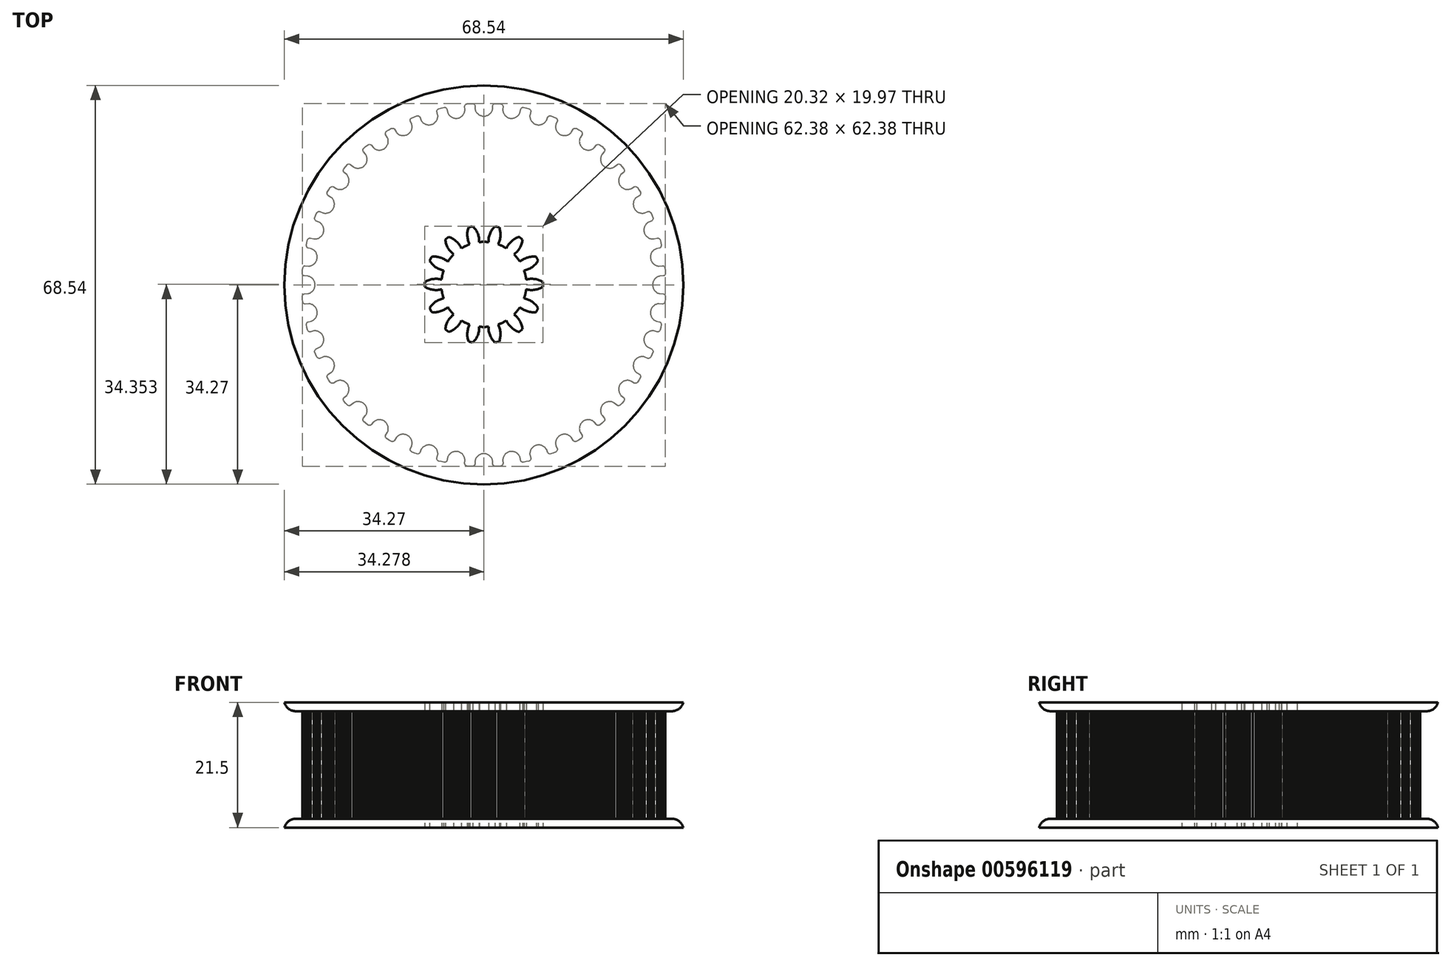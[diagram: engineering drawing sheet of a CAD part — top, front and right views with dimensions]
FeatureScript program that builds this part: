
annotation { "Feature Type Name" : "Feature", "Feature Type Description" : "" }
export const myFeature = defineFeature(function(context is Context, id is Id, definition is map)
    precondition{}
    {
        {
            assignVariable(context, id + "F0", {"name" : "totalThick", "anyValue" : 21.5});
        }
        {
            assignVariable(context, id + "F1", {"name" : "idlerThick", "anyValue" : 1.5});
        }
        {
            assignVariable(context, id + "F2", {"name" : "filletSize", "anyValue" : 2});
        }
        {
            var Q0;
            Q0=qCreatedBy(makeId("Top.planeOp"),FACE);
            var sketch = newSketch(context, id + "F3", { "sketchPlane" : qUnion([Q0])});
            skLineSegment(sketch, "E0", {"start": v(2.45, -31.16) * mm, "end": v(2.94, -31.12) * mm});
            skLineSegment(sketch, "E1", {"start": v(2.94, -31.12) * mm, "end": v(3.07, -31.07) * mm});
            skLineSegment(sketch, "E2", {"start": v(3.07, -31.07) * mm, "end": v(3.19, -30.98) * mm});
            skLineSegment(sketch, "E3", {"start": v(3.19, -30.98) * mm, "end": v(3.27, -30.85) * mm});
            skLineSegment(sketch, "E4", {"start": v(3.27, -30.85) * mm, "end": v(3.3, -30.7) * mm});
            skLineSegment(sketch, "E5", {"start": v(3.3, -30.7) * mm, "end": v(3.25, -30.1) * mm});
            skLineSegment(sketch, "E6", {"start": v(3.25, -30.1) * mm, "end": v(3.26, -29.97) * mm});
            skLineSegment(sketch, "E7", {"start": v(3.26, -29.97) * mm, "end": v(3.28, -29.84) * mm});
            skLineSegment(sketch, "E8", {"start": v(3.28, -29.84) * mm, "end": v(3.3, -29.71) * mm});
            skLineSegment(sketch, "E9", {"start": v(3.3, -29.71) * mm, "end": v(3.35, -29.6) * mm});
            skLineSegment(sketch, "E10", {"start": v(3.35, -29.6) * mm, "end": v(3.4, -29.47) * mm});
            skLineSegment(sketch, "E11", {"start": v(3.4, -29.47) * mm, "end": v(3.47, -29.36) * mm});
            skLineSegment(sketch, "E12", {"start": v(3.47, -29.36) * mm, "end": v(3.54, -29.26) * mm});
            skLineSegment(sketch, "E13", {"start": v(3.54, -29.26) * mm, "end": v(3.62, -29.16) * mm});
            skLineSegment(sketch, "E14", {"start": v(3.62, -29.16) * mm, "end": v(3.71, -29.06) * mm});
            skLineSegment(sketch, "E15", {"start": v(3.71, -29.06) * mm, "end": v(3.81, -28.98) * mm});
            skLineSegment(sketch, "E16", {"start": v(3.81, -28.98) * mm, "end": v(3.92, -28.9) * mm});
            skLineSegment(sketch, "E17", {"start": v(3.92, -28.9) * mm, "end": v(4.03, -28.83) * mm});
            skLineSegment(sketch, "E18", {"start": v(4.03, -28.83) * mm, "end": v(4.15, -28.77) * mm});
            skLineSegment(sketch, "E19", {"start": v(4.15, -28.77) * mm, "end": v(4.27, -28.71) * mm});
            skLineSegment(sketch, "E20", {"start": v(4.27, -28.71) * mm, "end": v(4.4, -28.67) * mm});
            skLineSegment(sketch, "E21", {"start": v(4.4, -28.67) * mm, "end": v(4.54, -28.64) * mm});
            skLineSegment(sketch, "E22", {"start": v(4.54, -28.64) * mm, "end": v(4.67, -28.63) * mm});
            skLineSegment(sketch, "E23", {"start": v(4.67, -28.63) * mm, "end": v(4.81, -28.63) * mm});
            skLineSegment(sketch, "E24", {"start": v(4.81, -28.63) * mm, "end": v(4.95, -28.64) * mm});
            skLineSegment(sketch, "E25", {"start": v(4.95, -28.64) * mm, "end": v(5.08, -28.66) * mm});
            skLineSegment(sketch, "E26", {"start": v(5.08, -28.66) * mm, "end": v(5.2, -28.7) * mm});
            skLineSegment(sketch, "E27", {"start": v(5.2, -28.7) * mm, "end": v(5.33, -28.74) * mm});
            skLineSegment(sketch, "E28", {"start": v(5.33, -28.74) * mm, "end": v(5.45, -28.79) * mm});
            skLineSegment(sketch, "E29", {"start": v(5.45, -28.79) * mm, "end": v(5.56, -28.85) * mm});
            skLineSegment(sketch, "E30", {"start": v(5.56, -28.85) * mm, "end": v(5.67, -28.92) * mm});
            skLineSegment(sketch, "E31", {"start": v(5.67, -28.92) * mm, "end": v(5.77, -29) * mm});
            skLineSegment(sketch, "E32", {"start": v(5.77, -29) * mm, "end": v(5.87, -29.08) * mm});
            skLineSegment(sketch, "E33", {"start": v(5.87, -29.08) * mm, "end": v(5.96, -29.18) * mm});
            skLineSegment(sketch, "E34", {"start": v(5.96, -29.18) * mm, "end": v(6.03, -29.28) * mm});
            skLineSegment(sketch, "E35", {"start": v(6.03, -29.28) * mm, "end": v(6.1, -29.39) * mm});
            skLineSegment(sketch, "E36", {"start": v(6.1, -29.39) * mm, "end": v(6.16, -29.5) * mm});
            skLineSegment(sketch, "E37", {"start": v(6.16, -29.5) * mm, "end": v(6.21, -29.63) * mm});
            skLineSegment(sketch, "E38", {"start": v(6.21, -29.63) * mm, "end": v(6.35, -30.22) * mm});
            skLineSegment(sketch, "E39", {"start": v(6.35, -30.22) * mm, "end": v(6.43, -30.35) * mm});
            skLineSegment(sketch, "E40", {"start": v(6.43, -30.35) * mm, "end": v(6.54, -30.45) * mm});
            skLineSegment(sketch, "E41", {"start": v(6.54, -30.45) * mm, "end": v(6.69, -30.5) * mm});
            skLineSegment(sketch, "E42", {"start": v(6.69, -30.5) * mm, "end": v(6.82, -30.5) * mm});
            skLineSegment(sketch, "E43", {"start": v(6.82, -30.5) * mm, "end": v(7.3, -30.4) * mm});
            skLineSegment(sketch, "E44", {"start": v(7.3, -30.4) * mm, "end": v(7.77, -30.27) * mm});
            skLineSegment(sketch, "E45", {"start": v(7.77, -30.27) * mm, "end": v(7.89, -30.21) * mm});
            skLineSegment(sketch, "E46", {"start": v(7.89, -30.21) * mm, "end": v(8, -30.1) * mm});
            skLineSegment(sketch, "E47", {"start": v(8, -30.1) * mm, "end": v(8.05, -29.96) * mm});
            skLineSegment(sketch, "E48", {"start": v(8.05, -29.96) * mm, "end": v(8.06, -29.8) * mm});
            skLineSegment(sketch, "E49", {"start": v(8.06, -29.8) * mm, "end": v(7.91, -29.22) * mm});
            skLineSegment(sketch, "E50", {"start": v(7.91, -29.22) * mm, "end": v(7.9, -29.09) * mm});
            skLineSegment(sketch, "E51", {"start": v(7.9, -29.09) * mm, "end": v(7.9, -28.96) * mm});
            skLineSegment(sketch, "E52", {"start": v(7.9, -28.96) * mm, "end": v(7.92, -28.83) * mm});
            skLineSegment(sketch, "E53", {"start": v(7.92, -28.83) * mm, "end": v(7.94, -28.7) * mm});
            skLineSegment(sketch, "E54", {"start": v(7.94, -28.7) * mm, "end": v(7.97, -28.58) * mm});
            skLineSegment(sketch, "E55", {"start": v(7.97, -28.58) * mm, "end": v(8.02, -28.46) * mm});
            skLineSegment(sketch, "E56", {"start": v(8.02, -28.46) * mm, "end": v(8.07, -28.34) * mm});
            skLineSegment(sketch, "E57", {"start": v(8.07, -28.34) * mm, "end": v(8.14, -28.23) * mm});
            skLineSegment(sketch, "E58", {"start": v(8.14, -28.23) * mm, "end": v(8.21, -28.12) * mm});
            skLineSegment(sketch, "E59", {"start": v(8.21, -28.12) * mm, "end": v(8.3, -28.02) * mm});
            skLineSegment(sketch, "E60", {"start": v(8.3, -28.02) * mm, "end": v(8.39, -27.93) * mm});
            skLineSegment(sketch, "E61", {"start": v(8.39, -27.93) * mm, "end": v(8.49, -27.84) * mm});
            skLineSegment(sketch, "E62", {"start": v(8.49, -27.84) * mm, "end": v(8.6, -27.76) * mm});
            skLineSegment(sketch, "E63", {"start": v(8.6, -27.76) * mm, "end": v(8.71, -27.7) * mm});
            skLineSegment(sketch, "E64", {"start": v(8.71, -27.7) * mm, "end": v(8.83, -27.63) * mm});
            skLineSegment(sketch, "E65", {"start": v(8.83, -27.63) * mm, "end": v(8.96, -27.58) * mm});
            skLineSegment(sketch, "E66", {"start": v(8.96, -27.58) * mm, "end": v(9.1, -27.55) * mm});
            skLineSegment(sketch, "E67", {"start": v(9.1, -27.55) * mm, "end": v(9.23, -27.52) * mm});
            skLineSegment(sketch, "E68", {"start": v(9.23, -27.52) * mm, "end": v(9.36, -27.51) * mm});
            skLineSegment(sketch, "E69", {"start": v(9.36, -27.51) * mm, "end": v(9.5, -27.51) * mm});
            skLineSegment(sketch, "E70", {"start": v(9.5, -27.51) * mm, "end": v(9.63, -27.53) * mm});
            skLineSegment(sketch, "E71", {"start": v(9.63, -27.53) * mm, "end": v(9.76, -27.55) * mm});
            skLineSegment(sketch, "E72", {"start": v(9.76, -27.55) * mm, "end": v(9.89, -27.58) * mm});
            skLineSegment(sketch, "E73", {"start": v(9.89, -27.58) * mm, "end": v(10, -27.62) * mm});
            skLineSegment(sketch, "E74", {"start": v(10, -27.62) * mm, "end": v(10.13, -27.67) * mm});
            skLineSegment(sketch, "E75", {"start": v(10.13, -27.67) * mm, "end": v(10.24, -27.74) * mm});
            skLineSegment(sketch, "E76", {"start": v(10.24, -27.74) * mm, "end": v(10.35, -27.8) * mm});
            skLineSegment(sketch, "E77", {"start": v(10.35, -27.8) * mm, "end": v(10.45, -27.89) * mm});
            skLineSegment(sketch, "E78", {"start": v(10.45, -27.89) * mm, "end": v(10.54, -27.98) * mm});
            skLineSegment(sketch, "E79", {"start": v(10.54, -27.98) * mm, "end": v(10.63, -28.07) * mm});
            skLineSegment(sketch, "E80", {"start": v(10.63, -28.07) * mm, "end": v(10.7, -28.18) * mm});
            skLineSegment(sketch, "E81", {"start": v(10.7, -28.18) * mm, "end": v(10.77, -28.3) * mm});
            skLineSegment(sketch, "E82", {"start": v(10.77, -28.3) * mm, "end": v(11, -28.85) * mm});
            skLineSegment(sketch, "E83", {"start": v(11, -28.85) * mm, "end": v(11.1, -28.97) * mm});
            skLineSegment(sketch, "E84", {"start": v(11.1, -28.97) * mm, "end": v(11.23, -29.05) * mm});
            skLineSegment(sketch, "E85", {"start": v(11.23, -29.05) * mm, "end": v(11.38, -29.08) * mm});
            skLineSegment(sketch, "E86", {"start": v(11.38, -29.08) * mm, "end": v(11.5, -29.06) * mm});
            skLineSegment(sketch, "E87", {"start": v(11.5, -29.06) * mm, "end": v(11.96, -28.88) * mm});
            skLineSegment(sketch, "E88", {"start": v(11.96, -28.88) * mm, "end": v(12.4, -28.68) * mm});
            skLineSegment(sketch, "E89", {"start": v(12.4, -28.68) * mm, "end": v(12.52, -28.6) * mm});
            skLineSegment(sketch, "E90", {"start": v(12.52, -28.6) * mm, "end": v(12.6, -28.48) * mm});
            skLineSegment(sketch, "E91", {"start": v(12.6, -28.48) * mm, "end": v(12.64, -28.33) * mm});
            skLineSegment(sketch, "E92", {"start": v(12.64, -28.33) * mm, "end": v(12.62, -28.18) * mm});
            skLineSegment(sketch, "E93", {"start": v(12.62, -28.18) * mm, "end": v(12.39, -27.62) * mm});
            skLineSegment(sketch, "E94", {"start": v(12.39, -27.62) * mm, "end": v(12.36, -27.5) * mm});
            skLineSegment(sketch, "E95", {"start": v(12.36, -27.5) * mm, "end": v(12.34, -27.36) * mm});
            skLineSegment(sketch, "E96", {"start": v(12.34, -27.36) * mm, "end": v(12.33, -27.24) * mm});
            skLineSegment(sketch, "E97", {"start": v(12.33, -27.24) * mm, "end": v(12.33, -27.1) * mm});
            skLineSegment(sketch, "E98", {"start": v(12.33, -27.1) * mm, "end": v(12.35, -26.98) * mm});
            skLineSegment(sketch, "E99", {"start": v(12.35, -26.98) * mm, "end": v(12.37, -26.85) * mm});
            skLineSegment(sketch, "E100", {"start": v(12.37, -26.85) * mm, "end": v(12.4, -26.73) * mm});
            skLineSegment(sketch, "E101", {"start": v(12.4, -26.73) * mm, "end": v(12.46, -26.6) * mm});
            skLineSegment(sketch, "E102", {"start": v(12.46, -26.6) * mm, "end": v(12.51, -26.5) * mm});
            skLineSegment(sketch, "E103", {"start": v(12.51, -26.5) * mm, "end": v(12.58, -26.38) * mm});
            skLineSegment(sketch, "E104", {"start": v(12.58, -26.38) * mm, "end": v(12.65, -26.27) * mm});
            skLineSegment(sketch, "E105", {"start": v(12.65, -26.27) * mm, "end": v(12.74, -26.17) * mm});
            skLineSegment(sketch, "E106", {"start": v(12.74, -26.17) * mm, "end": v(12.83, -26.08) * mm});
            skLineSegment(sketch, "E107", {"start": v(12.83, -26.08) * mm, "end": v(12.94, -25.99) * mm});
            skLineSegment(sketch, "E108", {"start": v(12.94, -25.99) * mm, "end": v(13.05, -25.9) * mm});
            skLineSegment(sketch, "E109", {"start": v(13.05, -25.9) * mm, "end": v(13.16, -25.84) * mm});
            skLineSegment(sketch, "E110", {"start": v(13.16, -25.84) * mm, "end": v(13.3, -25.78) * mm});
            skLineSegment(sketch, "E111", {"start": v(13.3, -25.78) * mm, "end": v(13.42, -25.74) * mm});
            skLineSegment(sketch, "E112", {"start": v(13.42, -25.74) * mm, "end": v(13.55, -25.7) * mm});
            skLineSegment(sketch, "E113", {"start": v(13.55, -25.7) * mm, "end": v(13.69, -25.69) * mm});
            skLineSegment(sketch, "E114", {"start": v(13.69, -25.69) * mm, "end": v(13.82, -25.68) * mm});
            skLineSegment(sketch, "E115", {"start": v(13.82, -25.68) * mm, "end": v(13.95, -25.68) * mm});
            skLineSegment(sketch, "E116", {"start": v(13.95, -25.68) * mm, "end": v(14.08, -25.7) * mm});
            skLineSegment(sketch, "E117", {"start": v(14.08, -25.7) * mm, "end": v(14.2, -25.72) * mm});
            skLineSegment(sketch, "E118", {"start": v(14.2, -25.72) * mm, "end": v(14.33, -25.75) * mm});
            skLineSegment(sketch, "E119", {"start": v(14.33, -25.75) * mm, "end": v(14.45, -25.8) * mm});
            skLineSegment(sketch, "E120", {"start": v(14.45, -25.8) * mm, "end": v(14.57, -25.85) * mm});
            skLineSegment(sketch, "E121", {"start": v(14.57, -25.85) * mm, "end": v(14.68, -25.9) * mm});
            skLineSegment(sketch, "E122", {"start": v(14.68, -25.9) * mm, "end": v(14.79, -25.98) * mm});
            skLineSegment(sketch, "E123", {"start": v(14.79, -25.98) * mm, "end": v(14.89, -26.06) * mm});
            skLineSegment(sketch, "E124", {"start": v(14.89, -26.06) * mm, "end": v(14.98, -26.16) * mm});
            skLineSegment(sketch, "E125", {"start": v(14.98, -26.16) * mm, "end": v(15.07, -26.26) * mm});
            skLineSegment(sketch, "E126", {"start": v(15.07, -26.26) * mm, "end": v(15.38, -26.78) * mm});
            skLineSegment(sketch, "E127", {"start": v(15.38, -26.78) * mm, "end": v(15.5, -26.88) * mm});
            skLineSegment(sketch, "E128", {"start": v(15.5, -26.88) * mm, "end": v(15.63, -26.93) * mm});
            skLineSegment(sketch, "E129", {"start": v(15.63, -26.93) * mm, "end": v(15.78, -26.94) * mm});
            skLineSegment(sketch, "E130", {"start": v(15.78, -26.94) * mm, "end": v(15.91, -26.9) * mm});
            skLineSegment(sketch, "E131", {"start": v(15.91, -26.9) * mm, "end": v(16.33, -26.65) * mm});
            skLineSegment(sketch, "E132", {"start": v(16.33, -26.65) * mm, "end": v(16.74, -26.4) * mm});
            skLineSegment(sketch, "E133", {"start": v(16.74, -26.4) * mm, "end": v(16.84, -26.3) * mm});
            skLineSegment(sketch, "E134", {"start": v(16.84, -26.3) * mm, "end": v(16.9, -26.16) * mm});
            skLineSegment(sketch, "E135", {"start": v(16.9, -26.16) * mm, "end": v(16.92, -26) * mm});
            skLineSegment(sketch, "E136", {"start": v(16.92, -26) * mm, "end": v(16.88, -25.86) * mm});
            skLineSegment(sketch, "E137", {"start": v(16.88, -25.86) * mm, "end": v(16.56, -25.34) * mm});
            skLineSegment(sketch, "E138", {"start": v(16.56, -25.34) * mm, "end": v(16.5, -25.22) * mm});
            skLineSegment(sketch, "E139", {"start": v(16.5, -25.22) * mm, "end": v(16.47, -25.1) * mm});
            skLineSegment(sketch, "E140", {"start": v(16.47, -25.1) * mm, "end": v(16.44, -24.97) * mm});
            skLineSegment(sketch, "E141", {"start": v(16.44, -24.97) * mm, "end": v(16.42, -24.84) * mm});
            skLineSegment(sketch, "E142", {"start": v(16.42, -24.84) * mm, "end": v(16.42, -24.71) * mm});
            skLineSegment(sketch, "E143", {"start": v(16.42, -24.71) * mm, "end": v(16.42, -24.59) * mm});
            skLineSegment(sketch, "E144", {"start": v(16.42, -24.59) * mm, "end": v(16.44, -24.46) * mm});
            skLineSegment(sketch, "E145", {"start": v(16.44, -24.46) * mm, "end": v(16.46, -24.33) * mm});
            skLineSegment(sketch, "E146", {"start": v(16.46, -24.33) * mm, "end": v(16.5, -24.2) * mm});
            skLineSegment(sketch, "E147", {"start": v(16.5, -24.2) * mm, "end": v(16.55, -24.09) * mm});
            skLineSegment(sketch, "E148", {"start": v(16.55, -24.09) * mm, "end": v(16.6, -23.97) * mm});
            skLineSegment(sketch, "E149", {"start": v(16.6, -23.97) * mm, "end": v(16.68, -23.86) * mm});
            skLineSegment(sketch, "E150", {"start": v(16.68, -23.86) * mm, "end": v(16.75, -23.75) * mm});
            skLineSegment(sketch, "E151", {"start": v(16.75, -23.75) * mm, "end": v(16.84, -23.65) * mm});
            skLineSegment(sketch, "E152", {"start": v(16.84, -23.65) * mm, "end": v(16.94, -23.55) * mm});
            skLineSegment(sketch, "E153", {"start": v(16.94, -23.55) * mm, "end": v(17.04, -23.46) * mm});
            skLineSegment(sketch, "E154", {"start": v(17.04, -23.46) * mm, "end": v(17.16, -23.39) * mm});
            skLineSegment(sketch, "E155", {"start": v(17.16, -23.39) * mm, "end": v(17.28, -23.32) * mm});
            skLineSegment(sketch, "E156", {"start": v(17.28, -23.32) * mm, "end": v(17.4, -23.27) * mm});
            skLineSegment(sketch, "E157", {"start": v(17.4, -23.27) * mm, "end": v(17.54, -23.23) * mm});
            skLineSegment(sketch, "E158", {"start": v(17.54, -23.23) * mm, "end": v(17.66, -23.2) * mm});
            skLineSegment(sketch, "E159", {"start": v(17.66, -23.2) * mm, "end": v(17.8, -23.18) * mm});
            skLineSegment(sketch, "E160", {"start": v(17.8, -23.18) * mm, "end": v(17.92, -23.18) * mm});
            skLineSegment(sketch, "E161", {"start": v(17.92, -23.18) * mm, "end": v(18.05, -23.18) * mm});
            skLineSegment(sketch, "E162", {"start": v(18.05, -23.18) * mm, "end": v(18.18, -23.2) * mm});
            skLineSegment(sketch, "E163", {"start": v(18.18, -23.2) * mm, "end": v(18.3, -23.21) * mm});
            skLineSegment(sketch, "E164", {"start": v(18.3, -23.21) * mm, "end": v(18.43, -23.25) * mm});
            skLineSegment(sketch, "E165", {"start": v(18.43, -23.25) * mm, "end": v(18.55, -23.3) * mm});
            skLineSegment(sketch, "E166", {"start": v(18.55, -23.3) * mm, "end": v(18.67, -23.35) * mm});
            skLineSegment(sketch, "E167", {"start": v(18.67, -23.35) * mm, "end": v(18.78, -23.41) * mm});
            skLineSegment(sketch, "E168", {"start": v(18.78, -23.41) * mm, "end": v(18.89, -23.5) * mm});
            skLineSegment(sketch, "E169", {"start": v(18.89, -23.5) * mm, "end": v(18.99, -23.58) * mm});
            skLineSegment(sketch, "E170", {"start": v(18.99, -23.58) * mm, "end": v(19.38, -24.04) * mm});
            skLineSegment(sketch, "E171", {"start": v(19.38, -24.04) * mm, "end": v(19.5, -24.13) * mm});
            skLineSegment(sketch, "E172", {"start": v(19.5, -24.13) * mm, "end": v(19.65, -24.16) * mm});
            skLineSegment(sketch, "E173", {"start": v(19.65, -24.16) * mm, "end": v(19.8, -24.14) * mm});
            skLineSegment(sketch, "E174", {"start": v(19.8, -24.14) * mm, "end": v(19.92, -24.08) * mm});
            skLineSegment(sketch, "E175", {"start": v(19.92, -24.08) * mm, "end": v(20.3, -23.77) * mm});
            skLineSegment(sketch, "E176", {"start": v(20.3, -23.77) * mm, "end": v(20.67, -23.45) * mm});
            skLineSegment(sketch, "E177", {"start": v(20.67, -23.45) * mm, "end": v(20.74, -23.34) * mm});
            skLineSegment(sketch, "E178", {"start": v(20.74, -23.34) * mm, "end": v(20.79, -23.19) * mm});
            skLineSegment(sketch, "E179", {"start": v(20.79, -23.19) * mm, "end": v(20.78, -23.04) * mm});
            skLineSegment(sketch, "E180", {"start": v(20.78, -23.04) * mm, "end": v(20.72, -22.9) * mm});
            skLineSegment(sketch, "E181", {"start": v(20.72, -22.9) * mm, "end": v(20.32, -22.44) * mm});
            skLineSegment(sketch, "E182", {"start": v(20.32, -22.44) * mm, "end": v(20.25, -22.33) * mm});
            skLineSegment(sketch, "E183", {"start": v(20.25, -22.33) * mm, "end": v(20.19, -22.21) * mm});
            skLineSegment(sketch, "E184", {"start": v(20.19, -22.21) * mm, "end": v(20.14, -22.1) * mm});
            skLineSegment(sketch, "E185", {"start": v(20.14, -22.1) * mm, "end": v(20.1, -21.97) * mm});
            skLineSegment(sketch, "E186", {"start": v(20.1, -21.97) * mm, "end": v(20.08, -21.84) * mm});
            skLineSegment(sketch, "E187", {"start": v(20.08, -21.84) * mm, "end": v(20.07, -21.72) * mm});
            skLineSegment(sketch, "E188", {"start": v(20.07, -21.72) * mm, "end": v(20.06, -21.59) * mm});
            skLineSegment(sketch, "E189", {"start": v(20.06, -21.59) * mm, "end": v(20.07, -21.46) * mm});
            skLineSegment(sketch, "E190", {"start": v(20.07, -21.46) * mm, "end": v(20.09, -21.33) * mm});
            skLineSegment(sketch, "E191", {"start": v(20.09, -21.33) * mm, "end": v(20.11, -21.2) * mm});
            skLineSegment(sketch, "E192", {"start": v(20.11, -21.2) * mm, "end": v(20.15, -21.08) * mm});
            skLineSegment(sketch, "E193", {"start": v(20.15, -21.08) * mm, "end": v(20.2, -20.95) * mm});
            skLineSegment(sketch, "E194", {"start": v(20.2, -20.95) * mm, "end": v(20.26, -20.84) * mm});
            skLineSegment(sketch, "E195", {"start": v(20.26, -20.84) * mm, "end": v(20.33, -20.72) * mm});
            skLineSegment(sketch, "E196", {"start": v(20.33, -20.72) * mm, "end": v(20.41, -20.6) * mm});
            skLineSegment(sketch, "E197", {"start": v(20.41, -20.6) * mm, "end": v(20.5, -20.5) * mm});
            skLineSegment(sketch, "E198", {"start": v(20.5, -20.5) * mm, "end": v(20.6, -20.41) * mm});
            skLineSegment(sketch, "E199", {"start": v(20.6, -20.41) * mm, "end": v(20.72, -20.33) * mm});
            skLineSegment(sketch, "E200", {"start": v(20.72, -20.33) * mm, "end": v(20.83, -20.26) * mm});
            skLineSegment(sketch, "E201", {"start": v(20.83, -20.26) * mm, "end": v(20.95, -20.2) * mm});
            skLineSegment(sketch, "E202", {"start": v(20.95, -20.2) * mm, "end": v(21.08, -20.15) * mm});
            skLineSegment(sketch, "E203", {"start": v(21.08, -20.15) * mm, "end": v(21.2, -20.11) * mm});
            skLineSegment(sketch, "E204", {"start": v(21.2, -20.11) * mm, "end": v(21.33, -20.09) * mm});
            skLineSegment(sketch, "E205", {"start": v(21.33, -20.09) * mm, "end": v(21.46, -20.07) * mm});
            skLineSegment(sketch, "E206", {"start": v(21.46, -20.07) * mm, "end": v(21.59, -20.06) * mm});
            skLineSegment(sketch, "E207", {"start": v(21.59, -20.06) * mm, "end": v(21.72, -20.06) * mm});
            skLineSegment(sketch, "E208", {"start": v(21.72, -20.06) * mm, "end": v(21.84, -20.08) * mm});
            skLineSegment(sketch, "E209", {"start": v(21.84, -20.08) * mm, "end": v(21.97, -20.1) * mm});
            skLineSegment(sketch, "E210", {"start": v(21.97, -20.1) * mm, "end": v(22.1, -20.14) * mm});
            skLineSegment(sketch, "E211", {"start": v(22.1, -20.14) * mm, "end": v(22.21, -20.19) * mm});
            skLineSegment(sketch, "E212", {"start": v(22.21, -20.19) * mm, "end": v(22.33, -20.25) * mm});
            skLineSegment(sketch, "E213", {"start": v(22.33, -20.25) * mm, "end": v(22.44, -20.32) * mm});
            skLineSegment(sketch, "E214", {"start": v(22.44, -20.32) * mm, "end": v(22.9, -20.72) * mm});
            skLineSegment(sketch, "E215", {"start": v(22.9, -20.72) * mm, "end": v(23.04, -20.78) * mm});
            skLineSegment(sketch, "E216", {"start": v(23.04, -20.78) * mm, "end": v(23.19, -20.79) * mm});
            skLineSegment(sketch, "E217", {"start": v(23.19, -20.79) * mm, "end": v(23.34, -20.74) * mm});
            skLineSegment(sketch, "E218", {"start": v(23.34, -20.74) * mm, "end": v(23.45, -20.67) * mm});
            skLineSegment(sketch, "E219", {"start": v(23.45, -20.67) * mm, "end": v(23.77, -20.3) * mm});
            skLineSegment(sketch, "E220", {"start": v(23.77, -20.3) * mm, "end": v(24.08, -19.92) * mm});
            skLineSegment(sketch, "E221", {"start": v(24.08, -19.92) * mm, "end": v(24.14, -19.8) * mm});
            skLineSegment(sketch, "E222", {"start": v(24.14, -19.8) * mm, "end": v(24.16, -19.65) * mm});
            skLineSegment(sketch, "E223", {"start": v(24.16, -19.65) * mm, "end": v(24.13, -19.5) * mm});
            skLineSegment(sketch, "E224", {"start": v(24.13, -19.5) * mm, "end": v(24.04, -19.38) * mm});
            skLineSegment(sketch, "E225", {"start": v(24.04, -19.38) * mm, "end": v(23.58, -18.99) * mm});
            skLineSegment(sketch, "E226", {"start": v(23.58, -18.99) * mm, "end": v(23.5, -18.89) * mm});
            skLineSegment(sketch, "E227", {"start": v(23.5, -18.89) * mm, "end": v(23.42, -18.78) * mm});
            skLineSegment(sketch, "E228", {"start": v(23.42, -18.78) * mm, "end": v(23.35, -18.67) * mm});
            skLineSegment(sketch, "E229", {"start": v(23.35, -18.67) * mm, "end": v(23.3, -18.55) * mm});
            skLineSegment(sketch, "E230", {"start": v(23.3, -18.55) * mm, "end": v(23.25, -18.43) * mm});
            skLineSegment(sketch, "E231", {"start": v(23.25, -18.43) * mm, "end": v(23.21, -18.3) * mm});
            skLineSegment(sketch, "E232", {"start": v(23.21, -18.3) * mm, "end": v(23.2, -18.18) * mm});
            skLineSegment(sketch, "E233", {"start": v(23.2, -18.18) * mm, "end": v(23.18, -18.05) * mm});
            skLineSegment(sketch, "E234", {"start": v(23.18, -18.05) * mm, "end": v(23.18, -17.92) * mm});
            skLineSegment(sketch, "E235", {"start": v(23.18, -17.92) * mm, "end": v(23.18, -17.8) * mm});
            skLineSegment(sketch, "E236", {"start": v(23.18, -17.8) * mm, "end": v(23.2, -17.66) * mm});
            skLineSegment(sketch, "E237", {"start": v(23.2, -17.66) * mm, "end": v(23.23, -17.54) * mm});
            skLineSegment(sketch, "E238", {"start": v(23.23, -17.54) * mm, "end": v(23.27, -17.4) * mm});
            skLineSegment(sketch, "E239", {"start": v(23.27, -17.4) * mm, "end": v(23.32, -17.28) * mm});
            skLineSegment(sketch, "E240", {"start": v(23.32, -17.28) * mm, "end": v(23.39, -17.16) * mm});
            skLineSegment(sketch, "E241", {"start": v(23.39, -17.16) * mm, "end": v(23.46, -17.04) * mm});
            skLineSegment(sketch, "E242", {"start": v(23.46, -17.04) * mm, "end": v(23.55, -16.94) * mm});
            skLineSegment(sketch, "E243", {"start": v(23.55, -16.94) * mm, "end": v(23.65, -16.84) * mm});
            skLineSegment(sketch, "E244", {"start": v(23.65, -16.84) * mm, "end": v(23.75, -16.75) * mm});
            skLineSegment(sketch, "E245", {"start": v(23.75, -16.75) * mm, "end": v(23.86, -16.68) * mm});
            skLineSegment(sketch, "E246", {"start": v(23.86, -16.68) * mm, "end": v(23.97, -16.6) * mm});
            skLineSegment(sketch, "E247", {"start": v(23.97, -16.6) * mm, "end": v(24.09, -16.55) * mm});
            skLineSegment(sketch, "E248", {"start": v(24.09, -16.55) * mm, "end": v(24.2, -16.5) * mm});
            skLineSegment(sketch, "E249", {"start": v(24.2, -16.5) * mm, "end": v(24.33, -16.46) * mm});
            skLineSegment(sketch, "E250", {"start": v(24.33, -16.46) * mm, "end": v(24.46, -16.44) * mm});
            skLineSegment(sketch, "E251", {"start": v(24.46, -16.44) * mm, "end": v(24.59, -16.42) * mm});
            skLineSegment(sketch, "E252", {"start": v(24.59, -16.42) * mm, "end": v(24.71, -16.42) * mm});
            skLineSegment(sketch, "E253", {"start": v(24.71, -16.42) * mm, "end": v(24.84, -16.42) * mm});
            skLineSegment(sketch, "E254", {"start": v(24.84, -16.42) * mm, "end": v(24.97, -16.44) * mm});
            skLineSegment(sketch, "E255", {"start": v(24.97, -16.44) * mm, "end": v(25.1, -16.47) * mm});
            skLineSegment(sketch, "E256", {"start": v(25.1, -16.47) * mm, "end": v(25.22, -16.5) * mm});
            skLineSegment(sketch, "E257", {"start": v(25.22, -16.5) * mm, "end": v(25.34, -16.56) * mm});
            skLineSegment(sketch, "E258", {"start": v(25.34, -16.56) * mm, "end": v(25.86, -16.88) * mm});
            skLineSegment(sketch, "E259", {"start": v(25.86, -16.88) * mm, "end": v(26, -16.92) * mm});
            skLineSegment(sketch, "E260", {"start": v(26, -16.92) * mm, "end": v(26.16, -16.9) * mm});
            skLineSegment(sketch, "E261", {"start": v(26.16, -16.9) * mm, "end": v(26.3, -16.84) * mm});
            skLineSegment(sketch, "E262", {"start": v(26.3, -16.84) * mm, "end": v(26.4, -16.74) * mm});
            skLineSegment(sketch, "E263", {"start": v(26.4, -16.74) * mm, "end": v(26.65, -16.33) * mm});
            skLineSegment(sketch, "E264", {"start": v(26.65, -16.33) * mm, "end": v(26.9, -15.91) * mm});
            skLineSegment(sketch, "E265", {"start": v(26.9, -15.91) * mm, "end": v(26.94, -15.78) * mm});
            skLineSegment(sketch, "E266", {"start": v(26.94, -15.78) * mm, "end": v(26.93, -15.63) * mm});
            skLineSegment(sketch, "E267", {"start": v(26.93, -15.63) * mm, "end": v(26.88, -15.5) * mm});
            skLineSegment(sketch, "E268", {"start": v(26.88, -15.5) * mm, "end": v(26.78, -15.38) * mm});
            skLineSegment(sketch, "E269", {"start": v(26.78, -15.38) * mm, "end": v(26.26, -15.07) * mm});
            skLineSegment(sketch, "E270", {"start": v(26.26, -15.07) * mm, "end": v(26.16, -14.98) * mm});
            skLineSegment(sketch, "E271", {"start": v(26.16, -14.98) * mm, "end": v(26.06, -14.89) * mm});
            skLineSegment(sketch, "E272", {"start": v(26.06, -14.89) * mm, "end": v(25.98, -14.79) * mm});
            skLineSegment(sketch, "E273", {"start": v(25.98, -14.79) * mm, "end": v(25.9, -14.68) * mm});
            skLineSegment(sketch, "E274", {"start": v(25.9, -14.68) * mm, "end": v(25.85, -14.57) * mm});
            skLineSegment(sketch, "E275", {"start": v(25.85, -14.57) * mm, "end": v(25.8, -14.45) * mm});
            skLineSegment(sketch, "E276", {"start": v(25.8, -14.45) * mm, "end": v(25.75, -14.33) * mm});
            skLineSegment(sketch, "E277", {"start": v(25.75, -14.33) * mm, "end": v(25.72, -14.2) * mm});
            skLineSegment(sketch, "E278", {"start": v(25.72, -14.2) * mm, "end": v(25.7, -14.08) * mm});
            skLineSegment(sketch, "E279", {"start": v(25.7, -14.08) * mm, "end": v(25.68, -13.95) * mm});
            skLineSegment(sketch, "E280", {"start": v(25.68, -13.95) * mm, "end": v(25.68, -13.82) * mm});
            skLineSegment(sketch, "E281", {"start": v(25.68, -13.82) * mm, "end": v(25.69, -13.69) * mm});
            skLineSegment(sketch, "E282", {"start": v(25.69, -13.69) * mm, "end": v(25.7, -13.55) * mm});
            skLineSegment(sketch, "E283", {"start": v(25.7, -13.55) * mm, "end": v(25.74, -13.42) * mm});
            skLineSegment(sketch, "E284", {"start": v(25.74, -13.42) * mm, "end": v(25.78, -13.3) * mm});
            skLineSegment(sketch, "E285", {"start": v(25.78, -13.3) * mm, "end": v(25.84, -13.16) * mm});
            skLineSegment(sketch, "E286", {"start": v(25.84, -13.16) * mm, "end": v(25.9, -13.05) * mm});
            skLineSegment(sketch, "E287", {"start": v(25.9, -13.05) * mm, "end": v(25.99, -12.94) * mm});
            skLineSegment(sketch, "E288", {"start": v(25.99, -12.94) * mm, "end": v(26.08, -12.83) * mm});
            skLineSegment(sketch, "E289", {"start": v(26.08, -12.83) * mm, "end": v(26.17, -12.74) * mm});
            skLineSegment(sketch, "E290", {"start": v(26.17, -12.74) * mm, "end": v(26.27, -12.65) * mm});
            skLineSegment(sketch, "E291", {"start": v(26.27, -12.65) * mm, "end": v(26.38, -12.58) * mm});
            skLineSegment(sketch, "E292", {"start": v(26.38, -12.58) * mm, "end": v(26.5, -12.51) * mm});
            skLineSegment(sketch, "E293", {"start": v(26.5, -12.51) * mm, "end": v(26.6, -12.46) * mm});
            skLineSegment(sketch, "E294", {"start": v(26.6, -12.46) * mm, "end": v(26.73, -12.4) * mm});
            skLineSegment(sketch, "E295", {"start": v(26.73, -12.4) * mm, "end": v(26.85, -12.37) * mm});
            skLineSegment(sketch, "E296", {"start": v(26.85, -12.37) * mm, "end": v(26.98, -12.35) * mm});
            skLineSegment(sketch, "E297", {"start": v(26.98, -12.35) * mm, "end": v(27.1, -12.33) * mm});
            skLineSegment(sketch, "E298", {"start": v(27.1, -12.33) * mm, "end": v(27.24, -12.33) * mm});
            skLineSegment(sketch, "E299", {"start": v(27.24, -12.33) * mm, "end": v(27.36, -12.34) * mm});
            skLineSegment(sketch, "E300", {"start": v(27.36, -12.34) * mm, "end": v(27.5, -12.36) * mm});
            skLineSegment(sketch, "E301", {"start": v(27.5, -12.36) * mm, "end": v(27.62, -12.39) * mm});
            skLineSegment(sketch, "E302", {"start": v(27.62, -12.39) * mm, "end": v(28.18, -12.62) * mm});
            skLineSegment(sketch, "E303", {"start": v(28.18, -12.62) * mm, "end": v(28.33, -12.64) * mm});
            skLineSegment(sketch, "E304", {"start": v(28.33, -12.64) * mm, "end": v(28.48, -12.6) * mm});
            skLineSegment(sketch, "E305", {"start": v(28.48, -12.6) * mm, "end": v(28.6, -12.52) * mm});
            skLineSegment(sketch, "E306", {"start": v(28.6, -12.52) * mm, "end": v(28.68, -12.4) * mm});
            skLineSegment(sketch, "E307", {"start": v(28.68, -12.4) * mm, "end": v(28.88, -11.96) * mm});
            skLineSegment(sketch, "E308", {"start": v(28.88, -11.96) * mm, "end": v(29.06, -11.5) * mm});
            skLineSegment(sketch, "E309", {"start": v(29.06, -11.5) * mm, "end": v(29.08, -11.38) * mm});
            skLineSegment(sketch, "E310", {"start": v(29.08, -11.38) * mm, "end": v(29.05, -11.23) * mm});
            skLineSegment(sketch, "E311", {"start": v(29.05, -11.23) * mm, "end": v(28.97, -11.1) * mm});
            skLineSegment(sketch, "E312", {"start": v(28.97, -11.1) * mm, "end": v(28.85, -11) * mm});
            skLineSegment(sketch, "E313", {"start": v(28.85, -11) * mm, "end": v(28.3, -10.77) * mm});
            skLineSegment(sketch, "E314", {"start": v(28.3, -10.77) * mm, "end": v(28.18, -10.7) * mm});
            skLineSegment(sketch, "E315", {"start": v(28.18, -10.7) * mm, "end": v(28.07, -10.63) * mm});
            skLineSegment(sketch, "E316", {"start": v(28.07, -10.63) * mm, "end": v(27.98, -10.54) * mm});
            skLineSegment(sketch, "E317", {"start": v(27.98, -10.54) * mm, "end": v(27.89, -10.45) * mm});
            skLineSegment(sketch, "E318", {"start": v(27.89, -10.45) * mm, "end": v(27.8, -10.35) * mm});
            skLineSegment(sketch, "E319", {"start": v(27.8, -10.35) * mm, "end": v(27.74, -10.24) * mm});
            skLineSegment(sketch, "E320", {"start": v(27.74, -10.24) * mm, "end": v(27.67, -10.13) * mm});
            skLineSegment(sketch, "E321", {"start": v(27.67, -10.13) * mm, "end": v(27.62, -10) * mm});
            skLineSegment(sketch, "E322", {"start": v(27.62, -10) * mm, "end": v(27.58, -9.89) * mm});
            skLineSegment(sketch, "E323", {"start": v(27.58, -9.89) * mm, "end": v(27.55, -9.76) * mm});
            skLineSegment(sketch, "E324", {"start": v(27.55, -9.76) * mm, "end": v(27.53, -9.63) * mm});
            skLineSegment(sketch, "E325", {"start": v(27.53, -9.63) * mm, "end": v(27.51, -9.5) * mm});
            skLineSegment(sketch, "E326", {"start": v(27.51, -9.5) * mm, "end": v(27.51, -9.36) * mm});
            skLineSegment(sketch, "E327", {"start": v(27.51, -9.36) * mm, "end": v(27.52, -9.23) * mm});
            skLineSegment(sketch, "E328", {"start": v(27.52, -9.23) * mm, "end": v(27.55, -9.1) * mm});
            skLineSegment(sketch, "E329", {"start": v(27.55, -9.1) * mm, "end": v(27.58, -8.96) * mm});
            skLineSegment(sketch, "E330", {"start": v(27.58, -8.96) * mm, "end": v(27.63, -8.83) * mm});
            skLineSegment(sketch, "E331", {"start": v(27.63, -8.83) * mm, "end": v(27.7, -8.71) * mm});
            skLineSegment(sketch, "E332", {"start": v(27.7, -8.71) * mm, "end": v(27.76, -8.6) * mm});
            skLineSegment(sketch, "E333", {"start": v(27.76, -8.6) * mm, "end": v(27.84, -8.49) * mm});
            skLineSegment(sketch, "E334", {"start": v(27.84, -8.49) * mm, "end": v(27.93, -8.39) * mm});
            skLineSegment(sketch, "E335", {"start": v(27.93, -8.39) * mm, "end": v(28.02, -8.3) * mm});
            skLineSegment(sketch, "E336", {"start": v(28.02, -8.3) * mm, "end": v(28.12, -8.21) * mm});
            skLineSegment(sketch, "E337", {"start": v(28.12, -8.21) * mm, "end": v(28.23, -8.14) * mm});
            skLineSegment(sketch, "E338", {"start": v(28.23, -8.14) * mm, "end": v(28.34, -8.07) * mm});
            skLineSegment(sketch, "E339", {"start": v(28.34, -8.07) * mm, "end": v(28.46, -8.02) * mm});
            skLineSegment(sketch, "E340", {"start": v(28.46, -8.02) * mm, "end": v(28.58, -7.97) * mm});
            skLineSegment(sketch, "E341", {"start": v(28.58, -7.97) * mm, "end": v(28.7, -7.94) * mm});
            skLineSegment(sketch, "E342", {"start": v(28.7, -7.94) * mm, "end": v(28.83, -7.92) * mm});
            skLineSegment(sketch, "E343", {"start": v(28.83, -7.92) * mm, "end": v(28.96, -7.9) * mm});
            skLineSegment(sketch, "E344", {"start": v(28.96, -7.9) * mm, "end": v(29.09, -7.9) * mm});
            skLineSegment(sketch, "E345", {"start": v(29.09, -7.9) * mm, "end": v(29.22, -7.91) * mm});
            skLineSegment(sketch, "E346", {"start": v(29.22, -7.91) * mm, "end": v(29.8, -8.06) * mm});
            skLineSegment(sketch, "E347", {"start": v(29.8, -8.06) * mm, "end": v(29.96, -8.05) * mm});
            skLineSegment(sketch, "E348", {"start": v(29.96, -8.05) * mm, "end": v(30.1, -8) * mm});
            skLineSegment(sketch, "E349", {"start": v(30.1, -8) * mm, "end": v(30.21, -7.89) * mm});
            skLineSegment(sketch, "E350", {"start": v(30.21, -7.89) * mm, "end": v(30.27, -7.77) * mm});
            skLineSegment(sketch, "E351", {"start": v(30.27, -7.77) * mm, "end": v(30.4, -7.3) * mm});
            skLineSegment(sketch, "E352", {"start": v(30.4, -7.3) * mm, "end": v(30.5, -6.82) * mm});
            skLineSegment(sketch, "E353", {"start": v(30.5, -6.82) * mm, "end": v(30.5, -6.69) * mm});
            skLineSegment(sketch, "E354", {"start": v(30.5, -6.69) * mm, "end": v(30.45, -6.54) * mm});
            skLineSegment(sketch, "E355", {"start": v(30.45, -6.54) * mm, "end": v(30.35, -6.43) * mm});
            skLineSegment(sketch, "E356", {"start": v(30.35, -6.43) * mm, "end": v(30.22, -6.35) * mm});
            skLineSegment(sketch, "E357", {"start": v(30.22, -6.35) * mm, "end": v(29.63, -6.21) * mm});
            skLineSegment(sketch, "E358", {"start": v(29.63, -6.21) * mm, "end": v(29.5, -6.16) * mm});
            skLineSegment(sketch, "E359", {"start": v(29.5, -6.16) * mm, "end": v(29.39, -6.1) * mm});
            skLineSegment(sketch, "E360", {"start": v(29.39, -6.1) * mm, "end": v(29.28, -6.03) * mm});
            skLineSegment(sketch, "E361", {"start": v(29.28, -6.03) * mm, "end": v(29.18, -5.96) * mm});
            skLineSegment(sketch, "E362", {"start": v(29.18, -5.96) * mm, "end": v(29.08, -5.87) * mm});
            skLineSegment(sketch, "E363", {"start": v(29.08, -5.87) * mm, "end": v(29, -5.77) * mm});
            skLineSegment(sketch, "E364", {"start": v(29, -5.77) * mm, "end": v(28.92, -5.67) * mm});
            skLineSegment(sketch, "E365", {"start": v(28.92, -5.67) * mm, "end": v(28.85, -5.56) * mm});
            skLineSegment(sketch, "E366", {"start": v(28.85, -5.56) * mm, "end": v(28.79, -5.45) * mm});
            skLineSegment(sketch, "E367", {"start": v(28.79, -5.45) * mm, "end": v(28.74, -5.33) * mm});
            skLineSegment(sketch, "E368", {"start": v(28.74, -5.33) * mm, "end": v(28.7, -5.2) * mm});
            skLineSegment(sketch, "E369", {"start": v(28.7, -5.2) * mm, "end": v(28.66, -5.08) * mm});
            skLineSegment(sketch, "E370", {"start": v(28.66, -5.08) * mm, "end": v(28.64, -4.95) * mm});
            skLineSegment(sketch, "E371", {"start": v(28.64, -4.95) * mm, "end": v(28.63, -4.81) * mm});
            skLineSegment(sketch, "E372", {"start": v(28.63, -4.81) * mm, "end": v(28.63, -4.67) * mm});
            skLineSegment(sketch, "E373", {"start": v(28.63, -4.67) * mm, "end": v(28.64, -4.54) * mm});
            skLineSegment(sketch, "E374", {"start": v(28.64, -4.54) * mm, "end": v(28.67, -4.4) * mm});
            skLineSegment(sketch, "E375", {"start": v(28.67, -4.4) * mm, "end": v(28.71, -4.27) * mm});
            skLineSegment(sketch, "E376", {"start": v(28.71, -4.27) * mm, "end": v(28.77, -4.15) * mm});
            skLineSegment(sketch, "E377", {"start": v(28.77, -4.15) * mm, "end": v(28.83, -4.03) * mm});
            skLineSegment(sketch, "E378", {"start": v(28.83, -4.03) * mm, "end": v(28.9, -3.92) * mm});
            skLineSegment(sketch, "E379", {"start": v(28.9, -3.92) * mm, "end": v(28.98, -3.81) * mm});
            skLineSegment(sketch, "E380", {"start": v(28.98, -3.81) * mm, "end": v(29.06, -3.71) * mm});
            skLineSegment(sketch, "E381", {"start": v(29.06, -3.71) * mm, "end": v(29.16, -3.62) * mm});
            skLineSegment(sketch, "E382", {"start": v(29.16, -3.62) * mm, "end": v(29.26, -3.54) * mm});
            skLineSegment(sketch, "E383", {"start": v(29.26, -3.54) * mm, "end": v(29.36, -3.47) * mm});
            skLineSegment(sketch, "E384", {"start": v(29.36, -3.47) * mm, "end": v(29.47, -3.4) * mm});
            skLineSegment(sketch, "E385", {"start": v(29.47, -3.4) * mm, "end": v(29.6, -3.35) * mm});
            skLineSegment(sketch, "E386", {"start": v(29.6, -3.35) * mm, "end": v(29.71, -3.3) * mm});
            skLineSegment(sketch, "E387", {"start": v(29.71, -3.3) * mm, "end": v(29.84, -3.28) * mm});
            skLineSegment(sketch, "E388", {"start": v(29.84, -3.28) * mm, "end": v(29.97, -3.26) * mm});
            skLineSegment(sketch, "E389", {"start": v(29.97, -3.26) * mm, "end": v(30.1, -3.25) * mm});
            skLineSegment(sketch, "E390", {"start": v(30.1, -3.25) * mm, "end": v(30.7, -3.3) * mm});
            skLineSegment(sketch, "E391", {"start": v(30.7, -3.3) * mm, "end": v(30.85, -3.27) * mm});
            skLineSegment(sketch, "E392", {"start": v(30.85, -3.27) * mm, "end": v(30.98, -3.19) * mm});
            skLineSegment(sketch, "E393", {"start": v(30.98, -3.19) * mm, "end": v(31.07, -3.07) * mm});
            skLineSegment(sketch, "E394", {"start": v(31.07, -3.07) * mm, "end": v(31.12, -2.94) * mm});
            skLineSegment(sketch, "E395", {"start": v(31.12, -2.94) * mm, "end": v(31.16, -2.45) * mm});
            skLineSegment(sketch, "E396", {"start": v(31.16, -2.45) * mm, "end": v(31.2, -1.97) * mm});
            skLineSegment(sketch, "E397", {"start": v(31.2, -1.97) * mm, "end": v(31.17, -1.83) * mm});
            skLineSegment(sketch, "E398", {"start": v(31.17, -1.83) * mm, "end": v(31.1, -1.7) * mm});
            skLineSegment(sketch, "E399", {"start": v(31.1, -1.7) * mm, "end": v(30.98, -1.6) * mm});
            skLineSegment(sketch, "E400", {"start": v(30.98, -1.6) * mm, "end": v(30.84, -1.54) * mm});
            skLineSegment(sketch, "E401", {"start": v(30.84, -1.54) * mm, "end": v(30.24, -1.5) * mm});
            skLineSegment(sketch, "E402", {"start": v(30.24, -1.5) * mm, "end": v(30.1, -1.47) * mm});
            skLineSegment(sketch, "E403", {"start": v(30.1, -1.47) * mm, "end": v(29.98, -1.43) * mm});
            skLineSegment(sketch, "E404", {"start": v(29.98, -1.43) * mm, "end": v(29.86, -1.38) * mm});
            skLineSegment(sketch, "E405", {"start": v(29.86, -1.38) * mm, "end": v(29.75, -1.32) * mm});
            skLineSegment(sketch, "E406", {"start": v(29.75, -1.32) * mm, "end": v(29.64, -1.25) * mm});
            skLineSegment(sketch, "E407", {"start": v(29.64, -1.25) * mm, "end": v(29.54, -1.17) * mm});
            skLineSegment(sketch, "E408", {"start": v(29.54, -1.17) * mm, "end": v(29.45, -1.08) * mm});
            skLineSegment(sketch, "E409", {"start": v(29.45, -1.08) * mm, "end": v(29.36, -0.98) * mm});
            skLineSegment(sketch, "E410", {"start": v(29.36, -0.98) * mm, "end": v(29.29, -0.88) * mm});
            skLineSegment(sketch, "E411", {"start": v(29.29, -0.88) * mm, "end": v(29.22, -0.77) * mm});
            skLineSegment(sketch, "E412", {"start": v(29.22, -0.77) * mm, "end": v(29.15, -0.65) * mm});
            skLineSegment(sketch, "E413", {"start": v(29.15, -0.65) * mm, "end": v(29.1, -0.53) * mm});
            skLineSegment(sketch, "E414", {"start": v(29.1, -0.53) * mm, "end": v(29.06, -0.4) * mm});
            skLineSegment(sketch, "E415", {"start": v(29.06, -0.4) * mm, "end": v(29.03, -0.27) * mm});
            skLineSegment(sketch, "E416", {"start": v(29.03, -0.27) * mm, "end": v(29, -0.14) * mm});
            skLineSegment(sketch, "E417", {"start": v(29, -0.14) * mm, "end": v(29, 0) * mm});
            skLineSegment(sketch, "E418", {"start": v(29, 0) * mm, "end": v(29, 0.14) * mm});
            skLineSegment(sketch, "E419", {"start": v(29, 0.14) * mm, "end": v(29.03, 0.27) * mm});
            skLineSegment(sketch, "E420", {"start": v(29.03, 0.27) * mm, "end": v(29.06, 0.4) * mm});
            skLineSegment(sketch, "E421", {"start": v(29.06, 0.4) * mm, "end": v(29.1, 0.53) * mm});
            skLineSegment(sketch, "E422", {"start": v(29.1, 0.53) * mm, "end": v(29.15, 0.65) * mm});
            skLineSegment(sketch, "E423", {"start": v(29.15, 0.65) * mm, "end": v(29.22, 0.77) * mm});
            skLineSegment(sketch, "E424", {"start": v(29.22, 0.77) * mm, "end": v(29.28, 0.88) * mm});
            skLineSegment(sketch, "E425", {"start": v(29.28, 0.88) * mm, "end": v(29.36, 0.98) * mm});
            skLineSegment(sketch, "E426", {"start": v(29.36, 0.98) * mm, "end": v(29.45, 1.08) * mm});
            skLineSegment(sketch, "E427", {"start": v(29.45, 1.08) * mm, "end": v(29.54, 1.17) * mm});
            skLineSegment(sketch, "E428", {"start": v(29.54, 1.17) * mm, "end": v(29.64, 1.25) * mm});
            skLineSegment(sketch, "E429", {"start": v(29.64, 1.25) * mm, "end": v(29.75, 1.32) * mm});
            skLineSegment(sketch, "E430", {"start": v(29.75, 1.32) * mm, "end": v(29.86, 1.38) * mm});
            skLineSegment(sketch, "E431", {"start": v(29.86, 1.38) * mm, "end": v(29.98, 1.43) * mm});
            skLineSegment(sketch, "E432", {"start": v(29.98, 1.43) * mm, "end": v(30.1, 1.47) * mm});
            skLineSegment(sketch, "E433", {"start": v(30.1, 1.47) * mm, "end": v(30.24, 1.5) * mm});
            skLineSegment(sketch, "E434", {"start": v(30.24, 1.5) * mm, "end": v(30.84, 1.54) * mm});
            skLineSegment(sketch, "E435", {"start": v(30.84, 1.54) * mm, "end": v(30.98, 1.6) * mm});
            skLineSegment(sketch, "E436", {"start": v(30.98, 1.6) * mm, "end": v(31.1, 1.7) * mm});
            skLineSegment(sketch, "E437", {"start": v(31.1, 1.7) * mm, "end": v(31.17, 1.83) * mm});
            skLineSegment(sketch, "E438", {"start": v(31.17, 1.83) * mm, "end": v(31.2, 1.97) * mm});
            skLineSegment(sketch, "E439", {"start": v(31.2, 1.97) * mm, "end": v(31.16, 2.45) * mm});
            skLineSegment(sketch, "E440", {"start": v(31.16, 2.45) * mm, "end": v(31.12, 2.94) * mm});
            skLineSegment(sketch, "E441", {"start": v(31.12, 2.94) * mm, "end": v(31.07, 3.07) * mm});
            skLineSegment(sketch, "E442", {"start": v(31.07, 3.07) * mm, "end": v(30.98, 3.19) * mm});
            skLineSegment(sketch, "E443", {"start": v(30.98, 3.19) * mm, "end": v(30.85, 3.27) * mm});
            skLineSegment(sketch, "E444", {"start": v(30.85, 3.27) * mm, "end": v(30.7, 3.3) * mm});
            skLineSegment(sketch, "E445", {"start": v(30.7, 3.3) * mm, "end": v(30.1, 3.25) * mm});
            skLineSegment(sketch, "E446", {"start": v(30.1, 3.25) * mm, "end": v(29.97, 3.26) * mm});
            skLineSegment(sketch, "E447", {"start": v(29.97, 3.26) * mm, "end": v(29.84, 3.28) * mm});
            skLineSegment(sketch, "E448", {"start": v(29.84, 3.28) * mm, "end": v(29.71, 3.3) * mm});
            skLineSegment(sketch, "E449", {"start": v(29.71, 3.3) * mm, "end": v(29.6, 3.35) * mm});
            skLineSegment(sketch, "E450", {"start": v(29.6, 3.35) * mm, "end": v(29.47, 3.4) * mm});
            skLineSegment(sketch, "E451", {"start": v(29.47, 3.4) * mm, "end": v(29.36, 3.47) * mm});
            skLineSegment(sketch, "E452", {"start": v(29.36, 3.47) * mm, "end": v(29.26, 3.54) * mm});
            skLineSegment(sketch, "E453", {"start": v(29.26, 3.54) * mm, "end": v(29.16, 3.62) * mm});
            skLineSegment(sketch, "E454", {"start": v(29.16, 3.62) * mm, "end": v(29.06, 3.71) * mm});
            skLineSegment(sketch, "E455", {"start": v(29.06, 3.71) * mm, "end": v(28.98, 3.81) * mm});
            skLineSegment(sketch, "E456", {"start": v(28.98, 3.81) * mm, "end": v(28.9, 3.92) * mm});
            skLineSegment(sketch, "E457", {"start": v(28.9, 3.92) * mm, "end": v(28.83, 4.03) * mm});
            skLineSegment(sketch, "E458", {"start": v(28.83, 4.03) * mm, "end": v(28.77, 4.15) * mm});
            skLineSegment(sketch, "E459", {"start": v(28.77, 4.15) * mm, "end": v(28.71, 4.27) * mm});
            skLineSegment(sketch, "E460", {"start": v(28.71, 4.27) * mm, "end": v(28.67, 4.4) * mm});
            skLineSegment(sketch, "E461", {"start": v(28.67, 4.4) * mm, "end": v(28.64, 4.54) * mm});
            skLineSegment(sketch, "E462", {"start": v(28.64, 4.54) * mm, "end": v(28.63, 4.67) * mm});
            skLineSegment(sketch, "E463", {"start": v(28.63, 4.67) * mm, "end": v(28.63, 4.81) * mm});
            skLineSegment(sketch, "E464", {"start": v(28.63, 4.81) * mm, "end": v(28.64, 4.95) * mm});
            skLineSegment(sketch, "E465", {"start": v(28.64, 4.95) * mm, "end": v(28.66, 5.08) * mm});
            skLineSegment(sketch, "E466", {"start": v(28.66, 5.08) * mm, "end": v(28.7, 5.2) * mm});
            skLineSegment(sketch, "E467", {"start": v(28.7, 5.2) * mm, "end": v(28.74, 5.33) * mm});
            skLineSegment(sketch, "E468", {"start": v(28.74, 5.33) * mm, "end": v(28.79, 5.45) * mm});
            skLineSegment(sketch, "E469", {"start": v(28.79, 5.45) * mm, "end": v(28.85, 5.56) * mm});
            skLineSegment(sketch, "E470", {"start": v(28.85, 5.56) * mm, "end": v(28.92, 5.67) * mm});
            skLineSegment(sketch, "E471", {"start": v(28.92, 5.67) * mm, "end": v(29, 5.77) * mm});
            skLineSegment(sketch, "E472", {"start": v(29, 5.77) * mm, "end": v(29.08, 5.87) * mm});
            skLineSegment(sketch, "E473", {"start": v(29.08, 5.87) * mm, "end": v(29.18, 5.96) * mm});
            skLineSegment(sketch, "E474", {"start": v(29.18, 5.96) * mm, "end": v(29.28, 6.03) * mm});
            skLineSegment(sketch, "E475", {"start": v(29.28, 6.03) * mm, "end": v(29.39, 6.1) * mm});
            skLineSegment(sketch, "E476", {"start": v(29.39, 6.1) * mm, "end": v(29.5, 6.16) * mm});
            skLineSegment(sketch, "E477", {"start": v(29.5, 6.16) * mm, "end": v(29.63, 6.21) * mm});
            skLineSegment(sketch, "E478", {"start": v(29.63, 6.21) * mm, "end": v(30.22, 6.35) * mm});
            skLineSegment(sketch, "E479", {"start": v(30.22, 6.35) * mm, "end": v(30.35, 6.43) * mm});
            skLineSegment(sketch, "E480", {"start": v(30.35, 6.43) * mm, "end": v(30.45, 6.54) * mm});
            skLineSegment(sketch, "E481", {"start": v(30.45, 6.54) * mm, "end": v(30.5, 6.69) * mm});
            skLineSegment(sketch, "E482", {"start": v(30.5, 6.69) * mm, "end": v(30.5, 6.82) * mm});
            skLineSegment(sketch, "E483", {"start": v(30.5, 6.82) * mm, "end": v(30.4, 7.3) * mm});
            skLineSegment(sketch, "E484", {"start": v(30.4, 7.3) * mm, "end": v(30.27, 7.77) * mm});
            skLineSegment(sketch, "E485", {"start": v(30.27, 7.77) * mm, "end": v(30.21, 7.89) * mm});
            skLineSegment(sketch, "E486", {"start": v(30.21, 7.89) * mm, "end": v(30.1, 8) * mm});
            skLineSegment(sketch, "E487", {"start": v(30.1, 8) * mm, "end": v(29.96, 8.05) * mm});
            skLineSegment(sketch, "E488", {"start": v(29.96, 8.05) * mm, "end": v(29.8, 8.06) * mm});
            skLineSegment(sketch, "E489", {"start": v(29.8, 8.06) * mm, "end": v(29.22, 7.91) * mm});
            skLineSegment(sketch, "E490", {"start": v(29.22, 7.91) * mm, "end": v(29.09, 7.9) * mm});
            skLineSegment(sketch, "E491", {"start": v(29.09, 7.9) * mm, "end": v(28.96, 7.9) * mm});
            skLineSegment(sketch, "E492", {"start": v(28.96, 7.9) * mm, "end": v(28.83, 7.92) * mm});
            skLineSegment(sketch, "E493", {"start": v(28.83, 7.92) * mm, "end": v(28.7, 7.94) * mm});
            skLineSegment(sketch, "E494", {"start": v(28.7, 7.94) * mm, "end": v(28.58, 7.97) * mm});
            skLineSegment(sketch, "E495", {"start": v(28.58, 7.97) * mm, "end": v(28.46, 8.02) * mm});
            skLineSegment(sketch, "E496", {"start": v(28.46, 8.02) * mm, "end": v(28.34, 8.07) * mm});
            skLineSegment(sketch, "E497", {"start": v(28.34, 8.07) * mm, "end": v(28.23, 8.14) * mm});
            skLineSegment(sketch, "E498", {"start": v(28.23, 8.14) * mm, "end": v(28.12, 8.21) * mm});
            skLineSegment(sketch, "E499", {"start": v(28.12, 8.21) * mm, "end": v(28.02, 8.3) * mm});
            skLineSegment(sketch, "E500", {"start": v(28.02, 8.3) * mm, "end": v(27.93, 8.39) * mm});
            skLineSegment(sketch, "E501", {"start": v(27.93, 8.39) * mm, "end": v(27.84, 8.49) * mm});
            skLineSegment(sketch, "E502", {"start": v(27.84, 8.49) * mm, "end": v(27.76, 8.6) * mm});
            skLineSegment(sketch, "E503", {"start": v(27.76, 8.6) * mm, "end": v(27.7, 8.71) * mm});
            skLineSegment(sketch, "E504", {"start": v(27.7, 8.71) * mm, "end": v(27.63, 8.83) * mm});
            skLineSegment(sketch, "E505", {"start": v(27.63, 8.83) * mm, "end": v(27.58, 8.96) * mm});
            skLineSegment(sketch, "E506", {"start": v(27.58, 8.96) * mm, "end": v(27.55, 9.1) * mm});
            skLineSegment(sketch, "E507", {"start": v(27.55, 9.1) * mm, "end": v(27.52, 9.23) * mm});
            skLineSegment(sketch, "E508", {"start": v(27.52, 9.23) * mm, "end": v(27.51, 9.36) * mm});
            skLineSegment(sketch, "E509", {"start": v(27.51, 9.36) * mm, "end": v(27.51, 9.5) * mm});
            skLineSegment(sketch, "E510", {"start": v(27.51, 9.5) * mm, "end": v(27.53, 9.63) * mm});
            skLineSegment(sketch, "E511", {"start": v(27.53, 9.63) * mm, "end": v(27.55, 9.76) * mm});
            skLineSegment(sketch, "E512", {"start": v(27.55, 9.76) * mm, "end": v(27.58, 9.89) * mm});
            skLineSegment(sketch, "E513", {"start": v(27.58, 9.89) * mm, "end": v(27.62, 10) * mm});
            skLineSegment(sketch, "E514", {"start": v(27.62, 10) * mm, "end": v(27.67, 10.13) * mm});
            skLineSegment(sketch, "E515", {"start": v(27.67, 10.13) * mm, "end": v(27.74, 10.24) * mm});
            skLineSegment(sketch, "E516", {"start": v(27.74, 10.24) * mm, "end": v(27.8, 10.35) * mm});
            skLineSegment(sketch, "E517", {"start": v(27.8, 10.35) * mm, "end": v(27.89, 10.45) * mm});
            skLineSegment(sketch, "E518", {"start": v(27.89, 10.45) * mm, "end": v(27.98, 10.54) * mm});
            skLineSegment(sketch, "E519", {"start": v(27.98, 10.54) * mm, "end": v(28.07, 10.63) * mm});
            skLineSegment(sketch, "E520", {"start": v(28.07, 10.63) * mm, "end": v(28.18, 10.7) * mm});
            skLineSegment(sketch, "E521", {"start": v(28.18, 10.7) * mm, "end": v(28.3, 10.77) * mm});
            skLineSegment(sketch, "E522", {"start": v(28.3, 10.77) * mm, "end": v(28.85, 11) * mm});
            skLineSegment(sketch, "E523", {"start": v(28.85, 11) * mm, "end": v(28.97, 11.1) * mm});
            skLineSegment(sketch, "E524", {"start": v(28.97, 11.1) * mm, "end": v(29.05, 11.23) * mm});
            skLineSegment(sketch, "E525", {"start": v(29.05, 11.23) * mm, "end": v(29.08, 11.38) * mm});
            skLineSegment(sketch, "E526", {"start": v(29.08, 11.38) * mm, "end": v(29.06, 11.5) * mm});
            skLineSegment(sketch, "E527", {"start": v(29.06, 11.5) * mm, "end": v(28.88, 11.96) * mm});
            skLineSegment(sketch, "E528", {"start": v(28.88, 11.96) * mm, "end": v(28.68, 12.4) * mm});
            skLineSegment(sketch, "E529", {"start": v(28.68, 12.4) * mm, "end": v(28.6, 12.52) * mm});
            skLineSegment(sketch, "E530", {"start": v(28.6, 12.52) * mm, "end": v(28.48, 12.6) * mm});
            skLineSegment(sketch, "E531", {"start": v(28.48, 12.6) * mm, "end": v(28.33, 12.64) * mm});
            skLineSegment(sketch, "E532", {"start": v(28.33, 12.64) * mm, "end": v(28.18, 12.62) * mm});
            skLineSegment(sketch, "E533", {"start": v(28.18, 12.62) * mm, "end": v(27.62, 12.39) * mm});
            skLineSegment(sketch, "E534", {"start": v(27.62, 12.39) * mm, "end": v(27.5, 12.36) * mm});
            skLineSegment(sketch, "E535", {"start": v(27.5, 12.36) * mm, "end": v(27.36, 12.34) * mm});
            skLineSegment(sketch, "E536", {"start": v(27.36, 12.34) * mm, "end": v(27.24, 12.33) * mm});
            skLineSegment(sketch, "E537", {"start": v(27.24, 12.33) * mm, "end": v(27.1, 12.33) * mm});
            skLineSegment(sketch, "E538", {"start": v(27.1, 12.33) * mm, "end": v(26.98, 12.35) * mm});
            skLineSegment(sketch, "E539", {"start": v(26.98, 12.35) * mm, "end": v(26.85, 12.37) * mm});
            skLineSegment(sketch, "E540", {"start": v(26.85, 12.37) * mm, "end": v(26.73, 12.4) * mm});
            skLineSegment(sketch, "E541", {"start": v(26.73, 12.4) * mm, "end": v(26.6, 12.46) * mm});
            skLineSegment(sketch, "E542", {"start": v(26.6, 12.46) * mm, "end": v(26.5, 12.51) * mm});
            skLineSegment(sketch, "E543", {"start": v(26.5, 12.51) * mm, "end": v(26.38, 12.58) * mm});
            skLineSegment(sketch, "E544", {"start": v(26.38, 12.58) * mm, "end": v(26.27, 12.65) * mm});
            skLineSegment(sketch, "E545", {"start": v(26.27, 12.65) * mm, "end": v(26.17, 12.74) * mm});
            skLineSegment(sketch, "E546", {"start": v(26.17, 12.74) * mm, "end": v(26.08, 12.83) * mm});
            skLineSegment(sketch, "E547", {"start": v(26.08, 12.83) * mm, "end": v(25.99, 12.94) * mm});
            skLineSegment(sketch, "E548", {"start": v(25.99, 12.94) * mm, "end": v(25.9, 13.05) * mm});
            skLineSegment(sketch, "E549", {"start": v(25.9, 13.05) * mm, "end": v(25.84, 13.16) * mm});
            skLineSegment(sketch, "E550", {"start": v(25.84, 13.16) * mm, "end": v(25.78, 13.3) * mm});
            skLineSegment(sketch, "E551", {"start": v(25.78, 13.3) * mm, "end": v(25.74, 13.42) * mm});
            skLineSegment(sketch, "E552", {"start": v(25.74, 13.42) * mm, "end": v(25.7, 13.55) * mm});
            skLineSegment(sketch, "E553", {"start": v(25.7, 13.55) * mm, "end": v(25.69, 13.69) * mm});
            skLineSegment(sketch, "E554", {"start": v(25.69, 13.69) * mm, "end": v(25.68, 13.82) * mm});
            skLineSegment(sketch, "E555", {"start": v(25.68, 13.82) * mm, "end": v(25.68, 13.95) * mm});
            skLineSegment(sketch, "E556", {"start": v(25.68, 13.95) * mm, "end": v(25.7, 14.08) * mm});
            skLineSegment(sketch, "E557", {"start": v(25.7, 14.08) * mm, "end": v(25.72, 14.2) * mm});
            skLineSegment(sketch, "E558", {"start": v(25.72, 14.2) * mm, "end": v(25.75, 14.33) * mm});
            skLineSegment(sketch, "E559", {"start": v(25.75, 14.33) * mm, "end": v(25.8, 14.45) * mm});
            skLineSegment(sketch, "E560", {"start": v(25.8, 14.45) * mm, "end": v(25.85, 14.57) * mm});
            skLineSegment(sketch, "E561", {"start": v(25.85, 14.57) * mm, "end": v(25.9, 14.68) * mm});
            skLineSegment(sketch, "E562", {"start": v(25.9, 14.68) * mm, "end": v(25.98, 14.79) * mm});
            skLineSegment(sketch, "E563", {"start": v(25.98, 14.79) * mm, "end": v(26.06, 14.89) * mm});
            skLineSegment(sketch, "E564", {"start": v(26.06, 14.89) * mm, "end": v(26.16, 14.98) * mm});
            skLineSegment(sketch, "E565", {"start": v(26.16, 14.98) * mm, "end": v(26.26, 15.07) * mm});
            skLineSegment(sketch, "E566", {"start": v(26.26, 15.07) * mm, "end": v(26.78, 15.38) * mm});
            skLineSegment(sketch, "E567", {"start": v(26.78, 15.38) * mm, "end": v(26.88, 15.5) * mm});
            skLineSegment(sketch, "E568", {"start": v(26.88, 15.5) * mm, "end": v(26.93, 15.63) * mm});
            skLineSegment(sketch, "E569", {"start": v(26.93, 15.63) * mm, "end": v(26.94, 15.78) * mm});
            skLineSegment(sketch, "E570", {"start": v(26.94, 15.78) * mm, "end": v(26.9, 15.91) * mm});
            skLineSegment(sketch, "E571", {"start": v(26.9, 15.91) * mm, "end": v(26.65, 16.33) * mm});
            skLineSegment(sketch, "E572", {"start": v(26.65, 16.33) * mm, "end": v(26.4, 16.74) * mm});
            skLineSegment(sketch, "E573", {"start": v(26.4, 16.74) * mm, "end": v(26.3, 16.84) * mm});
            skLineSegment(sketch, "E574", {"start": v(26.3, 16.84) * mm, "end": v(26.16, 16.9) * mm});
            skLineSegment(sketch, "E575", {"start": v(26.16, 16.9) * mm, "end": v(26, 16.92) * mm});
            skLineSegment(sketch, "E576", {"start": v(26, 16.92) * mm, "end": v(25.86, 16.88) * mm});
            skLineSegment(sketch, "E577", {"start": v(25.86, 16.88) * mm, "end": v(25.34, 16.56) * mm});
            skLineSegment(sketch, "E578", {"start": v(25.34, 16.56) * mm, "end": v(25.22, 16.5) * mm});
            skLineSegment(sketch, "E579", {"start": v(25.22, 16.5) * mm, "end": v(25.1, 16.47) * mm});
            skLineSegment(sketch, "E580", {"start": v(25.1, 16.47) * mm, "end": v(24.97, 16.44) * mm});
            skLineSegment(sketch, "E581", {"start": v(24.97, 16.44) * mm, "end": v(24.84, 16.42) * mm});
            skLineSegment(sketch, "E582", {"start": v(24.84, 16.42) * mm, "end": v(24.71, 16.42) * mm});
            skLineSegment(sketch, "E583", {"start": v(24.71, 16.42) * mm, "end": v(24.59, 16.42) * mm});
            skLineSegment(sketch, "E584", {"start": v(24.59, 16.42) * mm, "end": v(24.46, 16.44) * mm});
            skLineSegment(sketch, "E585", {"start": v(24.46, 16.44) * mm, "end": v(24.33, 16.46) * mm});
            skLineSegment(sketch, "E586", {"start": v(24.33, 16.46) * mm, "end": v(24.2, 16.5) * mm});
            skLineSegment(sketch, "E587", {"start": v(24.2, 16.5) * mm, "end": v(24.09, 16.55) * mm});
            skLineSegment(sketch, "E588", {"start": v(24.09, 16.55) * mm, "end": v(23.97, 16.6) * mm});
            skLineSegment(sketch, "E589", {"start": v(23.97, 16.6) * mm, "end": v(23.86, 16.68) * mm});
            skLineSegment(sketch, "E590", {"start": v(23.86, 16.68) * mm, "end": v(23.75, 16.75) * mm});
            skLineSegment(sketch, "E591", {"start": v(23.75, 16.75) * mm, "end": v(23.65, 16.84) * mm});
            skLineSegment(sketch, "E592", {"start": v(23.65, 16.84) * mm, "end": v(23.55, 16.94) * mm});
            skLineSegment(sketch, "E593", {"start": v(23.55, 16.94) * mm, "end": v(23.46, 17.04) * mm});
            skLineSegment(sketch, "E594", {"start": v(23.46, 17.04) * mm, "end": v(23.39, 17.16) * mm});
            skLineSegment(sketch, "E595", {"start": v(23.39, 17.16) * mm, "end": v(23.32, 17.28) * mm});
            skLineSegment(sketch, "E596", {"start": v(23.32, 17.28) * mm, "end": v(23.27, 17.4) * mm});
            skLineSegment(sketch, "E597", {"start": v(23.27, 17.4) * mm, "end": v(23.23, 17.54) * mm});
            skLineSegment(sketch, "E598", {"start": v(23.23, 17.54) * mm, "end": v(23.2, 17.66) * mm});
            skLineSegment(sketch, "E599", {"start": v(23.2, 17.66) * mm, "end": v(23.18, 17.8) * mm});
            skLineSegment(sketch, "E600", {"start": v(23.18, 17.8) * mm, "end": v(23.18, 17.92) * mm});
            skLineSegment(sketch, "E601", {"start": v(23.18, 17.92) * mm, "end": v(23.18, 18.05) * mm});
            skLineSegment(sketch, "E602", {"start": v(23.18, 18.05) * mm, "end": v(23.2, 18.18) * mm});
            skLineSegment(sketch, "E603", {"start": v(23.2, 18.18) * mm, "end": v(23.21, 18.3) * mm});
            skLineSegment(sketch, "E604", {"start": v(23.21, 18.3) * mm, "end": v(23.25, 18.43) * mm});
            skLineSegment(sketch, "E605", {"start": v(23.25, 18.43) * mm, "end": v(23.3, 18.55) * mm});
            skLineSegment(sketch, "E606", {"start": v(23.3, 18.55) * mm, "end": v(23.35, 18.67) * mm});
            skLineSegment(sketch, "E607", {"start": v(23.35, 18.67) * mm, "end": v(23.41, 18.78) * mm});
            skLineSegment(sketch, "E608", {"start": v(23.41, 18.78) * mm, "end": v(23.5, 18.89) * mm});
            skLineSegment(sketch, "E609", {"start": v(23.5, 18.89) * mm, "end": v(23.58, 18.99) * mm});
            skLineSegment(sketch, "E610", {"start": v(23.58, 18.99) * mm, "end": v(24.04, 19.38) * mm});
            skLineSegment(sketch, "E611", {"start": v(24.04, 19.38) * mm, "end": v(24.13, 19.5) * mm});
            skLineSegment(sketch, "E612", {"start": v(24.13, 19.5) * mm, "end": v(24.16, 19.65) * mm});
            skLineSegment(sketch, "E613", {"start": v(24.16, 19.65) * mm, "end": v(24.14, 19.8) * mm});
            skLineSegment(sketch, "E614", {"start": v(24.14, 19.8) * mm, "end": v(24.08, 19.92) * mm});
            skLineSegment(sketch, "E615", {"start": v(24.08, 19.92) * mm, "end": v(23.77, 20.3) * mm});
            skLineSegment(sketch, "E616", {"start": v(23.77, 20.3) * mm, "end": v(23.45, 20.67) * mm});
            skLineSegment(sketch, "E617", {"start": v(23.45, 20.67) * mm, "end": v(23.34, 20.74) * mm});
            skLineSegment(sketch, "E618", {"start": v(23.34, 20.74) * mm, "end": v(23.19, 20.79) * mm});
            skLineSegment(sketch, "E619", {"start": v(23.19, 20.79) * mm, "end": v(23.04, 20.78) * mm});
            skLineSegment(sketch, "E620", {"start": v(23.04, 20.78) * mm, "end": v(22.9, 20.72) * mm});
            skLineSegment(sketch, "E621", {"start": v(22.9, 20.72) * mm, "end": v(22.44, 20.32) * mm});
            skLineSegment(sketch, "E622", {"start": v(22.44, 20.32) * mm, "end": v(22.33, 20.25) * mm});
            skLineSegment(sketch, "E623", {"start": v(22.33, 20.25) * mm, "end": v(22.21, 20.19) * mm});
            skLineSegment(sketch, "E624", {"start": v(22.21, 20.19) * mm, "end": v(22.1, 20.14) * mm});
            skLineSegment(sketch, "E625", {"start": v(22.1, 20.14) * mm, "end": v(21.97, 20.1) * mm});
            skLineSegment(sketch, "E626", {"start": v(21.97, 20.1) * mm, "end": v(21.84, 20.08) * mm});
            skLineSegment(sketch, "E627", {"start": v(21.84, 20.08) * mm, "end": v(21.72, 20.07) * mm});
            skLineSegment(sketch, "E628", {"start": v(21.72, 20.07) * mm, "end": v(21.59, 20.06) * mm});
            skLineSegment(sketch, "E629", {"start": v(21.59, 20.06) * mm, "end": v(21.46, 20.07) * mm});
            skLineSegment(sketch, "E630", {"start": v(21.46, 20.07) * mm, "end": v(21.33, 20.09) * mm});
            skLineSegment(sketch, "E631", {"start": v(21.33, 20.09) * mm, "end": v(21.2, 20.11) * mm});
            skLineSegment(sketch, "E632", {"start": v(21.2, 20.11) * mm, "end": v(21.08, 20.15) * mm});
            skLineSegment(sketch, "E633", {"start": v(21.08, 20.15) * mm, "end": v(20.95, 20.2) * mm});
            skLineSegment(sketch, "E634", {"start": v(20.95, 20.2) * mm, "end": v(20.84, 20.26) * mm});
            skLineSegment(sketch, "E635", {"start": v(20.84, 20.26) * mm, "end": v(20.72, 20.33) * mm});
            skLineSegment(sketch, "E636", {"start": v(20.72, 20.33) * mm, "end": v(20.6, 20.41) * mm});
            skLineSegment(sketch, "E637", {"start": v(20.6, 20.41) * mm, "end": v(20.5, 20.5) * mm});
            skLineSegment(sketch, "E638", {"start": v(20.5, 20.5) * mm, "end": v(20.41, 20.6) * mm});
            skLineSegment(sketch, "E639", {"start": v(20.41, 20.6) * mm, "end": v(20.33, 20.72) * mm});
            skLineSegment(sketch, "E640", {"start": v(20.33, 20.72) * mm, "end": v(20.26, 20.83) * mm});
            skLineSegment(sketch, "E641", {"start": v(20.26, 20.83) * mm, "end": v(20.2, 20.95) * mm});
            skLineSegment(sketch, "E642", {"start": v(20.2, 20.95) * mm, "end": v(20.15, 21.08) * mm});
            skLineSegment(sketch, "E643", {"start": v(20.15, 21.08) * mm, "end": v(20.11, 21.2) * mm});
            skLineSegment(sketch, "E644", {"start": v(20.11, 21.2) * mm, "end": v(20.09, 21.33) * mm});
            skLineSegment(sketch, "E645", {"start": v(20.09, 21.33) * mm, "end": v(20.07, 21.46) * mm});
            skLineSegment(sketch, "E646", {"start": v(20.07, 21.46) * mm, "end": v(20.06, 21.59) * mm});
            skLineSegment(sketch, "E647", {"start": v(20.06, 21.59) * mm, "end": v(20.06, 21.72) * mm});
            skLineSegment(sketch, "E648", {"start": v(20.06, 21.72) * mm, "end": v(20.08, 21.84) * mm});
            skLineSegment(sketch, "E649", {"start": v(20.08, 21.84) * mm, "end": v(20.1, 21.97) * mm});
            skLineSegment(sketch, "E650", {"start": v(20.1, 21.97) * mm, "end": v(20.14, 22.1) * mm});
            skLineSegment(sketch, "E651", {"start": v(20.14, 22.1) * mm, "end": v(20.19, 22.21) * mm});
            skLineSegment(sketch, "E652", {"start": v(20.19, 22.21) * mm, "end": v(20.25, 22.33) * mm});
            skLineSegment(sketch, "E653", {"start": v(20.25, 22.33) * mm, "end": v(20.32, 22.44) * mm});
            skLineSegment(sketch, "E654", {"start": v(20.32, 22.44) * mm, "end": v(20.72, 22.9) * mm});
            skLineSegment(sketch, "E655", {"start": v(20.72, 22.9) * mm, "end": v(20.78, 23.04) * mm});
            skLineSegment(sketch, "E656", {"start": v(20.78, 23.04) * mm, "end": v(20.79, 23.19) * mm});
            skLineSegment(sketch, "E657", {"start": v(20.79, 23.19) * mm, "end": v(20.74, 23.34) * mm});
            skLineSegment(sketch, "E658", {"start": v(20.74, 23.34) * mm, "end": v(20.67, 23.45) * mm});
            skLineSegment(sketch, "E659", {"start": v(20.67, 23.45) * mm, "end": v(20.3, 23.77) * mm});
            skLineSegment(sketch, "E660", {"start": v(20.3, 23.77) * mm, "end": v(19.92, 24.08) * mm});
            skLineSegment(sketch, "E661", {"start": v(19.92, 24.08) * mm, "end": v(19.8, 24.14) * mm});
            skLineSegment(sketch, "E662", {"start": v(19.8, 24.14) * mm, "end": v(19.65, 24.16) * mm});
            skLineSegment(sketch, "E663", {"start": v(19.65, 24.16) * mm, "end": v(19.5, 24.13) * mm});
            skLineSegment(sketch, "E664", {"start": v(19.5, 24.13) * mm, "end": v(19.38, 24.04) * mm});
            skLineSegment(sketch, "E665", {"start": v(19.38, 24.04) * mm, "end": v(18.99, 23.58) * mm});
            skLineSegment(sketch, "E666", {"start": v(18.99, 23.58) * mm, "end": v(18.89, 23.5) * mm});
            skLineSegment(sketch, "E667", {"start": v(18.89, 23.5) * mm, "end": v(18.78, 23.42) * mm});
            skLineSegment(sketch, "E668", {"start": v(18.78, 23.42) * mm, "end": v(18.67, 23.35) * mm});
            skLineSegment(sketch, "E669", {"start": v(18.67, 23.35) * mm, "end": v(18.55, 23.3) * mm});
            skLineSegment(sketch, "E670", {"start": v(18.55, 23.3) * mm, "end": v(18.43, 23.25) * mm});
            skLineSegment(sketch, "E671", {"start": v(18.43, 23.25) * mm, "end": v(18.3, 23.21) * mm});
            skLineSegment(sketch, "E672", {"start": v(18.3, 23.21) * mm, "end": v(18.18, 23.2) * mm});
            skLineSegment(sketch, "E673", {"start": v(18.18, 23.2) * mm, "end": v(18.05, 23.18) * mm});
            skLineSegment(sketch, "E674", {"start": v(18.05, 23.18) * mm, "end": v(17.92, 23.18) * mm});
            skLineSegment(sketch, "E675", {"start": v(17.92, 23.18) * mm, "end": v(17.8, 23.18) * mm});
            skLineSegment(sketch, "E676", {"start": v(17.8, 23.18) * mm, "end": v(17.66, 23.2) * mm});
            skLineSegment(sketch, "E677", {"start": v(17.66, 23.2) * mm, "end": v(17.54, 23.23) * mm});
            skLineSegment(sketch, "E678", {"start": v(17.54, 23.23) * mm, "end": v(17.4, 23.27) * mm});
            skLineSegment(sketch, "E679", {"start": v(17.4, 23.27) * mm, "end": v(17.28, 23.32) * mm});
            skLineSegment(sketch, "E680", {"start": v(17.28, 23.32) * mm, "end": v(17.16, 23.39) * mm});
            skLineSegment(sketch, "E681", {"start": v(17.16, 23.39) * mm, "end": v(17.04, 23.46) * mm});
            skLineSegment(sketch, "E682", {"start": v(17.04, 23.46) * mm, "end": v(16.94, 23.55) * mm});
            skLineSegment(sketch, "E683", {"start": v(16.94, 23.55) * mm, "end": v(16.84, 23.65) * mm});
            skLineSegment(sketch, "E684", {"start": v(16.84, 23.65) * mm, "end": v(16.75, 23.75) * mm});
            skLineSegment(sketch, "E685", {"start": v(16.75, 23.75) * mm, "end": v(16.68, 23.86) * mm});
            skLineSegment(sketch, "E686", {"start": v(16.68, 23.86) * mm, "end": v(16.6, 23.97) * mm});
            skLineSegment(sketch, "E687", {"start": v(16.6, 23.97) * mm, "end": v(16.55, 24.09) * mm});
            skLineSegment(sketch, "E688", {"start": v(16.55, 24.09) * mm, "end": v(16.5, 24.2) * mm});
            skLineSegment(sketch, "E689", {"start": v(16.5, 24.2) * mm, "end": v(16.46, 24.33) * mm});
            skLineSegment(sketch, "E690", {"start": v(16.46, 24.33) * mm, "end": v(16.44, 24.46) * mm});
            skLineSegment(sketch, "E691", {"start": v(16.44, 24.46) * mm, "end": v(16.42, 24.59) * mm});
            skLineSegment(sketch, "E692", {"start": v(16.42, 24.59) * mm, "end": v(16.42, 24.71) * mm});
            skLineSegment(sketch, "E693", {"start": v(16.42, 24.71) * mm, "end": v(16.42, 24.84) * mm});
            skLineSegment(sketch, "E694", {"start": v(16.42, 24.84) * mm, "end": v(16.44, 24.97) * mm});
            skLineSegment(sketch, "E695", {"start": v(16.44, 24.97) * mm, "end": v(16.47, 25.1) * mm});
            skLineSegment(sketch, "E696", {"start": v(16.47, 25.1) * mm, "end": v(16.5, 25.22) * mm});
            skLineSegment(sketch, "E697", {"start": v(16.5, 25.22) * mm, "end": v(16.56, 25.34) * mm});
            skLineSegment(sketch, "E698", {"start": v(16.56, 25.34) * mm, "end": v(16.88, 25.86) * mm});
            skLineSegment(sketch, "E699", {"start": v(16.88, 25.86) * mm, "end": v(16.92, 26) * mm});
            skLineSegment(sketch, "E700", {"start": v(16.92, 26) * mm, "end": v(16.9, 26.16) * mm});
            skLineSegment(sketch, "E701", {"start": v(16.9, 26.16) * mm, "end": v(16.84, 26.3) * mm});
            skLineSegment(sketch, "E702", {"start": v(16.84, 26.3) * mm, "end": v(16.74, 26.4) * mm});
            skLineSegment(sketch, "E703", {"start": v(16.74, 26.4) * mm, "end": v(16.33, 26.65) * mm});
            skLineSegment(sketch, "E704", {"start": v(16.33, 26.65) * mm, "end": v(15.91, 26.9) * mm});
            skLineSegment(sketch, "E705", {"start": v(15.91, 26.9) * mm, "end": v(15.78, 26.94) * mm});
            skLineSegment(sketch, "E706", {"start": v(15.78, 26.94) * mm, "end": v(15.63, 26.93) * mm});
            skLineSegment(sketch, "E707", {"start": v(15.63, 26.93) * mm, "end": v(15.5, 26.88) * mm});
            skLineSegment(sketch, "E708", {"start": v(15.5, 26.88) * mm, "end": v(15.38, 26.78) * mm});
            skLineSegment(sketch, "E709", {"start": v(15.38, 26.78) * mm, "end": v(15.07, 26.26) * mm});
            skLineSegment(sketch, "E710", {"start": v(15.07, 26.26) * mm, "end": v(14.98, 26.16) * mm});
            skLineSegment(sketch, "E711", {"start": v(14.98, 26.16) * mm, "end": v(14.89, 26.06) * mm});
            skLineSegment(sketch, "E712", {"start": v(14.89, 26.06) * mm, "end": v(14.79, 25.98) * mm});
            skLineSegment(sketch, "E713", {"start": v(14.79, 25.98) * mm, "end": v(14.68, 25.9) * mm});
            skLineSegment(sketch, "E714", {"start": v(14.68, 25.9) * mm, "end": v(14.57, 25.85) * mm});
            skLineSegment(sketch, "E715", {"start": v(14.57, 25.85) * mm, "end": v(14.45, 25.8) * mm});
            skLineSegment(sketch, "E716", {"start": v(14.45, 25.8) * mm, "end": v(14.33, 25.75) * mm});
            skLineSegment(sketch, "E717", {"start": v(14.33, 25.75) * mm, "end": v(14.2, 25.72) * mm});
            skLineSegment(sketch, "E718", {"start": v(14.2, 25.72) * mm, "end": v(14.08, 25.7) * mm});
            skLineSegment(sketch, "E719", {"start": v(14.08, 25.7) * mm, "end": v(13.95, 25.68) * mm});
            skLineSegment(sketch, "E720", {"start": v(13.95, 25.68) * mm, "end": v(13.82, 25.68) * mm});
            skLineSegment(sketch, "E721", {"start": v(13.82, 25.68) * mm, "end": v(13.69, 25.69) * mm});
            skLineSegment(sketch, "E722", {"start": v(13.69, 25.69) * mm, "end": v(13.55, 25.7) * mm});
            skLineSegment(sketch, "E723", {"start": v(13.55, 25.7) * mm, "end": v(13.42, 25.74) * mm});
            skLineSegment(sketch, "E724", {"start": v(13.42, 25.74) * mm, "end": v(13.3, 25.78) * mm});
            skLineSegment(sketch, "E725", {"start": v(13.3, 25.78) * mm, "end": v(13.16, 25.84) * mm});
            skLineSegment(sketch, "E726", {"start": v(13.16, 25.84) * mm, "end": v(13.05, 25.9) * mm});
            skLineSegment(sketch, "E727", {"start": v(13.05, 25.9) * mm, "end": v(12.94, 25.99) * mm});
            skLineSegment(sketch, "E728", {"start": v(12.94, 25.99) * mm, "end": v(12.83, 26.08) * mm});
            skLineSegment(sketch, "E729", {"start": v(12.83, 26.08) * mm, "end": v(12.74, 26.17) * mm});
            skLineSegment(sketch, "E730", {"start": v(12.74, 26.17) * mm, "end": v(12.65, 26.27) * mm});
            skLineSegment(sketch, "E731", {"start": v(12.65, 26.27) * mm, "end": v(12.58, 26.38) * mm});
            skLineSegment(sketch, "E732", {"start": v(12.58, 26.38) * mm, "end": v(12.51, 26.5) * mm});
            skLineSegment(sketch, "E733", {"start": v(12.51, 26.5) * mm, "end": v(12.46, 26.6) * mm});
            skLineSegment(sketch, "E734", {"start": v(12.46, 26.6) * mm, "end": v(12.4, 26.73) * mm});
            skLineSegment(sketch, "E735", {"start": v(12.4, 26.73) * mm, "end": v(12.37, 26.85) * mm});
            skLineSegment(sketch, "E736", {"start": v(12.37, 26.85) * mm, "end": v(12.35, 26.98) * mm});
            skLineSegment(sketch, "E737", {"start": v(12.35, 26.98) * mm, "end": v(12.33, 27.1) * mm});
            skLineSegment(sketch, "E738", {"start": v(12.33, 27.1) * mm, "end": v(12.33, 27.24) * mm});
            skLineSegment(sketch, "E739", {"start": v(12.33, 27.24) * mm, "end": v(12.34, 27.36) * mm});
            skLineSegment(sketch, "E740", {"start": v(12.34, 27.36) * mm, "end": v(12.36, 27.5) * mm});
            skLineSegment(sketch, "E741", {"start": v(12.36, 27.5) * mm, "end": v(12.39, 27.62) * mm});
            skLineSegment(sketch, "E742", {"start": v(12.39, 27.62) * mm, "end": v(12.62, 28.18) * mm});
            skLineSegment(sketch, "E743", {"start": v(12.62, 28.18) * mm, "end": v(12.64, 28.33) * mm});
            skLineSegment(sketch, "E744", {"start": v(12.64, 28.33) * mm, "end": v(12.6, 28.48) * mm});
            skLineSegment(sketch, "E745", {"start": v(12.6, 28.48) * mm, "end": v(12.52, 28.6) * mm});
            skLineSegment(sketch, "E746", {"start": v(12.52, 28.6) * mm, "end": v(12.4, 28.68) * mm});
            skLineSegment(sketch, "E747", {"start": v(12.4, 28.68) * mm, "end": v(11.96, 28.88) * mm});
            skLineSegment(sketch, "E748", {"start": v(11.96, 28.88) * mm, "end": v(11.5, 29.06) * mm});
            skLineSegment(sketch, "E749", {"start": v(11.5, 29.06) * mm, "end": v(11.38, 29.08) * mm});
            skLineSegment(sketch, "E750", {"start": v(11.38, 29.08) * mm, "end": v(11.23, 29.05) * mm});
            skLineSegment(sketch, "E751", {"start": v(11.23, 29.05) * mm, "end": v(11.1, 28.97) * mm});
            skLineSegment(sketch, "E752", {"start": v(11.1, 28.97) * mm, "end": v(11, 28.85) * mm});
            skLineSegment(sketch, "E753", {"start": v(11, 28.85) * mm, "end": v(10.77, 28.3) * mm});
            skLineSegment(sketch, "E754", {"start": v(10.77, 28.3) * mm, "end": v(10.7, 28.18) * mm});
            skLineSegment(sketch, "E755", {"start": v(10.7, 28.18) * mm, "end": v(10.63, 28.07) * mm});
            skLineSegment(sketch, "E756", {"start": v(10.63, 28.07) * mm, "end": v(10.54, 27.98) * mm});
            skLineSegment(sketch, "E757", {"start": v(10.54, 27.98) * mm, "end": v(10.45, 27.89) * mm});
            skLineSegment(sketch, "E758", {"start": v(10.45, 27.89) * mm, "end": v(10.35, 27.8) * mm});
            skLineSegment(sketch, "E759", {"start": v(10.35, 27.8) * mm, "end": v(10.24, 27.74) * mm});
            skLineSegment(sketch, "E760", {"start": v(10.24, 27.74) * mm, "end": v(10.13, 27.67) * mm});
            skLineSegment(sketch, "E761", {"start": v(10.13, 27.67) * mm, "end": v(10, 27.62) * mm});
            skLineSegment(sketch, "E762", {"start": v(10, 27.62) * mm, "end": v(9.89, 27.58) * mm});
            skLineSegment(sketch, "E763", {"start": v(9.89, 27.58) * mm, "end": v(9.76, 27.55) * mm});
            skLineSegment(sketch, "E764", {"start": v(9.76, 27.55) * mm, "end": v(9.63, 27.53) * mm});
            skLineSegment(sketch, "E765", {"start": v(9.63, 27.53) * mm, "end": v(9.5, 27.51) * mm});
            skLineSegment(sketch, "E766", {"start": v(9.5, 27.51) * mm, "end": v(9.36, 27.51) * mm});
            skLineSegment(sketch, "E767", {"start": v(9.36, 27.51) * mm, "end": v(9.23, 27.52) * mm});
            skLineSegment(sketch, "E768", {"start": v(9.23, 27.52) * mm, "end": v(9.1, 27.55) * mm});
            skLineSegment(sketch, "E769", {"start": v(9.1, 27.55) * mm, "end": v(8.96, 27.58) * mm});
            skLineSegment(sketch, "E770", {"start": v(8.96, 27.58) * mm, "end": v(8.83, 27.63) * mm});
            skLineSegment(sketch, "E771", {"start": v(8.83, 27.63) * mm, "end": v(8.71, 27.7) * mm});
            skLineSegment(sketch, "E772", {"start": v(8.71, 27.7) * mm, "end": v(8.6, 27.76) * mm});
            skLineSegment(sketch, "E773", {"start": v(8.6, 27.76) * mm, "end": v(8.49, 27.84) * mm});
            skLineSegment(sketch, "E774", {"start": v(8.49, 27.84) * mm, "end": v(8.39, 27.93) * mm});
            skLineSegment(sketch, "E775", {"start": v(8.39, 27.93) * mm, "end": v(8.3, 28.02) * mm});
            skLineSegment(sketch, "E776", {"start": v(8.3, 28.02) * mm, "end": v(8.21, 28.12) * mm});
            skLineSegment(sketch, "E777", {"start": v(8.21, 28.12) * mm, "end": v(8.14, 28.23) * mm});
            skLineSegment(sketch, "E778", {"start": v(8.14, 28.23) * mm, "end": v(8.07, 28.34) * mm});
            skLineSegment(sketch, "E779", {"start": v(8.07, 28.34) * mm, "end": v(8.02, 28.46) * mm});
            skLineSegment(sketch, "E780", {"start": v(8.02, 28.46) * mm, "end": v(7.97, 28.58) * mm});
            skLineSegment(sketch, "E781", {"start": v(7.97, 28.58) * mm, "end": v(7.94, 28.7) * mm});
            skLineSegment(sketch, "E782", {"start": v(7.94, 28.7) * mm, "end": v(7.92, 28.83) * mm});
            skLineSegment(sketch, "E783", {"start": v(7.92, 28.83) * mm, "end": v(7.9, 28.96) * mm});
            skLineSegment(sketch, "E784", {"start": v(7.9, 28.96) * mm, "end": v(7.9, 29.09) * mm});
            skLineSegment(sketch, "E785", {"start": v(7.9, 29.09) * mm, "end": v(7.91, 29.22) * mm});
            skLineSegment(sketch, "E786", {"start": v(7.91, 29.22) * mm, "end": v(8.06, 29.8) * mm});
            skLineSegment(sketch, "E787", {"start": v(8.06, 29.8) * mm, "end": v(8.05, 29.96) * mm});
            skLineSegment(sketch, "E788", {"start": v(8.05, 29.96) * mm, "end": v(8, 30.1) * mm});
            skLineSegment(sketch, "E789", {"start": v(8, 30.1) * mm, "end": v(7.89, 30.21) * mm});
            skLineSegment(sketch, "E790", {"start": v(7.89, 30.21) * mm, "end": v(7.77, 30.27) * mm});
            skLineSegment(sketch, "E791", {"start": v(7.77, 30.27) * mm, "end": v(7.3, 30.4) * mm});
            skLineSegment(sketch, "E792", {"start": v(7.3, 30.4) * mm, "end": v(6.82, 30.5) * mm});
            skLineSegment(sketch, "E793", {"start": v(6.82, 30.5) * mm, "end": v(6.69, 30.5) * mm});
            skLineSegment(sketch, "E794", {"start": v(6.69, 30.5) * mm, "end": v(6.54, 30.45) * mm});
            skLineSegment(sketch, "E795", {"start": v(6.54, 30.45) * mm, "end": v(6.43, 30.35) * mm});
            skLineSegment(sketch, "E796", {"start": v(6.43, 30.35) * mm, "end": v(6.35, 30.22) * mm});
            skLineSegment(sketch, "E797", {"start": v(6.35, 30.22) * mm, "end": v(6.21, 29.63) * mm});
            skLineSegment(sketch, "E798", {"start": v(6.21, 29.63) * mm, "end": v(6.16, 29.5) * mm});
            skLineSegment(sketch, "E799", {"start": v(6.16, 29.5) * mm, "end": v(6.1, 29.39) * mm});
            skLineSegment(sketch, "E800", {"start": v(6.1, 29.39) * mm, "end": v(6.03, 29.28) * mm});
            skLineSegment(sketch, "E801", {"start": v(6.03, 29.28) * mm, "end": v(5.96, 29.18) * mm});
            skLineSegment(sketch, "E802", {"start": v(5.96, 29.18) * mm, "end": v(5.87, 29.08) * mm});
            skLineSegment(sketch, "E803", {"start": v(5.87, 29.08) * mm, "end": v(5.77, 29) * mm});
            skLineSegment(sketch, "E804", {"start": v(5.77, 29) * mm, "end": v(5.67, 28.92) * mm});
            skLineSegment(sketch, "E805", {"start": v(5.67, 28.92) * mm, "end": v(5.56, 28.85) * mm});
            skLineSegment(sketch, "E806", {"start": v(5.56, 28.85) * mm, "end": v(5.45, 28.79) * mm});
            skLineSegment(sketch, "E807", {"start": v(5.45, 28.79) * mm, "end": v(5.33, 28.74) * mm});
            skLineSegment(sketch, "E808", {"start": v(5.33, 28.74) * mm, "end": v(5.2, 28.7) * mm});
            skLineSegment(sketch, "E809", {"start": v(5.2, 28.7) * mm, "end": v(5.08, 28.66) * mm});
            skLineSegment(sketch, "E810", {"start": v(5.08, 28.66) * mm, "end": v(4.95, 28.64) * mm});
            skLineSegment(sketch, "E811", {"start": v(4.95, 28.64) * mm, "end": v(4.81, 28.63) * mm});
            skLineSegment(sketch, "E812", {"start": v(4.81, 28.63) * mm, "end": v(4.67, 28.63) * mm});
            skLineSegment(sketch, "E813", {"start": v(4.67, 28.63) * mm, "end": v(4.54, 28.64) * mm});
            skLineSegment(sketch, "E814", {"start": v(4.54, 28.64) * mm, "end": v(4.4, 28.67) * mm});
            skLineSegment(sketch, "E815", {"start": v(4.4, 28.67) * mm, "end": v(4.27, 28.71) * mm});
            skLineSegment(sketch, "E816", {"start": v(4.27, 28.71) * mm, "end": v(4.15, 28.77) * mm});
            skLineSegment(sketch, "E817", {"start": v(4.15, 28.77) * mm, "end": v(4.03, 28.83) * mm});
            skLineSegment(sketch, "E818", {"start": v(4.03, 28.83) * mm, "end": v(3.92, 28.9) * mm});
            skLineSegment(sketch, "E819", {"start": v(3.92, 28.9) * mm, "end": v(3.81, 28.98) * mm});
            skLineSegment(sketch, "E820", {"start": v(3.81, 28.98) * mm, "end": v(3.71, 29.06) * mm});
            skLineSegment(sketch, "E821", {"start": v(3.71, 29.06) * mm, "end": v(3.62, 29.16) * mm});
            skLineSegment(sketch, "E822", {"start": v(3.62, 29.16) * mm, "end": v(3.54, 29.26) * mm});
            skLineSegment(sketch, "E823", {"start": v(3.54, 29.26) * mm, "end": v(3.47, 29.36) * mm});
            skLineSegment(sketch, "E824", {"start": v(3.47, 29.36) * mm, "end": v(3.4, 29.47) * mm});
            skLineSegment(sketch, "E825", {"start": v(3.4, 29.47) * mm, "end": v(3.35, 29.6) * mm});
            skLineSegment(sketch, "E826", {"start": v(3.35, 29.6) * mm, "end": v(3.3, 29.71) * mm});
            skLineSegment(sketch, "E827", {"start": v(3.3, 29.71) * mm, "end": v(3.28, 29.84) * mm});
            skLineSegment(sketch, "E828", {"start": v(3.28, 29.84) * mm, "end": v(3.26, 29.97) * mm});
            skLineSegment(sketch, "E829", {"start": v(3.26, 29.97) * mm, "end": v(3.25, 30.1) * mm});
            skLineSegment(sketch, "E830", {"start": v(3.25, 30.1) * mm, "end": v(3.3, 30.7) * mm});
            skLineSegment(sketch, "E831", {"start": v(3.3, 30.7) * mm, "end": v(3.27, 30.85) * mm});
            skLineSegment(sketch, "E832", {"start": v(3.27, 30.85) * mm, "end": v(3.19, 30.98) * mm});
            skLineSegment(sketch, "E833", {"start": v(3.19, 30.98) * mm, "end": v(3.07, 31.07) * mm});
            skLineSegment(sketch, "E834", {"start": v(3.07, 31.07) * mm, "end": v(2.94, 31.12) * mm});
            skLineSegment(sketch, "E835", {"start": v(2.94, 31.12) * mm, "end": v(2.45, 31.16) * mm});
            skLineSegment(sketch, "E836", {"start": v(2.45, 31.16) * mm, "end": v(1.97, 31.2) * mm});
            skLineSegment(sketch, "E837", {"start": v(1.97, 31.2) * mm, "end": v(1.83, 31.17) * mm});
            skLineSegment(sketch, "E838", {"start": v(1.83, 31.17) * mm, "end": v(1.7, 31.1) * mm});
            skLineSegment(sketch, "E839", {"start": v(1.7, 31.1) * mm, "end": v(1.6, 30.98) * mm});
            skLineSegment(sketch, "E840", {"start": v(1.6, 30.98) * mm, "end": v(1.54, 30.84) * mm});
            skLineSegment(sketch, "E841", {"start": v(1.54, 30.84) * mm, "end": v(1.5, 30.24) * mm});
            skLineSegment(sketch, "E842", {"start": v(1.5, 30.24) * mm, "end": v(1.47, 30.1) * mm});
            skLineSegment(sketch, "E843", {"start": v(1.47, 30.1) * mm, "end": v(1.43, 29.98) * mm});
            skLineSegment(sketch, "E844", {"start": v(1.43, 29.98) * mm, "end": v(1.38, 29.86) * mm});
            skLineSegment(sketch, "E845", {"start": v(1.38, 29.86) * mm, "end": v(1.32, 29.75) * mm});
            skLineSegment(sketch, "E846", {"start": v(1.32, 29.75) * mm, "end": v(1.25, 29.64) * mm});
            skLineSegment(sketch, "E847", {"start": v(1.25, 29.64) * mm, "end": v(1.17, 29.54) * mm});
            skLineSegment(sketch, "E848", {"start": v(1.17, 29.54) * mm, "end": v(1.08, 29.45) * mm});
            skLineSegment(sketch, "E849", {"start": v(1.08, 29.45) * mm, "end": v(0.98, 29.36) * mm});
            skLineSegment(sketch, "E850", {"start": v(0.98, 29.36) * mm, "end": v(0.88, 29.29) * mm});
            skLineSegment(sketch, "E851", {"start": v(0.88, 29.29) * mm, "end": v(0.77, 29.22) * mm});
            skLineSegment(sketch, "E852", {"start": v(0.77, 29.22) * mm, "end": v(0.65, 29.15) * mm});
            skLineSegment(sketch, "E853", {"start": v(0.65, 29.15) * mm, "end": v(0.53, 29.1) * mm});
            skLineSegment(sketch, "E854", {"start": v(0.53, 29.1) * mm, "end": v(0.4, 29.06) * mm});
            skLineSegment(sketch, "E855", {"start": v(0.4, 29.06) * mm, "end": v(0.27, 29.03) * mm});
            skLineSegment(sketch, "E856", {"start": v(0.27, 29.03) * mm, "end": v(0.14, 29) * mm});
            skLineSegment(sketch, "E857", {"start": v(0.14, 29) * mm, "end": v(0, 29) * mm});
            skLineSegment(sketch, "E858", {"start": v(0, 29) * mm, "end": v(-0.14, 29) * mm});
            skLineSegment(sketch, "E859", {"start": v(-0.14, 29) * mm, "end": v(-0.27, 29.03) * mm});
            skLineSegment(sketch, "E860", {"start": v(-0.27, 29.03) * mm, "end": v(-0.4, 29.06) * mm});
            skLineSegment(sketch, "E861", {"start": v(-0.4, 29.06) * mm, "end": v(-0.53, 29.1) * mm});
            skLineSegment(sketch, "E862", {"start": v(-0.53, 29.1) * mm, "end": v(-0.65, 29.15) * mm});
            skLineSegment(sketch, "E863", {"start": v(-0.65, 29.15) * mm, "end": v(-0.77, 29.22) * mm});
            skLineSegment(sketch, "E864", {"start": v(-0.77, 29.22) * mm, "end": v(-0.88, 29.28) * mm});
            skLineSegment(sketch, "E865", {"start": v(-0.88, 29.28) * mm, "end": v(-0.98, 29.36) * mm});
            skLineSegment(sketch, "E866", {"start": v(-0.98, 29.36) * mm, "end": v(-1.08, 29.45) * mm});
            skLineSegment(sketch, "E867", {"start": v(-1.08, 29.45) * mm, "end": v(-1.17, 29.54) * mm});
            skLineSegment(sketch, "E868", {"start": v(-1.17, 29.54) * mm, "end": v(-1.25, 29.64) * mm});
            skLineSegment(sketch, "E869", {"start": v(-1.25, 29.64) * mm, "end": v(-1.32, 29.75) * mm});
            skLineSegment(sketch, "E870", {"start": v(-1.32, 29.75) * mm, "end": v(-1.38, 29.86) * mm});
            skLineSegment(sketch, "E871", {"start": v(-1.38, 29.86) * mm, "end": v(-1.43, 29.98) * mm});
            skLineSegment(sketch, "E872", {"start": v(-1.43, 29.98) * mm, "end": v(-1.47, 30.1) * mm});
            skLineSegment(sketch, "E873", {"start": v(-1.47, 30.1) * mm, "end": v(-1.5, 30.24) * mm});
            skLineSegment(sketch, "E874", {"start": v(-1.5, 30.24) * mm, "end": v(-1.54, 30.84) * mm});
            skLineSegment(sketch, "E875", {"start": v(-1.54, 30.84) * mm, "end": v(-1.6, 30.98) * mm});
            skLineSegment(sketch, "E876", {"start": v(-1.6, 30.98) * mm, "end": v(-1.7, 31.1) * mm});
            skLineSegment(sketch, "E877", {"start": v(-1.7, 31.1) * mm, "end": v(-1.83, 31.17) * mm});
            skLineSegment(sketch, "E878", {"start": v(-1.83, 31.17) * mm, "end": v(-1.97, 31.2) * mm});
            skLineSegment(sketch, "E879", {"start": v(-1.97, 31.2) * mm, "end": v(-2.45, 31.16) * mm});
            skLineSegment(sketch, "E880", {"start": v(-2.45, 31.16) * mm, "end": v(-2.94, 31.12) * mm});
            skLineSegment(sketch, "E881", {"start": v(-2.94, 31.12) * mm, "end": v(-3.07, 31.07) * mm});
            skLineSegment(sketch, "E882", {"start": v(-3.07, 31.07) * mm, "end": v(-3.19, 30.98) * mm});
            skLineSegment(sketch, "E883", {"start": v(-3.19, 30.98) * mm, "end": v(-3.27, 30.85) * mm});
            skLineSegment(sketch, "E884", {"start": v(-3.27, 30.85) * mm, "end": v(-3.3, 30.7) * mm});
            skLineSegment(sketch, "E885", {"start": v(-3.3, 30.7) * mm, "end": v(-3.25, 30.1) * mm});
            skLineSegment(sketch, "E886", {"start": v(-3.25, 30.1) * mm, "end": v(-3.26, 29.97) * mm});
            skLineSegment(sketch, "E887", {"start": v(-3.26, 29.97) * mm, "end": v(-3.28, 29.84) * mm});
            skLineSegment(sketch, "E888", {"start": v(-3.28, 29.84) * mm, "end": v(-3.3, 29.71) * mm});
            skLineSegment(sketch, "E889", {"start": v(-3.3, 29.71) * mm, "end": v(-3.35, 29.6) * mm});
            skLineSegment(sketch, "E890", {"start": v(-3.35, 29.6) * mm, "end": v(-3.4, 29.47) * mm});
            skLineSegment(sketch, "E891", {"start": v(-3.4, 29.47) * mm, "end": v(-3.47, 29.36) * mm});
            skLineSegment(sketch, "E892", {"start": v(-3.47, 29.36) * mm, "end": v(-3.54, 29.26) * mm});
            skLineSegment(sketch, "E893", {"start": v(-3.54, 29.26) * mm, "end": v(-3.62, 29.16) * mm});
            skLineSegment(sketch, "E894", {"start": v(-3.62, 29.16) * mm, "end": v(-3.71, 29.06) * mm});
            skLineSegment(sketch, "E895", {"start": v(-3.71, 29.06) * mm, "end": v(-3.81, 28.98) * mm});
            skLineSegment(sketch, "E896", {"start": v(-3.81, 28.98) * mm, "end": v(-3.92, 28.9) * mm});
            skLineSegment(sketch, "E897", {"start": v(-3.92, 28.9) * mm, "end": v(-4.03, 28.83) * mm});
            skLineSegment(sketch, "E898", {"start": v(-4.03, 28.83) * mm, "end": v(-4.15, 28.77) * mm});
            skLineSegment(sketch, "E899", {"start": v(-4.15, 28.77) * mm, "end": v(-4.27, 28.71) * mm});
            skLineSegment(sketch, "E900", {"start": v(-4.27, 28.71) * mm, "end": v(-4.4, 28.67) * mm});
            skLineSegment(sketch, "E901", {"start": v(-4.4, 28.67) * mm, "end": v(-4.54, 28.64) * mm});
            skLineSegment(sketch, "E902", {"start": v(-4.54, 28.64) * mm, "end": v(-4.67, 28.63) * mm});
            skLineSegment(sketch, "E903", {"start": v(-4.67, 28.63) * mm, "end": v(-4.81, 28.63) * mm});
            skLineSegment(sketch, "E904", {"start": v(-4.81, 28.63) * mm, "end": v(-4.95, 28.64) * mm});
            skLineSegment(sketch, "E905", {"start": v(-4.95, 28.64) * mm, "end": v(-5.08, 28.66) * mm});
            skLineSegment(sketch, "E906", {"start": v(-5.08, 28.66) * mm, "end": v(-5.2, 28.7) * mm});
            skLineSegment(sketch, "E907", {"start": v(-5.2, 28.7) * mm, "end": v(-5.33, 28.74) * mm});
            skLineSegment(sketch, "E908", {"start": v(-5.33, 28.74) * mm, "end": v(-5.45, 28.79) * mm});
            skLineSegment(sketch, "E909", {"start": v(-5.45, 28.79) * mm, "end": v(-5.56, 28.85) * mm});
            skLineSegment(sketch, "E910", {"start": v(-5.56, 28.85) * mm, "end": v(-5.67, 28.92) * mm});
            skLineSegment(sketch, "E911", {"start": v(-5.67, 28.92) * mm, "end": v(-5.77, 29) * mm});
            skLineSegment(sketch, "E912", {"start": v(-5.77, 29) * mm, "end": v(-5.87, 29.08) * mm});
            skLineSegment(sketch, "E913", {"start": v(-5.87, 29.08) * mm, "end": v(-5.96, 29.18) * mm});
            skLineSegment(sketch, "E914", {"start": v(-5.96, 29.18) * mm, "end": v(-6.03, 29.28) * mm});
            skLineSegment(sketch, "E915", {"start": v(-6.03, 29.28) * mm, "end": v(-6.1, 29.39) * mm});
            skLineSegment(sketch, "E916", {"start": v(-6.1, 29.39) * mm, "end": v(-6.16, 29.5) * mm});
            skLineSegment(sketch, "E917", {"start": v(-6.16, 29.5) * mm, "end": v(-6.21, 29.63) * mm});
            skLineSegment(sketch, "E918", {"start": v(-6.21, 29.63) * mm, "end": v(-6.35, 30.22) * mm});
            skLineSegment(sketch, "E919", {"start": v(-6.35, 30.22) * mm, "end": v(-6.43, 30.35) * mm});
            skLineSegment(sketch, "E920", {"start": v(-6.43, 30.35) * mm, "end": v(-6.54, 30.45) * mm});
            skLineSegment(sketch, "E921", {"start": v(-6.54, 30.45) * mm, "end": v(-6.69, 30.5) * mm});
            skLineSegment(sketch, "E922", {"start": v(-6.69, 30.5) * mm, "end": v(-6.82, 30.5) * mm});
            skLineSegment(sketch, "E923", {"start": v(-6.82, 30.5) * mm, "end": v(-7.3, 30.4) * mm});
            skLineSegment(sketch, "E924", {"start": v(-7.3, 30.4) * mm, "end": v(-7.77, 30.27) * mm});
            skLineSegment(sketch, "E925", {"start": v(-7.77, 30.27) * mm, "end": v(-7.89, 30.21) * mm});
            skLineSegment(sketch, "E926", {"start": v(-7.89, 30.21) * mm, "end": v(-8, 30.1) * mm});
            skLineSegment(sketch, "E927", {"start": v(-8, 30.1) * mm, "end": v(-8.05, 29.96) * mm});
            skLineSegment(sketch, "E928", {"start": v(-8.05, 29.96) * mm, "end": v(-8.06, 29.8) * mm});
            skLineSegment(sketch, "E929", {"start": v(-8.06, 29.8) * mm, "end": v(-7.91, 29.22) * mm});
            skLineSegment(sketch, "E930", {"start": v(-7.91, 29.22) * mm, "end": v(-7.9, 29.09) * mm});
            skLineSegment(sketch, "E931", {"start": v(-7.9, 29.09) * mm, "end": v(-7.9, 28.96) * mm});
            skLineSegment(sketch, "E932", {"start": v(-7.9, 28.96) * mm, "end": v(-7.92, 28.83) * mm});
            skLineSegment(sketch, "E933", {"start": v(-7.92, 28.83) * mm, "end": v(-7.94, 28.7) * mm});
            skLineSegment(sketch, "E934", {"start": v(-7.94, 28.7) * mm, "end": v(-7.97, 28.58) * mm});
            skLineSegment(sketch, "E935", {"start": v(-7.97, 28.58) * mm, "end": v(-8.02, 28.46) * mm});
            skLineSegment(sketch, "E936", {"start": v(-8.02, 28.46) * mm, "end": v(-8.07, 28.34) * mm});
            skLineSegment(sketch, "E937", {"start": v(-8.07, 28.34) * mm, "end": v(-8.14, 28.23) * mm});
            skLineSegment(sketch, "E938", {"start": v(-8.14, 28.23) * mm, "end": v(-8.21, 28.12) * mm});
            skLineSegment(sketch, "E939", {"start": v(-8.21, 28.12) * mm, "end": v(-8.3, 28.02) * mm});
            skLineSegment(sketch, "E940", {"start": v(-8.3, 28.02) * mm, "end": v(-8.39, 27.93) * mm});
            skLineSegment(sketch, "E941", {"start": v(-8.39, 27.93) * mm, "end": v(-8.49, 27.84) * mm});
            skLineSegment(sketch, "E942", {"start": v(-8.49, 27.84) * mm, "end": v(-8.6, 27.76) * mm});
            skLineSegment(sketch, "E943", {"start": v(-8.6, 27.76) * mm, "end": v(-8.71, 27.7) * mm});
            skLineSegment(sketch, "E944", {"start": v(-8.71, 27.7) * mm, "end": v(-8.83, 27.63) * mm});
            skLineSegment(sketch, "E945", {"start": v(-8.83, 27.63) * mm, "end": v(-8.96, 27.58) * mm});
            skLineSegment(sketch, "E946", {"start": v(-8.96, 27.58) * mm, "end": v(-9.1, 27.55) * mm});
            skLineSegment(sketch, "E947", {"start": v(-9.1, 27.55) * mm, "end": v(-9.23, 27.52) * mm});
            skLineSegment(sketch, "E948", {"start": v(-9.23, 27.52) * mm, "end": v(-9.36, 27.51) * mm});
            skLineSegment(sketch, "E949", {"start": v(-9.36, 27.51) * mm, "end": v(-9.5, 27.51) * mm});
            skLineSegment(sketch, "E950", {"start": v(-9.5, 27.51) * mm, "end": v(-9.63, 27.53) * mm});
            skLineSegment(sketch, "E951", {"start": v(-9.63, 27.53) * mm, "end": v(-9.76, 27.55) * mm});
            skLineSegment(sketch, "E952", {"start": v(-9.76, 27.55) * mm, "end": v(-9.89, 27.58) * mm});
            skLineSegment(sketch, "E953", {"start": v(-9.89, 27.58) * mm, "end": v(-10, 27.62) * mm});
            skLineSegment(sketch, "E954", {"start": v(-10, 27.62) * mm, "end": v(-10.13, 27.67) * mm});
            skLineSegment(sketch, "E955", {"start": v(-10.13, 27.67) * mm, "end": v(-10.24, 27.74) * mm});
            skLineSegment(sketch, "E956", {"start": v(-10.24, 27.74) * mm, "end": v(-10.35, 27.8) * mm});
            skLineSegment(sketch, "E957", {"start": v(-10.35, 27.8) * mm, "end": v(-10.45, 27.89) * mm});
            skLineSegment(sketch, "E958", {"start": v(-10.45, 27.89) * mm, "end": v(-10.54, 27.98) * mm});
            skLineSegment(sketch, "E959", {"start": v(-10.54, 27.98) * mm, "end": v(-10.63, 28.07) * mm});
            skLineSegment(sketch, "E960", {"start": v(-10.63, 28.07) * mm, "end": v(-10.7, 28.18) * mm});
            skLineSegment(sketch, "E961", {"start": v(-10.7, 28.18) * mm, "end": v(-10.77, 28.3) * mm});
            skLineSegment(sketch, "E962", {"start": v(-10.77, 28.3) * mm, "end": v(-11, 28.85) * mm});
            skLineSegment(sketch, "E963", {"start": v(-11, 28.85) * mm, "end": v(-11.1, 28.97) * mm});
            skLineSegment(sketch, "E964", {"start": v(-11.1, 28.97) * mm, "end": v(-11.23, 29.05) * mm});
            skLineSegment(sketch, "E965", {"start": v(-11.23, 29.05) * mm, "end": v(-11.38, 29.08) * mm});
            skLineSegment(sketch, "E966", {"start": v(-11.38, 29.08) * mm, "end": v(-11.5, 29.06) * mm});
            skLineSegment(sketch, "E967", {"start": v(-11.5, 29.06) * mm, "end": v(-11.96, 28.88) * mm});
            skLineSegment(sketch, "E968", {"start": v(-11.96, 28.88) * mm, "end": v(-12.4, 28.68) * mm});
            skLineSegment(sketch, "E969", {"start": v(-12.4, 28.68) * mm, "end": v(-12.52, 28.6) * mm});
            skLineSegment(sketch, "E970", {"start": v(-12.52, 28.6) * mm, "end": v(-12.6, 28.48) * mm});
            skLineSegment(sketch, "E971", {"start": v(-12.6, 28.48) * mm, "end": v(-12.64, 28.33) * mm});
            skLineSegment(sketch, "E972", {"start": v(-12.64, 28.33) * mm, "end": v(-12.62, 28.18) * mm});
            skLineSegment(sketch, "E973", {"start": v(-12.62, 28.18) * mm, "end": v(-12.39, 27.62) * mm});
            skLineSegment(sketch, "E974", {"start": v(-12.39, 27.62) * mm, "end": v(-12.36, 27.5) * mm});
            skLineSegment(sketch, "E975", {"start": v(-12.36, 27.5) * mm, "end": v(-12.34, 27.36) * mm});
            skLineSegment(sketch, "E976", {"start": v(-12.34, 27.36) * mm, "end": v(-12.33, 27.24) * mm});
            skLineSegment(sketch, "E977", {"start": v(-12.33, 27.24) * mm, "end": v(-12.33, 27.1) * mm});
            skLineSegment(sketch, "E978", {"start": v(-12.33, 27.1) * mm, "end": v(-12.35, 26.98) * mm});
            skLineSegment(sketch, "E979", {"start": v(-12.35, 26.98) * mm, "end": v(-12.37, 26.85) * mm});
            skLineSegment(sketch, "E980", {"start": v(-12.37, 26.85) * mm, "end": v(-12.4, 26.73) * mm});
            skLineSegment(sketch, "E981", {"start": v(-12.4, 26.73) * mm, "end": v(-12.46, 26.6) * mm});
            skLineSegment(sketch, "E982", {"start": v(-12.46, 26.6) * mm, "end": v(-12.51, 26.5) * mm});
            skLineSegment(sketch, "E983", {"start": v(-12.51, 26.5) * mm, "end": v(-12.58, 26.38) * mm});
            skLineSegment(sketch, "E984", {"start": v(-12.58, 26.38) * mm, "end": v(-12.65, 26.27) * mm});
            skLineSegment(sketch, "E985", {"start": v(-12.65, 26.27) * mm, "end": v(-12.74, 26.17) * mm});
            skLineSegment(sketch, "E986", {"start": v(-12.74, 26.17) * mm, "end": v(-12.83, 26.08) * mm});
            skLineSegment(sketch, "E987", {"start": v(-12.83, 26.08) * mm, "end": v(-12.94, 25.99) * mm});
            skLineSegment(sketch, "E988", {"start": v(-12.94, 25.99) * mm, "end": v(-13.05, 25.9) * mm});
            skLineSegment(sketch, "E989", {"start": v(-13.05, 25.9) * mm, "end": v(-13.16, 25.84) * mm});
            skLineSegment(sketch, "E990", {"start": v(-13.16, 25.84) * mm, "end": v(-13.3, 25.78) * mm});
            skLineSegment(sketch, "E991", {"start": v(-13.3, 25.78) * mm, "end": v(-13.42, 25.74) * mm});
            skLineSegment(sketch, "E992", {"start": v(-13.42, 25.74) * mm, "end": v(-13.55, 25.7) * mm});
            skLineSegment(sketch, "E993", {"start": v(-13.55, 25.7) * mm, "end": v(-13.69, 25.69) * mm});
            skLineSegment(sketch, "E994", {"start": v(-13.69, 25.69) * mm, "end": v(-13.82, 25.68) * mm});
            skLineSegment(sketch, "E995", {"start": v(-13.82, 25.68) * mm, "end": v(-13.95, 25.68) * mm});
            skLineSegment(sketch, "E996", {"start": v(-13.95, 25.68) * mm, "end": v(-14.08, 25.7) * mm});
            skLineSegment(sketch, "E997", {"start": v(-14.08, 25.7) * mm, "end": v(-14.2, 25.72) * mm});
            skLineSegment(sketch, "E998", {"start": v(-14.2, 25.72) * mm, "end": v(-14.33, 25.75) * mm});
            skLineSegment(sketch, "E999", {"start": v(-14.33, 25.75) * mm, "end": v(-14.45, 25.8) * mm});
            skLineSegment(sketch, "E1000", {"start": v(-14.45, 25.8) * mm, "end": v(-14.57, 25.85) * mm});
            skLineSegment(sketch, "E1001", {"start": v(-14.57, 25.85) * mm, "end": v(-14.68, 25.9) * mm});
            skLineSegment(sketch, "E1002", {"start": v(-14.68, 25.9) * mm, "end": v(-14.79, 25.98) * mm});
            skLineSegment(sketch, "E1003", {"start": v(-14.79, 25.98) * mm, "end": v(-14.89, 26.06) * mm});
            skLineSegment(sketch, "E1004", {"start": v(-14.89, 26.06) * mm, "end": v(-14.98, 26.16) * mm});
            skLineSegment(sketch, "E1005", {"start": v(-14.98, 26.16) * mm, "end": v(-15.07, 26.26) * mm});
            skLineSegment(sketch, "E1006", {"start": v(-15.07, 26.26) * mm, "end": v(-15.38, 26.78) * mm});
            skLineSegment(sketch, "E1007", {"start": v(-15.38, 26.78) * mm, "end": v(-15.5, 26.88) * mm});
            skLineSegment(sketch, "E1008", {"start": v(-15.5, 26.88) * mm, "end": v(-15.63, 26.93) * mm});
            skLineSegment(sketch, "E1009", {"start": v(-15.63, 26.93) * mm, "end": v(-15.78, 26.94) * mm});
            skLineSegment(sketch, "E1010", {"start": v(-15.78, 26.94) * mm, "end": v(-15.91, 26.9) * mm});
            skLineSegment(sketch, "E1011", {"start": v(-15.91, 26.9) * mm, "end": v(-16.33, 26.65) * mm});
            skLineSegment(sketch, "E1012", {"start": v(-16.33, 26.65) * mm, "end": v(-16.74, 26.4) * mm});
            skLineSegment(sketch, "E1013", {"start": v(-16.74, 26.4) * mm, "end": v(-16.84, 26.3) * mm});
            skLineSegment(sketch, "E1014", {"start": v(-16.84, 26.3) * mm, "end": v(-16.9, 26.16) * mm});
            skLineSegment(sketch, "E1015", {"start": v(-16.9, 26.16) * mm, "end": v(-16.92, 26) * mm});
            skLineSegment(sketch, "E1016", {"start": v(-16.92, 26) * mm, "end": v(-16.88, 25.86) * mm});
            skLineSegment(sketch, "E1017", {"start": v(-16.88, 25.86) * mm, "end": v(-16.56, 25.34) * mm});
            skLineSegment(sketch, "E1018", {"start": v(-16.56, 25.34) * mm, "end": v(-16.5, 25.22) * mm});
            skLineSegment(sketch, "E1019", {"start": v(-16.5, 25.22) * mm, "end": v(-16.47, 25.1) * mm});
            skLineSegment(sketch, "E1020", {"start": v(-16.47, 25.1) * mm, "end": v(-16.44, 24.97) * mm});
            skLineSegment(sketch, "E1021", {"start": v(-16.44, 24.97) * mm, "end": v(-16.42, 24.84) * mm});
            skLineSegment(sketch, "E1022", {"start": v(-16.42, 24.84) * mm, "end": v(-16.42, 24.71) * mm});
            skLineSegment(sketch, "E1023", {"start": v(-16.42, 24.71) * mm, "end": v(-16.42, 24.59) * mm});
            skLineSegment(sketch, "E1024", {"start": v(-16.42, 24.59) * mm, "end": v(-16.44, 24.46) * mm});
            skLineSegment(sketch, "E1025", {"start": v(-16.44, 24.46) * mm, "end": v(-16.46, 24.33) * mm});
            skLineSegment(sketch, "E1026", {"start": v(-16.46, 24.33) * mm, "end": v(-16.5, 24.2) * mm});
            skLineSegment(sketch, "E1027", {"start": v(-16.5, 24.2) * mm, "end": v(-16.55, 24.09) * mm});
            skLineSegment(sketch, "E1028", {"start": v(-16.55, 24.09) * mm, "end": v(-16.6, 23.97) * mm});
            skLineSegment(sketch, "E1029", {"start": v(-16.6, 23.97) * mm, "end": v(-16.68, 23.86) * mm});
            skLineSegment(sketch, "E1030", {"start": v(-16.68, 23.86) * mm, "end": v(-16.75, 23.75) * mm});
            skLineSegment(sketch, "E1031", {"start": v(-16.75, 23.75) * mm, "end": v(-16.84, 23.65) * mm});
            skLineSegment(sketch, "E1032", {"start": v(-16.84, 23.65) * mm, "end": v(-16.94, 23.55) * mm});
            skLineSegment(sketch, "E1033", {"start": v(-16.94, 23.55) * mm, "end": v(-17.04, 23.46) * mm});
            skLineSegment(sketch, "E1034", {"start": v(-17.04, 23.46) * mm, "end": v(-17.16, 23.39) * mm});
            skLineSegment(sketch, "E1035", {"start": v(-17.16, 23.39) * mm, "end": v(-17.28, 23.32) * mm});
            skLineSegment(sketch, "E1036", {"start": v(-17.28, 23.32) * mm, "end": v(-17.4, 23.27) * mm});
            skLineSegment(sketch, "E1037", {"start": v(-17.4, 23.27) * mm, "end": v(-17.54, 23.23) * mm});
            skLineSegment(sketch, "E1038", {"start": v(-17.54, 23.23) * mm, "end": v(-17.66, 23.2) * mm});
            skLineSegment(sketch, "E1039", {"start": v(-17.66, 23.2) * mm, "end": v(-17.8, 23.18) * mm});
            skLineSegment(sketch, "E1040", {"start": v(-17.8, 23.18) * mm, "end": v(-17.92, 23.18) * mm});
            skLineSegment(sketch, "E1041", {"start": v(-17.92, 23.18) * mm, "end": v(-18.05, 23.18) * mm});
            skLineSegment(sketch, "E1042", {"start": v(-18.05, 23.18) * mm, "end": v(-18.18, 23.2) * mm});
            skLineSegment(sketch, "E1043", {"start": v(-18.18, 23.2) * mm, "end": v(-18.3, 23.21) * mm});
            skLineSegment(sketch, "E1044", {"start": v(-18.3, 23.21) * mm, "end": v(-18.43, 23.25) * mm});
            skLineSegment(sketch, "E1045", {"start": v(-18.43, 23.25) * mm, "end": v(-18.55, 23.3) * mm});
            skLineSegment(sketch, "E1046", {"start": v(-18.55, 23.3) * mm, "end": v(-18.67, 23.35) * mm});
            skLineSegment(sketch, "E1047", {"start": v(-18.67, 23.35) * mm, "end": v(-18.78, 23.41) * mm});
            skLineSegment(sketch, "E1048", {"start": v(-18.78, 23.41) * mm, "end": v(-18.89, 23.5) * mm});
            skLineSegment(sketch, "E1049", {"start": v(-18.89, 23.5) * mm, "end": v(-18.99, 23.58) * mm});
            skLineSegment(sketch, "E1050", {"start": v(-18.99, 23.58) * mm, "end": v(-19.38, 24.04) * mm});
            skLineSegment(sketch, "E1051", {"start": v(-19.38, 24.04) * mm, "end": v(-19.5, 24.13) * mm});
            skLineSegment(sketch, "E1052", {"start": v(-19.5, 24.13) * mm, "end": v(-19.65, 24.16) * mm});
            skLineSegment(sketch, "E1053", {"start": v(-19.65, 24.16) * mm, "end": v(-19.8, 24.14) * mm});
            skLineSegment(sketch, "E1054", {"start": v(-19.8, 24.14) * mm, "end": v(-19.92, 24.08) * mm});
            skLineSegment(sketch, "E1055", {"start": v(-19.92, 24.08) * mm, "end": v(-20.3, 23.77) * mm});
            skLineSegment(sketch, "E1056", {"start": v(-20.3, 23.77) * mm, "end": v(-20.67, 23.45) * mm});
            skLineSegment(sketch, "E1057", {"start": v(-20.67, 23.45) * mm, "end": v(-20.74, 23.34) * mm});
            skLineSegment(sketch, "E1058", {"start": v(-20.74, 23.34) * mm, "end": v(-20.79, 23.19) * mm});
            skLineSegment(sketch, "E1059", {"start": v(-20.79, 23.19) * mm, "end": v(-20.78, 23.04) * mm});
            skLineSegment(sketch, "E1060", {"start": v(-20.78, 23.04) * mm, "end": v(-20.72, 22.9) * mm});
            skLineSegment(sketch, "E1061", {"start": v(-20.72, 22.9) * mm, "end": v(-20.32, 22.44) * mm});
            skLineSegment(sketch, "E1062", {"start": v(-20.32, 22.44) * mm, "end": v(-20.25, 22.33) * mm});
            skLineSegment(sketch, "E1063", {"start": v(-20.25, 22.33) * mm, "end": v(-20.19, 22.21) * mm});
            skLineSegment(sketch, "E1064", {"start": v(-20.19, 22.21) * mm, "end": v(-20.14, 22.1) * mm});
            skLineSegment(sketch, "E1065", {"start": v(-20.14, 22.1) * mm, "end": v(-20.1, 21.97) * mm});
            skLineSegment(sketch, "E1066", {"start": v(-20.1, 21.97) * mm, "end": v(-20.08, 21.84) * mm});
            skLineSegment(sketch, "E1067", {"start": v(-20.08, 21.84) * mm, "end": v(-20.07, 21.72) * mm});
            skLineSegment(sketch, "E1068", {"start": v(-20.07, 21.72) * mm, "end": v(-20.06, 21.59) * mm});
            skLineSegment(sketch, "E1069", {"start": v(-20.06, 21.59) * mm, "end": v(-20.07, 21.46) * mm});
            skLineSegment(sketch, "E1070", {"start": v(-20.07, 21.46) * mm, "end": v(-20.09, 21.33) * mm});
            skLineSegment(sketch, "E1071", {"start": v(-20.09, 21.33) * mm, "end": v(-20.11, 21.2) * mm});
            skLineSegment(sketch, "E1072", {"start": v(-20.11, 21.2) * mm, "end": v(-20.15, 21.08) * mm});
            skLineSegment(sketch, "E1073", {"start": v(-20.15, 21.08) * mm, "end": v(-20.2, 20.95) * mm});
            skLineSegment(sketch, "E1074", {"start": v(-20.2, 20.95) * mm, "end": v(-20.26, 20.84) * mm});
            skLineSegment(sketch, "E1075", {"start": v(-20.26, 20.84) * mm, "end": v(-20.33, 20.72) * mm});
            skLineSegment(sketch, "E1076", {"start": v(-20.33, 20.72) * mm, "end": v(-20.41, 20.6) * mm});
            skLineSegment(sketch, "E1077", {"start": v(-20.41, 20.6) * mm, "end": v(-20.5, 20.5) * mm});
            skLineSegment(sketch, "E1078", {"start": v(-20.5, 20.5) * mm, "end": v(-20.6, 20.41) * mm});
            skLineSegment(sketch, "E1079", {"start": v(-20.6, 20.41) * mm, "end": v(-20.72, 20.33) * mm});
            skLineSegment(sketch, "E1080", {"start": v(-20.72, 20.33) * mm, "end": v(-20.83, 20.26) * mm});
            skLineSegment(sketch, "E1081", {"start": v(-20.83, 20.26) * mm, "end": v(-20.95, 20.2) * mm});
            skLineSegment(sketch, "E1082", {"start": v(-20.95, 20.2) * mm, "end": v(-21.08, 20.15) * mm});
            skLineSegment(sketch, "E1083", {"start": v(-21.08, 20.15) * mm, "end": v(-21.2, 20.11) * mm});
            skLineSegment(sketch, "E1084", {"start": v(-21.2, 20.11) * mm, "end": v(-21.33, 20.09) * mm});
            skLineSegment(sketch, "E1085", {"start": v(-21.33, 20.09) * mm, "end": v(-21.46, 20.07) * mm});
            skLineSegment(sketch, "E1086", {"start": v(-21.46, 20.07) * mm, "end": v(-21.59, 20.06) * mm});
            skLineSegment(sketch, "E1087", {"start": v(-21.59, 20.06) * mm, "end": v(-21.72, 20.06) * mm});
            skLineSegment(sketch, "E1088", {"start": v(-21.72, 20.06) * mm, "end": v(-21.84, 20.08) * mm});
            skLineSegment(sketch, "E1089", {"start": v(-21.84, 20.08) * mm, "end": v(-21.97, 20.1) * mm});
            skLineSegment(sketch, "E1090", {"start": v(-21.97, 20.1) * mm, "end": v(-22.1, 20.14) * mm});
            skLineSegment(sketch, "E1091", {"start": v(-22.1, 20.14) * mm, "end": v(-22.21, 20.19) * mm});
            skLineSegment(sketch, "E1092", {"start": v(-22.21, 20.19) * mm, "end": v(-22.33, 20.25) * mm});
            skLineSegment(sketch, "E1093", {"start": v(-22.33, 20.25) * mm, "end": v(-22.44, 20.32) * mm});
            skLineSegment(sketch, "E1094", {"start": v(-22.44, 20.32) * mm, "end": v(-22.9, 20.72) * mm});
            skLineSegment(sketch, "E1095", {"start": v(-22.9, 20.72) * mm, "end": v(-23.04, 20.78) * mm});
            skLineSegment(sketch, "E1096", {"start": v(-23.04, 20.78) * mm, "end": v(-23.19, 20.79) * mm});
            skLineSegment(sketch, "E1097", {"start": v(-23.19, 20.79) * mm, "end": v(-23.34, 20.74) * mm});
            skLineSegment(sketch, "E1098", {"start": v(-23.34, 20.74) * mm, "end": v(-23.45, 20.67) * mm});
            skLineSegment(sketch, "E1099", {"start": v(-23.45, 20.67) * mm, "end": v(-23.77, 20.3) * mm});
            skLineSegment(sketch, "E1100", {"start": v(-23.77, 20.3) * mm, "end": v(-24.08, 19.92) * mm});
            skLineSegment(sketch, "E1101", {"start": v(-24.08, 19.92) * mm, "end": v(-24.14, 19.8) * mm});
            skLineSegment(sketch, "E1102", {"start": v(-24.14, 19.8) * mm, "end": v(-24.16, 19.65) * mm});
            skLineSegment(sketch, "E1103", {"start": v(-24.16, 19.65) * mm, "end": v(-24.13, 19.5) * mm});
            skLineSegment(sketch, "E1104", {"start": v(-24.13, 19.5) * mm, "end": v(-24.04, 19.38) * mm});
            skLineSegment(sketch, "E1105", {"start": v(-24.04, 19.38) * mm, "end": v(-23.58, 18.99) * mm});
            skLineSegment(sketch, "E1106", {"start": v(-23.58, 18.99) * mm, "end": v(-23.5, 18.89) * mm});
            skLineSegment(sketch, "E1107", {"start": v(-23.5, 18.89) * mm, "end": v(-23.42, 18.78) * mm});
            skLineSegment(sketch, "E1108", {"start": v(-23.42, 18.78) * mm, "end": v(-23.35, 18.67) * mm});
            skLineSegment(sketch, "E1109", {"start": v(-23.35, 18.67) * mm, "end": v(-23.3, 18.55) * mm});
            skLineSegment(sketch, "E1110", {"start": v(-23.3, 18.55) * mm, "end": v(-23.25, 18.43) * mm});
            skLineSegment(sketch, "E1111", {"start": v(-23.25, 18.43) * mm, "end": v(-23.21, 18.3) * mm});
            skLineSegment(sketch, "E1112", {"start": v(-23.21, 18.3) * mm, "end": v(-23.2, 18.18) * mm});
            skLineSegment(sketch, "E1113", {"start": v(-23.2, 18.18) * mm, "end": v(-23.18, 18.05) * mm});
            skLineSegment(sketch, "E1114", {"start": v(-23.18, 18.05) * mm, "end": v(-23.18, 17.92) * mm});
            skLineSegment(sketch, "E1115", {"start": v(-23.18, 17.92) * mm, "end": v(-23.18, 17.8) * mm});
            skLineSegment(sketch, "E1116", {"start": v(-23.18, 17.8) * mm, "end": v(-23.2, 17.66) * mm});
            skLineSegment(sketch, "E1117", {"start": v(-23.2, 17.66) * mm, "end": v(-23.23, 17.54) * mm});
            skLineSegment(sketch, "E1118", {"start": v(-23.23, 17.54) * mm, "end": v(-23.27, 17.4) * mm});
            skLineSegment(sketch, "E1119", {"start": v(-23.27, 17.4) * mm, "end": v(-23.32, 17.28) * mm});
            skLineSegment(sketch, "E1120", {"start": v(-23.32, 17.28) * mm, "end": v(-23.39, 17.16) * mm});
            skLineSegment(sketch, "E1121", {"start": v(-23.39, 17.16) * mm, "end": v(-23.46, 17.04) * mm});
            skLineSegment(sketch, "E1122", {"start": v(-23.46, 17.04) * mm, "end": v(-23.55, 16.94) * mm});
            skLineSegment(sketch, "E1123", {"start": v(-23.55, 16.94) * mm, "end": v(-23.65, 16.84) * mm});
            skLineSegment(sketch, "E1124", {"start": v(-23.65, 16.84) * mm, "end": v(-23.75, 16.75) * mm});
            skLineSegment(sketch, "E1125", {"start": v(-23.75, 16.75) * mm, "end": v(-23.86, 16.68) * mm});
            skLineSegment(sketch, "E1126", {"start": v(-23.86, 16.68) * mm, "end": v(-23.97, 16.6) * mm});
            skLineSegment(sketch, "E1127", {"start": v(-23.97, 16.6) * mm, "end": v(-24.09, 16.55) * mm});
            skLineSegment(sketch, "E1128", {"start": v(-24.09, 16.55) * mm, "end": v(-24.2, 16.5) * mm});
            skLineSegment(sketch, "E1129", {"start": v(-24.2, 16.5) * mm, "end": v(-24.33, 16.46) * mm});
            skLineSegment(sketch, "E1130", {"start": v(-24.33, 16.46) * mm, "end": v(-24.46, 16.44) * mm});
            skLineSegment(sketch, "E1131", {"start": v(-24.46, 16.44) * mm, "end": v(-24.59, 16.42) * mm});
            skLineSegment(sketch, "E1132", {"start": v(-24.59, 16.42) * mm, "end": v(-24.71, 16.42) * mm});
            skLineSegment(sketch, "E1133", {"start": v(-24.71, 16.42) * mm, "end": v(-24.84, 16.42) * mm});
            skLineSegment(sketch, "E1134", {"start": v(-24.84, 16.42) * mm, "end": v(-24.97, 16.44) * mm});
            skLineSegment(sketch, "E1135", {"start": v(-24.97, 16.44) * mm, "end": v(-25.1, 16.47) * mm});
            skLineSegment(sketch, "E1136", {"start": v(-25.1, 16.47) * mm, "end": v(-25.22, 16.5) * mm});
            skLineSegment(sketch, "E1137", {"start": v(-25.22, 16.5) * mm, "end": v(-25.34, 16.56) * mm});
            skLineSegment(sketch, "E1138", {"start": v(-25.34, 16.56) * mm, "end": v(-25.86, 16.88) * mm});
            skLineSegment(sketch, "E1139", {"start": v(-25.86, 16.88) * mm, "end": v(-26, 16.92) * mm});
            skLineSegment(sketch, "E1140", {"start": v(-26, 16.92) * mm, "end": v(-26.16, 16.9) * mm});
            skLineSegment(sketch, "E1141", {"start": v(-26.16, 16.9) * mm, "end": v(-26.3, 16.84) * mm});
            skLineSegment(sketch, "E1142", {"start": v(-26.3, 16.84) * mm, "end": v(-26.4, 16.74) * mm});
            skLineSegment(sketch, "E1143", {"start": v(-26.4, 16.74) * mm, "end": v(-26.65, 16.33) * mm});
            skLineSegment(sketch, "E1144", {"start": v(-26.65, 16.33) * mm, "end": v(-26.9, 15.91) * mm});
            skLineSegment(sketch, "E1145", {"start": v(-26.9, 15.91) * mm, "end": v(-26.94, 15.78) * mm});
            skLineSegment(sketch, "E1146", {"start": v(-26.94, 15.78) * mm, "end": v(-26.93, 15.63) * mm});
            skLineSegment(sketch, "E1147", {"start": v(-26.93, 15.63) * mm, "end": v(-26.88, 15.5) * mm});
            skLineSegment(sketch, "E1148", {"start": v(-26.88, 15.5) * mm, "end": v(-26.78, 15.38) * mm});
            skLineSegment(sketch, "E1149", {"start": v(-26.78, 15.38) * mm, "end": v(-26.26, 15.07) * mm});
            skLineSegment(sketch, "E1150", {"start": v(-26.26, 15.07) * mm, "end": v(-26.16, 14.98) * mm});
            skLineSegment(sketch, "E1151", {"start": v(-26.16, 14.98) * mm, "end": v(-26.06, 14.89) * mm});
            skLineSegment(sketch, "E1152", {"start": v(-26.06, 14.89) * mm, "end": v(-25.98, 14.79) * mm});
            skLineSegment(sketch, "E1153", {"start": v(-25.98, 14.79) * mm, "end": v(-25.9, 14.68) * mm});
            skLineSegment(sketch, "E1154", {"start": v(-25.9, 14.68) * mm, "end": v(-25.85, 14.57) * mm});
            skLineSegment(sketch, "E1155", {"start": v(-25.85, 14.57) * mm, "end": v(-25.8, 14.45) * mm});
            skLineSegment(sketch, "E1156", {"start": v(-25.8, 14.45) * mm, "end": v(-25.75, 14.33) * mm});
            skLineSegment(sketch, "E1157", {"start": v(-25.75, 14.33) * mm, "end": v(-25.72, 14.2) * mm});
            skLineSegment(sketch, "E1158", {"start": v(-25.72, 14.2) * mm, "end": v(-25.7, 14.08) * mm});
            skLineSegment(sketch, "E1159", {"start": v(-25.7, 14.08) * mm, "end": v(-25.68, 13.95) * mm});
            skLineSegment(sketch, "E1160", {"start": v(-25.68, 13.95) * mm, "end": v(-25.68, 13.82) * mm});
            skLineSegment(sketch, "E1161", {"start": v(-25.68, 13.82) * mm, "end": v(-25.69, 13.69) * mm});
            skLineSegment(sketch, "E1162", {"start": v(-25.69, 13.69) * mm, "end": v(-25.7, 13.55) * mm});
            skLineSegment(sketch, "E1163", {"start": v(-25.7, 13.55) * mm, "end": v(-25.74, 13.42) * mm});
            skLineSegment(sketch, "E1164", {"start": v(-25.74, 13.42) * mm, "end": v(-25.78, 13.3) * mm});
            skLineSegment(sketch, "E1165", {"start": v(-25.78, 13.3) * mm, "end": v(-25.84, 13.16) * mm});
            skLineSegment(sketch, "E1166", {"start": v(-25.84, 13.16) * mm, "end": v(-25.9, 13.05) * mm});
            skLineSegment(sketch, "E1167", {"start": v(-25.9, 13.05) * mm, "end": v(-25.99, 12.94) * mm});
            skLineSegment(sketch, "E1168", {"start": v(-25.99, 12.94) * mm, "end": v(-26.08, 12.83) * mm});
            skLineSegment(sketch, "E1169", {"start": v(-26.08, 12.83) * mm, "end": v(-26.17, 12.74) * mm});
            skLineSegment(sketch, "E1170", {"start": v(-26.17, 12.74) * mm, "end": v(-26.27, 12.65) * mm});
            skLineSegment(sketch, "E1171", {"start": v(-26.27, 12.65) * mm, "end": v(-26.38, 12.58) * mm});
            skLineSegment(sketch, "E1172", {"start": v(-26.38, 12.58) * mm, "end": v(-26.5, 12.51) * mm});
            skLineSegment(sketch, "E1173", {"start": v(-26.5, 12.51) * mm, "end": v(-26.6, 12.46) * mm});
            skLineSegment(sketch, "E1174", {"start": v(-26.6, 12.46) * mm, "end": v(-26.73, 12.4) * mm});
            skLineSegment(sketch, "E1175", {"start": v(-26.73, 12.4) * mm, "end": v(-26.85, 12.37) * mm});
            skLineSegment(sketch, "E1176", {"start": v(-26.85, 12.37) * mm, "end": v(-26.98, 12.35) * mm});
            skLineSegment(sketch, "E1177", {"start": v(-26.98, 12.35) * mm, "end": v(-27.1, 12.33) * mm});
            skLineSegment(sketch, "E1178", {"start": v(-27.1, 12.33) * mm, "end": v(-27.24, 12.33) * mm});
            skLineSegment(sketch, "E1179", {"start": v(-27.24, 12.33) * mm, "end": v(-27.36, 12.34) * mm});
            skLineSegment(sketch, "E1180", {"start": v(-27.36, 12.34) * mm, "end": v(-27.5, 12.36) * mm});
            skLineSegment(sketch, "E1181", {"start": v(-27.5, 12.36) * mm, "end": v(-27.62, 12.39) * mm});
            skLineSegment(sketch, "E1182", {"start": v(-27.62, 12.39) * mm, "end": v(-28.18, 12.62) * mm});
            skLineSegment(sketch, "E1183", {"start": v(-28.18, 12.62) * mm, "end": v(-28.33, 12.64) * mm});
            skLineSegment(sketch, "E1184", {"start": v(-28.33, 12.64) * mm, "end": v(-28.48, 12.6) * mm});
            skLineSegment(sketch, "E1185", {"start": v(-28.48, 12.6) * mm, "end": v(-28.6, 12.52) * mm});
            skLineSegment(sketch, "E1186", {"start": v(-28.6, 12.52) * mm, "end": v(-28.68, 12.4) * mm});
            skLineSegment(sketch, "E1187", {"start": v(-28.68, 12.4) * mm, "end": v(-28.88, 11.96) * mm});
            skLineSegment(sketch, "E1188", {"start": v(-28.88, 11.96) * mm, "end": v(-29.06, 11.5) * mm});
            skLineSegment(sketch, "E1189", {"start": v(-29.06, 11.5) * mm, "end": v(-29.08, 11.38) * mm});
            skLineSegment(sketch, "E1190", {"start": v(-29.08, 11.38) * mm, "end": v(-29.05, 11.23) * mm});
            skLineSegment(sketch, "E1191", {"start": v(-29.05, 11.23) * mm, "end": v(-28.97, 11.1) * mm});
            skLineSegment(sketch, "E1192", {"start": v(-28.97, 11.1) * mm, "end": v(-28.85, 11) * mm});
            skLineSegment(sketch, "E1193", {"start": v(-28.85, 11) * mm, "end": v(-28.3, 10.77) * mm});
            skLineSegment(sketch, "E1194", {"start": v(-28.3, 10.77) * mm, "end": v(-28.18, 10.7) * mm});
            skLineSegment(sketch, "E1195", {"start": v(-28.18, 10.7) * mm, "end": v(-28.07, 10.63) * mm});
            skLineSegment(sketch, "E1196", {"start": v(-28.07, 10.63) * mm, "end": v(-27.98, 10.54) * mm});
            skLineSegment(sketch, "E1197", {"start": v(-27.98, 10.54) * mm, "end": v(-27.89, 10.45) * mm});
            skLineSegment(sketch, "E1198", {"start": v(-27.89, 10.45) * mm, "end": v(-27.8, 10.35) * mm});
            skLineSegment(sketch, "E1199", {"start": v(-27.8, 10.35) * mm, "end": v(-27.74, 10.24) * mm});
            skLineSegment(sketch, "E1200", {"start": v(-27.74, 10.24) * mm, "end": v(-27.67, 10.13) * mm});
            skLineSegment(sketch, "E1201", {"start": v(-27.67, 10.13) * mm, "end": v(-27.62, 10) * mm});
            skLineSegment(sketch, "E1202", {"start": v(-27.62, 10) * mm, "end": v(-27.58, 9.89) * mm});
            skLineSegment(sketch, "E1203", {"start": v(-27.58, 9.89) * mm, "end": v(-27.55, 9.76) * mm});
            skLineSegment(sketch, "E1204", {"start": v(-27.55, 9.76) * mm, "end": v(-27.53, 9.63) * mm});
            skLineSegment(sketch, "E1205", {"start": v(-27.53, 9.63) * mm, "end": v(-27.51, 9.5) * mm});
            skLineSegment(sketch, "E1206", {"start": v(-27.51, 9.5) * mm, "end": v(-27.51, 9.36) * mm});
            skLineSegment(sketch, "E1207", {"start": v(-27.51, 9.36) * mm, "end": v(-27.52, 9.23) * mm});
            skLineSegment(sketch, "E1208", {"start": v(-27.52, 9.23) * mm, "end": v(-27.55, 9.1) * mm});
            skLineSegment(sketch, "E1209", {"start": v(-27.55, 9.1) * mm, "end": v(-27.58, 8.96) * mm});
            skLineSegment(sketch, "E1210", {"start": v(-27.58, 8.96) * mm, "end": v(-27.63, 8.83) * mm});
            skLineSegment(sketch, "E1211", {"start": v(-27.63, 8.83) * mm, "end": v(-27.7, 8.71) * mm});
            skLineSegment(sketch, "E1212", {"start": v(-27.7, 8.71) * mm, "end": v(-27.76, 8.6) * mm});
            skLineSegment(sketch, "E1213", {"start": v(-27.76, 8.6) * mm, "end": v(-27.84, 8.49) * mm});
            skLineSegment(sketch, "E1214", {"start": v(-27.84, 8.49) * mm, "end": v(-27.93, 8.39) * mm});
            skLineSegment(sketch, "E1215", {"start": v(-27.93, 8.39) * mm, "end": v(-28.02, 8.3) * mm});
            skLineSegment(sketch, "E1216", {"start": v(-28.02, 8.3) * mm, "end": v(-28.12, 8.21) * mm});
            skLineSegment(sketch, "E1217", {"start": v(-28.12, 8.21) * mm, "end": v(-28.23, 8.14) * mm});
            skLineSegment(sketch, "E1218", {"start": v(-28.23, 8.14) * mm, "end": v(-28.34, 8.07) * mm});
            skLineSegment(sketch, "E1219", {"start": v(-28.34, 8.07) * mm, "end": v(-28.46, 8.02) * mm});
            skLineSegment(sketch, "E1220", {"start": v(-28.46, 8.02) * mm, "end": v(-28.58, 7.97) * mm});
            skLineSegment(sketch, "E1221", {"start": v(-28.58, 7.97) * mm, "end": v(-28.7, 7.94) * mm});
            skLineSegment(sketch, "E1222", {"start": v(-28.7, 7.94) * mm, "end": v(-28.83, 7.92) * mm});
            skLineSegment(sketch, "E1223", {"start": v(-28.83, 7.92) * mm, "end": v(-28.96, 7.9) * mm});
            skLineSegment(sketch, "E1224", {"start": v(-28.96, 7.9) * mm, "end": v(-29.09, 7.9) * mm});
            skLineSegment(sketch, "E1225", {"start": v(-29.09, 7.9) * mm, "end": v(-29.22, 7.91) * mm});
            skLineSegment(sketch, "E1226", {"start": v(-29.22, 7.91) * mm, "end": v(-29.8, 8.06) * mm});
            skLineSegment(sketch, "E1227", {"start": v(-29.8, 8.06) * mm, "end": v(-29.96, 8.05) * mm});
            skLineSegment(sketch, "E1228", {"start": v(-29.96, 8.05) * mm, "end": v(-30.1, 8) * mm});
            skLineSegment(sketch, "E1229", {"start": v(-30.1, 8) * mm, "end": v(-30.21, 7.89) * mm});
            skLineSegment(sketch, "E1230", {"start": v(-30.21, 7.89) * mm, "end": v(-30.27, 7.77) * mm});
            skLineSegment(sketch, "E1231", {"start": v(-30.27, 7.77) * mm, "end": v(-30.4, 7.3) * mm});
            skLineSegment(sketch, "E1232", {"start": v(-30.4, 7.3) * mm, "end": v(-30.5, 6.82) * mm});
            skLineSegment(sketch, "E1233", {"start": v(-30.5, 6.82) * mm, "end": v(-30.5, 6.69) * mm});
            skLineSegment(sketch, "E1234", {"start": v(-30.5, 6.69) * mm, "end": v(-30.45, 6.54) * mm});
            skLineSegment(sketch, "E1235", {"start": v(-30.45, 6.54) * mm, "end": v(-30.35, 6.43) * mm});
            skLineSegment(sketch, "E1236", {"start": v(-30.35, 6.43) * mm, "end": v(-30.22, 6.35) * mm});
            skLineSegment(sketch, "E1237", {"start": v(-30.22, 6.35) * mm, "end": v(-29.63, 6.21) * mm});
            skLineSegment(sketch, "E1238", {"start": v(-29.63, 6.21) * mm, "end": v(-29.5, 6.16) * mm});
            skLineSegment(sketch, "E1239", {"start": v(-29.5, 6.16) * mm, "end": v(-29.39, 6.1) * mm});
            skLineSegment(sketch, "E1240", {"start": v(-29.39, 6.1) * mm, "end": v(-29.28, 6.03) * mm});
            skLineSegment(sketch, "E1241", {"start": v(-29.28, 6.03) * mm, "end": v(-29.18, 5.96) * mm});
            skLineSegment(sketch, "E1242", {"start": v(-29.18, 5.96) * mm, "end": v(-29.08, 5.87) * mm});
            skLineSegment(sketch, "E1243", {"start": v(-29.08, 5.87) * mm, "end": v(-29, 5.77) * mm});
            skLineSegment(sketch, "E1244", {"start": v(-29, 5.77) * mm, "end": v(-28.92, 5.67) * mm});
            skLineSegment(sketch, "E1245", {"start": v(-28.92, 5.67) * mm, "end": v(-28.85, 5.56) * mm});
            skLineSegment(sketch, "E1246", {"start": v(-28.85, 5.56) * mm, "end": v(-28.79, 5.45) * mm});
            skLineSegment(sketch, "E1247", {"start": v(-28.79, 5.45) * mm, "end": v(-28.74, 5.33) * mm});
            skLineSegment(sketch, "E1248", {"start": v(-28.74, 5.33) * mm, "end": v(-28.7, 5.2) * mm});
            skLineSegment(sketch, "E1249", {"start": v(-28.7, 5.2) * mm, "end": v(-28.66, 5.08) * mm});
            skLineSegment(sketch, "E1250", {"start": v(-28.66, 5.08) * mm, "end": v(-28.64, 4.95) * mm});
            skLineSegment(sketch, "E1251", {"start": v(-28.64, 4.95) * mm, "end": v(-28.63, 4.81) * mm});
            skLineSegment(sketch, "E1252", {"start": v(-28.63, 4.81) * mm, "end": v(-28.63, 4.67) * mm});
            skLineSegment(sketch, "E1253", {"start": v(-28.63, 4.67) * mm, "end": v(-28.64, 4.54) * mm});
            skLineSegment(sketch, "E1254", {"start": v(-28.64, 4.54) * mm, "end": v(-28.67, 4.4) * mm});
            skLineSegment(sketch, "E1255", {"start": v(-28.67, 4.4) * mm, "end": v(-28.71, 4.27) * mm});
            skLineSegment(sketch, "E1256", {"start": v(-28.71, 4.27) * mm, "end": v(-28.77, 4.15) * mm});
            skLineSegment(sketch, "E1257", {"start": v(-28.77, 4.15) * mm, "end": v(-28.83, 4.03) * mm});
            skLineSegment(sketch, "E1258", {"start": v(-28.83, 4.03) * mm, "end": v(-28.9, 3.92) * mm});
            skLineSegment(sketch, "E1259", {"start": v(-28.9, 3.92) * mm, "end": v(-28.98, 3.81) * mm});
            skLineSegment(sketch, "E1260", {"start": v(-28.98, 3.81) * mm, "end": v(-29.06, 3.71) * mm});
            skLineSegment(sketch, "E1261", {"start": v(-29.06, 3.71) * mm, "end": v(-29.16, 3.62) * mm});
            skLineSegment(sketch, "E1262", {"start": v(-29.16, 3.62) * mm, "end": v(-29.26, 3.54) * mm});
            skLineSegment(sketch, "E1263", {"start": v(-29.26, 3.54) * mm, "end": v(-29.36, 3.47) * mm});
            skLineSegment(sketch, "E1264", {"start": v(-29.36, 3.47) * mm, "end": v(-29.47, 3.4) * mm});
            skLineSegment(sketch, "E1265", {"start": v(-29.47, 3.4) * mm, "end": v(-29.6, 3.35) * mm});
            skLineSegment(sketch, "E1266", {"start": v(-29.6, 3.35) * mm, "end": v(-29.71, 3.3) * mm});
            skLineSegment(sketch, "E1267", {"start": v(-29.71, 3.3) * mm, "end": v(-29.84, 3.28) * mm});
            skLineSegment(sketch, "E1268", {"start": v(-29.84, 3.28) * mm, "end": v(-29.97, 3.26) * mm});
            skLineSegment(sketch, "E1269", {"start": v(-29.97, 3.26) * mm, "end": v(-30.1, 3.25) * mm});
            skLineSegment(sketch, "E1270", {"start": v(-30.1, 3.25) * mm, "end": v(-30.7, 3.3) * mm});
            skLineSegment(sketch, "E1271", {"start": v(-30.7, 3.3) * mm, "end": v(-30.85, 3.27) * mm});
            skLineSegment(sketch, "E1272", {"start": v(-30.85, 3.27) * mm, "end": v(-30.98, 3.19) * mm});
            skLineSegment(sketch, "E1273", {"start": v(-30.98, 3.19) * mm, "end": v(-31.07, 3.07) * mm});
            skLineSegment(sketch, "E1274", {"start": v(-31.07, 3.07) * mm, "end": v(-31.12, 2.94) * mm});
            skLineSegment(sketch, "E1275", {"start": v(-31.12, 2.94) * mm, "end": v(-31.16, 2.45) * mm});
            skLineSegment(sketch, "E1276", {"start": v(-31.16, 2.45) * mm, "end": v(-31.2, 1.97) * mm});
            skLineSegment(sketch, "E1277", {"start": v(-31.2, 1.97) * mm, "end": v(-31.17, 1.83) * mm});
            skLineSegment(sketch, "E1278", {"start": v(-31.17, 1.83) * mm, "end": v(-31.1, 1.7) * mm});
            skLineSegment(sketch, "E1279", {"start": v(-31.1, 1.7) * mm, "end": v(-30.98, 1.6) * mm});
            skLineSegment(sketch, "E1280", {"start": v(-30.98, 1.6) * mm, "end": v(-30.84, 1.54) * mm});
            skLineSegment(sketch, "E1281", {"start": v(-30.84, 1.54) * mm, "end": v(-30.24, 1.5) * mm});
            skLineSegment(sketch, "E1282", {"start": v(-30.24, 1.5) * mm, "end": v(-30.1, 1.47) * mm});
            skLineSegment(sketch, "E1283", {"start": v(-30.1, 1.47) * mm, "end": v(-29.98, 1.43) * mm});
            skLineSegment(sketch, "E1284", {"start": v(-29.98, 1.43) * mm, "end": v(-29.86, 1.38) * mm});
            skLineSegment(sketch, "E1285", {"start": v(-29.86, 1.38) * mm, "end": v(-29.75, 1.32) * mm});
            skLineSegment(sketch, "E1286", {"start": v(-29.75, 1.32) * mm, "end": v(-29.64, 1.25) * mm});
            skLineSegment(sketch, "E1287", {"start": v(-29.64, 1.25) * mm, "end": v(-29.54, 1.17) * mm});
            skLineSegment(sketch, "E1288", {"start": v(-29.54, 1.17) * mm, "end": v(-29.45, 1.08) * mm});
            skLineSegment(sketch, "E1289", {"start": v(-29.45, 1.08) * mm, "end": v(-29.36, 0.98) * mm});
            skLineSegment(sketch, "E1290", {"start": v(-29.36, 0.98) * mm, "end": v(-29.29, 0.88) * mm});
            skLineSegment(sketch, "E1291", {"start": v(-29.29, 0.88) * mm, "end": v(-29.22, 0.77) * mm});
            skLineSegment(sketch, "E1292", {"start": v(-29.22, 0.77) * mm, "end": v(-29.15, 0.65) * mm});
            skLineSegment(sketch, "E1293", {"start": v(-29.15, 0.65) * mm, "end": v(-29.1, 0.53) * mm});
            skLineSegment(sketch, "E1294", {"start": v(-29.1, 0.53) * mm, "end": v(-29.06, 0.4) * mm});
            skLineSegment(sketch, "E1295", {"start": v(-29.06, 0.4) * mm, "end": v(-29.03, 0.27) * mm});
            skLineSegment(sketch, "E1296", {"start": v(-29.03, 0.27) * mm, "end": v(-29, 0.14) * mm});
            skLineSegment(sketch, "E1297", {"start": v(-29, 0.14) * mm, "end": v(-29, 0) * mm});
            skLineSegment(sketch, "E1298", {"start": v(-29, 0) * mm, "end": v(-29, -0.14) * mm});
            skLineSegment(sketch, "E1299", {"start": v(-29, -0.14) * mm, "end": v(-29.03, -0.27) * mm});
            skLineSegment(sketch, "E1300", {"start": v(-29.03, -0.27) * mm, "end": v(-29.06, -0.4) * mm});
            skLineSegment(sketch, "E1301", {"start": v(-29.06, -0.4) * mm, "end": v(-29.1, -0.53) * mm});
            skLineSegment(sketch, "E1302", {"start": v(-29.1, -0.53) * mm, "end": v(-29.15, -0.65) * mm});
            skLineSegment(sketch, "E1303", {"start": v(-29.15, -0.65) * mm, "end": v(-29.22, -0.77) * mm});
            skLineSegment(sketch, "E1304", {"start": v(-29.22, -0.77) * mm, "end": v(-29.28, -0.88) * mm});
            skLineSegment(sketch, "E1305", {"start": v(-29.28, -0.88) * mm, "end": v(-29.36, -0.98) * mm});
            skLineSegment(sketch, "E1306", {"start": v(-29.36, -0.98) * mm, "end": v(-29.45, -1.08) * mm});
            skLineSegment(sketch, "E1307", {"start": v(-29.45, -1.08) * mm, "end": v(-29.54, -1.17) * mm});
            skLineSegment(sketch, "E1308", {"start": v(-29.54, -1.17) * mm, "end": v(-29.64, -1.25) * mm});
            skLineSegment(sketch, "E1309", {"start": v(-29.64, -1.25) * mm, "end": v(-29.75, -1.32) * mm});
            skLineSegment(sketch, "E1310", {"start": v(-29.75, -1.32) * mm, "end": v(-29.86, -1.38) * mm});
            skLineSegment(sketch, "E1311", {"start": v(-29.86, -1.38) * mm, "end": v(-29.98, -1.43) * mm});
            skLineSegment(sketch, "E1312", {"start": v(-29.98, -1.43) * mm, "end": v(-30.1, -1.47) * mm});
            skLineSegment(sketch, "E1313", {"start": v(-30.1, -1.47) * mm, "end": v(-30.24, -1.5) * mm});
            skLineSegment(sketch, "E1314", {"start": v(-30.24, -1.5) * mm, "end": v(-30.84, -1.54) * mm});
            skLineSegment(sketch, "E1315", {"start": v(-30.84, -1.54) * mm, "end": v(-30.98, -1.6) * mm});
            skLineSegment(sketch, "E1316", {"start": v(-30.98, -1.6) * mm, "end": v(-31.1, -1.7) * mm});
            skLineSegment(sketch, "E1317", {"start": v(-31.1, -1.7) * mm, "end": v(-31.17, -1.83) * mm});
            skLineSegment(sketch, "E1318", {"start": v(-31.17, -1.83) * mm, "end": v(-31.2, -1.97) * mm});
            skLineSegment(sketch, "E1319", {"start": v(-31.2, -1.97) * mm, "end": v(-31.16, -2.45) * mm});
            skLineSegment(sketch, "E1320", {"start": v(-31.16, -2.45) * mm, "end": v(-31.12, -2.94) * mm});
            skLineSegment(sketch, "E1321", {"start": v(-31.12, -2.94) * mm, "end": v(-31.07, -3.07) * mm});
            skLineSegment(sketch, "E1322", {"start": v(-31.07, -3.07) * mm, "end": v(-30.98, -3.19) * mm});
            skLineSegment(sketch, "E1323", {"start": v(-30.98, -3.19) * mm, "end": v(-30.85, -3.27) * mm});
            skLineSegment(sketch, "E1324", {"start": v(-30.85, -3.27) * mm, "end": v(-30.7, -3.3) * mm});
            skLineSegment(sketch, "E1325", {"start": v(-30.7, -3.3) * mm, "end": v(-30.1, -3.25) * mm});
            skLineSegment(sketch, "E1326", {"start": v(-30.1, -3.25) * mm, "end": v(-29.97, -3.26) * mm});
            skLineSegment(sketch, "E1327", {"start": v(-29.97, -3.26) * mm, "end": v(-29.84, -3.28) * mm});
            skLineSegment(sketch, "E1328", {"start": v(-29.84, -3.28) * mm, "end": v(-29.71, -3.3) * mm});
            skLineSegment(sketch, "E1329", {"start": v(-29.71, -3.3) * mm, "end": v(-29.6, -3.35) * mm});
            skLineSegment(sketch, "E1330", {"start": v(-29.6, -3.35) * mm, "end": v(-29.47, -3.4) * mm});
            skLineSegment(sketch, "E1331", {"start": v(-29.47, -3.4) * mm, "end": v(-29.36, -3.47) * mm});
            skLineSegment(sketch, "E1332", {"start": v(-29.36, -3.47) * mm, "end": v(-29.26, -3.54) * mm});
            skLineSegment(sketch, "E1333", {"start": v(-29.26, -3.54) * mm, "end": v(-29.16, -3.62) * mm});
            skLineSegment(sketch, "E1334", {"start": v(-29.16, -3.62) * mm, "end": v(-29.06, -3.71) * mm});
            skLineSegment(sketch, "E1335", {"start": v(-29.06, -3.71) * mm, "end": v(-28.98, -3.81) * mm});
            skLineSegment(sketch, "E1336", {"start": v(-28.98, -3.81) * mm, "end": v(-28.9, -3.92) * mm});
            skLineSegment(sketch, "E1337", {"start": v(-28.9, -3.92) * mm, "end": v(-28.83, -4.03) * mm});
            skLineSegment(sketch, "E1338", {"start": v(-28.83, -4.03) * mm, "end": v(-28.77, -4.15) * mm});
            skLineSegment(sketch, "E1339", {"start": v(-28.77, -4.15) * mm, "end": v(-28.71, -4.27) * mm});
            skLineSegment(sketch, "E1340", {"start": v(-28.71, -4.27) * mm, "end": v(-28.67, -4.4) * mm});
            skLineSegment(sketch, "E1341", {"start": v(-28.67, -4.4) * mm, "end": v(-28.64, -4.54) * mm});
            skLineSegment(sketch, "E1342", {"start": v(-28.64, -4.54) * mm, "end": v(-28.63, -4.67) * mm});
            skLineSegment(sketch, "E1343", {"start": v(-28.63, -4.67) * mm, "end": v(-28.63, -4.81) * mm});
            skLineSegment(sketch, "E1344", {"start": v(-28.63, -4.81) * mm, "end": v(-28.64, -4.95) * mm});
            skLineSegment(sketch, "E1345", {"start": v(-28.64, -4.95) * mm, "end": v(-28.66, -5.08) * mm});
            skLineSegment(sketch, "E1346", {"start": v(-28.66, -5.08) * mm, "end": v(-28.7, -5.2) * mm});
            skLineSegment(sketch, "E1347", {"start": v(-28.7, -5.2) * mm, "end": v(-28.74, -5.33) * mm});
            skLineSegment(sketch, "E1348", {"start": v(-28.74, -5.33) * mm, "end": v(-28.79, -5.45) * mm});
            skLineSegment(sketch, "E1349", {"start": v(-28.79, -5.45) * mm, "end": v(-28.85, -5.56) * mm});
            skLineSegment(sketch, "E1350", {"start": v(-28.85, -5.56) * mm, "end": v(-28.92, -5.67) * mm});
            skLineSegment(sketch, "E1351", {"start": v(-28.92, -5.67) * mm, "end": v(-29, -5.77) * mm});
            skLineSegment(sketch, "E1352", {"start": v(-29, -5.77) * mm, "end": v(-29.08, -5.87) * mm});
            skLineSegment(sketch, "E1353", {"start": v(-29.08, -5.87) * mm, "end": v(-29.18, -5.96) * mm});
            skLineSegment(sketch, "E1354", {"start": v(-29.18, -5.96) * mm, "end": v(-29.28, -6.03) * mm});
            skLineSegment(sketch, "E1355", {"start": v(-29.28, -6.03) * mm, "end": v(-29.39, -6.1) * mm});
            skLineSegment(sketch, "E1356", {"start": v(-29.39, -6.1) * mm, "end": v(-29.5, -6.16) * mm});
            skLineSegment(sketch, "E1357", {"start": v(-29.5, -6.16) * mm, "end": v(-29.63, -6.21) * mm});
            skLineSegment(sketch, "E1358", {"start": v(-29.63, -6.21) * mm, "end": v(-30.22, -6.35) * mm});
            skLineSegment(sketch, "E1359", {"start": v(-30.22, -6.35) * mm, "end": v(-30.35, -6.43) * mm});
            skLineSegment(sketch, "E1360", {"start": v(-30.35, -6.43) * mm, "end": v(-30.45, -6.54) * mm});
            skLineSegment(sketch, "E1361", {"start": v(-30.45, -6.54) * mm, "end": v(-30.5, -6.69) * mm});
            skLineSegment(sketch, "E1362", {"start": v(-30.5, -6.69) * mm, "end": v(-30.5, -6.82) * mm});
            skLineSegment(sketch, "E1363", {"start": v(-30.5, -6.82) * mm, "end": v(-30.4, -7.3) * mm});
            skLineSegment(sketch, "E1364", {"start": v(-30.4, -7.3) * mm, "end": v(-30.27, -7.77) * mm});
            skLineSegment(sketch, "E1365", {"start": v(-30.27, -7.77) * mm, "end": v(-30.21, -7.89) * mm});
            skLineSegment(sketch, "E1366", {"start": v(-30.21, -7.89) * mm, "end": v(-30.1, -8) * mm});
            skLineSegment(sketch, "E1367", {"start": v(-30.1, -8) * mm, "end": v(-29.96, -8.05) * mm});
            skLineSegment(sketch, "E1368", {"start": v(-29.96, -8.05) * mm, "end": v(-29.8, -8.06) * mm});
            skLineSegment(sketch, "E1369", {"start": v(-29.8, -8.06) * mm, "end": v(-29.22, -7.91) * mm});
            skLineSegment(sketch, "E1370", {"start": v(-29.22, -7.91) * mm, "end": v(-29.09, -7.9) * mm});
            skLineSegment(sketch, "E1371", {"start": v(-29.09, -7.9) * mm, "end": v(-28.96, -7.9) * mm});
            skLineSegment(sketch, "E1372", {"start": v(-28.96, -7.9) * mm, "end": v(-28.83, -7.92) * mm});
            skLineSegment(sketch, "E1373", {"start": v(-28.83, -7.92) * mm, "end": v(-28.7, -7.94) * mm});
            skLineSegment(sketch, "E1374", {"start": v(-28.7, -7.94) * mm, "end": v(-28.58, -7.97) * mm});
            skLineSegment(sketch, "E1375", {"start": v(-28.58, -7.97) * mm, "end": v(-28.46, -8.02) * mm});
            skLineSegment(sketch, "E1376", {"start": v(-28.46, -8.02) * mm, "end": v(-28.34, -8.07) * mm});
            skLineSegment(sketch, "E1377", {"start": v(-28.34, -8.07) * mm, "end": v(-28.23, -8.14) * mm});
            skLineSegment(sketch, "E1378", {"start": v(-28.23, -8.14) * mm, "end": v(-28.12, -8.21) * mm});
            skLineSegment(sketch, "E1379", {"start": v(-28.12, -8.21) * mm, "end": v(-28.02, -8.3) * mm});
            skLineSegment(sketch, "E1380", {"start": v(-28.02, -8.3) * mm, "end": v(-27.93, -8.39) * mm});
            skLineSegment(sketch, "E1381", {"start": v(-27.93, -8.39) * mm, "end": v(-27.84, -8.49) * mm});
            skLineSegment(sketch, "E1382", {"start": v(-27.84, -8.49) * mm, "end": v(-27.76, -8.6) * mm});
            skLineSegment(sketch, "E1383", {"start": v(-27.76, -8.6) * mm, "end": v(-27.7, -8.71) * mm});
            skLineSegment(sketch, "E1384", {"start": v(-27.7, -8.71) * mm, "end": v(-27.63, -8.83) * mm});
            skLineSegment(sketch, "E1385", {"start": v(-27.63, -8.83) * mm, "end": v(-27.58, -8.96) * mm});
            skLineSegment(sketch, "E1386", {"start": v(-27.58, -8.96) * mm, "end": v(-27.55, -9.1) * mm});
            skLineSegment(sketch, "E1387", {"start": v(-27.55, -9.1) * mm, "end": v(-27.52, -9.23) * mm});
            skLineSegment(sketch, "E1388", {"start": v(-27.52, -9.23) * mm, "end": v(-27.51, -9.36) * mm});
            skLineSegment(sketch, "E1389", {"start": v(-27.51, -9.36) * mm, "end": v(-27.51, -9.5) * mm});
            skLineSegment(sketch, "E1390", {"start": v(-27.51, -9.5) * mm, "end": v(-27.53, -9.63) * mm});
            skLineSegment(sketch, "E1391", {"start": v(-27.53, -9.63) * mm, "end": v(-27.55, -9.76) * mm});
            skLineSegment(sketch, "E1392", {"start": v(-27.55, -9.76) * mm, "end": v(-27.58, -9.89) * mm});
            skLineSegment(sketch, "E1393", {"start": v(-27.58, -9.89) * mm, "end": v(-27.62, -10) * mm});
            skLineSegment(sketch, "E1394", {"start": v(-27.62, -10) * mm, "end": v(-27.67, -10.13) * mm});
            skLineSegment(sketch, "E1395", {"start": v(-27.67, -10.13) * mm, "end": v(-27.74, -10.24) * mm});
            skLineSegment(sketch, "E1396", {"start": v(-27.74, -10.24) * mm, "end": v(-27.8, -10.35) * mm});
            skLineSegment(sketch, "E1397", {"start": v(-27.8, -10.35) * mm, "end": v(-27.89, -10.45) * mm});
            skLineSegment(sketch, "E1398", {"start": v(-27.89, -10.45) * mm, "end": v(-27.98, -10.54) * mm});
            skLineSegment(sketch, "E1399", {"start": v(-27.98, -10.54) * mm, "end": v(-28.07, -10.63) * mm});
            skLineSegment(sketch, "E1400", {"start": v(-28.07, -10.63) * mm, "end": v(-28.18, -10.7) * mm});
            skLineSegment(sketch, "E1401", {"start": v(-28.18, -10.7) * mm, "end": v(-28.3, -10.77) * mm});
            skLineSegment(sketch, "E1402", {"start": v(-28.3, -10.77) * mm, "end": v(-28.85, -11) * mm});
            skLineSegment(sketch, "E1403", {"start": v(-28.85, -11) * mm, "end": v(-28.97, -11.1) * mm});
            skLineSegment(sketch, "E1404", {"start": v(-28.97, -11.1) * mm, "end": v(-29.05, -11.23) * mm});
            skLineSegment(sketch, "E1405", {"start": v(-29.05, -11.23) * mm, "end": v(-29.08, -11.38) * mm});
            skLineSegment(sketch, "E1406", {"start": v(-29.08, -11.38) * mm, "end": v(-29.06, -11.5) * mm});
            skLineSegment(sketch, "E1407", {"start": v(-29.06, -11.5) * mm, "end": v(-28.88, -11.96) * mm});
            skLineSegment(sketch, "E1408", {"start": v(-28.88, -11.96) * mm, "end": v(-28.68, -12.4) * mm});
            skLineSegment(sketch, "E1409", {"start": v(-28.68, -12.4) * mm, "end": v(-28.6, -12.52) * mm});
            skLineSegment(sketch, "E1410", {"start": v(-28.6, -12.52) * mm, "end": v(-28.48, -12.6) * mm});
            skLineSegment(sketch, "E1411", {"start": v(-28.48, -12.6) * mm, "end": v(-28.33, -12.64) * mm});
            skLineSegment(sketch, "E1412", {"start": v(-28.33, -12.64) * mm, "end": v(-28.18, -12.62) * mm});
            skLineSegment(sketch, "E1413", {"start": v(-28.18, -12.62) * mm, "end": v(-27.62, -12.39) * mm});
            skLineSegment(sketch, "E1414", {"start": v(-27.62, -12.39) * mm, "end": v(-27.5, -12.36) * mm});
            skLineSegment(sketch, "E1415", {"start": v(-27.5, -12.36) * mm, "end": v(-27.36, -12.34) * mm});
            skLineSegment(sketch, "E1416", {"start": v(-27.36, -12.34) * mm, "end": v(-27.24, -12.33) * mm});
            skLineSegment(sketch, "E1417", {"start": v(-27.24, -12.33) * mm, "end": v(-27.1, -12.33) * mm});
            skLineSegment(sketch, "E1418", {"start": v(-27.1, -12.33) * mm, "end": v(-26.98, -12.35) * mm});
            skLineSegment(sketch, "E1419", {"start": v(-26.98, -12.35) * mm, "end": v(-26.85, -12.37) * mm});
            skLineSegment(sketch, "E1420", {"start": v(-26.85, -12.37) * mm, "end": v(-26.73, -12.4) * mm});
            skLineSegment(sketch, "E1421", {"start": v(-26.73, -12.4) * mm, "end": v(-26.6, -12.46) * mm});
            skLineSegment(sketch, "E1422", {"start": v(-26.6, -12.46) * mm, "end": v(-26.5, -12.51) * mm});
            skLineSegment(sketch, "E1423", {"start": v(-26.5, -12.51) * mm, "end": v(-26.38, -12.58) * mm});
            skLineSegment(sketch, "E1424", {"start": v(-26.38, -12.58) * mm, "end": v(-26.27, -12.65) * mm});
            skLineSegment(sketch, "E1425", {"start": v(-26.27, -12.65) * mm, "end": v(-26.17, -12.74) * mm});
            skLineSegment(sketch, "E1426", {"start": v(-26.17, -12.74) * mm, "end": v(-26.08, -12.83) * mm});
            skLineSegment(sketch, "E1427", {"start": v(-26.08, -12.83) * mm, "end": v(-25.99, -12.94) * mm});
            skLineSegment(sketch, "E1428", {"start": v(-25.99, -12.94) * mm, "end": v(-25.9, -13.05) * mm});
            skLineSegment(sketch, "E1429", {"start": v(-25.9, -13.05) * mm, "end": v(-25.84, -13.16) * mm});
            skLineSegment(sketch, "E1430", {"start": v(-25.84, -13.16) * mm, "end": v(-25.78, -13.3) * mm});
            skLineSegment(sketch, "E1431", {"start": v(-25.78, -13.3) * mm, "end": v(-25.74, -13.42) * mm});
            skLineSegment(sketch, "E1432", {"start": v(-25.74, -13.42) * mm, "end": v(-25.7, -13.55) * mm});
            skLineSegment(sketch, "E1433", {"start": v(-25.7, -13.55) * mm, "end": v(-25.69, -13.69) * mm});
            skLineSegment(sketch, "E1434", {"start": v(-25.69, -13.69) * mm, "end": v(-25.68, -13.82) * mm});
            skLineSegment(sketch, "E1435", {"start": v(-25.68, -13.82) * mm, "end": v(-25.68, -13.95) * mm});
            skLineSegment(sketch, "E1436", {"start": v(-25.68, -13.95) * mm, "end": v(-25.7, -14.08) * mm});
            skLineSegment(sketch, "E1437", {"start": v(-25.7, -14.08) * mm, "end": v(-25.72, -14.2) * mm});
            skLineSegment(sketch, "E1438", {"start": v(-25.72, -14.2) * mm, "end": v(-25.75, -14.33) * mm});
            skLineSegment(sketch, "E1439", {"start": v(-25.75, -14.33) * mm, "end": v(-25.8, -14.45) * mm});
            skLineSegment(sketch, "E1440", {"start": v(-25.8, -14.45) * mm, "end": v(-25.85, -14.57) * mm});
            skLineSegment(sketch, "E1441", {"start": v(-25.85, -14.57) * mm, "end": v(-25.9, -14.68) * mm});
            skLineSegment(sketch, "E1442", {"start": v(-25.9, -14.68) * mm, "end": v(-25.98, -14.79) * mm});
            skLineSegment(sketch, "E1443", {"start": v(-25.98, -14.79) * mm, "end": v(-26.06, -14.89) * mm});
            skLineSegment(sketch, "E1444", {"start": v(-26.06, -14.89) * mm, "end": v(-26.16, -14.98) * mm});
            skLineSegment(sketch, "E1445", {"start": v(-26.16, -14.98) * mm, "end": v(-26.26, -15.07) * mm});
            skLineSegment(sketch, "E1446", {"start": v(-26.26, -15.07) * mm, "end": v(-26.78, -15.38) * mm});
            skLineSegment(sketch, "E1447", {"start": v(-26.78, -15.38) * mm, "end": v(-26.88, -15.5) * mm});
            skLineSegment(sketch, "E1448", {"start": v(-26.88, -15.5) * mm, "end": v(-26.93, -15.63) * mm});
            skLineSegment(sketch, "E1449", {"start": v(-26.93, -15.63) * mm, "end": v(-26.94, -15.78) * mm});
            skLineSegment(sketch, "E1450", {"start": v(-26.94, -15.78) * mm, "end": v(-26.9, -15.91) * mm});
            skLineSegment(sketch, "E1451", {"start": v(-26.9, -15.91) * mm, "end": v(-26.65, -16.33) * mm});
            skLineSegment(sketch, "E1452", {"start": v(-26.65, -16.33) * mm, "end": v(-26.4, -16.74) * mm});
            skLineSegment(sketch, "E1453", {"start": v(-26.4, -16.74) * mm, "end": v(-26.3, -16.84) * mm});
            skLineSegment(sketch, "E1454", {"start": v(-26.3, -16.84) * mm, "end": v(-26.16, -16.9) * mm});
            skLineSegment(sketch, "E1455", {"start": v(-26.16, -16.9) * mm, "end": v(-26, -16.92) * mm});
            skLineSegment(sketch, "E1456", {"start": v(-26, -16.92) * mm, "end": v(-25.86, -16.88) * mm});
            skLineSegment(sketch, "E1457", {"start": v(-25.86, -16.88) * mm, "end": v(-25.34, -16.56) * mm});
            skLineSegment(sketch, "E1458", {"start": v(-25.34, -16.56) * mm, "end": v(-25.22, -16.5) * mm});
            skLineSegment(sketch, "E1459", {"start": v(-25.22, -16.5) * mm, "end": v(-25.1, -16.47) * mm});
            skLineSegment(sketch, "E1460", {"start": v(-25.1, -16.47) * mm, "end": v(-24.97, -16.44) * mm});
            skLineSegment(sketch, "E1461", {"start": v(-24.97, -16.44) * mm, "end": v(-24.84, -16.42) * mm});
            skLineSegment(sketch, "E1462", {"start": v(-24.84, -16.42) * mm, "end": v(-24.71, -16.42) * mm});
            skLineSegment(sketch, "E1463", {"start": v(-24.71, -16.42) * mm, "end": v(-24.59, -16.42) * mm});
            skLineSegment(sketch, "E1464", {"start": v(-24.59, -16.42) * mm, "end": v(-24.46, -16.44) * mm});
            skLineSegment(sketch, "E1465", {"start": v(-24.46, -16.44) * mm, "end": v(-24.33, -16.46) * mm});
            skLineSegment(sketch, "E1466", {"start": v(-24.33, -16.46) * mm, "end": v(-24.2, -16.5) * mm});
            skLineSegment(sketch, "E1467", {"start": v(-24.2, -16.5) * mm, "end": v(-24.09, -16.55) * mm});
            skLineSegment(sketch, "E1468", {"start": v(-24.09, -16.55) * mm, "end": v(-23.97, -16.6) * mm});
            skLineSegment(sketch, "E1469", {"start": v(-23.97, -16.6) * mm, "end": v(-23.86, -16.68) * mm});
            skLineSegment(sketch, "E1470", {"start": v(-23.86, -16.68) * mm, "end": v(-23.75, -16.75) * mm});
            skLineSegment(sketch, "E1471", {"start": v(-23.75, -16.75) * mm, "end": v(-23.65, -16.84) * mm});
            skLineSegment(sketch, "E1472", {"start": v(-23.65, -16.84) * mm, "end": v(-23.55, -16.94) * mm});
            skLineSegment(sketch, "E1473", {"start": v(-23.55, -16.94) * mm, "end": v(-23.46, -17.04) * mm});
            skLineSegment(sketch, "E1474", {"start": v(-23.46, -17.04) * mm, "end": v(-23.39, -17.16) * mm});
            skLineSegment(sketch, "E1475", {"start": v(-23.39, -17.16) * mm, "end": v(-23.32, -17.28) * mm});
            skLineSegment(sketch, "E1476", {"start": v(-23.32, -17.28) * mm, "end": v(-23.27, -17.4) * mm});
            skLineSegment(sketch, "E1477", {"start": v(-23.27, -17.4) * mm, "end": v(-23.23, -17.54) * mm});
            skLineSegment(sketch, "E1478", {"start": v(-23.23, -17.54) * mm, "end": v(-23.2, -17.66) * mm});
            skLineSegment(sketch, "E1479", {"start": v(-23.2, -17.66) * mm, "end": v(-23.18, -17.8) * mm});
            skLineSegment(sketch, "E1480", {"start": v(-23.18, -17.8) * mm, "end": v(-23.18, -17.92) * mm});
            skLineSegment(sketch, "E1481", {"start": v(-23.18, -17.92) * mm, "end": v(-23.18, -18.05) * mm});
            skLineSegment(sketch, "E1482", {"start": v(-23.18, -18.05) * mm, "end": v(-23.2, -18.18) * mm});
            skLineSegment(sketch, "E1483", {"start": v(-23.2, -18.18) * mm, "end": v(-23.21, -18.3) * mm});
            skLineSegment(sketch, "E1484", {"start": v(-23.21, -18.3) * mm, "end": v(-23.25, -18.43) * mm});
            skLineSegment(sketch, "E1485", {"start": v(-23.25, -18.43) * mm, "end": v(-23.3, -18.55) * mm});
            skLineSegment(sketch, "E1486", {"start": v(-23.3, -18.55) * mm, "end": v(-23.35, -18.67) * mm});
            skLineSegment(sketch, "E1487", {"start": v(-23.35, -18.67) * mm, "end": v(-23.41, -18.78) * mm});
            skLineSegment(sketch, "E1488", {"start": v(-23.41, -18.78) * mm, "end": v(-23.5, -18.89) * mm});
            skLineSegment(sketch, "E1489", {"start": v(-23.5, -18.89) * mm, "end": v(-23.58, -18.99) * mm});
            skLineSegment(sketch, "E1490", {"start": v(-23.58, -18.99) * mm, "end": v(-24.04, -19.38) * mm});
            skLineSegment(sketch, "E1491", {"start": v(-24.04, -19.38) * mm, "end": v(-24.13, -19.5) * mm});
            skLineSegment(sketch, "E1492", {"start": v(-24.13, -19.5) * mm, "end": v(-24.16, -19.65) * mm});
            skLineSegment(sketch, "E1493", {"start": v(-24.16, -19.65) * mm, "end": v(-24.14, -19.8) * mm});
            skLineSegment(sketch, "E1494", {"start": v(-24.14, -19.8) * mm, "end": v(-24.08, -19.92) * mm});
            skLineSegment(sketch, "E1495", {"start": v(-24.08, -19.92) * mm, "end": v(-23.77, -20.3) * mm});
            skLineSegment(sketch, "E1496", {"start": v(-23.77, -20.3) * mm, "end": v(-23.45, -20.67) * mm});
            skLineSegment(sketch, "E1497", {"start": v(-23.45, -20.67) * mm, "end": v(-23.34, -20.74) * mm});
            skLineSegment(sketch, "E1498", {"start": v(-23.34, -20.74) * mm, "end": v(-23.19, -20.79) * mm});
            skLineSegment(sketch, "E1499", {"start": v(-23.19, -20.79) * mm, "end": v(-23.04, -20.78) * mm});
            skLineSegment(sketch, "E1500", {"start": v(-23.04, -20.78) * mm, "end": v(-22.9, -20.72) * mm});
            skLineSegment(sketch, "E1501", {"start": v(-22.9, -20.72) * mm, "end": v(-22.44, -20.32) * mm});
            skLineSegment(sketch, "E1502", {"start": v(-22.44, -20.32) * mm, "end": v(-22.33, -20.25) * mm});
            skLineSegment(sketch, "E1503", {"start": v(-22.33, -20.25) * mm, "end": v(-22.21, -20.19) * mm});
            skLineSegment(sketch, "E1504", {"start": v(-22.21, -20.19) * mm, "end": v(-22.1, -20.14) * mm});
            skLineSegment(sketch, "E1505", {"start": v(-22.1, -20.14) * mm, "end": v(-21.97, -20.1) * mm});
            skLineSegment(sketch, "E1506", {"start": v(-21.97, -20.1) * mm, "end": v(-21.84, -20.08) * mm});
            skLineSegment(sketch, "E1507", {"start": v(-21.84, -20.08) * mm, "end": v(-21.72, -20.07) * mm});
            skLineSegment(sketch, "E1508", {"start": v(-21.72, -20.07) * mm, "end": v(-21.59, -20.06) * mm});
            skLineSegment(sketch, "E1509", {"start": v(-21.59, -20.06) * mm, "end": v(-21.46, -20.07) * mm});
            skLineSegment(sketch, "E1510", {"start": v(-21.46, -20.07) * mm, "end": v(-21.33, -20.09) * mm});
            skLineSegment(sketch, "E1511", {"start": v(-21.33, -20.09) * mm, "end": v(-21.2, -20.11) * mm});
            skLineSegment(sketch, "E1512", {"start": v(-21.2, -20.11) * mm, "end": v(-21.08, -20.15) * mm});
            skLineSegment(sketch, "E1513", {"start": v(-21.08, -20.15) * mm, "end": v(-20.95, -20.2) * mm});
            skLineSegment(sketch, "E1514", {"start": v(-20.95, -20.2) * mm, "end": v(-20.84, -20.26) * mm});
            skLineSegment(sketch, "E1515", {"start": v(-20.84, -20.26) * mm, "end": v(-20.72, -20.33) * mm});
            skLineSegment(sketch, "E1516", {"start": v(-20.72, -20.33) * mm, "end": v(-20.6, -20.41) * mm});
            skLineSegment(sketch, "E1517", {"start": v(-20.6, -20.41) * mm, "end": v(-20.5, -20.5) * mm});
            skLineSegment(sketch, "E1518", {"start": v(-20.5, -20.5) * mm, "end": v(-20.41, -20.6) * mm});
            skLineSegment(sketch, "E1519", {"start": v(-20.41, -20.6) * mm, "end": v(-20.33, -20.72) * mm});
            skLineSegment(sketch, "E1520", {"start": v(-20.33, -20.72) * mm, "end": v(-20.26, -20.83) * mm});
            skLineSegment(sketch, "E1521", {"start": v(-20.26, -20.83) * mm, "end": v(-20.2, -20.95) * mm});
            skLineSegment(sketch, "E1522", {"start": v(-20.2, -20.95) * mm, "end": v(-20.15, -21.08) * mm});
            skLineSegment(sketch, "E1523", {"start": v(-20.15, -21.08) * mm, "end": v(-20.11, -21.2) * mm});
            skLineSegment(sketch, "E1524", {"start": v(-20.11, -21.2) * mm, "end": v(-20.09, -21.33) * mm});
            skLineSegment(sketch, "E1525", {"start": v(-20.09, -21.33) * mm, "end": v(-20.07, -21.46) * mm});
            skLineSegment(sketch, "E1526", {"start": v(-20.07, -21.46) * mm, "end": v(-20.06, -21.59) * mm});
            skLineSegment(sketch, "E1527", {"start": v(-20.06, -21.59) * mm, "end": v(-20.06, -21.72) * mm});
            skLineSegment(sketch, "E1528", {"start": v(-20.06, -21.72) * mm, "end": v(-20.08, -21.84) * mm});
            skLineSegment(sketch, "E1529", {"start": v(-20.08, -21.84) * mm, "end": v(-20.1, -21.97) * mm});
            skLineSegment(sketch, "E1530", {"start": v(-20.1, -21.97) * mm, "end": v(-20.14, -22.1) * mm});
            skLineSegment(sketch, "E1531", {"start": v(-20.14, -22.1) * mm, "end": v(-20.19, -22.21) * mm});
            skLineSegment(sketch, "E1532", {"start": v(-20.19, -22.21) * mm, "end": v(-20.25, -22.33) * mm});
            skLineSegment(sketch, "E1533", {"start": v(-20.25, -22.33) * mm, "end": v(-20.32, -22.44) * mm});
            skLineSegment(sketch, "E1534", {"start": v(-20.32, -22.44) * mm, "end": v(-20.72, -22.9) * mm});
            skLineSegment(sketch, "E1535", {"start": v(-20.72, -22.9) * mm, "end": v(-20.78, -23.04) * mm});
            skLineSegment(sketch, "E1536", {"start": v(-20.78, -23.04) * mm, "end": v(-20.79, -23.19) * mm});
            skLineSegment(sketch, "E1537", {"start": v(-20.79, -23.19) * mm, "end": v(-20.74, -23.34) * mm});
            skLineSegment(sketch, "E1538", {"start": v(-20.74, -23.34) * mm, "end": v(-20.67, -23.45) * mm});
            skLineSegment(sketch, "E1539", {"start": v(-20.67, -23.45) * mm, "end": v(-20.3, -23.77) * mm});
            skLineSegment(sketch, "E1540", {"start": v(-20.3, -23.77) * mm, "end": v(-19.92, -24.08) * mm});
            skLineSegment(sketch, "E1541", {"start": v(-19.92, -24.08) * mm, "end": v(-19.8, -24.14) * mm});
            skLineSegment(sketch, "E1542", {"start": v(-19.8, -24.14) * mm, "end": v(-19.65, -24.16) * mm});
            skLineSegment(sketch, "E1543", {"start": v(-19.65, -24.16) * mm, "end": v(-19.5, -24.13) * mm});
            skLineSegment(sketch, "E1544", {"start": v(-19.5, -24.13) * mm, "end": v(-19.38, -24.04) * mm});
            skLineSegment(sketch, "E1545", {"start": v(-19.38, -24.04) * mm, "end": v(-18.99, -23.58) * mm});
            skLineSegment(sketch, "E1546", {"start": v(-18.99, -23.58) * mm, "end": v(-18.89, -23.5) * mm});
            skLineSegment(sketch, "E1547", {"start": v(-18.89, -23.5) * mm, "end": v(-18.78, -23.42) * mm});
            skLineSegment(sketch, "E1548", {"start": v(-18.78, -23.42) * mm, "end": v(-18.67, -23.35) * mm});
            skLineSegment(sketch, "E1549", {"start": v(-18.67, -23.35) * mm, "end": v(-18.55, -23.3) * mm});
            skLineSegment(sketch, "E1550", {"start": v(-18.55, -23.3) * mm, "end": v(-18.43, -23.25) * mm});
            skLineSegment(sketch, "E1551", {"start": v(-18.43, -23.25) * mm, "end": v(-18.3, -23.21) * mm});
            skLineSegment(sketch, "E1552", {"start": v(-18.3, -23.21) * mm, "end": v(-18.18, -23.2) * mm});
            skLineSegment(sketch, "E1553", {"start": v(-18.18, -23.2) * mm, "end": v(-18.05, -23.18) * mm});
            skLineSegment(sketch, "E1554", {"start": v(-18.05, -23.18) * mm, "end": v(-17.92, -23.18) * mm});
            skLineSegment(sketch, "E1555", {"start": v(-17.92, -23.18) * mm, "end": v(-17.8, -23.18) * mm});
            skLineSegment(sketch, "E1556", {"start": v(-17.8, -23.18) * mm, "end": v(-17.66, -23.2) * mm});
            skLineSegment(sketch, "E1557", {"start": v(-17.66, -23.2) * mm, "end": v(-17.54, -23.23) * mm});
            skLineSegment(sketch, "E1558", {"start": v(-17.54, -23.23) * mm, "end": v(-17.4, -23.27) * mm});
            skLineSegment(sketch, "E1559", {"start": v(-17.4, -23.27) * mm, "end": v(-17.28, -23.32) * mm});
            skLineSegment(sketch, "E1560", {"start": v(-17.28, -23.32) * mm, "end": v(-17.16, -23.39) * mm});
            skLineSegment(sketch, "E1561", {"start": v(-17.16, -23.39) * mm, "end": v(-17.04, -23.46) * mm});
            skLineSegment(sketch, "E1562", {"start": v(-17.04, -23.46) * mm, "end": v(-16.94, -23.55) * mm});
            skLineSegment(sketch, "E1563", {"start": v(-16.94, -23.55) * mm, "end": v(-16.84, -23.65) * mm});
            skLineSegment(sketch, "E1564", {"start": v(-16.84, -23.65) * mm, "end": v(-16.75, -23.75) * mm});
            skLineSegment(sketch, "E1565", {"start": v(-16.75, -23.75) * mm, "end": v(-16.68, -23.86) * mm});
            skLineSegment(sketch, "E1566", {"start": v(-16.68, -23.86) * mm, "end": v(-16.6, -23.97) * mm});
            skLineSegment(sketch, "E1567", {"start": v(-16.6, -23.97) * mm, "end": v(-16.55, -24.09) * mm});
            skLineSegment(sketch, "E1568", {"start": v(-16.55, -24.09) * mm, "end": v(-16.5, -24.2) * mm});
            skLineSegment(sketch, "E1569", {"start": v(-16.5, -24.2) * mm, "end": v(-16.46, -24.33) * mm});
            skLineSegment(sketch, "E1570", {"start": v(-16.46, -24.33) * mm, "end": v(-16.44, -24.46) * mm});
            skLineSegment(sketch, "E1571", {"start": v(-16.44, -24.46) * mm, "end": v(-16.42, -24.59) * mm});
            skLineSegment(sketch, "E1572", {"start": v(-16.42, -24.59) * mm, "end": v(-16.42, -24.71) * mm});
            skLineSegment(sketch, "E1573", {"start": v(-16.42, -24.71) * mm, "end": v(-16.42, -24.84) * mm});
            skLineSegment(sketch, "E1574", {"start": v(-16.42, -24.84) * mm, "end": v(-16.44, -24.97) * mm});
            skLineSegment(sketch, "E1575", {"start": v(-16.44, -24.97) * mm, "end": v(-16.47, -25.1) * mm});
            skLineSegment(sketch, "E1576", {"start": v(-16.47, -25.1) * mm, "end": v(-16.5, -25.22) * mm});
            skLineSegment(sketch, "E1577", {"start": v(-16.5, -25.22) * mm, "end": v(-16.56, -25.34) * mm});
            skLineSegment(sketch, "E1578", {"start": v(-16.56, -25.34) * mm, "end": v(-16.88, -25.86) * mm});
            skLineSegment(sketch, "E1579", {"start": v(-16.88, -25.86) * mm, "end": v(-16.92, -26) * mm});
            skLineSegment(sketch, "E1580", {"start": v(-16.92, -26) * mm, "end": v(-16.9, -26.16) * mm});
            skLineSegment(sketch, "E1581", {"start": v(-16.9, -26.16) * mm, "end": v(-16.84, -26.3) * mm});
            skLineSegment(sketch, "E1582", {"start": v(-16.84, -26.3) * mm, "end": v(-16.74, -26.4) * mm});
            skLineSegment(sketch, "E1583", {"start": v(-16.74, -26.4) * mm, "end": v(-16.33, -26.65) * mm});
            skLineSegment(sketch, "E1584", {"start": v(-16.33, -26.65) * mm, "end": v(-15.91, -26.9) * mm});
            skLineSegment(sketch, "E1585", {"start": v(-15.91, -26.9) * mm, "end": v(-15.78, -26.94) * mm});
            skLineSegment(sketch, "E1586", {"start": v(-15.78, -26.94) * mm, "end": v(-15.63, -26.93) * mm});
            skLineSegment(sketch, "E1587", {"start": v(-15.63, -26.93) * mm, "end": v(-15.5, -26.88) * mm});
            skLineSegment(sketch, "E1588", {"start": v(-15.5, -26.88) * mm, "end": v(-15.38, -26.78) * mm});
            skLineSegment(sketch, "E1589", {"start": v(-15.38, -26.78) * mm, "end": v(-15.07, -26.26) * mm});
            skLineSegment(sketch, "E1590", {"start": v(-15.07, -26.26) * mm, "end": v(-14.98, -26.16) * mm});
            skLineSegment(sketch, "E1591", {"start": v(-14.98, -26.16) * mm, "end": v(-14.89, -26.06) * mm});
            skLineSegment(sketch, "E1592", {"start": v(-14.89, -26.06) * mm, "end": v(-14.79, -25.98) * mm});
            skLineSegment(sketch, "E1593", {"start": v(-14.79, -25.98) * mm, "end": v(-14.68, -25.9) * mm});
            skLineSegment(sketch, "E1594", {"start": v(-14.68, -25.9) * mm, "end": v(-14.57, -25.85) * mm});
            skLineSegment(sketch, "E1595", {"start": v(-14.57, -25.85) * mm, "end": v(-14.45, -25.8) * mm});
            skLineSegment(sketch, "E1596", {"start": v(-14.45, -25.8) * mm, "end": v(-14.33, -25.75) * mm});
            skLineSegment(sketch, "E1597", {"start": v(-14.33, -25.75) * mm, "end": v(-14.2, -25.72) * mm});
            skLineSegment(sketch, "E1598", {"start": v(-14.2, -25.72) * mm, "end": v(-14.08, -25.7) * mm});
            skLineSegment(sketch, "E1599", {"start": v(-14.08, -25.7) * mm, "end": v(-13.95, -25.68) * mm});
            skLineSegment(sketch, "E1600", {"start": v(-13.95, -25.68) * mm, "end": v(-13.82, -25.68) * mm});
            skLineSegment(sketch, "E1601", {"start": v(-13.82, -25.68) * mm, "end": v(-13.69, -25.69) * mm});
            skLineSegment(sketch, "E1602", {"start": v(-13.69, -25.69) * mm, "end": v(-13.55, -25.7) * mm});
            skLineSegment(sketch, "E1603", {"start": v(-13.55, -25.7) * mm, "end": v(-13.42, -25.74) * mm});
            skLineSegment(sketch, "E1604", {"start": v(-13.42, -25.74) * mm, "end": v(-13.3, -25.78) * mm});
            skLineSegment(sketch, "E1605", {"start": v(-13.3, -25.78) * mm, "end": v(-13.16, -25.84) * mm});
            skLineSegment(sketch, "E1606", {"start": v(-13.16, -25.84) * mm, "end": v(-13.05, -25.9) * mm});
            skLineSegment(sketch, "E1607", {"start": v(-13.05, -25.9) * mm, "end": v(-12.94, -25.99) * mm});
            skLineSegment(sketch, "E1608", {"start": v(-12.94, -25.99) * mm, "end": v(-12.83, -26.08) * mm});
            skLineSegment(sketch, "E1609", {"start": v(-12.83, -26.08) * mm, "end": v(-12.74, -26.17) * mm});
            skLineSegment(sketch, "E1610", {"start": v(-12.74, -26.17) * mm, "end": v(-12.65, -26.27) * mm});
            skLineSegment(sketch, "E1611", {"start": v(-12.65, -26.27) * mm, "end": v(-12.58, -26.38) * mm});
            skLineSegment(sketch, "E1612", {"start": v(-12.58, -26.38) * mm, "end": v(-12.51, -26.5) * mm});
            skLineSegment(sketch, "E1613", {"start": v(-12.51, -26.5) * mm, "end": v(-12.46, -26.6) * mm});
            skLineSegment(sketch, "E1614", {"start": v(-12.46, -26.6) * mm, "end": v(-12.4, -26.73) * mm});
            skLineSegment(sketch, "E1615", {"start": v(-12.4, -26.73) * mm, "end": v(-12.37, -26.85) * mm});
            skLineSegment(sketch, "E1616", {"start": v(-12.37, -26.85) * mm, "end": v(-12.35, -26.98) * mm});
            skLineSegment(sketch, "E1617", {"start": v(-12.35, -26.98) * mm, "end": v(-12.33, -27.1) * mm});
            skLineSegment(sketch, "E1618", {"start": v(-12.33, -27.1) * mm, "end": v(-12.33, -27.24) * mm});
            skLineSegment(sketch, "E1619", {"start": v(-12.33, -27.24) * mm, "end": v(-12.34, -27.36) * mm});
            skLineSegment(sketch, "E1620", {"start": v(-12.34, -27.36) * mm, "end": v(-12.36, -27.5) * mm});
            skLineSegment(sketch, "E1621", {"start": v(-12.36, -27.5) * mm, "end": v(-12.39, -27.62) * mm});
            skLineSegment(sketch, "E1622", {"start": v(-12.39, -27.62) * mm, "end": v(-12.62, -28.18) * mm});
            skLineSegment(sketch, "E1623", {"start": v(-12.62, -28.18) * mm, "end": v(-12.64, -28.33) * mm});
            skLineSegment(sketch, "E1624", {"start": v(-12.64, -28.33) * mm, "end": v(-12.6, -28.48) * mm});
            skLineSegment(sketch, "E1625", {"start": v(-12.6, -28.48) * mm, "end": v(-12.52, -28.6) * mm});
            skLineSegment(sketch, "E1626", {"start": v(-12.52, -28.6) * mm, "end": v(-12.4, -28.68) * mm});
            skLineSegment(sketch, "E1627", {"start": v(-12.4, -28.68) * mm, "end": v(-11.96, -28.88) * mm});
            skLineSegment(sketch, "E1628", {"start": v(-11.96, -28.88) * mm, "end": v(-11.5, -29.06) * mm});
            skLineSegment(sketch, "E1629", {"start": v(-11.5, -29.06) * mm, "end": v(-11.38, -29.08) * mm});
            skLineSegment(sketch, "E1630", {"start": v(-11.38, -29.08) * mm, "end": v(-11.23, -29.05) * mm});
            skLineSegment(sketch, "E1631", {"start": v(-11.23, -29.05) * mm, "end": v(-11.1, -28.97) * mm});
            skLineSegment(sketch, "E1632", {"start": v(-11.1, -28.97) * mm, "end": v(-11, -28.85) * mm});
            skLineSegment(sketch, "E1633", {"start": v(-11, -28.85) * mm, "end": v(-10.77, -28.3) * mm});
            skLineSegment(sketch, "E1634", {"start": v(-10.77, -28.3) * mm, "end": v(-10.7, -28.18) * mm});
            skLineSegment(sketch, "E1635", {"start": v(-10.7, -28.18) * mm, "end": v(-10.63, -28.07) * mm});
            skLineSegment(sketch, "E1636", {"start": v(-10.63, -28.07) * mm, "end": v(-10.54, -27.98) * mm});
            skLineSegment(sketch, "E1637", {"start": v(-10.54, -27.98) * mm, "end": v(-10.45, -27.89) * mm});
            skLineSegment(sketch, "E1638", {"start": v(-10.45, -27.89) * mm, "end": v(-10.35, -27.8) * mm});
            skLineSegment(sketch, "E1639", {"start": v(-10.35, -27.8) * mm, "end": v(-10.24, -27.74) * mm});
            skLineSegment(sketch, "E1640", {"start": v(-10.24, -27.74) * mm, "end": v(-10.13, -27.67) * mm});
            skLineSegment(sketch, "E1641", {"start": v(-10.13, -27.67) * mm, "end": v(-10, -27.62) * mm});
            skLineSegment(sketch, "E1642", {"start": v(-10, -27.62) * mm, "end": v(-9.89, -27.58) * mm});
            skLineSegment(sketch, "E1643", {"start": v(-9.89, -27.58) * mm, "end": v(-9.76, -27.55) * mm});
            skLineSegment(sketch, "E1644", {"start": v(-9.76, -27.55) * mm, "end": v(-9.63, -27.53) * mm});
            skLineSegment(sketch, "E1645", {"start": v(-9.63, -27.53) * mm, "end": v(-9.5, -27.51) * mm});
            skLineSegment(sketch, "E1646", {"start": v(-9.5, -27.51) * mm, "end": v(-9.36, -27.51) * mm});
            skLineSegment(sketch, "E1647", {"start": v(-9.36, -27.51) * mm, "end": v(-9.23, -27.52) * mm});
            skLineSegment(sketch, "E1648", {"start": v(-9.23, -27.52) * mm, "end": v(-9.1, -27.55) * mm});
            skLineSegment(sketch, "E1649", {"start": v(-9.1, -27.55) * mm, "end": v(-8.96, -27.58) * mm});
            skLineSegment(sketch, "E1650", {"start": v(-8.96, -27.58) * mm, "end": v(-8.83, -27.63) * mm});
            skLineSegment(sketch, "E1651", {"start": v(-8.83, -27.63) * mm, "end": v(-8.71, -27.7) * mm});
            skLineSegment(sketch, "E1652", {"start": v(-8.71, -27.7) * mm, "end": v(-8.6, -27.76) * mm});
            skLineSegment(sketch, "E1653", {"start": v(-8.6, -27.76) * mm, "end": v(-8.49, -27.84) * mm});
            skLineSegment(sketch, "E1654", {"start": v(-8.49, -27.84) * mm, "end": v(-8.39, -27.93) * mm});
            skLineSegment(sketch, "E1655", {"start": v(-8.39, -27.93) * mm, "end": v(-8.3, -28.02) * mm});
            skLineSegment(sketch, "E1656", {"start": v(-8.3, -28.02) * mm, "end": v(-8.21, -28.12) * mm});
            skLineSegment(sketch, "E1657", {"start": v(-8.21, -28.12) * mm, "end": v(-8.14, -28.23) * mm});
            skLineSegment(sketch, "E1658", {"start": v(-8.14, -28.23) * mm, "end": v(-8.07, -28.34) * mm});
            skLineSegment(sketch, "E1659", {"start": v(-8.07, -28.34) * mm, "end": v(-8.02, -28.46) * mm});
            skLineSegment(sketch, "E1660", {"start": v(-8.02, -28.46) * mm, "end": v(-7.97, -28.58) * mm});
            skLineSegment(sketch, "E1661", {"start": v(-7.97, -28.58) * mm, "end": v(-7.94, -28.7) * mm});
            skLineSegment(sketch, "E1662", {"start": v(-7.94, -28.7) * mm, "end": v(-7.92, -28.83) * mm});
            skLineSegment(sketch, "E1663", {"start": v(-7.92, -28.83) * mm, "end": v(-7.9, -28.96) * mm});
            skLineSegment(sketch, "E1664", {"start": v(-7.9, -28.96) * mm, "end": v(-7.9, -29.09) * mm});
            skLineSegment(sketch, "E1665", {"start": v(-7.9, -29.09) * mm, "end": v(-7.91, -29.22) * mm});
            skLineSegment(sketch, "E1666", {"start": v(-7.91, -29.22) * mm, "end": v(-8.06, -29.8) * mm});
            skLineSegment(sketch, "E1667", {"start": v(-8.06, -29.8) * mm, "end": v(-8.05, -29.96) * mm});
            skLineSegment(sketch, "E1668", {"start": v(-8.05, -29.96) * mm, "end": v(-8, -30.1) * mm});
            skLineSegment(sketch, "E1669", {"start": v(-8, -30.1) * mm, "end": v(-7.89, -30.21) * mm});
            skLineSegment(sketch, "E1670", {"start": v(-7.89, -30.21) * mm, "end": v(-7.77, -30.27) * mm});
            skLineSegment(sketch, "E1671", {"start": v(-7.77, -30.27) * mm, "end": v(-7.3, -30.4) * mm});
            skLineSegment(sketch, "E1672", {"start": v(-7.3, -30.4) * mm, "end": v(-6.82, -30.5) * mm});
            skLineSegment(sketch, "E1673", {"start": v(-6.82, -30.5) * mm, "end": v(-6.69, -30.5) * mm});
            skLineSegment(sketch, "E1674", {"start": v(-6.69, -30.5) * mm, "end": v(-6.54, -30.45) * mm});
            skLineSegment(sketch, "E1675", {"start": v(-6.54, -30.45) * mm, "end": v(-6.43, -30.35) * mm});
            skLineSegment(sketch, "E1676", {"start": v(-6.43, -30.35) * mm, "end": v(-6.35, -30.22) * mm});
            skLineSegment(sketch, "E1677", {"start": v(-6.35, -30.22) * mm, "end": v(-6.21, -29.63) * mm});
            skLineSegment(sketch, "E1678", {"start": v(-6.21, -29.63) * mm, "end": v(-6.16, -29.5) * mm});
            skLineSegment(sketch, "E1679", {"start": v(-6.16, -29.5) * mm, "end": v(-6.1, -29.39) * mm});
            skLineSegment(sketch, "E1680", {"start": v(-6.1, -29.39) * mm, "end": v(-6.03, -29.28) * mm});
            skLineSegment(sketch, "E1681", {"start": v(-6.03, -29.28) * mm, "end": v(-5.96, -29.18) * mm});
            skLineSegment(sketch, "E1682", {"start": v(-5.96, -29.18) * mm, "end": v(-5.87, -29.08) * mm});
            skLineSegment(sketch, "E1683", {"start": v(-5.87, -29.08) * mm, "end": v(-5.77, -29) * mm});
            skLineSegment(sketch, "E1684", {"start": v(-5.77, -29) * mm, "end": v(-5.67, -28.92) * mm});
            skLineSegment(sketch, "E1685", {"start": v(-5.67, -28.92) * mm, "end": v(-5.56, -28.85) * mm});
            skLineSegment(sketch, "E1686", {"start": v(-5.56, -28.85) * mm, "end": v(-5.45, -28.79) * mm});
            skLineSegment(sketch, "E1687", {"start": v(-5.45, -28.79) * mm, "end": v(-5.33, -28.74) * mm});
            skLineSegment(sketch, "E1688", {"start": v(-5.33, -28.74) * mm, "end": v(-5.2, -28.7) * mm});
            skLineSegment(sketch, "E1689", {"start": v(-5.2, -28.7) * mm, "end": v(-5.08, -28.66) * mm});
            skLineSegment(sketch, "E1690", {"start": v(-5.08, -28.66) * mm, "end": v(-4.95, -28.64) * mm});
            skLineSegment(sketch, "E1691", {"start": v(-4.95, -28.64) * mm, "end": v(-4.81, -28.63) * mm});
            skLineSegment(sketch, "E1692", {"start": v(-4.81, -28.63) * mm, "end": v(-4.67, -28.63) * mm});
            skLineSegment(sketch, "E1693", {"start": v(-4.67, -28.63) * mm, "end": v(-4.54, -28.64) * mm});
            skLineSegment(sketch, "E1694", {"start": v(-4.54, -28.64) * mm, "end": v(-4.4, -28.67) * mm});
            skLineSegment(sketch, "E1695", {"start": v(-4.4, -28.67) * mm, "end": v(-4.27, -28.71) * mm});
            skLineSegment(sketch, "E1696", {"start": v(-4.27, -28.71) * mm, "end": v(-4.15, -28.77) * mm});
            skLineSegment(sketch, "E1697", {"start": v(-4.15, -28.77) * mm, "end": v(-4.03, -28.83) * mm});
            skLineSegment(sketch, "E1698", {"start": v(-4.03, -28.83) * mm, "end": v(-3.92, -28.9) * mm});
            skLineSegment(sketch, "E1699", {"start": v(-3.92, -28.9) * mm, "end": v(-3.81, -28.98) * mm});
            skLineSegment(sketch, "E1700", {"start": v(-3.81, -28.98) * mm, "end": v(-3.71, -29.06) * mm});
            skLineSegment(sketch, "E1701", {"start": v(-3.71, -29.06) * mm, "end": v(-3.62, -29.16) * mm});
            skLineSegment(sketch, "E1702", {"start": v(-3.62, -29.16) * mm, "end": v(-3.54, -29.26) * mm});
            skLineSegment(sketch, "E1703", {"start": v(-3.54, -29.26) * mm, "end": v(-3.47, -29.36) * mm});
            skLineSegment(sketch, "E1704", {"start": v(-3.47, -29.36) * mm, "end": v(-3.4, -29.47) * mm});
            skLineSegment(sketch, "E1705", {"start": v(-3.4, -29.47) * mm, "end": v(-3.35, -29.6) * mm});
            skLineSegment(sketch, "E1706", {"start": v(-3.35, -29.6) * mm, "end": v(-3.3, -29.71) * mm});
            skLineSegment(sketch, "E1707", {"start": v(-3.3, -29.71) * mm, "end": v(-3.28, -29.84) * mm});
            skLineSegment(sketch, "E1708", {"start": v(-3.28, -29.84) * mm, "end": v(-3.26, -29.97) * mm});
            skLineSegment(sketch, "E1709", {"start": v(-3.26, -29.97) * mm, "end": v(-3.25, -30.1) * mm});
            skLineSegment(sketch, "E1710", {"start": v(-3.25, -30.1) * mm, "end": v(-3.3, -30.7) * mm});
            skLineSegment(sketch, "E1711", {"start": v(-3.3, -30.7) * mm, "end": v(-3.27, -30.85) * mm});
            skLineSegment(sketch, "E1712", {"start": v(-3.27, -30.85) * mm, "end": v(-3.19, -30.98) * mm});
            skLineSegment(sketch, "E1713", {"start": v(-3.19, -30.98) * mm, "end": v(-3.07, -31.07) * mm});
            skLineSegment(sketch, "E1714", {"start": v(-3.07, -31.07) * mm, "end": v(-2.94, -31.12) * mm});
            skLineSegment(sketch, "E1715", {"start": v(-2.94, -31.12) * mm, "end": v(-2.45, -31.16) * mm});
            skLineSegment(sketch, "E1716", {"start": v(-2.45, -31.16) * mm, "end": v(-1.97, -31.2) * mm});
            skLineSegment(sketch, "E1717", {"start": v(-1.97, -31.2) * mm, "end": v(-1.83, -31.17) * mm});
            skLineSegment(sketch, "E1718", {"start": v(-1.83, -31.17) * mm, "end": v(-1.7, -31.1) * mm});
            skLineSegment(sketch, "E1719", {"start": v(-1.7, -31.1) * mm, "end": v(-1.6, -30.98) * mm});
            skLineSegment(sketch, "E1720", {"start": v(-1.6, -30.98) * mm, "end": v(-1.54, -30.84) * mm});
            skLineSegment(sketch, "E1721", {"start": v(-1.54, -30.84) * mm, "end": v(-1.5, -30.24) * mm});
            skLineSegment(sketch, "E1722", {"start": v(-1.5, -30.24) * mm, "end": v(-1.47, -30.1) * mm});
            skLineSegment(sketch, "E1723", {"start": v(-1.47, -30.1) * mm, "end": v(-1.43, -29.98) * mm});
            skLineSegment(sketch, "E1724", {"start": v(-1.43, -29.98) * mm, "end": v(-1.38, -29.86) * mm});
            skLineSegment(sketch, "E1725", {"start": v(-1.38, -29.86) * mm, "end": v(-1.32, -29.75) * mm});
            skLineSegment(sketch, "E1726", {"start": v(-1.32, -29.75) * mm, "end": v(-1.25, -29.64) * mm});
            skLineSegment(sketch, "E1727", {"start": v(-1.25, -29.64) * mm, "end": v(-1.17, -29.54) * mm});
            skLineSegment(sketch, "E1728", {"start": v(-1.17, -29.54) * mm, "end": v(-1.08, -29.45) * mm});
            skLineSegment(sketch, "E1729", {"start": v(-1.08, -29.45) * mm, "end": v(-0.98, -29.36) * mm});
            skLineSegment(sketch, "E1730", {"start": v(-0.98, -29.36) * mm, "end": v(-0.88, -29.29) * mm});
            skLineSegment(sketch, "E1731", {"start": v(-0.88, -29.29) * mm, "end": v(-0.77, -29.22) * mm});
            skLineSegment(sketch, "E1732", {"start": v(-0.77, -29.22) * mm, "end": v(-0.65, -29.15) * mm});
            skLineSegment(sketch, "E1733", {"start": v(-0.65, -29.15) * mm, "end": v(-0.53, -29.1) * mm});
            skLineSegment(sketch, "E1734", {"start": v(-0.53, -29.1) * mm, "end": v(-0.4, -29.06) * mm});
            skLineSegment(sketch, "E1735", {"start": v(-0.4, -29.06) * mm, "end": v(-0.27, -29.03) * mm});
            skLineSegment(sketch, "E1736", {"start": v(-0.27, -29.03) * mm, "end": v(-0.14, -29) * mm});
            skLineSegment(sketch, "E1737", {"start": v(-0.14, -29) * mm, "end": v(0, -29) * mm});
            skLineSegment(sketch, "E1738", {"start": v(0, -29) * mm, "end": v(0.14, -29) * mm});
            skLineSegment(sketch, "E1739", {"start": v(0.14, -29) * mm, "end": v(0.27, -29.03) * mm});
            skLineSegment(sketch, "E1740", {"start": v(0.27, -29.03) * mm, "end": v(0.4, -29.06) * mm});
            skLineSegment(sketch, "E1741", {"start": v(0.4, -29.06) * mm, "end": v(0.53, -29.1) * mm});
            skLineSegment(sketch, "E1742", {"start": v(0.53, -29.1) * mm, "end": v(0.65, -29.15) * mm});
            skLineSegment(sketch, "E1743", {"start": v(0.65, -29.15) * mm, "end": v(0.77, -29.22) * mm});
            skLineSegment(sketch, "E1744", {"start": v(0.77, -29.22) * mm, "end": v(0.88, -29.28) * mm});
            skLineSegment(sketch, "E1745", {"start": v(0.88, -29.28) * mm, "end": v(0.98, -29.36) * mm});
            skLineSegment(sketch, "E1746", {"start": v(0.98, -29.36) * mm, "end": v(1.08, -29.45) * mm});
            skLineSegment(sketch, "E1747", {"start": v(1.08, -29.45) * mm, "end": v(1.17, -29.54) * mm});
            skLineSegment(sketch, "E1748", {"start": v(1.17, -29.54) * mm, "end": v(1.25, -29.64) * mm});
            skLineSegment(sketch, "E1749", {"start": v(1.25, -29.64) * mm, "end": v(1.32, -29.75) * mm});
            skLineSegment(sketch, "E1750", {"start": v(1.32, -29.75) * mm, "end": v(1.38, -29.86) * mm});
            skLineSegment(sketch, "E1751", {"start": v(1.38, -29.86) * mm, "end": v(1.43, -29.98) * mm});
            skLineSegment(sketch, "E1752", {"start": v(1.43, -29.98) * mm, "end": v(1.47, -30.1) * mm});
            skLineSegment(sketch, "E1753", {"start": v(1.47, -30.1) * mm, "end": v(1.5, -30.24) * mm});
            skLineSegment(sketch, "E1754", {"start": v(1.5, -30.24) * mm, "end": v(1.54, -30.84) * mm});
            skLineSegment(sketch, "E1755", {"start": v(1.54, -30.84) * mm, "end": v(1.6, -30.98) * mm});
            skLineSegment(sketch, "E1756", {"start": v(1.6, -30.98) * mm, "end": v(1.7, -31.1) * mm});
            skLineSegment(sketch, "E1757", {"start": v(1.7, -31.1) * mm, "end": v(1.83, -31.17) * mm});
            skLineSegment(sketch, "E1758", {"start": v(1.83, -31.17) * mm, "end": v(1.97, -31.2) * mm});
            skLineSegment(sketch, "E1759", {"start": v(1.97, -31.2) * mm, "end": v(2.45, -31.16) * mm});
            skLineSegment(sketch, "E1760", {"start": v(-0.8, -2.47) * mm, "end": v(-1.53, -2.1) * mm});
            skLineSegment(sketch, "E1761", {"start": v(-1.53, -2.1) * mm, "end": v(-2.1, -1.53) * mm});
            skLineSegment(sketch, "E1762", {"start": v(-2.1, -1.53) * mm, "end": v(-2.47, -0.8) * mm});
            skLineSegment(sketch, "E1763", {"start": v(-2.47, -0.8) * mm, "end": v(-2.6, 0) * mm});
            skLineSegment(sketch, "E1764", {"start": v(-2.6, 0) * mm, "end": v(-2.47, 0.8) * mm});
            skLineSegment(sketch, "E1765", {"start": v(-2.47, 0.8) * mm, "end": v(-2.1, 1.53) * mm});
            skLineSegment(sketch, "E1766", {"start": v(-2.1, 1.53) * mm, "end": v(-1.53, 2.1) * mm});
            skLineSegment(sketch, "E1767", {"start": v(-1.53, 2.1) * mm, "end": v(-0.8, 2.47) * mm});
            skLineSegment(sketch, "E1768", {"start": v(-0.8, 2.47) * mm, "end": v(0, 2.6) * mm});
            skLineSegment(sketch, "E1769", {"start": v(0, 2.6) * mm, "end": v(0.8, 2.47) * mm});
            skLineSegment(sketch, "E1770", {"start": v(0.8, 2.47) * mm, "end": v(1.53, 2.1) * mm});
            skLineSegment(sketch, "E1771", {"start": v(1.53, 2.1) * mm, "end": v(2.1, 1.53) * mm});
            skLineSegment(sketch, "E1772", {"start": v(2.1, 1.53) * mm, "end": v(2.47, 0.8) * mm});
            skLineSegment(sketch, "E1773", {"start": v(2.47, 0.8) * mm, "end": v(2.6, 0) * mm});
            skLineSegment(sketch, "E1774", {"start": v(2.6, 0) * mm, "end": v(2.47, -0.8) * mm});
            skLineSegment(sketch, "E1775", {"start": v(2.47, -0.8) * mm, "end": v(2.1, -1.53) * mm});
            skLineSegment(sketch, "E1776", {"start": v(2.1, -1.53) * mm, "end": v(1.53, -2.1) * mm});
            skLineSegment(sketch, "E1777", {"start": v(1.53, -2.1) * mm, "end": v(0.8, -2.47) * mm});
            skLineSegment(sketch, "E1778", {"start": v(0.8, -2.47) * mm, "end": v(0, -2.6) * mm});
            skLineSegment(sketch, "E1779", {"start": v(0, -2.6) * mm, "end": v(-0.8, -2.47) * mm});
            skArc(sketch, "E1780.0.0", {"start": v(3.88, 6.29) * mm, "mid": v(4.75, 7.5) * mm, "end": v(6.04, 8.26) * mm});
            skArc(sketch, "E1780.0.1", {"start": v(6.04, 8.26) * mm, "mid": v(6.34, 8.03) * mm, "end": v(6.64, 7.78) * mm});
            skArc(sketch, "E1780.0.2", {"start": v(6.64, 7.78) * mm, "mid": v(6.19, 6.36) * mm, "end": v(5.2, 5.24) * mm});
            skArc(sketch, "E1780.0.3", {"start": v(5.2, 5.24) * mm, "mid": v(5.73, 4.64) * mm, "end": v(6.2, 4) * mm});
            skArc(sketch, "E1780.0.4", {"start": v(6.2, 4) * mm, "mid": v(7.5, 4.71) * mm, "end": v(8.99, 4.83) * mm});
            skArc(sketch, "E1780.0.5", {"start": v(8.99, 4.83) * mm, "mid": v(9.16, 4.5) * mm, "end": v(9.32, 4.14) * mm});
            skArc(sketch, "E1780.0.6", {"start": v(9.32, 4.14) * mm, "mid": v(8.3, 3.05) * mm, "end": v(6.92, 2.48) * mm});
            skArc(sketch, "E1780.0.7", {"start": v(6.92, 2.48) * mm, "mid": v(7.14, 1.71) * mm, "end": v(7.28, 0.92) * mm});
            skArc(sketch, "E1780.0.8", {"start": v(7.28, 0.92) * mm, "mid": v(8.77, 1) * mm, "end": v(10.16, 0.47) * mm});
            skArc(sketch, "E1780.0.9", {"start": v(10.16, 0.47) * mm, "mid": v(10.17, 0.08) * mm, "end": v(10.16, -0.3) * mm});
            skArc(sketch, "E1780.0.10", {"start": v(10.16, -0.3) * mm, "mid": v(8.77, -0.84) * mm, "end": v(7.28, -0.75) * mm});
            skArc(sketch, "E1780.0.11", {"start": v(7.28, -0.75) * mm, "mid": v(7.14, -1.54) * mm, "end": v(6.92, -2.32) * mm});
            skArc(sketch, "E1780.0.12", {"start": v(6.92, -2.32) * mm, "mid": v(8.3, -2.89) * mm, "end": v(9.32, -3.98) * mm});
            skArc(sketch, "E1780.0.13", {"start": v(9.32, -3.98) * mm, "mid": v(9.16, -4.33) * mm, "end": v(8.99, -4.67) * mm});
            skArc(sketch, "E1780.0.14", {"start": v(8.99, -4.67) * mm, "mid": v(7.5, -4.55) * mm, "end": v(6.2, -3.82) * mm});
            skArc(sketch, "E1780.0.15", {"start": v(6.2, -3.82) * mm, "mid": v(5.73, -4.48) * mm, "end": v(5.2, -5.08) * mm});
            skArc(sketch, "E1780.0.16", {"start": v(5.2, -5.08) * mm, "mid": v(6.19, -6.2) * mm, "end": v(6.64, -7.61) * mm});
            skArc(sketch, "E1780.0.17", {"start": v(6.64, -7.61) * mm, "mid": v(6.34, -7.86) * mm, "end": v(6.04, -8.1) * mm});
            skArc(sketch, "E1780.0.18", {"start": v(6.04, -8.1) * mm, "mid": v(4.75, -7.34) * mm, "end": v(3.88, -6.12) * mm});
            skArc(sketch, "E1780.0.19", {"start": v(3.88, -6.12) * mm, "mid": v(3.18, -6.5) * mm, "end": v(2.44, -6.82) * mm});
            skArc(sketch, "E1780.0.20", {"start": v(2.44, -6.82) * mm, "mid": v(2.85, -8.25) * mm, "end": v(2.64, -9.73) * mm});
            skArc(sketch, "E1780.0.21", {"start": v(2.64, -9.73) * mm, "mid": v(2.27, -9.82) * mm, "end": v(1.9, -9.9) * mm});
            skArc(sketch, "E1780.0.22", {"start": v(1.9, -9.9) * mm, "mid": v(1.06, -8.66) * mm, "end": v(0.8, -7.19) * mm});
            skArc(sketch, "E1780.0.23", {"start": v(0.8, -7.19) * mm, "mid": v(0, -7.23) * mm, "end": v(-0.8, -7.19) * mm});
            skArc(sketch, "E1780.0.24", {"start": v(-0.8, -7.19) * mm, "mid": v(-1.04, -8.66) * mm, "end": v(-1.88, -9.9) * mm});
            skArc(sketch, "E1780.0.25", {"start": v(-1.88, -9.9) * mm, "mid": v(-2.25, -9.82) * mm, "end": v(-2.63, -9.73) * mm});
            skArc(sketch, "E1780.0.26", {"start": v(-2.63, -9.73) * mm, "mid": v(-2.84, -8.25) * mm, "end": v(-2.43, -6.82) * mm});
            skArc(sketch, "E1780.0.27", {"start": v(-2.43, -6.82) * mm, "mid": v(-3.17, -6.5) * mm, "end": v(-3.87, -6.12) * mm});
            skArc(sketch, "E1780.0.28", {"start": v(-3.87, -6.12) * mm, "mid": v(-4.73, -7.34) * mm, "end": v(-6.02, -8.1) * mm});
            skArc(sketch, "E1780.0.29", {"start": v(-6.02, -8.1) * mm, "mid": v(-6.33, -7.86) * mm, "end": v(-6.62, -7.61) * mm});
            skArc(sketch, "E1780.0.30", {"start": v(-6.62, -7.61) * mm, "mid": v(-6.17, -6.2) * mm, "end": v(-5.18, -5.08) * mm});
            skArc(sketch, "E1780.0.31", {"start": v(-5.18, -5.08) * mm, "mid": v(-5.71, -4.48) * mm, "end": v(-6.18, -3.82) * mm});
            skArc(sketch, "E1780.0.32", {"start": v(-6.18, -3.82) * mm, "mid": v(-7.48, -4.55) * mm, "end": v(-8.97, -4.67) * mm});
            skArc(sketch, "E1780.0.33", {"start": v(-8.97, -4.67) * mm, "mid": v(-9.15, -4.33) * mm, "end": v(-9.3, -3.98) * mm});
            skArc(sketch, "E1780.0.34", {"start": v(-9.3, -3.98) * mm, "mid": v(-8.28, -2.89) * mm, "end": v(-6.9, -2.32) * mm});
            skArc(sketch, "E1780.0.35", {"start": v(-6.9, -2.32) * mm, "mid": v(-7.12, -1.54) * mm, "end": v(-7.26, -0.75) * mm});
            skArc(sketch, "E1780.0.36", {"start": v(-7.26, -0.75) * mm, "mid": v(-8.75, -0.84) * mm, "end": v(-10.14, -0.3) * mm});
            skArc(sketch, "E1780.0.37", {"start": v(-10.14, -0.3) * mm, "mid": v(-10.15, 0.08) * mm, "end": v(-10.14, 0.47) * mm});
            skArc(sketch, "E1780.0.38", {"start": v(-10.14, 0.47) * mm, "mid": v(-8.75, 1) * mm, "end": v(-7.26, 0.92) * mm});
            skArc(sketch, "E1780.0.39", {"start": v(-7.26, 0.92) * mm, "mid": v(-7.12, 1.71) * mm, "end": v(-6.9, 2.48) * mm});
            skArc(sketch, "E1780.0.40", {"start": v(-6.9, 2.48) * mm, "mid": v(-8.28, 3.05) * mm, "end": v(-9.3, 4.14) * mm});
            skArc(sketch, "E1780.0.41", {"start": v(-9.3, 4.14) * mm, "mid": v(-9.15, 4.5) * mm, "end": v(-8.97, 4.83) * mm});
            skArc(sketch, "E1780.0.42", {"start": v(-8.97, 4.83) * mm, "mid": v(-7.48, 4.71) * mm, "end": v(-6.18, 4) * mm});
            skArc(sketch, "E1780.0.43", {"start": v(-6.18, 4) * mm, "mid": v(-5.71, 4.64) * mm, "end": v(-5.18, 5.24) * mm});
            skArc(sketch, "E1780.0.44", {"start": v(-5.18, 5.24) * mm, "mid": v(-6.17, 6.36) * mm, "end": v(-6.62, 7.78) * mm});
            skArc(sketch, "E1780.0.45", {"start": v(-6.62, 7.78) * mm, "mid": v(-6.33, 8.03) * mm, "end": v(-6.02, 8.26) * mm});
            skArc(sketch, "E1780.0.46", {"start": v(-6.02, 8.26) * mm, "mid": v(-4.73, 7.5) * mm, "end": v(-3.87, 6.29) * mm});
            skArc(sketch, "E1780.0.47", {"start": v(-3.87, 6.29) * mm, "mid": v(-3.17, 6.67) * mm, "end": v(-2.43, 6.98) * mm});
            skArc(sketch, "E1780.0.48", {"start": v(-2.43, 6.98) * mm, "mid": v(-2.84, 8.42) * mm, "end": v(-2.63, 9.9) * mm});
            skArc(sketch, "E1780.0.49", {"start": v(-2.63, 9.9) * mm, "mid": v(-2.25, 9.99) * mm, "end": v(-1.88, 10.07) * mm});
            skArc(sketch, "E1780.0.50", {"start": v(-1.88, 10.07) * mm, "mid": v(-1.04, 8.83) * mm, "end": v(-0.8, 7.35) * mm});
            skArc(sketch, "E1780.0.51", {"start": v(-0.8, 7.35) * mm, "mid": v(0, 7.4) * mm, "end": v(0.8, 7.35) * mm});
            skArc(sketch, "E1780.0.52", {"start": v(0.8, 7.35) * mm, "mid": v(1.06, 8.83) * mm, "end": v(1.9, 10.07) * mm});
            skArc(sketch, "E1780.0.53", {"start": v(1.9, 10.07) * mm, "mid": v(2.27, 9.99) * mm, "end": v(2.64, 9.9) * mm});
            skArc(sketch, "E1780.0.54", {"start": v(2.64, 9.9) * mm, "mid": v(2.85, 8.42) * mm, "end": v(2.44, 6.98) * mm});
            skArc(sketch, "E1780.0.55", {"start": v(2.44, 6.98) * mm, "mid": v(3.18, 6.67) * mm, "end": v(3.88, 6.29) * mm});
            skSolve(sketch);
        }
        {
            var Q0;
            Q0=makeQuery(id+"F3.imprint","IMPRINT",FACE,{"disambiguationData":[TD([[makeQuery(id+"F3.imprint","IMPRINT",EDGE,{"derivedFrom":sQuery(id+"F3.wireOp",EDGE,"E0")}),1.0]])]});
            extrude(context, id + "F4", {"entities" : qUnion([Q0]), "depth" : (getVariable(context, 'totalThick')) * mm, "offsetDistance" : 25 * mm});
        }
        {
            var Q0;
            Q0=makeQuery(id+"F4.opExtrude","CAP_FACE",FACE,{"disambiguationData":[OSD([sQuery(id+"F3.wireOp",EDGE,"E0"),sQuery(id+"F3.wireOp",EDGE,"E1"),sQuery(id+"F3.wireOp",EDGE,"E2"),sQuery(id+"F3.wireOp",EDGE,"E3"),sQuery(id+"F3.wireOp",EDGE,"E4"),sQuery(id+"F3.wireOp",EDGE,"E5"),sQuery(id+"F3.wireOp",EDGE,"E6"),sQuery(id+"F3.wireOp",EDGE,"E7"),sQuery(id+"F3.wireOp",EDGE,"E8"),sQuery(id+"F3.wireOp",EDGE,"E9"),sQuery(id+"F3.wireOp",EDGE,"E10"),sQuery(id+"F3.wireOp",EDGE,"E11"),sQuery(id+"F3.wireOp",EDGE,"E12"),sQuery(id+"F3.wireOp",EDGE,"E13"),sQuery(id+"F3.wireOp",EDGE,"E14"),sQuery(id+"F3.wireOp",EDGE,"E15"),sQuery(id+"F3.wireOp",EDGE,"E16"),sQuery(id+"F3.wireOp",EDGE,"E17"),sQuery(id+"F3.wireOp",EDGE,"E18"),sQuery(id+"F3.wireOp",EDGE,"E19"),sQuery(id+"F3.wireOp",EDGE,"E20"),sQuery(id+"F3.wireOp",EDGE,"E21"),sQuery(id+"F3.wireOp",EDGE,"E22"),sQuery(id+"F3.wireOp",EDGE,"E23"),sQuery(id+"F3.wireOp",EDGE,"E24"),sQuery(id+"F3.wireOp",EDGE,"E25"),sQuery(id+"F3.wireOp",EDGE,"E26"),sQuery(id+"F3.wireOp",EDGE,"E27"),sQuery(id+"F3.wireOp",EDGE,"E28"),sQuery(id+"F3.wireOp",EDGE,"E29"),sQuery(id+"F3.wireOp",EDGE,"E30"),sQuery(id+"F3.wireOp",EDGE,"E31"),sQuery(id+"F3.wireOp",EDGE,"E32"),sQuery(id+"F3.wireOp",EDGE,"E33"),sQuery(id+"F3.wireOp",EDGE,"E34"),sQuery(id+"F3.wireOp",EDGE,"E35"),sQuery(id+"F3.wireOp",EDGE,"E36"),sQuery(id+"F3.wireOp",EDGE,"E37"),sQuery(id+"F3.wireOp",EDGE,"E38"),sQuery(id+"F3.wireOp",EDGE,"E39"),sQuery(id+"F3.wireOp",EDGE,"E40"),sQuery(id+"F3.wireOp",EDGE,"E41"),sQuery(id+"F3.wireOp",EDGE,"E42"),sQuery(id+"F3.wireOp",EDGE,"E43"),sQuery(id+"F3.wireOp",EDGE,"E44"),sQuery(id+"F3.wireOp",EDGE,"E45"),sQuery(id+"F3.wireOp",EDGE,"E46"),sQuery(id+"F3.wireOp",EDGE,"E47"),sQuery(id+"F3.wireOp",EDGE,"E48"),sQuery(id+"F3.wireOp",EDGE,"E49"),sQuery(id+"F3.wireOp",EDGE,"E50"),sQuery(id+"F3.wireOp",EDGE,"E51"),sQuery(id+"F3.wireOp",EDGE,"E52"),sQuery(id+"F3.wireOp",EDGE,"E53"),sQuery(id+"F3.wireOp",EDGE,"E54"),sQuery(id+"F3.wireOp",EDGE,"E55"),sQuery(id+"F3.wireOp",EDGE,"E56"),sQuery(id+"F3.wireOp",EDGE,"E57"),sQuery(id+"F3.wireOp",EDGE,"E58"),sQuery(id+"F3.wireOp",EDGE,"E59"),sQuery(id+"F3.wireOp",EDGE,"E60"),sQuery(id+"F3.wireOp",EDGE,"E61"),sQuery(id+"F3.wireOp",EDGE,"E62"),sQuery(id+"F3.wireOp",EDGE,"E63"),sQuery(id+"F3.wireOp",EDGE,"E64"),sQuery(id+"F3.wireOp",EDGE,"E65"),sQuery(id+"F3.wireOp",EDGE,"E66"),sQuery(id+"F3.wireOp",EDGE,"E67"),sQuery(id+"F3.wireOp",EDGE,"E68"),sQuery(id+"F3.wireOp",EDGE,"E69"),sQuery(id+"F3.wireOp",EDGE,"E70"),sQuery(id+"F3.wireOp",EDGE,"E71"),sQuery(id+"F3.wireOp",EDGE,"E72"),sQuery(id+"F3.wireOp",EDGE,"E73"),sQuery(id+"F3.wireOp",EDGE,"E74"),sQuery(id+"F3.wireOp",EDGE,"E75"),sQuery(id+"F3.wireOp",EDGE,"E76"),sQuery(id+"F3.wireOp",EDGE,"E77"),sQuery(id+"F3.wireOp",EDGE,"E78"),sQuery(id+"F3.wireOp",EDGE,"E79"),sQuery(id+"F3.wireOp",EDGE,"E80"),sQuery(id+"F3.wireOp",EDGE,"E81"),sQuery(id+"F3.wireOp",EDGE,"E82"),sQuery(id+"F3.wireOp",EDGE,"E83"),sQuery(id+"F3.wireOp",EDGE,"E84"),sQuery(id+"F3.wireOp",EDGE,"E85"),sQuery(id+"F3.wireOp",EDGE,"E86"),sQuery(id+"F3.wireOp",EDGE,"E87"),sQuery(id+"F3.wireOp",EDGE,"E88"),sQuery(id+"F3.wireOp",EDGE,"E89"),sQuery(id+"F3.wireOp",EDGE,"E90"),sQuery(id+"F3.wireOp",EDGE,"E91"),sQuery(id+"F3.wireOp",EDGE,"E92"),sQuery(id+"F3.wireOp",EDGE,"E93"),sQuery(id+"F3.wireOp",EDGE,"E94"),sQuery(id+"F3.wireOp",EDGE,"E95"),sQuery(id+"F3.wireOp",EDGE,"E96"),sQuery(id+"F3.wireOp",EDGE,"E97"),sQuery(id+"F3.wireOp",EDGE,"E98"),sQuery(id+"F3.wireOp",EDGE,"E99"),sQuery(id+"F3.wireOp",EDGE,"E100"),sQuery(id+"F3.wireOp",EDGE,"E101"),sQuery(id+"F3.wireOp",EDGE,"E102"),sQuery(id+"F3.wireOp",EDGE,"E103"),sQuery(id+"F3.wireOp",EDGE,"E104"),sQuery(id+"F3.wireOp",EDGE,"E105"),sQuery(id+"F3.wireOp",EDGE,"E106"),sQuery(id+"F3.wireOp",EDGE,"E107"),sQuery(id+"F3.wireOp",EDGE,"E108"),sQuery(id+"F3.wireOp",EDGE,"E109"),sQuery(id+"F3.wireOp",EDGE,"E110"),sQuery(id+"F3.wireOp",EDGE,"E111"),sQuery(id+"F3.wireOp",EDGE,"E112"),sQuery(id+"F3.wireOp",EDGE,"E113"),sQuery(id+"F3.wireOp",EDGE,"E114"),sQuery(id+"F3.wireOp",EDGE,"E115"),sQuery(id+"F3.wireOp",EDGE,"E116"),sQuery(id+"F3.wireOp",EDGE,"E117"),sQuery(id+"F3.wireOp",EDGE,"E118"),sQuery(id+"F3.wireOp",EDGE,"E119"),sQuery(id+"F3.wireOp",EDGE,"E120"),sQuery(id+"F3.wireOp",EDGE,"E121"),sQuery(id+"F3.wireOp",EDGE,"E122"),sQuery(id+"F3.wireOp",EDGE,"E123"),sQuery(id+"F3.wireOp",EDGE,"E124"),sQuery(id+"F3.wireOp",EDGE,"E125"),sQuery(id+"F3.wireOp",EDGE,"E126"),sQuery(id+"F3.wireOp",EDGE,"E127"),sQuery(id+"F3.wireOp",EDGE,"E128"),sQuery(id+"F3.wireOp",EDGE,"E129"),sQuery(id+"F3.wireOp",EDGE,"E130"),sQuery(id+"F3.wireOp",EDGE,"E131"),sQuery(id+"F3.wireOp",EDGE,"E132"),sQuery(id+"F3.wireOp",EDGE,"E133"),sQuery(id+"F3.wireOp",EDGE,"E134"),sQuery(id+"F3.wireOp",EDGE,"E135"),sQuery(id+"F3.wireOp",EDGE,"E136"),sQuery(id+"F3.wireOp",EDGE,"E137"),sQuery(id+"F3.wireOp",EDGE,"E138"),sQuery(id+"F3.wireOp",EDGE,"E139"),sQuery(id+"F3.wireOp",EDGE,"E140"),sQuery(id+"F3.wireOp",EDGE,"E141"),sQuery(id+"F3.wireOp",EDGE,"E142"),sQuery(id+"F3.wireOp",EDGE,"E143"),sQuery(id+"F3.wireOp",EDGE,"E144"),sQuery(id+"F3.wireOp",EDGE,"E145"),sQuery(id+"F3.wireOp",EDGE,"E146"),sQuery(id+"F3.wireOp",EDGE,"E147"),sQuery(id+"F3.wireOp",EDGE,"E148"),sQuery(id+"F3.wireOp",EDGE,"E149"),sQuery(id+"F3.wireOp",EDGE,"E150"),sQuery(id+"F3.wireOp",EDGE,"E151"),sQuery(id+"F3.wireOp",EDGE,"E152"),sQuery(id+"F3.wireOp",EDGE,"E153"),sQuery(id+"F3.wireOp",EDGE,"E154"),sQuery(id+"F3.wireOp",EDGE,"E155"),sQuery(id+"F3.wireOp",EDGE,"E156"),sQuery(id+"F3.wireOp",EDGE,"E157"),sQuery(id+"F3.wireOp",EDGE,"E158"),sQuery(id+"F3.wireOp",EDGE,"E159"),sQuery(id+"F3.wireOp",EDGE,"E160"),sQuery(id+"F3.wireOp",EDGE,"E161"),sQuery(id+"F3.wireOp",EDGE,"E162"),sQuery(id+"F3.wireOp",EDGE,"E163"),sQuery(id+"F3.wireOp",EDGE,"E164"),sQuery(id+"F3.wireOp",EDGE,"E165"),sQuery(id+"F3.wireOp",EDGE,"E166"),sQuery(id+"F3.wireOp",EDGE,"E167"),sQuery(id+"F3.wireOp",EDGE,"E168"),sQuery(id+"F3.wireOp",EDGE,"E169"),sQuery(id+"F3.wireOp",EDGE,"E170"),sQuery(id+"F3.wireOp",EDGE,"E171"),sQuery(id+"F3.wireOp",EDGE,"E172"),sQuery(id+"F3.wireOp",EDGE,"E173"),sQuery(id+"F3.wireOp",EDGE,"E174"),sQuery(id+"F3.wireOp",EDGE,"E175"),sQuery(id+"F3.wireOp",EDGE,"E176"),sQuery(id+"F3.wireOp",EDGE,"E177"),sQuery(id+"F3.wireOp",EDGE,"E178"),sQuery(id+"F3.wireOp",EDGE,"E179"),sQuery(id+"F3.wireOp",EDGE,"E180"),sQuery(id+"F3.wireOp",EDGE,"E181"),sQuery(id+"F3.wireOp",EDGE,"E182"),sQuery(id+"F3.wireOp",EDGE,"E183"),sQuery(id+"F3.wireOp",EDGE,"E184"),sQuery(id+"F3.wireOp",EDGE,"E185"),sQuery(id+"F3.wireOp",EDGE,"E186"),sQuery(id+"F3.wireOp",EDGE,"E187"),sQuery(id+"F3.wireOp",EDGE,"E188"),sQuery(id+"F3.wireOp",EDGE,"E189"),sQuery(id+"F3.wireOp",EDGE,"E190"),sQuery(id+"F3.wireOp",EDGE,"E191"),sQuery(id+"F3.wireOp",EDGE,"E192"),sQuery(id+"F3.wireOp",EDGE,"E193"),sQuery(id+"F3.wireOp",EDGE,"E194"),sQuery(id+"F3.wireOp",EDGE,"E195"),sQuery(id+"F3.wireOp",EDGE,"E196"),sQuery(id+"F3.wireOp",EDGE,"E197"),sQuery(id+"F3.wireOp",EDGE,"E198"),sQuery(id+"F3.wireOp",EDGE,"E199"),sQuery(id+"F3.wireOp",EDGE,"E200"),sQuery(id+"F3.wireOp",EDGE,"E201"),sQuery(id+"F3.wireOp",EDGE,"E202"),sQuery(id+"F3.wireOp",EDGE,"E203"),sQuery(id+"F3.wireOp",EDGE,"E204"),sQuery(id+"F3.wireOp",EDGE,"E205"),sQuery(id+"F3.wireOp",EDGE,"E206"),sQuery(id+"F3.wireOp",EDGE,"E207"),sQuery(id+"F3.wireOp",EDGE,"E208"),sQuery(id+"F3.wireOp",EDGE,"E209"),sQuery(id+"F3.wireOp",EDGE,"E210"),sQuery(id+"F3.wireOp",EDGE,"E211"),sQuery(id+"F3.wireOp",EDGE,"E212"),sQuery(id+"F3.wireOp",EDGE,"E213"),sQuery(id+"F3.wireOp",EDGE,"E214"),sQuery(id+"F3.wireOp",EDGE,"E215"),sQuery(id+"F3.wireOp",EDGE,"E216"),sQuery(id+"F3.wireOp",EDGE,"E217"),sQuery(id+"F3.wireOp",EDGE,"E218"),sQuery(id+"F3.wireOp",EDGE,"E219"),sQuery(id+"F3.wireOp",EDGE,"E220"),sQuery(id+"F3.wireOp",EDGE,"E221"),sQuery(id+"F3.wireOp",EDGE,"E222"),sQuery(id+"F3.wireOp",EDGE,"E223"),sQuery(id+"F3.wireOp",EDGE,"E224"),sQuery(id+"F3.wireOp",EDGE,"E225"),sQuery(id+"F3.wireOp",EDGE,"E226"),sQuery(id+"F3.wireOp",EDGE,"E227"),sQuery(id+"F3.wireOp",EDGE,"E228"),sQuery(id+"F3.wireOp",EDGE,"E229"),sQuery(id+"F3.wireOp",EDGE,"E230"),sQuery(id+"F3.wireOp",EDGE,"E231"),sQuery(id+"F3.wireOp",EDGE,"E232"),sQuery(id+"F3.wireOp",EDGE,"E233"),sQuery(id+"F3.wireOp",EDGE,"E234"),sQuery(id+"F3.wireOp",EDGE,"E235"),sQuery(id+"F3.wireOp",EDGE,"E236"),sQuery(id+"F3.wireOp",EDGE,"E237"),sQuery(id+"F3.wireOp",EDGE,"E238"),sQuery(id+"F3.wireOp",EDGE,"E239"),sQuery(id+"F3.wireOp",EDGE,"E240"),sQuery(id+"F3.wireOp",EDGE,"E241"),sQuery(id+"F3.wireOp",EDGE,"E242"),sQuery(id+"F3.wireOp",EDGE,"E243"),sQuery(id+"F3.wireOp",EDGE,"E244"),sQuery(id+"F3.wireOp",EDGE,"E245"),sQuery(id+"F3.wireOp",EDGE,"E246"),sQuery(id+"F3.wireOp",EDGE,"E247"),sQuery(id+"F3.wireOp",EDGE,"E248"),sQuery(id+"F3.wireOp",EDGE,"E249"),sQuery(id+"F3.wireOp",EDGE,"E250"),sQuery(id+"F3.wireOp",EDGE,"E251"),sQuery(id+"F3.wireOp",EDGE,"E252"),sQuery(id+"F3.wireOp",EDGE,"E253"),sQuery(id+"F3.wireOp",EDGE,"E254"),sQuery(id+"F3.wireOp",EDGE,"E255"),sQuery(id+"F3.wireOp",EDGE,"E256"),sQuery(id+"F3.wireOp",EDGE,"E257"),sQuery(id+"F3.wireOp",EDGE,"E258"),sQuery(id+"F3.wireOp",EDGE,"E259"),sQuery(id+"F3.wireOp",EDGE,"E260"),sQuery(id+"F3.wireOp",EDGE,"E261"),sQuery(id+"F3.wireOp",EDGE,"E262"),sQuery(id+"F3.wireOp",EDGE,"E263"),sQuery(id+"F3.wireOp",EDGE,"E264"),sQuery(id+"F3.wireOp",EDGE,"E265"),sQuery(id+"F3.wireOp",EDGE,"E266"),sQuery(id+"F3.wireOp",EDGE,"E267"),sQuery(id+"F3.wireOp",EDGE,"E268"),sQuery(id+"F3.wireOp",EDGE,"E269"),sQuery(id+"F3.wireOp",EDGE,"E270"),sQuery(id+"F3.wireOp",EDGE,"E271"),sQuery(id+"F3.wireOp",EDGE,"E272"),sQuery(id+"F3.wireOp",EDGE,"E273"),sQuery(id+"F3.wireOp",EDGE,"E274"),sQuery(id+"F3.wireOp",EDGE,"E275"),sQuery(id+"F3.wireOp",EDGE,"E276"),sQuery(id+"F3.wireOp",EDGE,"E277"),sQuery(id+"F3.wireOp",EDGE,"E278"),sQuery(id+"F3.wireOp",EDGE,"E279"),sQuery(id+"F3.wireOp",EDGE,"E280"),sQuery(id+"F3.wireOp",EDGE,"E281"),sQuery(id+"F3.wireOp",EDGE,"E282"),sQuery(id+"F3.wireOp",EDGE,"E283"),sQuery(id+"F3.wireOp",EDGE,"E284"),sQuery(id+"F3.wireOp",EDGE,"E285"),sQuery(id+"F3.wireOp",EDGE,"E286"),sQuery(id+"F3.wireOp",EDGE,"E287"),sQuery(id+"F3.wireOp",EDGE,"E288"),sQuery(id+"F3.wireOp",EDGE,"E289"),sQuery(id+"F3.wireOp",EDGE,"E290"),sQuery(id+"F3.wireOp",EDGE,"E291"),sQuery(id+"F3.wireOp",EDGE,"E292"),sQuery(id+"F3.wireOp",EDGE,"E293"),sQuery(id+"F3.wireOp",EDGE,"E294"),sQuery(id+"F3.wireOp",EDGE,"E295"),sQuery(id+"F3.wireOp",EDGE,"E296"),sQuery(id+"F3.wireOp",EDGE,"E297"),sQuery(id+"F3.wireOp",EDGE,"E298"),sQuery(id+"F3.wireOp",EDGE,"E299"),sQuery(id+"F3.wireOp",EDGE,"E300"),sQuery(id+"F3.wireOp",EDGE,"E301"),sQuery(id+"F3.wireOp",EDGE,"E302"),sQuery(id+"F3.wireOp",EDGE,"E303"),sQuery(id+"F3.wireOp",EDGE,"E304"),sQuery(id+"F3.wireOp",EDGE,"E305"),sQuery(id+"F3.wireOp",EDGE,"E306"),sQuery(id+"F3.wireOp",EDGE,"E307"),sQuery(id+"F3.wireOp",EDGE,"E308"),sQuery(id+"F3.wireOp",EDGE,"E309"),sQuery(id+"F3.wireOp",EDGE,"E310"),sQuery(id+"F3.wireOp",EDGE,"E311"),sQuery(id+"F3.wireOp",EDGE,"E312"),sQuery(id+"F3.wireOp",EDGE,"E313"),sQuery(id+"F3.wireOp",EDGE,"E314"),sQuery(id+"F3.wireOp",EDGE,"E315"),sQuery(id+"F3.wireOp",EDGE,"E316"),sQuery(id+"F3.wireOp",EDGE,"E317"),sQuery(id+"F3.wireOp",EDGE,"E318"),sQuery(id+"F3.wireOp",EDGE,"E319"),sQuery(id+"F3.wireOp",EDGE,"E320"),sQuery(id+"F3.wireOp",EDGE,"E321"),sQuery(id+"F3.wireOp",EDGE,"E322"),sQuery(id+"F3.wireOp",EDGE,"E323"),sQuery(id+"F3.wireOp",EDGE,"E324"),sQuery(id+"F3.wireOp",EDGE,"E325"),sQuery(id+"F3.wireOp",EDGE,"E326"),sQuery(id+"F3.wireOp",EDGE,"E327"),sQuery(id+"F3.wireOp",EDGE,"E328"),sQuery(id+"F3.wireOp",EDGE,"E329"),sQuery(id+"F3.wireOp",EDGE,"E330"),sQuery(id+"F3.wireOp",EDGE,"E331"),sQuery(id+"F3.wireOp",EDGE,"E332"),sQuery(id+"F3.wireOp",EDGE,"E333"),sQuery(id+"F3.wireOp",EDGE,"E334"),sQuery(id+"F3.wireOp",EDGE,"E335"),sQuery(id+"F3.wireOp",EDGE,"E336"),sQuery(id+"F3.wireOp",EDGE,"E337"),sQuery(id+"F3.wireOp",EDGE,"E338"),sQuery(id+"F3.wireOp",EDGE,"E339"),sQuery(id+"F3.wireOp",EDGE,"E340"),sQuery(id+"F3.wireOp",EDGE,"E341"),sQuery(id+"F3.wireOp",EDGE,"E342"),sQuery(id+"F3.wireOp",EDGE,"E343"),sQuery(id+"F3.wireOp",EDGE,"E344"),sQuery(id+"F3.wireOp",EDGE,"E345"),sQuery(id+"F3.wireOp",EDGE,"E346"),sQuery(id+"F3.wireOp",EDGE,"E347"),sQuery(id+"F3.wireOp",EDGE,"E348"),sQuery(id+"F3.wireOp",EDGE,"E349"),sQuery(id+"F3.wireOp",EDGE,"E350"),sQuery(id+"F3.wireOp",EDGE,"E351"),sQuery(id+"F3.wireOp",EDGE,"E352"),sQuery(id+"F3.wireOp",EDGE,"E353"),sQuery(id+"F3.wireOp",EDGE,"E354"),sQuery(id+"F3.wireOp",EDGE,"E355"),sQuery(id+"F3.wireOp",EDGE,"E356"),sQuery(id+"F3.wireOp",EDGE,"E357"),sQuery(id+"F3.wireOp",EDGE,"E358"),sQuery(id+"F3.wireOp",EDGE,"E359"),sQuery(id+"F3.wireOp",EDGE,"E360"),sQuery(id+"F3.wireOp",EDGE,"E361"),sQuery(id+"F3.wireOp",EDGE,"E362"),sQuery(id+"F3.wireOp",EDGE,"E363"),sQuery(id+"F3.wireOp",EDGE,"E364"),sQuery(id+"F3.wireOp",EDGE,"E365"),sQuery(id+"F3.wireOp",EDGE,"E366"),sQuery(id+"F3.wireOp",EDGE,"E367"),sQuery(id+"F3.wireOp",EDGE,"E368"),sQuery(id+"F3.wireOp",EDGE,"E369"),sQuery(id+"F3.wireOp",EDGE,"E370"),sQuery(id+"F3.wireOp",EDGE,"E371"),sQuery(id+"F3.wireOp",EDGE,"E372"),sQuery(id+"F3.wireOp",EDGE,"E373"),sQuery(id+"F3.wireOp",EDGE,"E374"),sQuery(id+"F3.wireOp",EDGE,"E375"),sQuery(id+"F3.wireOp",EDGE,"E376"),sQuery(id+"F3.wireOp",EDGE,"E377"),sQuery(id+"F3.wireOp",EDGE,"E378"),sQuery(id+"F3.wireOp",EDGE,"E379"),sQuery(id+"F3.wireOp",EDGE,"E380"),sQuery(id+"F3.wireOp",EDGE,"E381"),sQuery(id+"F3.wireOp",EDGE,"E382"),sQuery(id+"F3.wireOp",EDGE,"E383"),sQuery(id+"F3.wireOp",EDGE,"E384"),sQuery(id+"F3.wireOp",EDGE,"E385"),sQuery(id+"F3.wireOp",EDGE,"E386"),sQuery(id+"F3.wireOp",EDGE,"E387"),sQuery(id+"F3.wireOp",EDGE,"E388"),sQuery(id+"F3.wireOp",EDGE,"E389"),sQuery(id+"F3.wireOp",EDGE,"E390"),sQuery(id+"F3.wireOp",EDGE,"E391"),sQuery(id+"F3.wireOp",EDGE,"E392"),sQuery(id+"F3.wireOp",EDGE,"E393"),sQuery(id+"F3.wireOp",EDGE,"E394"),sQuery(id+"F3.wireOp",EDGE,"E395"),sQuery(id+"F3.wireOp",EDGE,"E396"),sQuery(id+"F3.wireOp",EDGE,"E397"),sQuery(id+"F3.wireOp",EDGE,"E398"),sQuery(id+"F3.wireOp",EDGE,"E399"),sQuery(id+"F3.wireOp",EDGE,"E400"),sQuery(id+"F3.wireOp",EDGE,"E401"),sQuery(id+"F3.wireOp",EDGE,"E402"),sQuery(id+"F3.wireOp",EDGE,"E403"),sQuery(id+"F3.wireOp",EDGE,"E404"),sQuery(id+"F3.wireOp",EDGE,"E405"),sQuery(id+"F3.wireOp",EDGE,"E406"),sQuery(id+"F3.wireOp",EDGE,"E407"),sQuery(id+"F3.wireOp",EDGE,"E408"),sQuery(id+"F3.wireOp",EDGE,"E409"),sQuery(id+"F3.wireOp",EDGE,"E410"),sQuery(id+"F3.wireOp",EDGE,"E411"),sQuery(id+"F3.wireOp",EDGE,"E412"),sQuery(id+"F3.wireOp",EDGE,"E413"),sQuery(id+"F3.wireOp",EDGE,"E414"),sQuery(id+"F3.wireOp",EDGE,"E415"),sQuery(id+"F3.wireOp",EDGE,"E416"),sQuery(id+"F3.wireOp",EDGE,"E417"),sQuery(id+"F3.wireOp",EDGE,"E418"),sQuery(id+"F3.wireOp",EDGE,"E419"),sQuery(id+"F3.wireOp",EDGE,"E420"),sQuery(id+"F3.wireOp",EDGE,"E421"),sQuery(id+"F3.wireOp",EDGE,"E422"),sQuery(id+"F3.wireOp",EDGE,"E423"),sQuery(id+"F3.wireOp",EDGE,"E424"),sQuery(id+"F3.wireOp",EDGE,"E425"),sQuery(id+"F3.wireOp",EDGE,"E426"),sQuery(id+"F3.wireOp",EDGE,"E427"),sQuery(id+"F3.wireOp",EDGE,"E428"),sQuery(id+"F3.wireOp",EDGE,"E429"),sQuery(id+"F3.wireOp",EDGE,"E430"),sQuery(id+"F3.wireOp",EDGE,"E431"),sQuery(id+"F3.wireOp",EDGE,"E432"),sQuery(id+"F3.wireOp",EDGE,"E433"),sQuery(id+"F3.wireOp",EDGE,"E434"),sQuery(id+"F3.wireOp",EDGE,"E435"),sQuery(id+"F3.wireOp",EDGE,"E436"),sQuery(id+"F3.wireOp",EDGE,"E437"),sQuery(id+"F3.wireOp",EDGE,"E438"),sQuery(id+"F3.wireOp",EDGE,"E439"),sQuery(id+"F3.wireOp",EDGE,"E440"),sQuery(id+"F3.wireOp",EDGE,"E441"),sQuery(id+"F3.wireOp",EDGE,"E442"),sQuery(id+"F3.wireOp",EDGE,"E443"),sQuery(id+"F3.wireOp",EDGE,"E444"),sQuery(id+"F3.wireOp",EDGE,"E445"),sQuery(id+"F3.wireOp",EDGE,"E446"),sQuery(id+"F3.wireOp",EDGE,"E447"),sQuery(id+"F3.wireOp",EDGE,"E448"),sQuery(id+"F3.wireOp",EDGE,"E449"),sQuery(id+"F3.wireOp",EDGE,"E450"),sQuery(id+"F3.wireOp",EDGE,"E451"),sQuery(id+"F3.wireOp",EDGE,"E452"),sQuery(id+"F3.wireOp",EDGE,"E453"),sQuery(id+"F3.wireOp",EDGE,"E454"),sQuery(id+"F3.wireOp",EDGE,"E455"),sQuery(id+"F3.wireOp",EDGE,"E456"),sQuery(id+"F3.wireOp",EDGE,"E457"),sQuery(id+"F3.wireOp",EDGE,"E458"),sQuery(id+"F3.wireOp",EDGE,"E459"),sQuery(id+"F3.wireOp",EDGE,"E460"),sQuery(id+"F3.wireOp",EDGE,"E461"),sQuery(id+"F3.wireOp",EDGE,"E462"),sQuery(id+"F3.wireOp",EDGE,"E463"),sQuery(id+"F3.wireOp",EDGE,"E464"),sQuery(id+"F3.wireOp",EDGE,"E465"),sQuery(id+"F3.wireOp",EDGE,"E466"),sQuery(id+"F3.wireOp",EDGE,"E467"),sQuery(id+"F3.wireOp",EDGE,"E468"),sQuery(id+"F3.wireOp",EDGE,"E469"),sQuery(id+"F3.wireOp",EDGE,"E470"),sQuery(id+"F3.wireOp",EDGE,"E471"),sQuery(id+"F3.wireOp",EDGE,"E472"),sQuery(id+"F3.wireOp",EDGE,"E473"),sQuery(id+"F3.wireOp",EDGE,"E474"),sQuery(id+"F3.wireOp",EDGE,"E475"),sQuery(id+"F3.wireOp",EDGE,"E476"),sQuery(id+"F3.wireOp",EDGE,"E477"),sQuery(id+"F3.wireOp",EDGE,"E478"),sQuery(id+"F3.wireOp",EDGE,"E479"),sQuery(id+"F3.wireOp",EDGE,"E480"),sQuery(id+"F3.wireOp",EDGE,"E481"),sQuery(id+"F3.wireOp",EDGE,"E482"),sQuery(id+"F3.wireOp",EDGE,"E483"),sQuery(id+"F3.wireOp",EDGE,"E484"),sQuery(id+"F3.wireOp",EDGE,"E485"),sQuery(id+"F3.wireOp",EDGE,"E486"),sQuery(id+"F3.wireOp",EDGE,"E487"),sQuery(id+"F3.wireOp",EDGE,"E488"),sQuery(id+"F3.wireOp",EDGE,"E489"),sQuery(id+"F3.wireOp",EDGE,"E490"),sQuery(id+"F3.wireOp",EDGE,"E491"),sQuery(id+"F3.wireOp",EDGE,"E492"),sQuery(id+"F3.wireOp",EDGE,"E493"),sQuery(id+"F3.wireOp",EDGE,"E494"),sQuery(id+"F3.wireOp",EDGE,"E495"),sQuery(id+"F3.wireOp",EDGE,"E496"),sQuery(id+"F3.wireOp",EDGE,"E497"),sQuery(id+"F3.wireOp",EDGE,"E498"),sQuery(id+"F3.wireOp",EDGE,"E499"),sQuery(id+"F3.wireOp",EDGE,"E500"),sQuery(id+"F3.wireOp",EDGE,"E501"),sQuery(id+"F3.wireOp",EDGE,"E502"),sQuery(id+"F3.wireOp",EDGE,"E503"),sQuery(id+"F3.wireOp",EDGE,"E504"),sQuery(id+"F3.wireOp",EDGE,"E505"),sQuery(id+"F3.wireOp",EDGE,"E506"),sQuery(id+"F3.wireOp",EDGE,"E507"),sQuery(id+"F3.wireOp",EDGE,"E508"),sQuery(id+"F3.wireOp",EDGE,"E509"),sQuery(id+"F3.wireOp",EDGE,"E510"),sQuery(id+"F3.wireOp",EDGE,"E511"),sQuery(id+"F3.wireOp",EDGE,"E512"),sQuery(id+"F3.wireOp",EDGE,"E513"),sQuery(id+"F3.wireOp",EDGE,"E514"),sQuery(id+"F3.wireOp",EDGE,"E515"),sQuery(id+"F3.wireOp",EDGE,"E516"),sQuery(id+"F3.wireOp",EDGE,"E517"),sQuery(id+"F3.wireOp",EDGE,"E518"),sQuery(id+"F3.wireOp",EDGE,"E519"),sQuery(id+"F3.wireOp",EDGE,"E520"),sQuery(id+"F3.wireOp",EDGE,"E521"),sQuery(id+"F3.wireOp",EDGE,"E522"),sQuery(id+"F3.wireOp",EDGE,"E523"),sQuery(id+"F3.wireOp",EDGE,"E524"),sQuery(id+"F3.wireOp",EDGE,"E525"),sQuery(id+"F3.wireOp",EDGE,"E526"),sQuery(id+"F3.wireOp",EDGE,"E527"),sQuery(id+"F3.wireOp",EDGE,"E528"),sQuery(id+"F3.wireOp",EDGE,"E529"),sQuery(id+"F3.wireOp",EDGE,"E530"),sQuery(id+"F3.wireOp",EDGE,"E531"),sQuery(id+"F3.wireOp",EDGE,"E532"),sQuery(id+"F3.wireOp",EDGE,"E533"),sQuery(id+"F3.wireOp",EDGE,"E534"),sQuery(id+"F3.wireOp",EDGE,"E535"),sQuery(id+"F3.wireOp",EDGE,"E536"),sQuery(id+"F3.wireOp",EDGE,"E537"),sQuery(id+"F3.wireOp",EDGE,"E538"),sQuery(id+"F3.wireOp",EDGE,"E539"),sQuery(id+"F3.wireOp",EDGE,"E540"),sQuery(id+"F3.wireOp",EDGE,"E541"),sQuery(id+"F3.wireOp",EDGE,"E542"),sQuery(id+"F3.wireOp",EDGE,"E543"),sQuery(id+"F3.wireOp",EDGE,"E544"),sQuery(id+"F3.wireOp",EDGE,"E545"),sQuery(id+"F3.wireOp",EDGE,"E546"),sQuery(id+"F3.wireOp",EDGE,"E547"),sQuery(id+"F3.wireOp",EDGE,"E548"),sQuery(id+"F3.wireOp",EDGE,"E549"),sQuery(id+"F3.wireOp",EDGE,"E550"),sQuery(id+"F3.wireOp",EDGE,"E551"),sQuery(id+"F3.wireOp",EDGE,"E552"),sQuery(id+"F3.wireOp",EDGE,"E553"),sQuery(id+"F3.wireOp",EDGE,"E554"),sQuery(id+"F3.wireOp",EDGE,"E555"),sQuery(id+"F3.wireOp",EDGE,"E556"),sQuery(id+"F3.wireOp",EDGE,"E557"),sQuery(id+"F3.wireOp",EDGE,"E558"),sQuery(id+"F3.wireOp",EDGE,"E559"),sQuery(id+"F3.wireOp",EDGE,"E560"),sQuery(id+"F3.wireOp",EDGE,"E561"),sQuery(id+"F3.wireOp",EDGE,"E562"),sQuery(id+"F3.wireOp",EDGE,"E563"),sQuery(id+"F3.wireOp",EDGE,"E564"),sQuery(id+"F3.wireOp",EDGE,"E565"),sQuery(id+"F3.wireOp",EDGE,"E566"),sQuery(id+"F3.wireOp",EDGE,"E567"),sQuery(id+"F3.wireOp",EDGE,"E568"),sQuery(id+"F3.wireOp",EDGE,"E569"),sQuery(id+"F3.wireOp",EDGE,"E570"),sQuery(id+"F3.wireOp",EDGE,"E571"),sQuery(id+"F3.wireOp",EDGE,"E572"),sQuery(id+"F3.wireOp",EDGE,"E573"),sQuery(id+"F3.wireOp",EDGE,"E574"),sQuery(id+"F3.wireOp",EDGE,"E575"),sQuery(id+"F3.wireOp",EDGE,"E576"),sQuery(id+"F3.wireOp",EDGE,"E577"),sQuery(id+"F3.wireOp",EDGE,"E578"),sQuery(id+"F3.wireOp",EDGE,"E579"),sQuery(id+"F3.wireOp",EDGE,"E580"),sQuery(id+"F3.wireOp",EDGE,"E581"),sQuery(id+"F3.wireOp",EDGE,"E582"),sQuery(id+"F3.wireOp",EDGE,"E583"),sQuery(id+"F3.wireOp",EDGE,"E584"),sQuery(id+"F3.wireOp",EDGE,"E585"),sQuery(id+"F3.wireOp",EDGE,"E586"),sQuery(id+"F3.wireOp",EDGE,"E587"),sQuery(id+"F3.wireOp",EDGE,"E588"),sQuery(id+"F3.wireOp",EDGE,"E589"),sQuery(id+"F3.wireOp",EDGE,"E590"),sQuery(id+"F3.wireOp",EDGE,"E591"),sQuery(id+"F3.wireOp",EDGE,"E592"),sQuery(id+"F3.wireOp",EDGE,"E593"),sQuery(id+"F3.wireOp",EDGE,"E594"),sQuery(id+"F3.wireOp",EDGE,"E595"),sQuery(id+"F3.wireOp",EDGE,"E596"),sQuery(id+"F3.wireOp",EDGE,"E597"),sQuery(id+"F3.wireOp",EDGE,"E598"),sQuery(id+"F3.wireOp",EDGE,"E599"),sQuery(id+"F3.wireOp",EDGE,"E600"),sQuery(id+"F3.wireOp",EDGE,"E601"),sQuery(id+"F3.wireOp",EDGE,"E602"),sQuery(id+"F3.wireOp",EDGE,"E603"),sQuery(id+"F3.wireOp",EDGE,"E604"),sQuery(id+"F3.wireOp",EDGE,"E605"),sQuery(id+"F3.wireOp",EDGE,"E606"),sQuery(id+"F3.wireOp",EDGE,"E607"),sQuery(id+"F3.wireOp",EDGE,"E608"),sQuery(id+"F3.wireOp",EDGE,"E609"),sQuery(id+"F3.wireOp",EDGE,"E610"),sQuery(id+"F3.wireOp",EDGE,"E611"),sQuery(id+"F3.wireOp",EDGE,"E612"),sQuery(id+"F3.wireOp",EDGE,"E613"),sQuery(id+"F3.wireOp",EDGE,"E614"),sQuery(id+"F3.wireOp",EDGE,"E615"),sQuery(id+"F3.wireOp",EDGE,"E616"),sQuery(id+"F3.wireOp",EDGE,"E617"),sQuery(id+"F3.wireOp",EDGE,"E618"),sQuery(id+"F3.wireOp",EDGE,"E619"),sQuery(id+"F3.wireOp",EDGE,"E620"),sQuery(id+"F3.wireOp",EDGE,"E621"),sQuery(id+"F3.wireOp",EDGE,"E622"),sQuery(id+"F3.wireOp",EDGE,"E623"),sQuery(id+"F3.wireOp",EDGE,"E624"),sQuery(id+"F3.wireOp",EDGE,"E625"),sQuery(id+"F3.wireOp",EDGE,"E626"),sQuery(id+"F3.wireOp",EDGE,"E627"),sQuery(id+"F3.wireOp",EDGE,"E628"),sQuery(id+"F3.wireOp",EDGE,"E629"),sQuery(id+"F3.wireOp",EDGE,"E630"),sQuery(id+"F3.wireOp",EDGE,"E631"),sQuery(id+"F3.wireOp",EDGE,"E632"),sQuery(id+"F3.wireOp",EDGE,"E633"),sQuery(id+"F3.wireOp",EDGE,"E634"),sQuery(id+"F3.wireOp",EDGE,"E635"),sQuery(id+"F3.wireOp",EDGE,"E636"),sQuery(id+"F3.wireOp",EDGE,"E637"),sQuery(id+"F3.wireOp",EDGE,"E638"),sQuery(id+"F3.wireOp",EDGE,"E639"),sQuery(id+"F3.wireOp",EDGE,"E640"),sQuery(id+"F3.wireOp",EDGE,"E641"),sQuery(id+"F3.wireOp",EDGE,"E642"),sQuery(id+"F3.wireOp",EDGE,"E643"),sQuery(id+"F3.wireOp",EDGE,"E644"),sQuery(id+"F3.wireOp",EDGE,"E645"),sQuery(id+"F3.wireOp",EDGE,"E646"),sQuery(id+"F3.wireOp",EDGE,"E647"),sQuery(id+"F3.wireOp",EDGE,"E648"),sQuery(id+"F3.wireOp",EDGE,"E649"),sQuery(id+"F3.wireOp",EDGE,"E650"),sQuery(id+"F3.wireOp",EDGE,"E651"),sQuery(id+"F3.wireOp",EDGE,"E652"),sQuery(id+"F3.wireOp",EDGE,"E653"),sQuery(id+"F3.wireOp",EDGE,"E654"),sQuery(id+"F3.wireOp",EDGE,"E655"),sQuery(id+"F3.wireOp",EDGE,"E656"),sQuery(id+"F3.wireOp",EDGE,"E657"),sQuery(id+"F3.wireOp",EDGE,"E658"),sQuery(id+"F3.wireOp",EDGE,"E659"),sQuery(id+"F3.wireOp",EDGE,"E660"),sQuery(id+"F3.wireOp",EDGE,"E661"),sQuery(id+"F3.wireOp",EDGE,"E662"),sQuery(id+"F3.wireOp",EDGE,"E663"),sQuery(id+"F3.wireOp",EDGE,"E664"),sQuery(id+"F3.wireOp",EDGE,"E665"),sQuery(id+"F3.wireOp",EDGE,"E666"),sQuery(id+"F3.wireOp",EDGE,"E667"),sQuery(id+"F3.wireOp",EDGE,"E668"),sQuery(id+"F3.wireOp",EDGE,"E669"),sQuery(id+"F3.wireOp",EDGE,"E670"),sQuery(id+"F3.wireOp",EDGE,"E671"),sQuery(id+"F3.wireOp",EDGE,"E672"),sQuery(id+"F3.wireOp",EDGE,"E673"),sQuery(id+"F3.wireOp",EDGE,"E674"),sQuery(id+"F3.wireOp",EDGE,"E675"),sQuery(id+"F3.wireOp",EDGE,"E676"),sQuery(id+"F3.wireOp",EDGE,"E677"),sQuery(id+"F3.wireOp",EDGE,"E678"),sQuery(id+"F3.wireOp",EDGE,"E679"),sQuery(id+"F3.wireOp",EDGE,"E680"),sQuery(id+"F3.wireOp",EDGE,"E681"),sQuery(id+"F3.wireOp",EDGE,"E682"),sQuery(id+"F3.wireOp",EDGE,"E683"),sQuery(id+"F3.wireOp",EDGE,"E684"),sQuery(id+"F3.wireOp",EDGE,"E685"),sQuery(id+"F3.wireOp",EDGE,"E686"),sQuery(id+"F3.wireOp",EDGE,"E687"),sQuery(id+"F3.wireOp",EDGE,"E688"),sQuery(id+"F3.wireOp",EDGE,"E689"),sQuery(id+"F3.wireOp",EDGE,"E690"),sQuery(id+"F3.wireOp",EDGE,"E691"),sQuery(id+"F3.wireOp",EDGE,"E692"),sQuery(id+"F3.wireOp",EDGE,"E693"),sQuery(id+"F3.wireOp",EDGE,"E694"),sQuery(id+"F3.wireOp",EDGE,"E695"),sQuery(id+"F3.wireOp",EDGE,"E696"),sQuery(id+"F3.wireOp",EDGE,"E697"),sQuery(id+"F3.wireOp",EDGE,"E698"),sQuery(id+"F3.wireOp",EDGE,"E699"),sQuery(id+"F3.wireOp",EDGE,"E700"),sQuery(id+"F3.wireOp",EDGE,"E701"),sQuery(id+"F3.wireOp",EDGE,"E702"),sQuery(id+"F3.wireOp",EDGE,"E703"),sQuery(id+"F3.wireOp",EDGE,"E704"),sQuery(id+"F3.wireOp",EDGE,"E705"),sQuery(id+"F3.wireOp",EDGE,"E706"),sQuery(id+"F3.wireOp",EDGE,"E707"),sQuery(id+"F3.wireOp",EDGE,"E708"),sQuery(id+"F3.wireOp",EDGE,"E709"),sQuery(id+"F3.wireOp",EDGE,"E710"),sQuery(id+"F3.wireOp",EDGE,"E711"),sQuery(id+"F3.wireOp",EDGE,"E712"),sQuery(id+"F3.wireOp",EDGE,"E713"),sQuery(id+"F3.wireOp",EDGE,"E714"),sQuery(id+"F3.wireOp",EDGE,"E715"),sQuery(id+"F3.wireOp",EDGE,"E716"),sQuery(id+"F3.wireOp",EDGE,"E717"),sQuery(id+"F3.wireOp",EDGE,"E718"),sQuery(id+"F3.wireOp",EDGE,"E719"),sQuery(id+"F3.wireOp",EDGE,"E720"),sQuery(id+"F3.wireOp",EDGE,"E721"),sQuery(id+"F3.wireOp",EDGE,"E722"),sQuery(id+"F3.wireOp",EDGE,"E723"),sQuery(id+"F3.wireOp",EDGE,"E724"),sQuery(id+"F3.wireOp",EDGE,"E725"),sQuery(id+"F3.wireOp",EDGE,"E726"),sQuery(id+"F3.wireOp",EDGE,"E727"),sQuery(id+"F3.wireOp",EDGE,"E728"),sQuery(id+"F3.wireOp",EDGE,"E729"),sQuery(id+"F3.wireOp",EDGE,"E730"),sQuery(id+"F3.wireOp",EDGE,"E731"),sQuery(id+"F3.wireOp",EDGE,"E732"),sQuery(id+"F3.wireOp",EDGE,"E733"),sQuery(id+"F3.wireOp",EDGE,"E734"),sQuery(id+"F3.wireOp",EDGE,"E735"),sQuery(id+"F3.wireOp",EDGE,"E736"),sQuery(id+"F3.wireOp",EDGE,"E737"),sQuery(id+"F3.wireOp",EDGE,"E738"),sQuery(id+"F3.wireOp",EDGE,"E739"),sQuery(id+"F3.wireOp",EDGE,"E740"),sQuery(id+"F3.wireOp",EDGE,"E741"),sQuery(id+"F3.wireOp",EDGE,"E742"),sQuery(id+"F3.wireOp",EDGE,"E743"),sQuery(id+"F3.wireOp",EDGE,"E744"),sQuery(id+"F3.wireOp",EDGE,"E745"),sQuery(id+"F3.wireOp",EDGE,"E746"),sQuery(id+"F3.wireOp",EDGE,"E747"),sQuery(id+"F3.wireOp",EDGE,"E748"),sQuery(id+"F3.wireOp",EDGE,"E749"),sQuery(id+"F3.wireOp",EDGE,"E750"),sQuery(id+"F3.wireOp",EDGE,"E751"),sQuery(id+"F3.wireOp",EDGE,"E752"),sQuery(id+"F3.wireOp",EDGE,"E753"),sQuery(id+"F3.wireOp",EDGE,"E754"),sQuery(id+"F3.wireOp",EDGE,"E755"),sQuery(id+"F3.wireOp",EDGE,"E756"),sQuery(id+"F3.wireOp",EDGE,"E757"),sQuery(id+"F3.wireOp",EDGE,"E758"),sQuery(id+"F3.wireOp",EDGE,"E759"),sQuery(id+"F3.wireOp",EDGE,"E760"),sQuery(id+"F3.wireOp",EDGE,"E761"),sQuery(id+"F3.wireOp",EDGE,"E762"),sQuery(id+"F3.wireOp",EDGE,"E763"),sQuery(id+"F3.wireOp",EDGE,"E764"),sQuery(id+"F3.wireOp",EDGE,"E765"),sQuery(id+"F3.wireOp",EDGE,"E766"),sQuery(id+"F3.wireOp",EDGE,"E767"),sQuery(id+"F3.wireOp",EDGE,"E768"),sQuery(id+"F3.wireOp",EDGE,"E769"),sQuery(id+"F3.wireOp",EDGE,"E770"),sQuery(id+"F3.wireOp",EDGE,"E771"),sQuery(id+"F3.wireOp",EDGE,"E772"),sQuery(id+"F3.wireOp",EDGE,"E773"),sQuery(id+"F3.wireOp",EDGE,"E774"),sQuery(id+"F3.wireOp",EDGE,"E775"),sQuery(id+"F3.wireOp",EDGE,"E776"),sQuery(id+"F3.wireOp",EDGE,"E777"),sQuery(id+"F3.wireOp",EDGE,"E778"),sQuery(id+"F3.wireOp",EDGE,"E779"),sQuery(id+"F3.wireOp",EDGE,"E780"),sQuery(id+"F3.wireOp",EDGE,"E781"),sQuery(id+"F3.wireOp",EDGE,"E782"),sQuery(id+"F3.wireOp",EDGE,"E783"),sQuery(id+"F3.wireOp",EDGE,"E784"),sQuery(id+"F3.wireOp",EDGE,"E785"),sQuery(id+"F3.wireOp",EDGE,"E786"),sQuery(id+"F3.wireOp",EDGE,"E787"),sQuery(id+"F3.wireOp",EDGE,"E788"),sQuery(id+"F3.wireOp",EDGE,"E789"),sQuery(id+"F3.wireOp",EDGE,"E790"),sQuery(id+"F3.wireOp",EDGE,"E791"),sQuery(id+"F3.wireOp",EDGE,"E792"),sQuery(id+"F3.wireOp",EDGE,"E793"),sQuery(id+"F3.wireOp",EDGE,"E794"),sQuery(id+"F3.wireOp",EDGE,"E795"),sQuery(id+"F3.wireOp",EDGE,"E796"),sQuery(id+"F3.wireOp",EDGE,"E797"),sQuery(id+"F3.wireOp",EDGE,"E798"),sQuery(id+"F3.wireOp",EDGE,"E799"),sQuery(id+"F3.wireOp",EDGE,"E800"),sQuery(id+"F3.wireOp",EDGE,"E801"),sQuery(id+"F3.wireOp",EDGE,"E802"),sQuery(id+"F3.wireOp",EDGE,"E803"),sQuery(id+"F3.wireOp",EDGE,"E804"),sQuery(id+"F3.wireOp",EDGE,"E805"),sQuery(id+"F3.wireOp",EDGE,"E806"),sQuery(id+"F3.wireOp",EDGE,"E807"),sQuery(id+"F3.wireOp",EDGE,"E808"),sQuery(id+"F3.wireOp",EDGE,"E809"),sQuery(id+"F3.wireOp",EDGE,"E810"),sQuery(id+"F3.wireOp",EDGE,"E811"),sQuery(id+"F3.wireOp",EDGE,"E812"),sQuery(id+"F3.wireOp",EDGE,"E813"),sQuery(id+"F3.wireOp",EDGE,"E814"),sQuery(id+"F3.wireOp",EDGE,"E815"),sQuery(id+"F3.wireOp",EDGE,"E816"),sQuery(id+"F3.wireOp",EDGE,"E817"),sQuery(id+"F3.wireOp",EDGE,"E818"),sQuery(id+"F3.wireOp",EDGE,"E819"),sQuery(id+"F3.wireOp",EDGE,"E820"),sQuery(id+"F3.wireOp",EDGE,"E821"),sQuery(id+"F3.wireOp",EDGE,"E822"),sQuery(id+"F3.wireOp",EDGE,"E823"),sQuery(id+"F3.wireOp",EDGE,"E824"),sQuery(id+"F3.wireOp",EDGE,"E825"),sQuery(id+"F3.wireOp",EDGE,"E826"),sQuery(id+"F3.wireOp",EDGE,"E827"),sQuery(id+"F3.wireOp",EDGE,"E828"),sQuery(id+"F3.wireOp",EDGE,"E829"),sQuery(id+"F3.wireOp",EDGE,"E830"),sQuery(id+"F3.wireOp",EDGE,"E831"),sQuery(id+"F3.wireOp",EDGE,"E832"),sQuery(id+"F3.wireOp",EDGE,"E833"),sQuery(id+"F3.wireOp",EDGE,"E834"),sQuery(id+"F3.wireOp",EDGE,"E835"),sQuery(id+"F3.wireOp",EDGE,"E836"),sQuery(id+"F3.wireOp",EDGE,"E837"),sQuery(id+"F3.wireOp",EDGE,"E838"),sQuery(id+"F3.wireOp",EDGE,"E839"),sQuery(id+"F3.wireOp",EDGE,"E840"),sQuery(id+"F3.wireOp",EDGE,"E841"),sQuery(id+"F3.wireOp",EDGE,"E842"),sQuery(id+"F3.wireOp",EDGE,"E843"),sQuery(id+"F3.wireOp",EDGE,"E844"),sQuery(id+"F3.wireOp",EDGE,"E845"),sQuery(id+"F3.wireOp",EDGE,"E846"),sQuery(id+"F3.wireOp",EDGE,"E847"),sQuery(id+"F3.wireOp",EDGE,"E848"),sQuery(id+"F3.wireOp",EDGE,"E849"),sQuery(id+"F3.wireOp",EDGE,"E850"),sQuery(id+"F3.wireOp",EDGE,"E851"),sQuery(id+"F3.wireOp",EDGE,"E852"),sQuery(id+"F3.wireOp",EDGE,"E853"),sQuery(id+"F3.wireOp",EDGE,"E854"),sQuery(id+"F3.wireOp",EDGE,"E855"),sQuery(id+"F3.wireOp",EDGE,"E856"),sQuery(id+"F3.wireOp",EDGE,"E857"),sQuery(id+"F3.wireOp",EDGE,"E858"),sQuery(id+"F3.wireOp",EDGE,"E859"),sQuery(id+"F3.wireOp",EDGE,"E860"),sQuery(id+"F3.wireOp",EDGE,"E861"),sQuery(id+"F3.wireOp",EDGE,"E862"),sQuery(id+"F3.wireOp",EDGE,"E863"),sQuery(id+"F3.wireOp",EDGE,"E864"),sQuery(id+"F3.wireOp",EDGE,"E865"),sQuery(id+"F3.wireOp",EDGE,"E866"),sQuery(id+"F3.wireOp",EDGE,"E867"),sQuery(id+"F3.wireOp",EDGE,"E868"),sQuery(id+"F3.wireOp",EDGE,"E869"),sQuery(id+"F3.wireOp",EDGE,"E870"),sQuery(id+"F3.wireOp",EDGE,"E871"),sQuery(id+"F3.wireOp",EDGE,"E872"),sQuery(id+"F3.wireOp",EDGE,"E873"),sQuery(id+"F3.wireOp",EDGE,"E874"),sQuery(id+"F3.wireOp",EDGE,"E875"),sQuery(id+"F3.wireOp",EDGE,"E876"),sQuery(id+"F3.wireOp",EDGE,"E877"),sQuery(id+"F3.wireOp",EDGE,"E878"),sQuery(id+"F3.wireOp",EDGE,"E879"),sQuery(id+"F3.wireOp",EDGE,"E880"),sQuery(id+"F3.wireOp",EDGE,"E881"),sQuery(id+"F3.wireOp",EDGE,"E882"),sQuery(id+"F3.wireOp",EDGE,"E883"),sQuery(id+"F3.wireOp",EDGE,"E884"),sQuery(id+"F3.wireOp",EDGE,"E885"),sQuery(id+"F3.wireOp",EDGE,"E886"),sQuery(id+"F3.wireOp",EDGE,"E887"),sQuery(id+"F3.wireOp",EDGE,"E888"),sQuery(id+"F3.wireOp",EDGE,"E889"),sQuery(id+"F3.wireOp",EDGE,"E890"),sQuery(id+"F3.wireOp",EDGE,"E891"),sQuery(id+"F3.wireOp",EDGE,"E892"),sQuery(id+"F3.wireOp",EDGE,"E893"),sQuery(id+"F3.wireOp",EDGE,"E894"),sQuery(id+"F3.wireOp",EDGE,"E895"),sQuery(id+"F3.wireOp",EDGE,"E896"),sQuery(id+"F3.wireOp",EDGE,"E897"),sQuery(id+"F3.wireOp",EDGE,"E898"),sQuery(id+"F3.wireOp",EDGE,"E899"),sQuery(id+"F3.wireOp",EDGE,"E900"),sQuery(id+"F3.wireOp",EDGE,"E901"),sQuery(id+"F3.wireOp",EDGE,"E902"),sQuery(id+"F3.wireOp",EDGE,"E903"),sQuery(id+"F3.wireOp",EDGE,"E904"),sQuery(id+"F3.wireOp",EDGE,"E905"),sQuery(id+"F3.wireOp",EDGE,"E906"),sQuery(id+"F3.wireOp",EDGE,"E907"),sQuery(id+"F3.wireOp",EDGE,"E908"),sQuery(id+"F3.wireOp",EDGE,"E909"),sQuery(id+"F3.wireOp",EDGE,"E910"),sQuery(id+"F3.wireOp",EDGE,"E911"),sQuery(id+"F3.wireOp",EDGE,"E912"),sQuery(id+"F3.wireOp",EDGE,"E913"),sQuery(id+"F3.wireOp",EDGE,"E914"),sQuery(id+"F3.wireOp",EDGE,"E915"),sQuery(id+"F3.wireOp",EDGE,"E916"),sQuery(id+"F3.wireOp",EDGE,"E917"),sQuery(id+"F3.wireOp",EDGE,"E918"),sQuery(id+"F3.wireOp",EDGE,"E919"),sQuery(id+"F3.wireOp",EDGE,"E920"),sQuery(id+"F3.wireOp",EDGE,"E921"),sQuery(id+"F3.wireOp",EDGE,"E922"),sQuery(id+"F3.wireOp",EDGE,"E923"),sQuery(id+"F3.wireOp",EDGE,"E924"),sQuery(id+"F3.wireOp",EDGE,"E925"),sQuery(id+"F3.wireOp",EDGE,"E926"),sQuery(id+"F3.wireOp",EDGE,"E927"),sQuery(id+"F3.wireOp",EDGE,"E928"),sQuery(id+"F3.wireOp",EDGE,"E929"),sQuery(id+"F3.wireOp",EDGE,"E930"),sQuery(id+"F3.wireOp",EDGE,"E931"),sQuery(id+"F3.wireOp",EDGE,"E932"),sQuery(id+"F3.wireOp",EDGE,"E933"),sQuery(id+"F3.wireOp",EDGE,"E934"),sQuery(id+"F3.wireOp",EDGE,"E935"),sQuery(id+"F3.wireOp",EDGE,"E936"),sQuery(id+"F3.wireOp",EDGE,"E937"),sQuery(id+"F3.wireOp",EDGE,"E938"),sQuery(id+"F3.wireOp",EDGE,"E939"),sQuery(id+"F3.wireOp",EDGE,"E940"),sQuery(id+"F3.wireOp",EDGE,"E941"),sQuery(id+"F3.wireOp",EDGE,"E942"),sQuery(id+"F3.wireOp",EDGE,"E943"),sQuery(id+"F3.wireOp",EDGE,"E944"),sQuery(id+"F3.wireOp",EDGE,"E945"),sQuery(id+"F3.wireOp",EDGE,"E946"),sQuery(id+"F3.wireOp",EDGE,"E947"),sQuery(id+"F3.wireOp",EDGE,"E948"),sQuery(id+"F3.wireOp",EDGE,"E949"),sQuery(id+"F3.wireOp",EDGE,"E950"),sQuery(id+"F3.wireOp",EDGE,"E951"),sQuery(id+"F3.wireOp",EDGE,"E952"),sQuery(id+"F3.wireOp",EDGE,"E953"),sQuery(id+"F3.wireOp",EDGE,"E954"),sQuery(id+"F3.wireOp",EDGE,"E955"),sQuery(id+"F3.wireOp",EDGE,"E956"),sQuery(id+"F3.wireOp",EDGE,"E957"),sQuery(id+"F3.wireOp",EDGE,"E958"),sQuery(id+"F3.wireOp",EDGE,"E959"),sQuery(id+"F3.wireOp",EDGE,"E960"),sQuery(id+"F3.wireOp",EDGE,"E961"),sQuery(id+"F3.wireOp",EDGE,"E962"),sQuery(id+"F3.wireOp",EDGE,"E963"),sQuery(id+"F3.wireOp",EDGE,"E964"),sQuery(id+"F3.wireOp",EDGE,"E965"),sQuery(id+"F3.wireOp",EDGE,"E966"),sQuery(id+"F3.wireOp",EDGE,"E967"),sQuery(id+"F3.wireOp",EDGE,"E968"),sQuery(id+"F3.wireOp",EDGE,"E969"),sQuery(id+"F3.wireOp",EDGE,"E970"),sQuery(id+"F3.wireOp",EDGE,"E971"),sQuery(id+"F3.wireOp",EDGE,"E972"),sQuery(id+"F3.wireOp",EDGE,"E973"),sQuery(id+"F3.wireOp",EDGE,"E974"),sQuery(id+"F3.wireOp",EDGE,"E975"),sQuery(id+"F3.wireOp",EDGE,"E976"),sQuery(id+"F3.wireOp",EDGE,"E977"),sQuery(id+"F3.wireOp",EDGE,"E978"),sQuery(id+"F3.wireOp",EDGE,"E979"),sQuery(id+"F3.wireOp",EDGE,"E980"),sQuery(id+"F3.wireOp",EDGE,"E981"),sQuery(id+"F3.wireOp",EDGE,"E982"),sQuery(id+"F3.wireOp",EDGE,"E983"),sQuery(id+"F3.wireOp",EDGE,"E984"),sQuery(id+"F3.wireOp",EDGE,"E985"),sQuery(id+"F3.wireOp",EDGE,"E986"),sQuery(id+"F3.wireOp",EDGE,"E987"),sQuery(id+"F3.wireOp",EDGE,"E988"),sQuery(id+"F3.wireOp",EDGE,"E989"),sQuery(id+"F3.wireOp",EDGE,"E990"),sQuery(id+"F3.wireOp",EDGE,"E991"),sQuery(id+"F3.wireOp",EDGE,"E992"),sQuery(id+"F3.wireOp",EDGE,"E993"),sQuery(id+"F3.wireOp",EDGE,"E994"),sQuery(id+"F3.wireOp",EDGE,"E995"),sQuery(id+"F3.wireOp",EDGE,"E996"),sQuery(id+"F3.wireOp",EDGE,"E997"),sQuery(id+"F3.wireOp",EDGE,"E998"),sQuery(id+"F3.wireOp",EDGE,"E999"),sQuery(id+"F3.wireOp",EDGE,"E1000"),sQuery(id+"F3.wireOp",EDGE,"E1001"),sQuery(id+"F3.wireOp",EDGE,"E1002"),sQuery(id+"F3.wireOp",EDGE,"E1003"),sQuery(id+"F3.wireOp",EDGE,"E1004"),sQuery(id+"F3.wireOp",EDGE,"E1005"),sQuery(id+"F3.wireOp",EDGE,"E1006"),sQuery(id+"F3.wireOp",EDGE,"E1007"),sQuery(id+"F3.wireOp",EDGE,"E1008"),sQuery(id+"F3.wireOp",EDGE,"E1009"),sQuery(id+"F3.wireOp",EDGE,"E1010"),sQuery(id+"F3.wireOp",EDGE,"E1011"),sQuery(id+"F3.wireOp",EDGE,"E1012"),sQuery(id+"F3.wireOp",EDGE,"E1013"),sQuery(id+"F3.wireOp",EDGE,"E1014"),sQuery(id+"F3.wireOp",EDGE,"E1015"),sQuery(id+"F3.wireOp",EDGE,"E1016"),sQuery(id+"F3.wireOp",EDGE,"E1017"),sQuery(id+"F3.wireOp",EDGE,"E1018"),sQuery(id+"F3.wireOp",EDGE,"E1019"),sQuery(id+"F3.wireOp",EDGE,"E1020"),sQuery(id+"F3.wireOp",EDGE,"E1021"),sQuery(id+"F3.wireOp",EDGE,"E1022"),sQuery(id+"F3.wireOp",EDGE,"E1023"),sQuery(id+"F3.wireOp",EDGE,"E1024"),sQuery(id+"F3.wireOp",EDGE,"E1025"),sQuery(id+"F3.wireOp",EDGE,"E1026"),sQuery(id+"F3.wireOp",EDGE,"E1027"),sQuery(id+"F3.wireOp",EDGE,"E1028"),sQuery(id+"F3.wireOp",EDGE,"E1029"),sQuery(id+"F3.wireOp",EDGE,"E1030"),sQuery(id+"F3.wireOp",EDGE,"E1031"),sQuery(id+"F3.wireOp",EDGE,"E1032"),sQuery(id+"F3.wireOp",EDGE,"E1033"),sQuery(id+"F3.wireOp",EDGE,"E1034"),sQuery(id+"F3.wireOp",EDGE,"E1035"),sQuery(id+"F3.wireOp",EDGE,"E1036"),sQuery(id+"F3.wireOp",EDGE,"E1037"),sQuery(id+"F3.wireOp",EDGE,"E1038"),sQuery(id+"F3.wireOp",EDGE,"E1039"),sQuery(id+"F3.wireOp",EDGE,"E1040"),sQuery(id+"F3.wireOp",EDGE,"E1041"),sQuery(id+"F3.wireOp",EDGE,"E1042"),sQuery(id+"F3.wireOp",EDGE,"E1043"),sQuery(id+"F3.wireOp",EDGE,"E1044"),sQuery(id+"F3.wireOp",EDGE,"E1045"),sQuery(id+"F3.wireOp",EDGE,"E1046"),sQuery(id+"F3.wireOp",EDGE,"E1047"),sQuery(id+"F3.wireOp",EDGE,"E1048"),sQuery(id+"F3.wireOp",EDGE,"E1049"),sQuery(id+"F3.wireOp",EDGE,"E1050"),sQuery(id+"F3.wireOp",EDGE,"E1051"),sQuery(id+"F3.wireOp",EDGE,"E1052"),sQuery(id+"F3.wireOp",EDGE,"E1053"),sQuery(id+"F3.wireOp",EDGE,"E1054"),sQuery(id+"F3.wireOp",EDGE,"E1055"),sQuery(id+"F3.wireOp",EDGE,"E1056"),sQuery(id+"F3.wireOp",EDGE,"E1057"),sQuery(id+"F3.wireOp",EDGE,"E1058"),sQuery(id+"F3.wireOp",EDGE,"E1059"),sQuery(id+"F3.wireOp",EDGE,"E1060"),sQuery(id+"F3.wireOp",EDGE,"E1061"),sQuery(id+"F3.wireOp",EDGE,"E1062"),sQuery(id+"F3.wireOp",EDGE,"E1063"),sQuery(id+"F3.wireOp",EDGE,"E1064"),sQuery(id+"F3.wireOp",EDGE,"E1065"),sQuery(id+"F3.wireOp",EDGE,"E1066"),sQuery(id+"F3.wireOp",EDGE,"E1067"),sQuery(id+"F3.wireOp",EDGE,"E1068"),sQuery(id+"F3.wireOp",EDGE,"E1069"),sQuery(id+"F3.wireOp",EDGE,"E1070"),sQuery(id+"F3.wireOp",EDGE,"E1071"),sQuery(id+"F3.wireOp",EDGE,"E1072"),sQuery(id+"F3.wireOp",EDGE,"E1073"),sQuery(id+"F3.wireOp",EDGE,"E1074"),sQuery(id+"F3.wireOp",EDGE,"E1075"),sQuery(id+"F3.wireOp",EDGE,"E1076"),sQuery(id+"F3.wireOp",EDGE,"E1077"),sQuery(id+"F3.wireOp",EDGE,"E1078"),sQuery(id+"F3.wireOp",EDGE,"E1079"),sQuery(id+"F3.wireOp",EDGE,"E1080"),sQuery(id+"F3.wireOp",EDGE,"E1081"),sQuery(id+"F3.wireOp",EDGE,"E1082"),sQuery(id+"F3.wireOp",EDGE,"E1083"),sQuery(id+"F3.wireOp",EDGE,"E1084"),sQuery(id+"F3.wireOp",EDGE,"E1085"),sQuery(id+"F3.wireOp",EDGE,"E1086"),sQuery(id+"F3.wireOp",EDGE,"E1087"),sQuery(id+"F3.wireOp",EDGE,"E1088"),sQuery(id+"F3.wireOp",EDGE,"E1089"),sQuery(id+"F3.wireOp",EDGE,"E1090"),sQuery(id+"F3.wireOp",EDGE,"E1091"),sQuery(id+"F3.wireOp",EDGE,"E1092"),sQuery(id+"F3.wireOp",EDGE,"E1093"),sQuery(id+"F3.wireOp",EDGE,"E1094"),sQuery(id+"F3.wireOp",EDGE,"E1095"),sQuery(id+"F3.wireOp",EDGE,"E1096"),sQuery(id+"F3.wireOp",EDGE,"E1097"),sQuery(id+"F3.wireOp",EDGE,"E1098"),sQuery(id+"F3.wireOp",EDGE,"E1099"),sQuery(id+"F3.wireOp",EDGE,"E1100"),sQuery(id+"F3.wireOp",EDGE,"E1101"),sQuery(id+"F3.wireOp",EDGE,"E1102"),sQuery(id+"F3.wireOp",EDGE,"E1103"),sQuery(id+"F3.wireOp",EDGE,"E1104"),sQuery(id+"F3.wireOp",EDGE,"E1105"),sQuery(id+"F3.wireOp",EDGE,"E1106"),sQuery(id+"F3.wireOp",EDGE,"E1107"),sQuery(id+"F3.wireOp",EDGE,"E1108"),sQuery(id+"F3.wireOp",EDGE,"E1109"),sQuery(id+"F3.wireOp",EDGE,"E1110"),sQuery(id+"F3.wireOp",EDGE,"E1111"),sQuery(id+"F3.wireOp",EDGE,"E1112"),sQuery(id+"F3.wireOp",EDGE,"E1113"),sQuery(id+"F3.wireOp",EDGE,"E1114"),sQuery(id+"F3.wireOp",EDGE,"E1115"),sQuery(id+"F3.wireOp",EDGE,"E1116"),sQuery(id+"F3.wireOp",EDGE,"E1117"),sQuery(id+"F3.wireOp",EDGE,"E1118"),sQuery(id+"F3.wireOp",EDGE,"E1119"),sQuery(id+"F3.wireOp",EDGE,"E1120"),sQuery(id+"F3.wireOp",EDGE,"E1121"),sQuery(id+"F3.wireOp",EDGE,"E1122"),sQuery(id+"F3.wireOp",EDGE,"E1123"),sQuery(id+"F3.wireOp",EDGE,"E1124"),sQuery(id+"F3.wireOp",EDGE,"E1125"),sQuery(id+"F3.wireOp",EDGE,"E1126"),sQuery(id+"F3.wireOp",EDGE,"E1127"),sQuery(id+"F3.wireOp",EDGE,"E1128"),sQuery(id+"F3.wireOp",EDGE,"E1129"),sQuery(id+"F3.wireOp",EDGE,"E1130"),sQuery(id+"F3.wireOp",EDGE,"E1131"),sQuery(id+"F3.wireOp",EDGE,"E1132"),sQuery(id+"F3.wireOp",EDGE,"E1133"),sQuery(id+"F3.wireOp",EDGE,"E1134"),sQuery(id+"F3.wireOp",EDGE,"E1135"),sQuery(id+"F3.wireOp",EDGE,"E1136"),sQuery(id+"F3.wireOp",EDGE,"E1137"),sQuery(id+"F3.wireOp",EDGE,"E1138"),sQuery(id+"F3.wireOp",EDGE,"E1139"),sQuery(id+"F3.wireOp",EDGE,"E1140"),sQuery(id+"F3.wireOp",EDGE,"E1141"),sQuery(id+"F3.wireOp",EDGE,"E1142"),sQuery(id+"F3.wireOp",EDGE,"E1143"),sQuery(id+"F3.wireOp",EDGE,"E1144"),sQuery(id+"F3.wireOp",EDGE,"E1145"),sQuery(id+"F3.wireOp",EDGE,"E1146"),sQuery(id+"F3.wireOp",EDGE,"E1147"),sQuery(id+"F3.wireOp",EDGE,"E1148"),sQuery(id+"F3.wireOp",EDGE,"E1149"),sQuery(id+"F3.wireOp",EDGE,"E1150"),sQuery(id+"F3.wireOp",EDGE,"E1151"),sQuery(id+"F3.wireOp",EDGE,"E1152"),sQuery(id+"F3.wireOp",EDGE,"E1153"),sQuery(id+"F3.wireOp",EDGE,"E1154"),sQuery(id+"F3.wireOp",EDGE,"E1155"),sQuery(id+"F3.wireOp",EDGE,"E1156"),sQuery(id+"F3.wireOp",EDGE,"E1157"),sQuery(id+"F3.wireOp",EDGE,"E1158"),sQuery(id+"F3.wireOp",EDGE,"E1159"),sQuery(id+"F3.wireOp",EDGE,"E1160"),sQuery(id+"F3.wireOp",EDGE,"E1161"),sQuery(id+"F3.wireOp",EDGE,"E1162"),sQuery(id+"F3.wireOp",EDGE,"E1163"),sQuery(id+"F3.wireOp",EDGE,"E1164"),sQuery(id+"F3.wireOp",EDGE,"E1165"),sQuery(id+"F3.wireOp",EDGE,"E1166"),sQuery(id+"F3.wireOp",EDGE,"E1167"),sQuery(id+"F3.wireOp",EDGE,"E1168"),sQuery(id+"F3.wireOp",EDGE,"E1169"),sQuery(id+"F3.wireOp",EDGE,"E1170"),sQuery(id+"F3.wireOp",EDGE,"E1171"),sQuery(id+"F3.wireOp",EDGE,"E1172"),sQuery(id+"F3.wireOp",EDGE,"E1173"),sQuery(id+"F3.wireOp",EDGE,"E1174"),sQuery(id+"F3.wireOp",EDGE,"E1175"),sQuery(id+"F3.wireOp",EDGE,"E1176"),sQuery(id+"F3.wireOp",EDGE,"E1177"),sQuery(id+"F3.wireOp",EDGE,"E1178"),sQuery(id+"F3.wireOp",EDGE,"E1179"),sQuery(id+"F3.wireOp",EDGE,"E1180"),sQuery(id+"F3.wireOp",EDGE,"E1181"),sQuery(id+"F3.wireOp",EDGE,"E1182"),sQuery(id+"F3.wireOp",EDGE,"E1183"),sQuery(id+"F3.wireOp",EDGE,"E1184"),sQuery(id+"F3.wireOp",EDGE,"E1185"),sQuery(id+"F3.wireOp",EDGE,"E1186"),sQuery(id+"F3.wireOp",EDGE,"E1187"),sQuery(id+"F3.wireOp",EDGE,"E1188"),sQuery(id+"F3.wireOp",EDGE,"E1189"),sQuery(id+"F3.wireOp",EDGE,"E1190"),sQuery(id+"F3.wireOp",EDGE,"E1191"),sQuery(id+"F3.wireOp",EDGE,"E1192"),sQuery(id+"F3.wireOp",EDGE,"E1193"),sQuery(id+"F3.wireOp",EDGE,"E1194"),sQuery(id+"F3.wireOp",EDGE,"E1195"),sQuery(id+"F3.wireOp",EDGE,"E1196"),sQuery(id+"F3.wireOp",EDGE,"E1197"),sQuery(id+"F3.wireOp",EDGE,"E1198"),sQuery(id+"F3.wireOp",EDGE,"E1199"),sQuery(id+"F3.wireOp",EDGE,"E1200"),sQuery(id+"F3.wireOp",EDGE,"E1201"),sQuery(id+"F3.wireOp",EDGE,"E1202"),sQuery(id+"F3.wireOp",EDGE,"E1203"),sQuery(id+"F3.wireOp",EDGE,"E1204"),sQuery(id+"F3.wireOp",EDGE,"E1205"),sQuery(id+"F3.wireOp",EDGE,"E1206"),sQuery(id+"F3.wireOp",EDGE,"E1207"),sQuery(id+"F3.wireOp",EDGE,"E1208"),sQuery(id+"F3.wireOp",EDGE,"E1209"),sQuery(id+"F3.wireOp",EDGE,"E1210"),sQuery(id+"F3.wireOp",EDGE,"E1211"),sQuery(id+"F3.wireOp",EDGE,"E1212"),sQuery(id+"F3.wireOp",EDGE,"E1213"),sQuery(id+"F3.wireOp",EDGE,"E1214"),sQuery(id+"F3.wireOp",EDGE,"E1215"),sQuery(id+"F3.wireOp",EDGE,"E1216"),sQuery(id+"F3.wireOp",EDGE,"E1217"),sQuery(id+"F3.wireOp",EDGE,"E1218"),sQuery(id+"F3.wireOp",EDGE,"E1219"),sQuery(id+"F3.wireOp",EDGE,"E1220"),sQuery(id+"F3.wireOp",EDGE,"E1221"),sQuery(id+"F3.wireOp",EDGE,"E1222"),sQuery(id+"F3.wireOp",EDGE,"E1223"),sQuery(id+"F3.wireOp",EDGE,"E1224"),sQuery(id+"F3.wireOp",EDGE,"E1225"),sQuery(id+"F3.wireOp",EDGE,"E1226"),sQuery(id+"F3.wireOp",EDGE,"E1227"),sQuery(id+"F3.wireOp",EDGE,"E1228"),sQuery(id+"F3.wireOp",EDGE,"E1229"),sQuery(id+"F3.wireOp",EDGE,"E1230"),sQuery(id+"F3.wireOp",EDGE,"E1231"),sQuery(id+"F3.wireOp",EDGE,"E1232"),sQuery(id+"F3.wireOp",EDGE,"E1233"),sQuery(id+"F3.wireOp",EDGE,"E1234"),sQuery(id+"F3.wireOp",EDGE,"E1235"),sQuery(id+"F3.wireOp",EDGE,"E1236"),sQuery(id+"F3.wireOp",EDGE,"E1237"),sQuery(id+"F3.wireOp",EDGE,"E1238"),sQuery(id+"F3.wireOp",EDGE,"E1239"),sQuery(id+"F3.wireOp",EDGE,"E1240"),sQuery(id+"F3.wireOp",EDGE,"E1241"),sQuery(id+"F3.wireOp",EDGE,"E1242"),sQuery(id+"F3.wireOp",EDGE,"E1243"),sQuery(id+"F3.wireOp",EDGE,"E1244"),sQuery(id+"F3.wireOp",EDGE,"E1245"),sQuery(id+"F3.wireOp",EDGE,"E1246"),sQuery(id+"F3.wireOp",EDGE,"E1247"),sQuery(id+"F3.wireOp",EDGE,"E1248"),sQuery(id+"F3.wireOp",EDGE,"E1249"),sQuery(id+"F3.wireOp",EDGE,"E1250"),sQuery(id+"F3.wireOp",EDGE,"E1251"),sQuery(id+"F3.wireOp",EDGE,"E1252"),sQuery(id+"F3.wireOp",EDGE,"E1253"),sQuery(id+"F3.wireOp",EDGE,"E1254"),sQuery(id+"F3.wireOp",EDGE,"E1255"),sQuery(id+"F3.wireOp",EDGE,"E1256"),sQuery(id+"F3.wireOp",EDGE,"E1257"),sQuery(id+"F3.wireOp",EDGE,"E1258"),sQuery(id+"F3.wireOp",EDGE,"E1259"),sQuery(id+"F3.wireOp",EDGE,"E1260"),sQuery(id+"F3.wireOp",EDGE,"E1261"),sQuery(id+"F3.wireOp",EDGE,"E1262"),sQuery(id+"F3.wireOp",EDGE,"E1263"),sQuery(id+"F3.wireOp",EDGE,"E1264"),sQuery(id+"F3.wireOp",EDGE,"E1265"),sQuery(id+"F3.wireOp",EDGE,"E1266"),sQuery(id+"F3.wireOp",EDGE,"E1267"),sQuery(id+"F3.wireOp",EDGE,"E1268"),sQuery(id+"F3.wireOp",EDGE,"E1269"),sQuery(id+"F3.wireOp",EDGE,"E1270"),sQuery(id+"F3.wireOp",EDGE,"E1271"),sQuery(id+"F3.wireOp",EDGE,"E1272"),sQuery(id+"F3.wireOp",EDGE,"E1273"),sQuery(id+"F3.wireOp",EDGE,"E1274"),sQuery(id+"F3.wireOp",EDGE,"E1275"),sQuery(id+"F3.wireOp",EDGE,"E1276"),sQuery(id+"F3.wireOp",EDGE,"E1277"),sQuery(id+"F3.wireOp",EDGE,"E1278"),sQuery(id+"F3.wireOp",EDGE,"E1279"),sQuery(id+"F3.wireOp",EDGE,"E1280"),sQuery(id+"F3.wireOp",EDGE,"E1281"),sQuery(id+"F3.wireOp",EDGE,"E1282"),sQuery(id+"F3.wireOp",EDGE,"E1283"),sQuery(id+"F3.wireOp",EDGE,"E1284"),sQuery(id+"F3.wireOp",EDGE,"E1285"),sQuery(id+"F3.wireOp",EDGE,"E1286"),sQuery(id+"F3.wireOp",EDGE,"E1287"),sQuery(id+"F3.wireOp",EDGE,"E1288"),sQuery(id+"F3.wireOp",EDGE,"E1289"),sQuery(id+"F3.wireOp",EDGE,"E1290"),sQuery(id+"F3.wireOp",EDGE,"E1291"),sQuery(id+"F3.wireOp",EDGE,"E1292"),sQuery(id+"F3.wireOp",EDGE,"E1293"),sQuery(id+"F3.wireOp",EDGE,"E1294"),sQuery(id+"F3.wireOp",EDGE,"E1295"),sQuery(id+"F3.wireOp",EDGE,"E1296"),sQuery(id+"F3.wireOp",EDGE,"E1297"),sQuery(id+"F3.wireOp",EDGE,"E1298"),sQuery(id+"F3.wireOp",EDGE,"E1299"),sQuery(id+"F3.wireOp",EDGE,"E1300"),sQuery(id+"F3.wireOp",EDGE,"E1301"),sQuery(id+"F3.wireOp",EDGE,"E1302"),sQuery(id+"F3.wireOp",EDGE,"E1303"),sQuery(id+"F3.wireOp",EDGE,"E1304"),sQuery(id+"F3.wireOp",EDGE,"E1305"),sQuery(id+"F3.wireOp",EDGE,"E1306"),sQuery(id+"F3.wireOp",EDGE,"E1307"),sQuery(id+"F3.wireOp",EDGE,"E1308"),sQuery(id+"F3.wireOp",EDGE,"E1309"),sQuery(id+"F3.wireOp",EDGE,"E1310"),sQuery(id+"F3.wireOp",EDGE,"E1311"),sQuery(id+"F3.wireOp",EDGE,"E1312"),sQuery(id+"F3.wireOp",EDGE,"E1313"),sQuery(id+"F3.wireOp",EDGE,"E1314"),sQuery(id+"F3.wireOp",EDGE,"E1315"),sQuery(id+"F3.wireOp",EDGE,"E1316"),sQuery(id+"F3.wireOp",EDGE,"E1317"),sQuery(id+"F3.wireOp",EDGE,"E1318"),sQuery(id+"F3.wireOp",EDGE,"E1319"),sQuery(id+"F3.wireOp",EDGE,"E1320"),sQuery(id+"F3.wireOp",EDGE,"E1321"),sQuery(id+"F3.wireOp",EDGE,"E1322"),sQuery(id+"F3.wireOp",EDGE,"E1323"),sQuery(id+"F3.wireOp",EDGE,"E1324"),sQuery(id+"F3.wireOp",EDGE,"E1325"),sQuery(id+"F3.wireOp",EDGE,"E1326"),sQuery(id+"F3.wireOp",EDGE,"E1327"),sQuery(id+"F3.wireOp",EDGE,"E1328"),sQuery(id+"F3.wireOp",EDGE,"E1329"),sQuery(id+"F3.wireOp",EDGE,"E1330"),sQuery(id+"F3.wireOp",EDGE,"E1331"),sQuery(id+"F3.wireOp",EDGE,"E1332"),sQuery(id+"F3.wireOp",EDGE,"E1333"),sQuery(id+"F3.wireOp",EDGE,"E1334"),sQuery(id+"F3.wireOp",EDGE,"E1335"),sQuery(id+"F3.wireOp",EDGE,"E1336"),sQuery(id+"F3.wireOp",EDGE,"E1337"),sQuery(id+"F3.wireOp",EDGE,"E1338"),sQuery(id+"F3.wireOp",EDGE,"E1339"),sQuery(id+"F3.wireOp",EDGE,"E1340"),sQuery(id+"F3.wireOp",EDGE,"E1341"),sQuery(id+"F3.wireOp",EDGE,"E1342"),sQuery(id+"F3.wireOp",EDGE,"E1343"),sQuery(id+"F3.wireOp",EDGE,"E1344"),sQuery(id+"F3.wireOp",EDGE,"E1345"),sQuery(id+"F3.wireOp",EDGE,"E1346"),sQuery(id+"F3.wireOp",EDGE,"E1347"),sQuery(id+"F3.wireOp",EDGE,"E1348"),sQuery(id+"F3.wireOp",EDGE,"E1349"),sQuery(id+"F3.wireOp",EDGE,"E1350"),sQuery(id+"F3.wireOp",EDGE,"E1351"),sQuery(id+"F3.wireOp",EDGE,"E1352"),sQuery(id+"F3.wireOp",EDGE,"E1353"),sQuery(id+"F3.wireOp",EDGE,"E1354"),sQuery(id+"F3.wireOp",EDGE,"E1355"),sQuery(id+"F3.wireOp",EDGE,"E1356"),sQuery(id+"F3.wireOp",EDGE,"E1357"),sQuery(id+"F3.wireOp",EDGE,"E1358"),sQuery(id+"F3.wireOp",EDGE,"E1359"),sQuery(id+"F3.wireOp",EDGE,"E1360"),sQuery(id+"F3.wireOp",EDGE,"E1361"),sQuery(id+"F3.wireOp",EDGE,"E1362"),sQuery(id+"F3.wireOp",EDGE,"E1363"),sQuery(id+"F3.wireOp",EDGE,"E1364"),sQuery(id+"F3.wireOp",EDGE,"E1365"),sQuery(id+"F3.wireOp",EDGE,"E1366"),sQuery(id+"F3.wireOp",EDGE,"E1367"),sQuery(id+"F3.wireOp",EDGE,"E1368"),sQuery(id+"F3.wireOp",EDGE,"E1369"),sQuery(id+"F3.wireOp",EDGE,"E1370"),sQuery(id+"F3.wireOp",EDGE,"E1371"),sQuery(id+"F3.wireOp",EDGE,"E1372"),sQuery(id+"F3.wireOp",EDGE,"E1373"),sQuery(id+"F3.wireOp",EDGE,"E1374"),sQuery(id+"F3.wireOp",EDGE,"E1375"),sQuery(id+"F3.wireOp",EDGE,"E1376"),sQuery(id+"F3.wireOp",EDGE,"E1377"),sQuery(id+"F3.wireOp",EDGE,"E1378"),sQuery(id+"F3.wireOp",EDGE,"E1379"),sQuery(id+"F3.wireOp",EDGE,"E1380"),sQuery(id+"F3.wireOp",EDGE,"E1381"),sQuery(id+"F3.wireOp",EDGE,"E1382"),sQuery(id+"F3.wireOp",EDGE,"E1383"),sQuery(id+"F3.wireOp",EDGE,"E1384"),sQuery(id+"F3.wireOp",EDGE,"E1385"),sQuery(id+"F3.wireOp",EDGE,"E1386"),sQuery(id+"F3.wireOp",EDGE,"E1387"),sQuery(id+"F3.wireOp",EDGE,"E1388"),sQuery(id+"F3.wireOp",EDGE,"E1389"),sQuery(id+"F3.wireOp",EDGE,"E1390"),sQuery(id+"F3.wireOp",EDGE,"E1391"),sQuery(id+"F3.wireOp",EDGE,"E1392"),sQuery(id+"F3.wireOp",EDGE,"E1393"),sQuery(id+"F3.wireOp",EDGE,"E1394"),sQuery(id+"F3.wireOp",EDGE,"E1395"),sQuery(id+"F3.wireOp",EDGE,"E1396"),sQuery(id+"F3.wireOp",EDGE,"E1397"),sQuery(id+"F3.wireOp",EDGE,"E1398"),sQuery(id+"F3.wireOp",EDGE,"E1399"),sQuery(id+"F3.wireOp",EDGE,"E1400"),sQuery(id+"F3.wireOp",EDGE,"E1401"),sQuery(id+"F3.wireOp",EDGE,"E1402"),sQuery(id+"F3.wireOp",EDGE,"E1403"),sQuery(id+"F3.wireOp",EDGE,"E1404"),sQuery(id+"F3.wireOp",EDGE,"E1405"),sQuery(id+"F3.wireOp",EDGE,"E1406"),sQuery(id+"F3.wireOp",EDGE,"E1407"),sQuery(id+"F3.wireOp",EDGE,"E1408"),sQuery(id+"F3.wireOp",EDGE,"E1409"),sQuery(id+"F3.wireOp",EDGE,"E1410"),sQuery(id+"F3.wireOp",EDGE,"E1411"),sQuery(id+"F3.wireOp",EDGE,"E1412"),sQuery(id+"F3.wireOp",EDGE,"E1413"),sQuery(id+"F3.wireOp",EDGE,"E1414"),sQuery(id+"F3.wireOp",EDGE,"E1415"),sQuery(id+"F3.wireOp",EDGE,"E1416"),sQuery(id+"F3.wireOp",EDGE,"E1417"),sQuery(id+"F3.wireOp",EDGE,"E1418"),sQuery(id+"F3.wireOp",EDGE,"E1419"),sQuery(id+"F3.wireOp",EDGE,"E1420"),sQuery(id+"F3.wireOp",EDGE,"E1421"),sQuery(id+"F3.wireOp",EDGE,"E1422"),sQuery(id+"F3.wireOp",EDGE,"E1423"),sQuery(id+"F3.wireOp",EDGE,"E1424"),sQuery(id+"F3.wireOp",EDGE,"E1425"),sQuery(id+"F3.wireOp",EDGE,"E1426"),sQuery(id+"F3.wireOp",EDGE,"E1427"),sQuery(id+"F3.wireOp",EDGE,"E1428"),sQuery(id+"F3.wireOp",EDGE,"E1429"),sQuery(id+"F3.wireOp",EDGE,"E1430"),sQuery(id+"F3.wireOp",EDGE,"E1431"),sQuery(id+"F3.wireOp",EDGE,"E1432"),sQuery(id+"F3.wireOp",EDGE,"E1433"),sQuery(id+"F3.wireOp",EDGE,"E1434"),sQuery(id+"F3.wireOp",EDGE,"E1435"),sQuery(id+"F3.wireOp",EDGE,"E1436"),sQuery(id+"F3.wireOp",EDGE,"E1437"),sQuery(id+"F3.wireOp",EDGE,"E1438"),sQuery(id+"F3.wireOp",EDGE,"E1439"),sQuery(id+"F3.wireOp",EDGE,"E1440"),sQuery(id+"F3.wireOp",EDGE,"E1441"),sQuery(id+"F3.wireOp",EDGE,"E1442"),sQuery(id+"F3.wireOp",EDGE,"E1443"),sQuery(id+"F3.wireOp",EDGE,"E1444"),sQuery(id+"F3.wireOp",EDGE,"E1445"),sQuery(id+"F3.wireOp",EDGE,"E1446"),sQuery(id+"F3.wireOp",EDGE,"E1447"),sQuery(id+"F3.wireOp",EDGE,"E1448"),sQuery(id+"F3.wireOp",EDGE,"E1449"),sQuery(id+"F3.wireOp",EDGE,"E1450"),sQuery(id+"F3.wireOp",EDGE,"E1451"),sQuery(id+"F3.wireOp",EDGE,"E1452"),sQuery(id+"F3.wireOp",EDGE,"E1453"),sQuery(id+"F3.wireOp",EDGE,"E1454"),sQuery(id+"F3.wireOp",EDGE,"E1455"),sQuery(id+"F3.wireOp",EDGE,"E1456"),sQuery(id+"F3.wireOp",EDGE,"E1457"),sQuery(id+"F3.wireOp",EDGE,"E1458"),sQuery(id+"F3.wireOp",EDGE,"E1459"),sQuery(id+"F3.wireOp",EDGE,"E1460"),sQuery(id+"F3.wireOp",EDGE,"E1461"),sQuery(id+"F3.wireOp",EDGE,"E1462"),sQuery(id+"F3.wireOp",EDGE,"E1463"),sQuery(id+"F3.wireOp",EDGE,"E1464"),sQuery(id+"F3.wireOp",EDGE,"E1465"),sQuery(id+"F3.wireOp",EDGE,"E1466"),sQuery(id+"F3.wireOp",EDGE,"E1467"),sQuery(id+"F3.wireOp",EDGE,"E1468"),sQuery(id+"F3.wireOp",EDGE,"E1469"),sQuery(id+"F3.wireOp",EDGE,"E1470"),sQuery(id+"F3.wireOp",EDGE,"E1471"),sQuery(id+"F3.wireOp",EDGE,"E1472"),sQuery(id+"F3.wireOp",EDGE,"E1473"),sQuery(id+"F3.wireOp",EDGE,"E1474"),sQuery(id+"F3.wireOp",EDGE,"E1475"),sQuery(id+"F3.wireOp",EDGE,"E1476"),sQuery(id+"F3.wireOp",EDGE,"E1477"),sQuery(id+"F3.wireOp",EDGE,"E1478"),sQuery(id+"F3.wireOp",EDGE,"E1479"),sQuery(id+"F3.wireOp",EDGE,"E1480"),sQuery(id+"F3.wireOp",EDGE,"E1481"),sQuery(id+"F3.wireOp",EDGE,"E1482"),sQuery(id+"F3.wireOp",EDGE,"E1483"),sQuery(id+"F3.wireOp",EDGE,"E1484"),sQuery(id+"F3.wireOp",EDGE,"E1485"),sQuery(id+"F3.wireOp",EDGE,"E1486"),sQuery(id+"F3.wireOp",EDGE,"E1487"),sQuery(id+"F3.wireOp",EDGE,"E1488"),sQuery(id+"F3.wireOp",EDGE,"E1489"),sQuery(id+"F3.wireOp",EDGE,"E1490"),sQuery(id+"F3.wireOp",EDGE,"E1491"),sQuery(id+"F3.wireOp",EDGE,"E1492"),sQuery(id+"F3.wireOp",EDGE,"E1493"),sQuery(id+"F3.wireOp",EDGE,"E1494"),sQuery(id+"F3.wireOp",EDGE,"E1495"),sQuery(id+"F3.wireOp",EDGE,"E1496"),sQuery(id+"F3.wireOp",EDGE,"E1497"),sQuery(id+"F3.wireOp",EDGE,"E1498"),sQuery(id+"F3.wireOp",EDGE,"E1499"),sQuery(id+"F3.wireOp",EDGE,"E1500"),sQuery(id+"F3.wireOp",EDGE,"E1501"),sQuery(id+"F3.wireOp",EDGE,"E1502"),sQuery(id+"F3.wireOp",EDGE,"E1503"),sQuery(id+"F3.wireOp",EDGE,"E1504"),sQuery(id+"F3.wireOp",EDGE,"E1505"),sQuery(id+"F3.wireOp",EDGE,"E1506"),sQuery(id+"F3.wireOp",EDGE,"E1507"),sQuery(id+"F3.wireOp",EDGE,"E1508"),sQuery(id+"F3.wireOp",EDGE,"E1509"),sQuery(id+"F3.wireOp",EDGE,"E1510"),sQuery(id+"F3.wireOp",EDGE,"E1511"),sQuery(id+"F3.wireOp",EDGE,"E1512"),sQuery(id+"F3.wireOp",EDGE,"E1513"),sQuery(id+"F3.wireOp",EDGE,"E1514"),sQuery(id+"F3.wireOp",EDGE,"E1515"),sQuery(id+"F3.wireOp",EDGE,"E1516"),sQuery(id+"F3.wireOp",EDGE,"E1517"),sQuery(id+"F3.wireOp",EDGE,"E1518"),sQuery(id+"F3.wireOp",EDGE,"E1519"),sQuery(id+"F3.wireOp",EDGE,"E1520"),sQuery(id+"F3.wireOp",EDGE,"E1521"),sQuery(id+"F3.wireOp",EDGE,"E1522"),sQuery(id+"F3.wireOp",EDGE,"E1523"),sQuery(id+"F3.wireOp",EDGE,"E1524"),sQuery(id+"F3.wireOp",EDGE,"E1525"),sQuery(id+"F3.wireOp",EDGE,"E1526"),sQuery(id+"F3.wireOp",EDGE,"E1527"),sQuery(id+"F3.wireOp",EDGE,"E1528"),sQuery(id+"F3.wireOp",EDGE,"E1529"),sQuery(id+"F3.wireOp",EDGE,"E1530"),sQuery(id+"F3.wireOp",EDGE,"E1531"),sQuery(id+"F3.wireOp",EDGE,"E1532"),sQuery(id+"F3.wireOp",EDGE,"E1533"),sQuery(id+"F3.wireOp",EDGE,"E1534"),sQuery(id+"F3.wireOp",EDGE,"E1535"),sQuery(id+"F3.wireOp",EDGE,"E1536"),sQuery(id+"F3.wireOp",EDGE,"E1537"),sQuery(id+"F3.wireOp",EDGE,"E1538"),sQuery(id+"F3.wireOp",EDGE,"E1539"),sQuery(id+"F3.wireOp",EDGE,"E1540"),sQuery(id+"F3.wireOp",EDGE,"E1541"),sQuery(id+"F3.wireOp",EDGE,"E1542"),sQuery(id+"F3.wireOp",EDGE,"E1543"),sQuery(id+"F3.wireOp",EDGE,"E1544"),sQuery(id+"F3.wireOp",EDGE,"E1545"),sQuery(id+"F3.wireOp",EDGE,"E1546"),sQuery(id+"F3.wireOp",EDGE,"E1547"),sQuery(id+"F3.wireOp",EDGE,"E1548"),sQuery(id+"F3.wireOp",EDGE,"E1549"),sQuery(id+"F3.wireOp",EDGE,"E1550"),sQuery(id+"F3.wireOp",EDGE,"E1551"),sQuery(id+"F3.wireOp",EDGE,"E1552"),sQuery(id+"F3.wireOp",EDGE,"E1553"),sQuery(id+"F3.wireOp",EDGE,"E1554"),sQuery(id+"F3.wireOp",EDGE,"E1555"),sQuery(id+"F3.wireOp",EDGE,"E1556"),sQuery(id+"F3.wireOp",EDGE,"E1557"),sQuery(id+"F3.wireOp",EDGE,"E1558"),sQuery(id+"F3.wireOp",EDGE,"E1559"),sQuery(id+"F3.wireOp",EDGE,"E1560"),sQuery(id+"F3.wireOp",EDGE,"E1561"),sQuery(id+"F3.wireOp",EDGE,"E1562"),sQuery(id+"F3.wireOp",EDGE,"E1563"),sQuery(id+"F3.wireOp",EDGE,"E1564"),sQuery(id+"F3.wireOp",EDGE,"E1565"),sQuery(id+"F3.wireOp",EDGE,"E1566"),sQuery(id+"F3.wireOp",EDGE,"E1567"),sQuery(id+"F3.wireOp",EDGE,"E1568"),sQuery(id+"F3.wireOp",EDGE,"E1569"),sQuery(id+"F3.wireOp",EDGE,"E1570"),sQuery(id+"F3.wireOp",EDGE,"E1571"),sQuery(id+"F3.wireOp",EDGE,"E1572"),sQuery(id+"F3.wireOp",EDGE,"E1573"),sQuery(id+"F3.wireOp",EDGE,"E1574"),sQuery(id+"F3.wireOp",EDGE,"E1575"),sQuery(id+"F3.wireOp",EDGE,"E1576"),sQuery(id+"F3.wireOp",EDGE,"E1577"),sQuery(id+"F3.wireOp",EDGE,"E1578"),sQuery(id+"F3.wireOp",EDGE,"E1579"),sQuery(id+"F3.wireOp",EDGE,"E1580"),sQuery(id+"F3.wireOp",EDGE,"E1581"),sQuery(id+"F3.wireOp",EDGE,"E1582"),sQuery(id+"F3.wireOp",EDGE,"E1583"),sQuery(id+"F3.wireOp",EDGE,"E1584"),sQuery(id+"F3.wireOp",EDGE,"E1585"),sQuery(id+"F3.wireOp",EDGE,"E1586"),sQuery(id+"F3.wireOp",EDGE,"E1587"),sQuery(id+"F3.wireOp",EDGE,"E1588"),sQuery(id+"F3.wireOp",EDGE,"E1589"),sQuery(id+"F3.wireOp",EDGE,"E1590"),sQuery(id+"F3.wireOp",EDGE,"E1591"),sQuery(id+"F3.wireOp",EDGE,"E1592"),sQuery(id+"F3.wireOp",EDGE,"E1593"),sQuery(id+"F3.wireOp",EDGE,"E1594"),sQuery(id+"F3.wireOp",EDGE,"E1595"),sQuery(id+"F3.wireOp",EDGE,"E1596"),sQuery(id+"F3.wireOp",EDGE,"E1597"),sQuery(id+"F3.wireOp",EDGE,"E1598"),sQuery(id+"F3.wireOp",EDGE,"E1599"),sQuery(id+"F3.wireOp",EDGE,"E1600"),sQuery(id+"F3.wireOp",EDGE,"E1601"),sQuery(id+"F3.wireOp",EDGE,"E1602"),sQuery(id+"F3.wireOp",EDGE,"E1603"),sQuery(id+"F3.wireOp",EDGE,"E1604"),sQuery(id+"F3.wireOp",EDGE,"E1605"),sQuery(id+"F3.wireOp",EDGE,"E1606"),sQuery(id+"F3.wireOp",EDGE,"E1607"),sQuery(id+"F3.wireOp",EDGE,"E1608"),sQuery(id+"F3.wireOp",EDGE,"E1609"),sQuery(id+"F3.wireOp",EDGE,"E1610"),sQuery(id+"F3.wireOp",EDGE,"E1611"),sQuery(id+"F3.wireOp",EDGE,"E1612"),sQuery(id+"F3.wireOp",EDGE,"E1613"),sQuery(id+"F3.wireOp",EDGE,"E1614"),sQuery(id+"F3.wireOp",EDGE,"E1615"),sQuery(id+"F3.wireOp",EDGE,"E1616"),sQuery(id+"F3.wireOp",EDGE,"E1617"),sQuery(id+"F3.wireOp",EDGE,"E1618"),sQuery(id+"F3.wireOp",EDGE,"E1619"),sQuery(id+"F3.wireOp",EDGE,"E1620"),sQuery(id+"F3.wireOp",EDGE,"E1621"),sQuery(id+"F3.wireOp",EDGE,"E1622"),sQuery(id+"F3.wireOp",EDGE,"E1623"),sQuery(id+"F3.wireOp",EDGE,"E1624"),sQuery(id+"F3.wireOp",EDGE,"E1625"),sQuery(id+"F3.wireOp",EDGE,"E1626"),sQuery(id+"F3.wireOp",EDGE,"E1627"),sQuery(id+"F3.wireOp",EDGE,"E1628"),sQuery(id+"F3.wireOp",EDGE,"E1629"),sQuery(id+"F3.wireOp",EDGE,"E1630"),sQuery(id+"F3.wireOp",EDGE,"E1631"),sQuery(id+"F3.wireOp",EDGE,"E1632"),sQuery(id+"F3.wireOp",EDGE,"E1633"),sQuery(id+"F3.wireOp",EDGE,"E1634"),sQuery(id+"F3.wireOp",EDGE,"E1635"),sQuery(id+"F3.wireOp",EDGE,"E1636"),sQuery(id+"F3.wireOp",EDGE,"E1637"),sQuery(id+"F3.wireOp",EDGE,"E1638"),sQuery(id+"F3.wireOp",EDGE,"E1639"),sQuery(id+"F3.wireOp",EDGE,"E1640"),sQuery(id+"F3.wireOp",EDGE,"E1641"),sQuery(id+"F3.wireOp",EDGE,"E1642"),sQuery(id+"F3.wireOp",EDGE,"E1643"),sQuery(id+"F3.wireOp",EDGE,"E1644"),sQuery(id+"F3.wireOp",EDGE,"E1645"),sQuery(id+"F3.wireOp",EDGE,"E1646"),sQuery(id+"F3.wireOp",EDGE,"E1647"),sQuery(id+"F3.wireOp",EDGE,"E1648"),sQuery(id+"F3.wireOp",EDGE,"E1649"),sQuery(id+"F3.wireOp",EDGE,"E1650"),sQuery(id+"F3.wireOp",EDGE,"E1651"),sQuery(id+"F3.wireOp",EDGE,"E1652"),sQuery(id+"F3.wireOp",EDGE,"E1653"),sQuery(id+"F3.wireOp",EDGE,"E1654"),sQuery(id+"F3.wireOp",EDGE,"E1655"),sQuery(id+"F3.wireOp",EDGE,"E1656"),sQuery(id+"F3.wireOp",EDGE,"E1657"),sQuery(id+"F3.wireOp",EDGE,"E1658"),sQuery(id+"F3.wireOp",EDGE,"E1659"),sQuery(id+"F3.wireOp",EDGE,"E1660"),sQuery(id+"F3.wireOp",EDGE,"E1661"),sQuery(id+"F3.wireOp",EDGE,"E1662"),sQuery(id+"F3.wireOp",EDGE,"E1663"),sQuery(id+"F3.wireOp",EDGE,"E1664"),sQuery(id+"F3.wireOp",EDGE,"E1665"),sQuery(id+"F3.wireOp",EDGE,"E1666"),sQuery(id+"F3.wireOp",EDGE,"E1667"),sQuery(id+"F3.wireOp",EDGE,"E1668"),sQuery(id+"F3.wireOp",EDGE,"E1669"),sQuery(id+"F3.wireOp",EDGE,"E1670"),sQuery(id+"F3.wireOp",EDGE,"E1671"),sQuery(id+"F3.wireOp",EDGE,"E1672"),sQuery(id+"F3.wireOp",EDGE,"E1673"),sQuery(id+"F3.wireOp",EDGE,"E1674"),sQuery(id+"F3.wireOp",EDGE,"E1675"),sQuery(id+"F3.wireOp",EDGE,"E1676"),sQuery(id+"F3.wireOp",EDGE,"E1677"),sQuery(id+"F3.wireOp",EDGE,"E1678"),sQuery(id+"F3.wireOp",EDGE,"E1679"),sQuery(id+"F3.wireOp",EDGE,"E1680"),sQuery(id+"F3.wireOp",EDGE,"E1681"),sQuery(id+"F3.wireOp",EDGE,"E1682"),sQuery(id+"F3.wireOp",EDGE,"E1683"),sQuery(id+"F3.wireOp",EDGE,"E1684"),sQuery(id+"F3.wireOp",EDGE,"E1685"),sQuery(id+"F3.wireOp",EDGE,"E1686"),sQuery(id+"F3.wireOp",EDGE,"E1687"),sQuery(id+"F3.wireOp",EDGE,"E1688"),sQuery(id+"F3.wireOp",EDGE,"E1689"),sQuery(id+"F3.wireOp",EDGE,"E1690"),sQuery(id+"F3.wireOp",EDGE,"E1691"),sQuery(id+"F3.wireOp",EDGE,"E1692"),sQuery(id+"F3.wireOp",EDGE,"E1693"),sQuery(id+"F3.wireOp",EDGE,"E1694"),sQuery(id+"F3.wireOp",EDGE,"E1695"),sQuery(id+"F3.wireOp",EDGE,"E1696"),sQuery(id+"F3.wireOp",EDGE,"E1697"),sQuery(id+"F3.wireOp",EDGE,"E1698"),sQuery(id+"F3.wireOp",EDGE,"E1699"),sQuery(id+"F3.wireOp",EDGE,"E1700"),sQuery(id+"F3.wireOp",EDGE,"E1701"),sQuery(id+"F3.wireOp",EDGE,"E1702"),sQuery(id+"F3.wireOp",EDGE,"E1703"),sQuery(id+"F3.wireOp",EDGE,"E1704"),sQuery(id+"F3.wireOp",EDGE,"E1705"),sQuery(id+"F3.wireOp",EDGE,"E1706"),sQuery(id+"F3.wireOp",EDGE,"E1707"),sQuery(id+"F3.wireOp",EDGE,"E1708"),sQuery(id+"F3.wireOp",EDGE,"E1709"),sQuery(id+"F3.wireOp",EDGE,"E1710"),sQuery(id+"F3.wireOp",EDGE,"E1711"),sQuery(id+"F3.wireOp",EDGE,"E1712"),sQuery(id+"F3.wireOp",EDGE,"E1713"),sQuery(id+"F3.wireOp",EDGE,"E1714"),sQuery(id+"F3.wireOp",EDGE,"E1715"),sQuery(id+"F3.wireOp",EDGE,"E1716"),sQuery(id+"F3.wireOp",EDGE,"E1717"),sQuery(id+"F3.wireOp",EDGE,"E1718"),sQuery(id+"F3.wireOp",EDGE,"E1719"),sQuery(id+"F3.wireOp",EDGE,"E1720"),sQuery(id+"F3.wireOp",EDGE,"E1721"),sQuery(id+"F3.wireOp",EDGE,"E1722"),sQuery(id+"F3.wireOp",EDGE,"E1723"),sQuery(id+"F3.wireOp",EDGE,"E1724"),sQuery(id+"F3.wireOp",EDGE,"E1725"),sQuery(id+"F3.wireOp",EDGE,"E1726"),sQuery(id+"F3.wireOp",EDGE,"E1727"),sQuery(id+"F3.wireOp",EDGE,"E1728"),sQuery(id+"F3.wireOp",EDGE,"E1729"),sQuery(id+"F3.wireOp",EDGE,"E1730"),sQuery(id+"F3.wireOp",EDGE,"E1731"),sQuery(id+"F3.wireOp",EDGE,"E1732"),sQuery(id+"F3.wireOp",EDGE,"E1733"),sQuery(id+"F3.wireOp",EDGE,"E1734"),sQuery(id+"F3.wireOp",EDGE,"E1735"),sQuery(id+"F3.wireOp",EDGE,"E1736"),sQuery(id+"F3.wireOp",EDGE,"E1737"),sQuery(id+"F3.wireOp",EDGE,"E1738"),sQuery(id+"F3.wireOp",EDGE,"E1739"),sQuery(id+"F3.wireOp",EDGE,"E1740"),sQuery(id+"F3.wireOp",EDGE,"E1741"),sQuery(id+"F3.wireOp",EDGE,"E1742"),sQuery(id+"F3.wireOp",EDGE,"E1743"),sQuery(id+"F3.wireOp",EDGE,"E1744"),sQuery(id+"F3.wireOp",EDGE,"E1745"),sQuery(id+"F3.wireOp",EDGE,"E1746"),sQuery(id+"F3.wireOp",EDGE,"E1747"),sQuery(id+"F3.wireOp",EDGE,"E1748"),sQuery(id+"F3.wireOp",EDGE,"E1749"),sQuery(id+"F3.wireOp",EDGE,"E1750"),sQuery(id+"F3.wireOp",EDGE,"E1751"),sQuery(id+"F3.wireOp",EDGE,"E1752"),sQuery(id+"F3.wireOp",EDGE,"E1753"),sQuery(id+"F3.wireOp",EDGE,"E1754"),sQuery(id+"F3.wireOp",EDGE,"E1755"),sQuery(id+"F3.wireOp",EDGE,"E1756"),sQuery(id+"F3.wireOp",EDGE,"E1757"),sQuery(id+"F3.wireOp",EDGE,"E1758"),sQuery(id+"F3.wireOp",EDGE,"E1759"),sQuery(id+"F3.wireOp",EDGE,"E1780.0.0"),sQuery(id+"F3.wireOp",EDGE,"E1780.0.1"),sQuery(id+"F3.wireOp",EDGE,"E1780.0.2"),sQuery(id+"F3.wireOp",EDGE,"E1780.0.3"),sQuery(id+"F3.wireOp",EDGE,"E1780.0.4"),sQuery(id+"F3.wireOp",EDGE,"E1780.0.5"),sQuery(id+"F3.wireOp",EDGE,"E1780.0.6"),sQuery(id+"F3.wireOp",EDGE,"E1780.0.7"),sQuery(id+"F3.wireOp",EDGE,"E1780.0.8"),sQuery(id+"F3.wireOp",EDGE,"E1780.0.9"),sQuery(id+"F3.wireOp",EDGE,"E1780.0.10"),sQuery(id+"F3.wireOp",EDGE,"E1780.0.11"),sQuery(id+"F3.wireOp",EDGE,"E1780.0.12"),sQuery(id+"F3.wireOp",EDGE,"E1780.0.13"),sQuery(id+"F3.wireOp",EDGE,"E1780.0.14"),sQuery(id+"F3.wireOp",EDGE,"E1780.0.15"),sQuery(id+"F3.wireOp",EDGE,"E1780.0.16"),sQuery(id+"F3.wireOp",EDGE,"E1780.0.17"),sQuery(id+"F3.wireOp",EDGE,"E1780.0.18"),sQuery(id+"F3.wireOp",EDGE,"E1780.0.19"),sQuery(id+"F3.wireOp",EDGE,"E1780.0.20"),sQuery(id+"F3.wireOp",EDGE,"E1780.0.21"),sQuery(id+"F3.wireOp",EDGE,"E1780.0.22"),sQuery(id+"F3.wireOp",EDGE,"E1780.0.23"),sQuery(id+"F3.wireOp",EDGE,"E1780.0.24"),sQuery(id+"F3.wireOp",EDGE,"E1780.0.25"),sQuery(id+"F3.wireOp",EDGE,"E1780.0.26"),sQuery(id+"F3.wireOp",EDGE,"E1780.0.27"),sQuery(id+"F3.wireOp",EDGE,"E1780.0.28"),sQuery(id+"F3.wireOp",EDGE,"E1780.0.29"),sQuery(id+"F3.wireOp",EDGE,"E1780.0.30"),sQuery(id+"F3.wireOp",EDGE,"E1780.0.31"),sQuery(id+"F3.wireOp",EDGE,"E1780.0.32"),sQuery(id+"F3.wireOp",EDGE,"E1780.0.33"),sQuery(id+"F3.wireOp",EDGE,"E1780.0.34"),sQuery(id+"F3.wireOp",EDGE,"E1780.0.35"),sQuery(id+"F3.wireOp",EDGE,"E1780.0.36"),sQuery(id+"F3.wireOp",EDGE,"E1780.0.37"),sQuery(id+"F3.wireOp",EDGE,"E1780.0.38"),sQuery(id+"F3.wireOp",EDGE,"E1780.0.39"),sQuery(id+"F3.wireOp",EDGE,"E1780.0.40"),sQuery(id+"F3.wireOp",EDGE,"E1780.0.41"),sQuery(id+"F3.wireOp",EDGE,"E1780.0.42"),sQuery(id+"F3.wireOp",EDGE,"E1780.0.43"),sQuery(id+"F3.wireOp",EDGE,"E1780.0.44"),sQuery(id+"F3.wireOp",EDGE,"E1780.0.45"),sQuery(id+"F3.wireOp",EDGE,"E1780.0.46"),sQuery(id+"F3.wireOp",EDGE,"E1780.0.47"),sQuery(id+"F3.wireOp",EDGE,"E1780.0.48"),sQuery(id+"F3.wireOp",EDGE,"E1780.0.49"),sQuery(id+"F3.wireOp",EDGE,"E1780.0.50"),sQuery(id+"F3.wireOp",EDGE,"E1780.0.51"),sQuery(id+"F3.wireOp",EDGE,"E1780.0.52"),sQuery(id+"F3.wireOp",EDGE,"E1780.0.53"),sQuery(id+"F3.wireOp",EDGE,"E1780.0.54"),sQuery(id+"F3.wireOp",EDGE,"E1780.0.55")])],"isStart":false});
            var sketch = newSketch(context, id + "F5", { "sketchPlane" : qUnion([Q0])});
            skCircle(sketch, "E1781", {"center": v(0, 0) * mm, "radius": 34.27 * mm});
            skCircle(sketch, "E1782", {"center": v(0, 0) * mm, "radius": 27.27 * mm});
            skSolve(sketch);
        }
        {
            var Q0;
            Q0 = qSketchRegion(id + "F5", true);
            var Q1;
            Q1=makeQuery(id+"F5.imprint","IMPRINT",FACE,{"disambiguationData":[TD([[makeQuery(id+"F5.imprint","IMPRINT",EDGE,{"derivedFrom":sQuery(id+"F5.wireOp",EDGE,"E1782")}),1.0]])]});
            extrude(context, id + "F6", {"entities" : qUnion([Q0, Q1]), "operationType" : NewBodyOperationType.ADD, "oppositeDirection" : true, "depth" : (getVariable(context, 'idlerThick')) * mm, "offsetDistance" : 25 * mm});
        }
        {
            var Q0;
            Q0=makeQuery(id+"F4.opExtrude","CAP_FACE",FACE,{"disambiguationData":[OSD([sQuery(id+"F3.wireOp",EDGE,"E0"),sQuery(id+"F3.wireOp",EDGE,"E1"),sQuery(id+"F3.wireOp",EDGE,"E2"),sQuery(id+"F3.wireOp",EDGE,"E3"),sQuery(id+"F3.wireOp",EDGE,"E4"),sQuery(id+"F3.wireOp",EDGE,"E5"),sQuery(id+"F3.wireOp",EDGE,"E6"),sQuery(id+"F3.wireOp",EDGE,"E7"),sQuery(id+"F3.wireOp",EDGE,"E8"),sQuery(id+"F3.wireOp",EDGE,"E9"),sQuery(id+"F3.wireOp",EDGE,"E10"),sQuery(id+"F3.wireOp",EDGE,"E11"),sQuery(id+"F3.wireOp",EDGE,"E12"),sQuery(id+"F3.wireOp",EDGE,"E13"),sQuery(id+"F3.wireOp",EDGE,"E14"),sQuery(id+"F3.wireOp",EDGE,"E15"),sQuery(id+"F3.wireOp",EDGE,"E16"),sQuery(id+"F3.wireOp",EDGE,"E17"),sQuery(id+"F3.wireOp",EDGE,"E18"),sQuery(id+"F3.wireOp",EDGE,"E19"),sQuery(id+"F3.wireOp",EDGE,"E20"),sQuery(id+"F3.wireOp",EDGE,"E21"),sQuery(id+"F3.wireOp",EDGE,"E22"),sQuery(id+"F3.wireOp",EDGE,"E23"),sQuery(id+"F3.wireOp",EDGE,"E24"),sQuery(id+"F3.wireOp",EDGE,"E25"),sQuery(id+"F3.wireOp",EDGE,"E26"),sQuery(id+"F3.wireOp",EDGE,"E27"),sQuery(id+"F3.wireOp",EDGE,"E28"),sQuery(id+"F3.wireOp",EDGE,"E29"),sQuery(id+"F3.wireOp",EDGE,"E30"),sQuery(id+"F3.wireOp",EDGE,"E31"),sQuery(id+"F3.wireOp",EDGE,"E32"),sQuery(id+"F3.wireOp",EDGE,"E33"),sQuery(id+"F3.wireOp",EDGE,"E34"),sQuery(id+"F3.wireOp",EDGE,"E35"),sQuery(id+"F3.wireOp",EDGE,"E36"),sQuery(id+"F3.wireOp",EDGE,"E37"),sQuery(id+"F3.wireOp",EDGE,"E38"),sQuery(id+"F3.wireOp",EDGE,"E39"),sQuery(id+"F3.wireOp",EDGE,"E40"),sQuery(id+"F3.wireOp",EDGE,"E41"),sQuery(id+"F3.wireOp",EDGE,"E42"),sQuery(id+"F3.wireOp",EDGE,"E43"),sQuery(id+"F3.wireOp",EDGE,"E44"),sQuery(id+"F3.wireOp",EDGE,"E45"),sQuery(id+"F3.wireOp",EDGE,"E46"),sQuery(id+"F3.wireOp",EDGE,"E47"),sQuery(id+"F3.wireOp",EDGE,"E48"),sQuery(id+"F3.wireOp",EDGE,"E49"),sQuery(id+"F3.wireOp",EDGE,"E50"),sQuery(id+"F3.wireOp",EDGE,"E51"),sQuery(id+"F3.wireOp",EDGE,"E52"),sQuery(id+"F3.wireOp",EDGE,"E53"),sQuery(id+"F3.wireOp",EDGE,"E54"),sQuery(id+"F3.wireOp",EDGE,"E55"),sQuery(id+"F3.wireOp",EDGE,"E56"),sQuery(id+"F3.wireOp",EDGE,"E57"),sQuery(id+"F3.wireOp",EDGE,"E58"),sQuery(id+"F3.wireOp",EDGE,"E59"),sQuery(id+"F3.wireOp",EDGE,"E60"),sQuery(id+"F3.wireOp",EDGE,"E61"),sQuery(id+"F3.wireOp",EDGE,"E62"),sQuery(id+"F3.wireOp",EDGE,"E63"),sQuery(id+"F3.wireOp",EDGE,"E64"),sQuery(id+"F3.wireOp",EDGE,"E65"),sQuery(id+"F3.wireOp",EDGE,"E66"),sQuery(id+"F3.wireOp",EDGE,"E67"),sQuery(id+"F3.wireOp",EDGE,"E68"),sQuery(id+"F3.wireOp",EDGE,"E69"),sQuery(id+"F3.wireOp",EDGE,"E70"),sQuery(id+"F3.wireOp",EDGE,"E71"),sQuery(id+"F3.wireOp",EDGE,"E72"),sQuery(id+"F3.wireOp",EDGE,"E73"),sQuery(id+"F3.wireOp",EDGE,"E74"),sQuery(id+"F3.wireOp",EDGE,"E75"),sQuery(id+"F3.wireOp",EDGE,"E76"),sQuery(id+"F3.wireOp",EDGE,"E77"),sQuery(id+"F3.wireOp",EDGE,"E78"),sQuery(id+"F3.wireOp",EDGE,"E79"),sQuery(id+"F3.wireOp",EDGE,"E80"),sQuery(id+"F3.wireOp",EDGE,"E81"),sQuery(id+"F3.wireOp",EDGE,"E82"),sQuery(id+"F3.wireOp",EDGE,"E83"),sQuery(id+"F3.wireOp",EDGE,"E84"),sQuery(id+"F3.wireOp",EDGE,"E85"),sQuery(id+"F3.wireOp",EDGE,"E86"),sQuery(id+"F3.wireOp",EDGE,"E87"),sQuery(id+"F3.wireOp",EDGE,"E88"),sQuery(id+"F3.wireOp",EDGE,"E89"),sQuery(id+"F3.wireOp",EDGE,"E90"),sQuery(id+"F3.wireOp",EDGE,"E91"),sQuery(id+"F3.wireOp",EDGE,"E92"),sQuery(id+"F3.wireOp",EDGE,"E93"),sQuery(id+"F3.wireOp",EDGE,"E94"),sQuery(id+"F3.wireOp",EDGE,"E95"),sQuery(id+"F3.wireOp",EDGE,"E96"),sQuery(id+"F3.wireOp",EDGE,"E97"),sQuery(id+"F3.wireOp",EDGE,"E98"),sQuery(id+"F3.wireOp",EDGE,"E99"),sQuery(id+"F3.wireOp",EDGE,"E100"),sQuery(id+"F3.wireOp",EDGE,"E101"),sQuery(id+"F3.wireOp",EDGE,"E102"),sQuery(id+"F3.wireOp",EDGE,"E103"),sQuery(id+"F3.wireOp",EDGE,"E104"),sQuery(id+"F3.wireOp",EDGE,"E105"),sQuery(id+"F3.wireOp",EDGE,"E106"),sQuery(id+"F3.wireOp",EDGE,"E107"),sQuery(id+"F3.wireOp",EDGE,"E108"),sQuery(id+"F3.wireOp",EDGE,"E109"),sQuery(id+"F3.wireOp",EDGE,"E110"),sQuery(id+"F3.wireOp",EDGE,"E111"),sQuery(id+"F3.wireOp",EDGE,"E112"),sQuery(id+"F3.wireOp",EDGE,"E113"),sQuery(id+"F3.wireOp",EDGE,"E114"),sQuery(id+"F3.wireOp",EDGE,"E115"),sQuery(id+"F3.wireOp",EDGE,"E116"),sQuery(id+"F3.wireOp",EDGE,"E117"),sQuery(id+"F3.wireOp",EDGE,"E118"),sQuery(id+"F3.wireOp",EDGE,"E119"),sQuery(id+"F3.wireOp",EDGE,"E120"),sQuery(id+"F3.wireOp",EDGE,"E121"),sQuery(id+"F3.wireOp",EDGE,"E122"),sQuery(id+"F3.wireOp",EDGE,"E123"),sQuery(id+"F3.wireOp",EDGE,"E124"),sQuery(id+"F3.wireOp",EDGE,"E125"),sQuery(id+"F3.wireOp",EDGE,"E126"),sQuery(id+"F3.wireOp",EDGE,"E127"),sQuery(id+"F3.wireOp",EDGE,"E128"),sQuery(id+"F3.wireOp",EDGE,"E129"),sQuery(id+"F3.wireOp",EDGE,"E130"),sQuery(id+"F3.wireOp",EDGE,"E131"),sQuery(id+"F3.wireOp",EDGE,"E132"),sQuery(id+"F3.wireOp",EDGE,"E133"),sQuery(id+"F3.wireOp",EDGE,"E134"),sQuery(id+"F3.wireOp",EDGE,"E135"),sQuery(id+"F3.wireOp",EDGE,"E136"),sQuery(id+"F3.wireOp",EDGE,"E137"),sQuery(id+"F3.wireOp",EDGE,"E138"),sQuery(id+"F3.wireOp",EDGE,"E139"),sQuery(id+"F3.wireOp",EDGE,"E140"),sQuery(id+"F3.wireOp",EDGE,"E141"),sQuery(id+"F3.wireOp",EDGE,"E142"),sQuery(id+"F3.wireOp",EDGE,"E143"),sQuery(id+"F3.wireOp",EDGE,"E144"),sQuery(id+"F3.wireOp",EDGE,"E145"),sQuery(id+"F3.wireOp",EDGE,"E146"),sQuery(id+"F3.wireOp",EDGE,"E147"),sQuery(id+"F3.wireOp",EDGE,"E148"),sQuery(id+"F3.wireOp",EDGE,"E149"),sQuery(id+"F3.wireOp",EDGE,"E150"),sQuery(id+"F3.wireOp",EDGE,"E151"),sQuery(id+"F3.wireOp",EDGE,"E152"),sQuery(id+"F3.wireOp",EDGE,"E153"),sQuery(id+"F3.wireOp",EDGE,"E154"),sQuery(id+"F3.wireOp",EDGE,"E155"),sQuery(id+"F3.wireOp",EDGE,"E156"),sQuery(id+"F3.wireOp",EDGE,"E157"),sQuery(id+"F3.wireOp",EDGE,"E158"),sQuery(id+"F3.wireOp",EDGE,"E159"),sQuery(id+"F3.wireOp",EDGE,"E160"),sQuery(id+"F3.wireOp",EDGE,"E161"),sQuery(id+"F3.wireOp",EDGE,"E162"),sQuery(id+"F3.wireOp",EDGE,"E163"),sQuery(id+"F3.wireOp",EDGE,"E164"),sQuery(id+"F3.wireOp",EDGE,"E165"),sQuery(id+"F3.wireOp",EDGE,"E166"),sQuery(id+"F3.wireOp",EDGE,"E167"),sQuery(id+"F3.wireOp",EDGE,"E168"),sQuery(id+"F3.wireOp",EDGE,"E169"),sQuery(id+"F3.wireOp",EDGE,"E170"),sQuery(id+"F3.wireOp",EDGE,"E171"),sQuery(id+"F3.wireOp",EDGE,"E172"),sQuery(id+"F3.wireOp",EDGE,"E173"),sQuery(id+"F3.wireOp",EDGE,"E174"),sQuery(id+"F3.wireOp",EDGE,"E175"),sQuery(id+"F3.wireOp",EDGE,"E176"),sQuery(id+"F3.wireOp",EDGE,"E177"),sQuery(id+"F3.wireOp",EDGE,"E178"),sQuery(id+"F3.wireOp",EDGE,"E179"),sQuery(id+"F3.wireOp",EDGE,"E180"),sQuery(id+"F3.wireOp",EDGE,"E181"),sQuery(id+"F3.wireOp",EDGE,"E182"),sQuery(id+"F3.wireOp",EDGE,"E183"),sQuery(id+"F3.wireOp",EDGE,"E184"),sQuery(id+"F3.wireOp",EDGE,"E185"),sQuery(id+"F3.wireOp",EDGE,"E186"),sQuery(id+"F3.wireOp",EDGE,"E187"),sQuery(id+"F3.wireOp",EDGE,"E188"),sQuery(id+"F3.wireOp",EDGE,"E189"),sQuery(id+"F3.wireOp",EDGE,"E190"),sQuery(id+"F3.wireOp",EDGE,"E191"),sQuery(id+"F3.wireOp",EDGE,"E192"),sQuery(id+"F3.wireOp",EDGE,"E193"),sQuery(id+"F3.wireOp",EDGE,"E194"),sQuery(id+"F3.wireOp",EDGE,"E195"),sQuery(id+"F3.wireOp",EDGE,"E196"),sQuery(id+"F3.wireOp",EDGE,"E197"),sQuery(id+"F3.wireOp",EDGE,"E198"),sQuery(id+"F3.wireOp",EDGE,"E199"),sQuery(id+"F3.wireOp",EDGE,"E200"),sQuery(id+"F3.wireOp",EDGE,"E201"),sQuery(id+"F3.wireOp",EDGE,"E202"),sQuery(id+"F3.wireOp",EDGE,"E203"),sQuery(id+"F3.wireOp",EDGE,"E204"),sQuery(id+"F3.wireOp",EDGE,"E205"),sQuery(id+"F3.wireOp",EDGE,"E206"),sQuery(id+"F3.wireOp",EDGE,"E207"),sQuery(id+"F3.wireOp",EDGE,"E208"),sQuery(id+"F3.wireOp",EDGE,"E209"),sQuery(id+"F3.wireOp",EDGE,"E210"),sQuery(id+"F3.wireOp",EDGE,"E211"),sQuery(id+"F3.wireOp",EDGE,"E212"),sQuery(id+"F3.wireOp",EDGE,"E213"),sQuery(id+"F3.wireOp",EDGE,"E214"),sQuery(id+"F3.wireOp",EDGE,"E215"),sQuery(id+"F3.wireOp",EDGE,"E216"),sQuery(id+"F3.wireOp",EDGE,"E217"),sQuery(id+"F3.wireOp",EDGE,"E218"),sQuery(id+"F3.wireOp",EDGE,"E219"),sQuery(id+"F3.wireOp",EDGE,"E220"),sQuery(id+"F3.wireOp",EDGE,"E221"),sQuery(id+"F3.wireOp",EDGE,"E222"),sQuery(id+"F3.wireOp",EDGE,"E223"),sQuery(id+"F3.wireOp",EDGE,"E224"),sQuery(id+"F3.wireOp",EDGE,"E225"),sQuery(id+"F3.wireOp",EDGE,"E226"),sQuery(id+"F3.wireOp",EDGE,"E227"),sQuery(id+"F3.wireOp",EDGE,"E228"),sQuery(id+"F3.wireOp",EDGE,"E229"),sQuery(id+"F3.wireOp",EDGE,"E230"),sQuery(id+"F3.wireOp",EDGE,"E231"),sQuery(id+"F3.wireOp",EDGE,"E232"),sQuery(id+"F3.wireOp",EDGE,"E233"),sQuery(id+"F3.wireOp",EDGE,"E234"),sQuery(id+"F3.wireOp",EDGE,"E235"),sQuery(id+"F3.wireOp",EDGE,"E236"),sQuery(id+"F3.wireOp",EDGE,"E237"),sQuery(id+"F3.wireOp",EDGE,"E238"),sQuery(id+"F3.wireOp",EDGE,"E239"),sQuery(id+"F3.wireOp",EDGE,"E240"),sQuery(id+"F3.wireOp",EDGE,"E241"),sQuery(id+"F3.wireOp",EDGE,"E242"),sQuery(id+"F3.wireOp",EDGE,"E243"),sQuery(id+"F3.wireOp",EDGE,"E244"),sQuery(id+"F3.wireOp",EDGE,"E245"),sQuery(id+"F3.wireOp",EDGE,"E246"),sQuery(id+"F3.wireOp",EDGE,"E247"),sQuery(id+"F3.wireOp",EDGE,"E248"),sQuery(id+"F3.wireOp",EDGE,"E249"),sQuery(id+"F3.wireOp",EDGE,"E250"),sQuery(id+"F3.wireOp",EDGE,"E251"),sQuery(id+"F3.wireOp",EDGE,"E252"),sQuery(id+"F3.wireOp",EDGE,"E253"),sQuery(id+"F3.wireOp",EDGE,"E254"),sQuery(id+"F3.wireOp",EDGE,"E255"),sQuery(id+"F3.wireOp",EDGE,"E256"),sQuery(id+"F3.wireOp",EDGE,"E257"),sQuery(id+"F3.wireOp",EDGE,"E258"),sQuery(id+"F3.wireOp",EDGE,"E259"),sQuery(id+"F3.wireOp",EDGE,"E260"),sQuery(id+"F3.wireOp",EDGE,"E261"),sQuery(id+"F3.wireOp",EDGE,"E262"),sQuery(id+"F3.wireOp",EDGE,"E263"),sQuery(id+"F3.wireOp",EDGE,"E264"),sQuery(id+"F3.wireOp",EDGE,"E265"),sQuery(id+"F3.wireOp",EDGE,"E266"),sQuery(id+"F3.wireOp",EDGE,"E267"),sQuery(id+"F3.wireOp",EDGE,"E268"),sQuery(id+"F3.wireOp",EDGE,"E269"),sQuery(id+"F3.wireOp",EDGE,"E270"),sQuery(id+"F3.wireOp",EDGE,"E271"),sQuery(id+"F3.wireOp",EDGE,"E272"),sQuery(id+"F3.wireOp",EDGE,"E273"),sQuery(id+"F3.wireOp",EDGE,"E274"),sQuery(id+"F3.wireOp",EDGE,"E275"),sQuery(id+"F3.wireOp",EDGE,"E276"),sQuery(id+"F3.wireOp",EDGE,"E277"),sQuery(id+"F3.wireOp",EDGE,"E278"),sQuery(id+"F3.wireOp",EDGE,"E279"),sQuery(id+"F3.wireOp",EDGE,"E280"),sQuery(id+"F3.wireOp",EDGE,"E281"),sQuery(id+"F3.wireOp",EDGE,"E282"),sQuery(id+"F3.wireOp",EDGE,"E283"),sQuery(id+"F3.wireOp",EDGE,"E284"),sQuery(id+"F3.wireOp",EDGE,"E285"),sQuery(id+"F3.wireOp",EDGE,"E286"),sQuery(id+"F3.wireOp",EDGE,"E287"),sQuery(id+"F3.wireOp",EDGE,"E288"),sQuery(id+"F3.wireOp",EDGE,"E289"),sQuery(id+"F3.wireOp",EDGE,"E290"),sQuery(id+"F3.wireOp",EDGE,"E291"),sQuery(id+"F3.wireOp",EDGE,"E292"),sQuery(id+"F3.wireOp",EDGE,"E293"),sQuery(id+"F3.wireOp",EDGE,"E294"),sQuery(id+"F3.wireOp",EDGE,"E295"),sQuery(id+"F3.wireOp",EDGE,"E296"),sQuery(id+"F3.wireOp",EDGE,"E297"),sQuery(id+"F3.wireOp",EDGE,"E298"),sQuery(id+"F3.wireOp",EDGE,"E299"),sQuery(id+"F3.wireOp",EDGE,"E300"),sQuery(id+"F3.wireOp",EDGE,"E301"),sQuery(id+"F3.wireOp",EDGE,"E302"),sQuery(id+"F3.wireOp",EDGE,"E303"),sQuery(id+"F3.wireOp",EDGE,"E304"),sQuery(id+"F3.wireOp",EDGE,"E305"),sQuery(id+"F3.wireOp",EDGE,"E306"),sQuery(id+"F3.wireOp",EDGE,"E307"),sQuery(id+"F3.wireOp",EDGE,"E308"),sQuery(id+"F3.wireOp",EDGE,"E309"),sQuery(id+"F3.wireOp",EDGE,"E310"),sQuery(id+"F3.wireOp",EDGE,"E311"),sQuery(id+"F3.wireOp",EDGE,"E312"),sQuery(id+"F3.wireOp",EDGE,"E313"),sQuery(id+"F3.wireOp",EDGE,"E314"),sQuery(id+"F3.wireOp",EDGE,"E315"),sQuery(id+"F3.wireOp",EDGE,"E316"),sQuery(id+"F3.wireOp",EDGE,"E317"),sQuery(id+"F3.wireOp",EDGE,"E318"),sQuery(id+"F3.wireOp",EDGE,"E319"),sQuery(id+"F3.wireOp",EDGE,"E320"),sQuery(id+"F3.wireOp",EDGE,"E321"),sQuery(id+"F3.wireOp",EDGE,"E322"),sQuery(id+"F3.wireOp",EDGE,"E323"),sQuery(id+"F3.wireOp",EDGE,"E324"),sQuery(id+"F3.wireOp",EDGE,"E325"),sQuery(id+"F3.wireOp",EDGE,"E326"),sQuery(id+"F3.wireOp",EDGE,"E327"),sQuery(id+"F3.wireOp",EDGE,"E328"),sQuery(id+"F3.wireOp",EDGE,"E329"),sQuery(id+"F3.wireOp",EDGE,"E330"),sQuery(id+"F3.wireOp",EDGE,"E331"),sQuery(id+"F3.wireOp",EDGE,"E332"),sQuery(id+"F3.wireOp",EDGE,"E333"),sQuery(id+"F3.wireOp",EDGE,"E334"),sQuery(id+"F3.wireOp",EDGE,"E335"),sQuery(id+"F3.wireOp",EDGE,"E336"),sQuery(id+"F3.wireOp",EDGE,"E337"),sQuery(id+"F3.wireOp",EDGE,"E338"),sQuery(id+"F3.wireOp",EDGE,"E339"),sQuery(id+"F3.wireOp",EDGE,"E340"),sQuery(id+"F3.wireOp",EDGE,"E341"),sQuery(id+"F3.wireOp",EDGE,"E342"),sQuery(id+"F3.wireOp",EDGE,"E343"),sQuery(id+"F3.wireOp",EDGE,"E344"),sQuery(id+"F3.wireOp",EDGE,"E345"),sQuery(id+"F3.wireOp",EDGE,"E346"),sQuery(id+"F3.wireOp",EDGE,"E347"),sQuery(id+"F3.wireOp",EDGE,"E348"),sQuery(id+"F3.wireOp",EDGE,"E349"),sQuery(id+"F3.wireOp",EDGE,"E350"),sQuery(id+"F3.wireOp",EDGE,"E351"),sQuery(id+"F3.wireOp",EDGE,"E352"),sQuery(id+"F3.wireOp",EDGE,"E353"),sQuery(id+"F3.wireOp",EDGE,"E354"),sQuery(id+"F3.wireOp",EDGE,"E355"),sQuery(id+"F3.wireOp",EDGE,"E356"),sQuery(id+"F3.wireOp",EDGE,"E357"),sQuery(id+"F3.wireOp",EDGE,"E358"),sQuery(id+"F3.wireOp",EDGE,"E359"),sQuery(id+"F3.wireOp",EDGE,"E360"),sQuery(id+"F3.wireOp",EDGE,"E361"),sQuery(id+"F3.wireOp",EDGE,"E362"),sQuery(id+"F3.wireOp",EDGE,"E363"),sQuery(id+"F3.wireOp",EDGE,"E364"),sQuery(id+"F3.wireOp",EDGE,"E365"),sQuery(id+"F3.wireOp",EDGE,"E366"),sQuery(id+"F3.wireOp",EDGE,"E367"),sQuery(id+"F3.wireOp",EDGE,"E368"),sQuery(id+"F3.wireOp",EDGE,"E369"),sQuery(id+"F3.wireOp",EDGE,"E370"),sQuery(id+"F3.wireOp",EDGE,"E371"),sQuery(id+"F3.wireOp",EDGE,"E372"),sQuery(id+"F3.wireOp",EDGE,"E373"),sQuery(id+"F3.wireOp",EDGE,"E374"),sQuery(id+"F3.wireOp",EDGE,"E375"),sQuery(id+"F3.wireOp",EDGE,"E376"),sQuery(id+"F3.wireOp",EDGE,"E377"),sQuery(id+"F3.wireOp",EDGE,"E378"),sQuery(id+"F3.wireOp",EDGE,"E379"),sQuery(id+"F3.wireOp",EDGE,"E380"),sQuery(id+"F3.wireOp",EDGE,"E381"),sQuery(id+"F3.wireOp",EDGE,"E382"),sQuery(id+"F3.wireOp",EDGE,"E383"),sQuery(id+"F3.wireOp",EDGE,"E384"),sQuery(id+"F3.wireOp",EDGE,"E385"),sQuery(id+"F3.wireOp",EDGE,"E386"),sQuery(id+"F3.wireOp",EDGE,"E387"),sQuery(id+"F3.wireOp",EDGE,"E388"),sQuery(id+"F3.wireOp",EDGE,"E389"),sQuery(id+"F3.wireOp",EDGE,"E390"),sQuery(id+"F3.wireOp",EDGE,"E391"),sQuery(id+"F3.wireOp",EDGE,"E392"),sQuery(id+"F3.wireOp",EDGE,"E393"),sQuery(id+"F3.wireOp",EDGE,"E394"),sQuery(id+"F3.wireOp",EDGE,"E395"),sQuery(id+"F3.wireOp",EDGE,"E396"),sQuery(id+"F3.wireOp",EDGE,"E397"),sQuery(id+"F3.wireOp",EDGE,"E398"),sQuery(id+"F3.wireOp",EDGE,"E399"),sQuery(id+"F3.wireOp",EDGE,"E400"),sQuery(id+"F3.wireOp",EDGE,"E401"),sQuery(id+"F3.wireOp",EDGE,"E402"),sQuery(id+"F3.wireOp",EDGE,"E403"),sQuery(id+"F3.wireOp",EDGE,"E404"),sQuery(id+"F3.wireOp",EDGE,"E405"),sQuery(id+"F3.wireOp",EDGE,"E406"),sQuery(id+"F3.wireOp",EDGE,"E407"),sQuery(id+"F3.wireOp",EDGE,"E408"),sQuery(id+"F3.wireOp",EDGE,"E409"),sQuery(id+"F3.wireOp",EDGE,"E410"),sQuery(id+"F3.wireOp",EDGE,"E411"),sQuery(id+"F3.wireOp",EDGE,"E412"),sQuery(id+"F3.wireOp",EDGE,"E413"),sQuery(id+"F3.wireOp",EDGE,"E414"),sQuery(id+"F3.wireOp",EDGE,"E415"),sQuery(id+"F3.wireOp",EDGE,"E416"),sQuery(id+"F3.wireOp",EDGE,"E417"),sQuery(id+"F3.wireOp",EDGE,"E418"),sQuery(id+"F3.wireOp",EDGE,"E419"),sQuery(id+"F3.wireOp",EDGE,"E420"),sQuery(id+"F3.wireOp",EDGE,"E421"),sQuery(id+"F3.wireOp",EDGE,"E422"),sQuery(id+"F3.wireOp",EDGE,"E423"),sQuery(id+"F3.wireOp",EDGE,"E424"),sQuery(id+"F3.wireOp",EDGE,"E425"),sQuery(id+"F3.wireOp",EDGE,"E426"),sQuery(id+"F3.wireOp",EDGE,"E427"),sQuery(id+"F3.wireOp",EDGE,"E428"),sQuery(id+"F3.wireOp",EDGE,"E429"),sQuery(id+"F3.wireOp",EDGE,"E430"),sQuery(id+"F3.wireOp",EDGE,"E431"),sQuery(id+"F3.wireOp",EDGE,"E432"),sQuery(id+"F3.wireOp",EDGE,"E433"),sQuery(id+"F3.wireOp",EDGE,"E434"),sQuery(id+"F3.wireOp",EDGE,"E435"),sQuery(id+"F3.wireOp",EDGE,"E436"),sQuery(id+"F3.wireOp",EDGE,"E437"),sQuery(id+"F3.wireOp",EDGE,"E438"),sQuery(id+"F3.wireOp",EDGE,"E439"),sQuery(id+"F3.wireOp",EDGE,"E440"),sQuery(id+"F3.wireOp",EDGE,"E441"),sQuery(id+"F3.wireOp",EDGE,"E442"),sQuery(id+"F3.wireOp",EDGE,"E443"),sQuery(id+"F3.wireOp",EDGE,"E444"),sQuery(id+"F3.wireOp",EDGE,"E445"),sQuery(id+"F3.wireOp",EDGE,"E446"),sQuery(id+"F3.wireOp",EDGE,"E447"),sQuery(id+"F3.wireOp",EDGE,"E448"),sQuery(id+"F3.wireOp",EDGE,"E449"),sQuery(id+"F3.wireOp",EDGE,"E450"),sQuery(id+"F3.wireOp",EDGE,"E451"),sQuery(id+"F3.wireOp",EDGE,"E452"),sQuery(id+"F3.wireOp",EDGE,"E453"),sQuery(id+"F3.wireOp",EDGE,"E454"),sQuery(id+"F3.wireOp",EDGE,"E455"),sQuery(id+"F3.wireOp",EDGE,"E456"),sQuery(id+"F3.wireOp",EDGE,"E457"),sQuery(id+"F3.wireOp",EDGE,"E458"),sQuery(id+"F3.wireOp",EDGE,"E459"),sQuery(id+"F3.wireOp",EDGE,"E460"),sQuery(id+"F3.wireOp",EDGE,"E461"),sQuery(id+"F3.wireOp",EDGE,"E462"),sQuery(id+"F3.wireOp",EDGE,"E463"),sQuery(id+"F3.wireOp",EDGE,"E464"),sQuery(id+"F3.wireOp",EDGE,"E465"),sQuery(id+"F3.wireOp",EDGE,"E466"),sQuery(id+"F3.wireOp",EDGE,"E467"),sQuery(id+"F3.wireOp",EDGE,"E468"),sQuery(id+"F3.wireOp",EDGE,"E469"),sQuery(id+"F3.wireOp",EDGE,"E470"),sQuery(id+"F3.wireOp",EDGE,"E471"),sQuery(id+"F3.wireOp",EDGE,"E472"),sQuery(id+"F3.wireOp",EDGE,"E473"),sQuery(id+"F3.wireOp",EDGE,"E474"),sQuery(id+"F3.wireOp",EDGE,"E475"),sQuery(id+"F3.wireOp",EDGE,"E476"),sQuery(id+"F3.wireOp",EDGE,"E477"),sQuery(id+"F3.wireOp",EDGE,"E478"),sQuery(id+"F3.wireOp",EDGE,"E479"),sQuery(id+"F3.wireOp",EDGE,"E480"),sQuery(id+"F3.wireOp",EDGE,"E481"),sQuery(id+"F3.wireOp",EDGE,"E482"),sQuery(id+"F3.wireOp",EDGE,"E483"),sQuery(id+"F3.wireOp",EDGE,"E484"),sQuery(id+"F3.wireOp",EDGE,"E485"),sQuery(id+"F3.wireOp",EDGE,"E486"),sQuery(id+"F3.wireOp",EDGE,"E487"),sQuery(id+"F3.wireOp",EDGE,"E488"),sQuery(id+"F3.wireOp",EDGE,"E489"),sQuery(id+"F3.wireOp",EDGE,"E490"),sQuery(id+"F3.wireOp",EDGE,"E491"),sQuery(id+"F3.wireOp",EDGE,"E492"),sQuery(id+"F3.wireOp",EDGE,"E493"),sQuery(id+"F3.wireOp",EDGE,"E494"),sQuery(id+"F3.wireOp",EDGE,"E495"),sQuery(id+"F3.wireOp",EDGE,"E496"),sQuery(id+"F3.wireOp",EDGE,"E497"),sQuery(id+"F3.wireOp",EDGE,"E498"),sQuery(id+"F3.wireOp",EDGE,"E499"),sQuery(id+"F3.wireOp",EDGE,"E500"),sQuery(id+"F3.wireOp",EDGE,"E501"),sQuery(id+"F3.wireOp",EDGE,"E502"),sQuery(id+"F3.wireOp",EDGE,"E503"),sQuery(id+"F3.wireOp",EDGE,"E504"),sQuery(id+"F3.wireOp",EDGE,"E505"),sQuery(id+"F3.wireOp",EDGE,"E506"),sQuery(id+"F3.wireOp",EDGE,"E507"),sQuery(id+"F3.wireOp",EDGE,"E508"),sQuery(id+"F3.wireOp",EDGE,"E509"),sQuery(id+"F3.wireOp",EDGE,"E510"),sQuery(id+"F3.wireOp",EDGE,"E511"),sQuery(id+"F3.wireOp",EDGE,"E512"),sQuery(id+"F3.wireOp",EDGE,"E513"),sQuery(id+"F3.wireOp",EDGE,"E514"),sQuery(id+"F3.wireOp",EDGE,"E515"),sQuery(id+"F3.wireOp",EDGE,"E516"),sQuery(id+"F3.wireOp",EDGE,"E517"),sQuery(id+"F3.wireOp",EDGE,"E518"),sQuery(id+"F3.wireOp",EDGE,"E519"),sQuery(id+"F3.wireOp",EDGE,"E520"),sQuery(id+"F3.wireOp",EDGE,"E521"),sQuery(id+"F3.wireOp",EDGE,"E522"),sQuery(id+"F3.wireOp",EDGE,"E523"),sQuery(id+"F3.wireOp",EDGE,"E524"),sQuery(id+"F3.wireOp",EDGE,"E525"),sQuery(id+"F3.wireOp",EDGE,"E526"),sQuery(id+"F3.wireOp",EDGE,"E527"),sQuery(id+"F3.wireOp",EDGE,"E528"),sQuery(id+"F3.wireOp",EDGE,"E529"),sQuery(id+"F3.wireOp",EDGE,"E530"),sQuery(id+"F3.wireOp",EDGE,"E531"),sQuery(id+"F3.wireOp",EDGE,"E532"),sQuery(id+"F3.wireOp",EDGE,"E533"),sQuery(id+"F3.wireOp",EDGE,"E534"),sQuery(id+"F3.wireOp",EDGE,"E535"),sQuery(id+"F3.wireOp",EDGE,"E536"),sQuery(id+"F3.wireOp",EDGE,"E537"),sQuery(id+"F3.wireOp",EDGE,"E538"),sQuery(id+"F3.wireOp",EDGE,"E539"),sQuery(id+"F3.wireOp",EDGE,"E540"),sQuery(id+"F3.wireOp",EDGE,"E541"),sQuery(id+"F3.wireOp",EDGE,"E542"),sQuery(id+"F3.wireOp",EDGE,"E543"),sQuery(id+"F3.wireOp",EDGE,"E544"),sQuery(id+"F3.wireOp",EDGE,"E545"),sQuery(id+"F3.wireOp",EDGE,"E546"),sQuery(id+"F3.wireOp",EDGE,"E547"),sQuery(id+"F3.wireOp",EDGE,"E548"),sQuery(id+"F3.wireOp",EDGE,"E549"),sQuery(id+"F3.wireOp",EDGE,"E550"),sQuery(id+"F3.wireOp",EDGE,"E551"),sQuery(id+"F3.wireOp",EDGE,"E552"),sQuery(id+"F3.wireOp",EDGE,"E553"),sQuery(id+"F3.wireOp",EDGE,"E554"),sQuery(id+"F3.wireOp",EDGE,"E555"),sQuery(id+"F3.wireOp",EDGE,"E556"),sQuery(id+"F3.wireOp",EDGE,"E557"),sQuery(id+"F3.wireOp",EDGE,"E558"),sQuery(id+"F3.wireOp",EDGE,"E559"),sQuery(id+"F3.wireOp",EDGE,"E560"),sQuery(id+"F3.wireOp",EDGE,"E561"),sQuery(id+"F3.wireOp",EDGE,"E562"),sQuery(id+"F3.wireOp",EDGE,"E563"),sQuery(id+"F3.wireOp",EDGE,"E564"),sQuery(id+"F3.wireOp",EDGE,"E565"),sQuery(id+"F3.wireOp",EDGE,"E566"),sQuery(id+"F3.wireOp",EDGE,"E567"),sQuery(id+"F3.wireOp",EDGE,"E568"),sQuery(id+"F3.wireOp",EDGE,"E569"),sQuery(id+"F3.wireOp",EDGE,"E570"),sQuery(id+"F3.wireOp",EDGE,"E571"),sQuery(id+"F3.wireOp",EDGE,"E572"),sQuery(id+"F3.wireOp",EDGE,"E573"),sQuery(id+"F3.wireOp",EDGE,"E574"),sQuery(id+"F3.wireOp",EDGE,"E575"),sQuery(id+"F3.wireOp",EDGE,"E576"),sQuery(id+"F3.wireOp",EDGE,"E577"),sQuery(id+"F3.wireOp",EDGE,"E578"),sQuery(id+"F3.wireOp",EDGE,"E579"),sQuery(id+"F3.wireOp",EDGE,"E580"),sQuery(id+"F3.wireOp",EDGE,"E581"),sQuery(id+"F3.wireOp",EDGE,"E582"),sQuery(id+"F3.wireOp",EDGE,"E583"),sQuery(id+"F3.wireOp",EDGE,"E584"),sQuery(id+"F3.wireOp",EDGE,"E585"),sQuery(id+"F3.wireOp",EDGE,"E586"),sQuery(id+"F3.wireOp",EDGE,"E587"),sQuery(id+"F3.wireOp",EDGE,"E588"),sQuery(id+"F3.wireOp",EDGE,"E589"),sQuery(id+"F3.wireOp",EDGE,"E590"),sQuery(id+"F3.wireOp",EDGE,"E591"),sQuery(id+"F3.wireOp",EDGE,"E592"),sQuery(id+"F3.wireOp",EDGE,"E593"),sQuery(id+"F3.wireOp",EDGE,"E594"),sQuery(id+"F3.wireOp",EDGE,"E595"),sQuery(id+"F3.wireOp",EDGE,"E596"),sQuery(id+"F3.wireOp",EDGE,"E597"),sQuery(id+"F3.wireOp",EDGE,"E598"),sQuery(id+"F3.wireOp",EDGE,"E599"),sQuery(id+"F3.wireOp",EDGE,"E600"),sQuery(id+"F3.wireOp",EDGE,"E601"),sQuery(id+"F3.wireOp",EDGE,"E602"),sQuery(id+"F3.wireOp",EDGE,"E603"),sQuery(id+"F3.wireOp",EDGE,"E604"),sQuery(id+"F3.wireOp",EDGE,"E605"),sQuery(id+"F3.wireOp",EDGE,"E606"),sQuery(id+"F3.wireOp",EDGE,"E607"),sQuery(id+"F3.wireOp",EDGE,"E608"),sQuery(id+"F3.wireOp",EDGE,"E609"),sQuery(id+"F3.wireOp",EDGE,"E610"),sQuery(id+"F3.wireOp",EDGE,"E611"),sQuery(id+"F3.wireOp",EDGE,"E612"),sQuery(id+"F3.wireOp",EDGE,"E613"),sQuery(id+"F3.wireOp",EDGE,"E614"),sQuery(id+"F3.wireOp",EDGE,"E615"),sQuery(id+"F3.wireOp",EDGE,"E616"),sQuery(id+"F3.wireOp",EDGE,"E617"),sQuery(id+"F3.wireOp",EDGE,"E618"),sQuery(id+"F3.wireOp",EDGE,"E619"),sQuery(id+"F3.wireOp",EDGE,"E620"),sQuery(id+"F3.wireOp",EDGE,"E621"),sQuery(id+"F3.wireOp",EDGE,"E622"),sQuery(id+"F3.wireOp",EDGE,"E623"),sQuery(id+"F3.wireOp",EDGE,"E624"),sQuery(id+"F3.wireOp",EDGE,"E625"),sQuery(id+"F3.wireOp",EDGE,"E626"),sQuery(id+"F3.wireOp",EDGE,"E627"),sQuery(id+"F3.wireOp",EDGE,"E628"),sQuery(id+"F3.wireOp",EDGE,"E629"),sQuery(id+"F3.wireOp",EDGE,"E630"),sQuery(id+"F3.wireOp",EDGE,"E631"),sQuery(id+"F3.wireOp",EDGE,"E632"),sQuery(id+"F3.wireOp",EDGE,"E633"),sQuery(id+"F3.wireOp",EDGE,"E634"),sQuery(id+"F3.wireOp",EDGE,"E635"),sQuery(id+"F3.wireOp",EDGE,"E636"),sQuery(id+"F3.wireOp",EDGE,"E637"),sQuery(id+"F3.wireOp",EDGE,"E638"),sQuery(id+"F3.wireOp",EDGE,"E639"),sQuery(id+"F3.wireOp",EDGE,"E640"),sQuery(id+"F3.wireOp",EDGE,"E641"),sQuery(id+"F3.wireOp",EDGE,"E642"),sQuery(id+"F3.wireOp",EDGE,"E643"),sQuery(id+"F3.wireOp",EDGE,"E644"),sQuery(id+"F3.wireOp",EDGE,"E645"),sQuery(id+"F3.wireOp",EDGE,"E646"),sQuery(id+"F3.wireOp",EDGE,"E647"),sQuery(id+"F3.wireOp",EDGE,"E648"),sQuery(id+"F3.wireOp",EDGE,"E649"),sQuery(id+"F3.wireOp",EDGE,"E650"),sQuery(id+"F3.wireOp",EDGE,"E651"),sQuery(id+"F3.wireOp",EDGE,"E652"),sQuery(id+"F3.wireOp",EDGE,"E653"),sQuery(id+"F3.wireOp",EDGE,"E654"),sQuery(id+"F3.wireOp",EDGE,"E655"),sQuery(id+"F3.wireOp",EDGE,"E656"),sQuery(id+"F3.wireOp",EDGE,"E657"),sQuery(id+"F3.wireOp",EDGE,"E658"),sQuery(id+"F3.wireOp",EDGE,"E659"),sQuery(id+"F3.wireOp",EDGE,"E660"),sQuery(id+"F3.wireOp",EDGE,"E661"),sQuery(id+"F3.wireOp",EDGE,"E662"),sQuery(id+"F3.wireOp",EDGE,"E663"),sQuery(id+"F3.wireOp",EDGE,"E664"),sQuery(id+"F3.wireOp",EDGE,"E665"),sQuery(id+"F3.wireOp",EDGE,"E666"),sQuery(id+"F3.wireOp",EDGE,"E667"),sQuery(id+"F3.wireOp",EDGE,"E668"),sQuery(id+"F3.wireOp",EDGE,"E669"),sQuery(id+"F3.wireOp",EDGE,"E670"),sQuery(id+"F3.wireOp",EDGE,"E671"),sQuery(id+"F3.wireOp",EDGE,"E672"),sQuery(id+"F3.wireOp",EDGE,"E673"),sQuery(id+"F3.wireOp",EDGE,"E674"),sQuery(id+"F3.wireOp",EDGE,"E675"),sQuery(id+"F3.wireOp",EDGE,"E676"),sQuery(id+"F3.wireOp",EDGE,"E677"),sQuery(id+"F3.wireOp",EDGE,"E678"),sQuery(id+"F3.wireOp",EDGE,"E679"),sQuery(id+"F3.wireOp",EDGE,"E680"),sQuery(id+"F3.wireOp",EDGE,"E681"),sQuery(id+"F3.wireOp",EDGE,"E682"),sQuery(id+"F3.wireOp",EDGE,"E683"),sQuery(id+"F3.wireOp",EDGE,"E684"),sQuery(id+"F3.wireOp",EDGE,"E685"),sQuery(id+"F3.wireOp",EDGE,"E686"),sQuery(id+"F3.wireOp",EDGE,"E687"),sQuery(id+"F3.wireOp",EDGE,"E688"),sQuery(id+"F3.wireOp",EDGE,"E689"),sQuery(id+"F3.wireOp",EDGE,"E690"),sQuery(id+"F3.wireOp",EDGE,"E691"),sQuery(id+"F3.wireOp",EDGE,"E692"),sQuery(id+"F3.wireOp",EDGE,"E693"),sQuery(id+"F3.wireOp",EDGE,"E694"),sQuery(id+"F3.wireOp",EDGE,"E695"),sQuery(id+"F3.wireOp",EDGE,"E696"),sQuery(id+"F3.wireOp",EDGE,"E697"),sQuery(id+"F3.wireOp",EDGE,"E698"),sQuery(id+"F3.wireOp",EDGE,"E699"),sQuery(id+"F3.wireOp",EDGE,"E700"),sQuery(id+"F3.wireOp",EDGE,"E701"),sQuery(id+"F3.wireOp",EDGE,"E702"),sQuery(id+"F3.wireOp",EDGE,"E703"),sQuery(id+"F3.wireOp",EDGE,"E704"),sQuery(id+"F3.wireOp",EDGE,"E705"),sQuery(id+"F3.wireOp",EDGE,"E706"),sQuery(id+"F3.wireOp",EDGE,"E707"),sQuery(id+"F3.wireOp",EDGE,"E708"),sQuery(id+"F3.wireOp",EDGE,"E709"),sQuery(id+"F3.wireOp",EDGE,"E710"),sQuery(id+"F3.wireOp",EDGE,"E711"),sQuery(id+"F3.wireOp",EDGE,"E712"),sQuery(id+"F3.wireOp",EDGE,"E713"),sQuery(id+"F3.wireOp",EDGE,"E714"),sQuery(id+"F3.wireOp",EDGE,"E715"),sQuery(id+"F3.wireOp",EDGE,"E716"),sQuery(id+"F3.wireOp",EDGE,"E717"),sQuery(id+"F3.wireOp",EDGE,"E718"),sQuery(id+"F3.wireOp",EDGE,"E719"),sQuery(id+"F3.wireOp",EDGE,"E720"),sQuery(id+"F3.wireOp",EDGE,"E721"),sQuery(id+"F3.wireOp",EDGE,"E722"),sQuery(id+"F3.wireOp",EDGE,"E723"),sQuery(id+"F3.wireOp",EDGE,"E724"),sQuery(id+"F3.wireOp",EDGE,"E725"),sQuery(id+"F3.wireOp",EDGE,"E726"),sQuery(id+"F3.wireOp",EDGE,"E727"),sQuery(id+"F3.wireOp",EDGE,"E728"),sQuery(id+"F3.wireOp",EDGE,"E729"),sQuery(id+"F3.wireOp",EDGE,"E730"),sQuery(id+"F3.wireOp",EDGE,"E731"),sQuery(id+"F3.wireOp",EDGE,"E732"),sQuery(id+"F3.wireOp",EDGE,"E733"),sQuery(id+"F3.wireOp",EDGE,"E734"),sQuery(id+"F3.wireOp",EDGE,"E735"),sQuery(id+"F3.wireOp",EDGE,"E736"),sQuery(id+"F3.wireOp",EDGE,"E737"),sQuery(id+"F3.wireOp",EDGE,"E738"),sQuery(id+"F3.wireOp",EDGE,"E739"),sQuery(id+"F3.wireOp",EDGE,"E740"),sQuery(id+"F3.wireOp",EDGE,"E741"),sQuery(id+"F3.wireOp",EDGE,"E742"),sQuery(id+"F3.wireOp",EDGE,"E743"),sQuery(id+"F3.wireOp",EDGE,"E744"),sQuery(id+"F3.wireOp",EDGE,"E745"),sQuery(id+"F3.wireOp",EDGE,"E746"),sQuery(id+"F3.wireOp",EDGE,"E747"),sQuery(id+"F3.wireOp",EDGE,"E748"),sQuery(id+"F3.wireOp",EDGE,"E749"),sQuery(id+"F3.wireOp",EDGE,"E750"),sQuery(id+"F3.wireOp",EDGE,"E751"),sQuery(id+"F3.wireOp",EDGE,"E752"),sQuery(id+"F3.wireOp",EDGE,"E753"),sQuery(id+"F3.wireOp",EDGE,"E754"),sQuery(id+"F3.wireOp",EDGE,"E755"),sQuery(id+"F3.wireOp",EDGE,"E756"),sQuery(id+"F3.wireOp",EDGE,"E757"),sQuery(id+"F3.wireOp",EDGE,"E758"),sQuery(id+"F3.wireOp",EDGE,"E759"),sQuery(id+"F3.wireOp",EDGE,"E760"),sQuery(id+"F3.wireOp",EDGE,"E761"),sQuery(id+"F3.wireOp",EDGE,"E762"),sQuery(id+"F3.wireOp",EDGE,"E763"),sQuery(id+"F3.wireOp",EDGE,"E764"),sQuery(id+"F3.wireOp",EDGE,"E765"),sQuery(id+"F3.wireOp",EDGE,"E766"),sQuery(id+"F3.wireOp",EDGE,"E767"),sQuery(id+"F3.wireOp",EDGE,"E768"),sQuery(id+"F3.wireOp",EDGE,"E769"),sQuery(id+"F3.wireOp",EDGE,"E770"),sQuery(id+"F3.wireOp",EDGE,"E771"),sQuery(id+"F3.wireOp",EDGE,"E772"),sQuery(id+"F3.wireOp",EDGE,"E773"),sQuery(id+"F3.wireOp",EDGE,"E774"),sQuery(id+"F3.wireOp",EDGE,"E775"),sQuery(id+"F3.wireOp",EDGE,"E776"),sQuery(id+"F3.wireOp",EDGE,"E777"),sQuery(id+"F3.wireOp",EDGE,"E778"),sQuery(id+"F3.wireOp",EDGE,"E779"),sQuery(id+"F3.wireOp",EDGE,"E780"),sQuery(id+"F3.wireOp",EDGE,"E781"),sQuery(id+"F3.wireOp",EDGE,"E782"),sQuery(id+"F3.wireOp",EDGE,"E783"),sQuery(id+"F3.wireOp",EDGE,"E784"),sQuery(id+"F3.wireOp",EDGE,"E785"),sQuery(id+"F3.wireOp",EDGE,"E786"),sQuery(id+"F3.wireOp",EDGE,"E787"),sQuery(id+"F3.wireOp",EDGE,"E788"),sQuery(id+"F3.wireOp",EDGE,"E789"),sQuery(id+"F3.wireOp",EDGE,"E790"),sQuery(id+"F3.wireOp",EDGE,"E791"),sQuery(id+"F3.wireOp",EDGE,"E792"),sQuery(id+"F3.wireOp",EDGE,"E793"),sQuery(id+"F3.wireOp",EDGE,"E794"),sQuery(id+"F3.wireOp",EDGE,"E795"),sQuery(id+"F3.wireOp",EDGE,"E796"),sQuery(id+"F3.wireOp",EDGE,"E797"),sQuery(id+"F3.wireOp",EDGE,"E798"),sQuery(id+"F3.wireOp",EDGE,"E799"),sQuery(id+"F3.wireOp",EDGE,"E800"),sQuery(id+"F3.wireOp",EDGE,"E801"),sQuery(id+"F3.wireOp",EDGE,"E802"),sQuery(id+"F3.wireOp",EDGE,"E803"),sQuery(id+"F3.wireOp",EDGE,"E804"),sQuery(id+"F3.wireOp",EDGE,"E805"),sQuery(id+"F3.wireOp",EDGE,"E806"),sQuery(id+"F3.wireOp",EDGE,"E807"),sQuery(id+"F3.wireOp",EDGE,"E808"),sQuery(id+"F3.wireOp",EDGE,"E809"),sQuery(id+"F3.wireOp",EDGE,"E810"),sQuery(id+"F3.wireOp",EDGE,"E811"),sQuery(id+"F3.wireOp",EDGE,"E812"),sQuery(id+"F3.wireOp",EDGE,"E813"),sQuery(id+"F3.wireOp",EDGE,"E814"),sQuery(id+"F3.wireOp",EDGE,"E815"),sQuery(id+"F3.wireOp",EDGE,"E816"),sQuery(id+"F3.wireOp",EDGE,"E817"),sQuery(id+"F3.wireOp",EDGE,"E818"),sQuery(id+"F3.wireOp",EDGE,"E819"),sQuery(id+"F3.wireOp",EDGE,"E820"),sQuery(id+"F3.wireOp",EDGE,"E821"),sQuery(id+"F3.wireOp",EDGE,"E822"),sQuery(id+"F3.wireOp",EDGE,"E823"),sQuery(id+"F3.wireOp",EDGE,"E824"),sQuery(id+"F3.wireOp",EDGE,"E825"),sQuery(id+"F3.wireOp",EDGE,"E826"),sQuery(id+"F3.wireOp",EDGE,"E827"),sQuery(id+"F3.wireOp",EDGE,"E828"),sQuery(id+"F3.wireOp",EDGE,"E829"),sQuery(id+"F3.wireOp",EDGE,"E830"),sQuery(id+"F3.wireOp",EDGE,"E831"),sQuery(id+"F3.wireOp",EDGE,"E832"),sQuery(id+"F3.wireOp",EDGE,"E833"),sQuery(id+"F3.wireOp",EDGE,"E834"),sQuery(id+"F3.wireOp",EDGE,"E835"),sQuery(id+"F3.wireOp",EDGE,"E836"),sQuery(id+"F3.wireOp",EDGE,"E837"),sQuery(id+"F3.wireOp",EDGE,"E838"),sQuery(id+"F3.wireOp",EDGE,"E839"),sQuery(id+"F3.wireOp",EDGE,"E840"),sQuery(id+"F3.wireOp",EDGE,"E841"),sQuery(id+"F3.wireOp",EDGE,"E842"),sQuery(id+"F3.wireOp",EDGE,"E843"),sQuery(id+"F3.wireOp",EDGE,"E844"),sQuery(id+"F3.wireOp",EDGE,"E845"),sQuery(id+"F3.wireOp",EDGE,"E846"),sQuery(id+"F3.wireOp",EDGE,"E847"),sQuery(id+"F3.wireOp",EDGE,"E848"),sQuery(id+"F3.wireOp",EDGE,"E849"),sQuery(id+"F3.wireOp",EDGE,"E850"),sQuery(id+"F3.wireOp",EDGE,"E851"),sQuery(id+"F3.wireOp",EDGE,"E852"),sQuery(id+"F3.wireOp",EDGE,"E853"),sQuery(id+"F3.wireOp",EDGE,"E854"),sQuery(id+"F3.wireOp",EDGE,"E855"),sQuery(id+"F3.wireOp",EDGE,"E856"),sQuery(id+"F3.wireOp",EDGE,"E857"),sQuery(id+"F3.wireOp",EDGE,"E858"),sQuery(id+"F3.wireOp",EDGE,"E859"),sQuery(id+"F3.wireOp",EDGE,"E860"),sQuery(id+"F3.wireOp",EDGE,"E861"),sQuery(id+"F3.wireOp",EDGE,"E862"),sQuery(id+"F3.wireOp",EDGE,"E863"),sQuery(id+"F3.wireOp",EDGE,"E864"),sQuery(id+"F3.wireOp",EDGE,"E865"),sQuery(id+"F3.wireOp",EDGE,"E866"),sQuery(id+"F3.wireOp",EDGE,"E867"),sQuery(id+"F3.wireOp",EDGE,"E868"),sQuery(id+"F3.wireOp",EDGE,"E869"),sQuery(id+"F3.wireOp",EDGE,"E870"),sQuery(id+"F3.wireOp",EDGE,"E871"),sQuery(id+"F3.wireOp",EDGE,"E872"),sQuery(id+"F3.wireOp",EDGE,"E873"),sQuery(id+"F3.wireOp",EDGE,"E874"),sQuery(id+"F3.wireOp",EDGE,"E875"),sQuery(id+"F3.wireOp",EDGE,"E876"),sQuery(id+"F3.wireOp",EDGE,"E877"),sQuery(id+"F3.wireOp",EDGE,"E878"),sQuery(id+"F3.wireOp",EDGE,"E879"),sQuery(id+"F3.wireOp",EDGE,"E880"),sQuery(id+"F3.wireOp",EDGE,"E881"),sQuery(id+"F3.wireOp",EDGE,"E882"),sQuery(id+"F3.wireOp",EDGE,"E883"),sQuery(id+"F3.wireOp",EDGE,"E884"),sQuery(id+"F3.wireOp",EDGE,"E885"),sQuery(id+"F3.wireOp",EDGE,"E886"),sQuery(id+"F3.wireOp",EDGE,"E887"),sQuery(id+"F3.wireOp",EDGE,"E888"),sQuery(id+"F3.wireOp",EDGE,"E889"),sQuery(id+"F3.wireOp",EDGE,"E890"),sQuery(id+"F3.wireOp",EDGE,"E891"),sQuery(id+"F3.wireOp",EDGE,"E892"),sQuery(id+"F3.wireOp",EDGE,"E893"),sQuery(id+"F3.wireOp",EDGE,"E894"),sQuery(id+"F3.wireOp",EDGE,"E895"),sQuery(id+"F3.wireOp",EDGE,"E896"),sQuery(id+"F3.wireOp",EDGE,"E897"),sQuery(id+"F3.wireOp",EDGE,"E898"),sQuery(id+"F3.wireOp",EDGE,"E899"),sQuery(id+"F3.wireOp",EDGE,"E900"),sQuery(id+"F3.wireOp",EDGE,"E901"),sQuery(id+"F3.wireOp",EDGE,"E902"),sQuery(id+"F3.wireOp",EDGE,"E903"),sQuery(id+"F3.wireOp",EDGE,"E904"),sQuery(id+"F3.wireOp",EDGE,"E905"),sQuery(id+"F3.wireOp",EDGE,"E906"),sQuery(id+"F3.wireOp",EDGE,"E907"),sQuery(id+"F3.wireOp",EDGE,"E908"),sQuery(id+"F3.wireOp",EDGE,"E909"),sQuery(id+"F3.wireOp",EDGE,"E910"),sQuery(id+"F3.wireOp",EDGE,"E911"),sQuery(id+"F3.wireOp",EDGE,"E912"),sQuery(id+"F3.wireOp",EDGE,"E913"),sQuery(id+"F3.wireOp",EDGE,"E914"),sQuery(id+"F3.wireOp",EDGE,"E915"),sQuery(id+"F3.wireOp",EDGE,"E916"),sQuery(id+"F3.wireOp",EDGE,"E917"),sQuery(id+"F3.wireOp",EDGE,"E918"),sQuery(id+"F3.wireOp",EDGE,"E919"),sQuery(id+"F3.wireOp",EDGE,"E920"),sQuery(id+"F3.wireOp",EDGE,"E921"),sQuery(id+"F3.wireOp",EDGE,"E922"),sQuery(id+"F3.wireOp",EDGE,"E923"),sQuery(id+"F3.wireOp",EDGE,"E924"),sQuery(id+"F3.wireOp",EDGE,"E925"),sQuery(id+"F3.wireOp",EDGE,"E926"),sQuery(id+"F3.wireOp",EDGE,"E927"),sQuery(id+"F3.wireOp",EDGE,"E928"),sQuery(id+"F3.wireOp",EDGE,"E929"),sQuery(id+"F3.wireOp",EDGE,"E930"),sQuery(id+"F3.wireOp",EDGE,"E931"),sQuery(id+"F3.wireOp",EDGE,"E932"),sQuery(id+"F3.wireOp",EDGE,"E933"),sQuery(id+"F3.wireOp",EDGE,"E934"),sQuery(id+"F3.wireOp",EDGE,"E935"),sQuery(id+"F3.wireOp",EDGE,"E936"),sQuery(id+"F3.wireOp",EDGE,"E937"),sQuery(id+"F3.wireOp",EDGE,"E938"),sQuery(id+"F3.wireOp",EDGE,"E939"),sQuery(id+"F3.wireOp",EDGE,"E940"),sQuery(id+"F3.wireOp",EDGE,"E941"),sQuery(id+"F3.wireOp",EDGE,"E942"),sQuery(id+"F3.wireOp",EDGE,"E943"),sQuery(id+"F3.wireOp",EDGE,"E944"),sQuery(id+"F3.wireOp",EDGE,"E945"),sQuery(id+"F3.wireOp",EDGE,"E946"),sQuery(id+"F3.wireOp",EDGE,"E947"),sQuery(id+"F3.wireOp",EDGE,"E948"),sQuery(id+"F3.wireOp",EDGE,"E949"),sQuery(id+"F3.wireOp",EDGE,"E950"),sQuery(id+"F3.wireOp",EDGE,"E951"),sQuery(id+"F3.wireOp",EDGE,"E952"),sQuery(id+"F3.wireOp",EDGE,"E953"),sQuery(id+"F3.wireOp",EDGE,"E954"),sQuery(id+"F3.wireOp",EDGE,"E955"),sQuery(id+"F3.wireOp",EDGE,"E956"),sQuery(id+"F3.wireOp",EDGE,"E957"),sQuery(id+"F3.wireOp",EDGE,"E958"),sQuery(id+"F3.wireOp",EDGE,"E959"),sQuery(id+"F3.wireOp",EDGE,"E960"),sQuery(id+"F3.wireOp",EDGE,"E961"),sQuery(id+"F3.wireOp",EDGE,"E962"),sQuery(id+"F3.wireOp",EDGE,"E963"),sQuery(id+"F3.wireOp",EDGE,"E964"),sQuery(id+"F3.wireOp",EDGE,"E965"),sQuery(id+"F3.wireOp",EDGE,"E966"),sQuery(id+"F3.wireOp",EDGE,"E967"),sQuery(id+"F3.wireOp",EDGE,"E968"),sQuery(id+"F3.wireOp",EDGE,"E969"),sQuery(id+"F3.wireOp",EDGE,"E970"),sQuery(id+"F3.wireOp",EDGE,"E971"),sQuery(id+"F3.wireOp",EDGE,"E972"),sQuery(id+"F3.wireOp",EDGE,"E973"),sQuery(id+"F3.wireOp",EDGE,"E974"),sQuery(id+"F3.wireOp",EDGE,"E975"),sQuery(id+"F3.wireOp",EDGE,"E976"),sQuery(id+"F3.wireOp",EDGE,"E977"),sQuery(id+"F3.wireOp",EDGE,"E978"),sQuery(id+"F3.wireOp",EDGE,"E979"),sQuery(id+"F3.wireOp",EDGE,"E980"),sQuery(id+"F3.wireOp",EDGE,"E981"),sQuery(id+"F3.wireOp",EDGE,"E982"),sQuery(id+"F3.wireOp",EDGE,"E983"),sQuery(id+"F3.wireOp",EDGE,"E984"),sQuery(id+"F3.wireOp",EDGE,"E985"),sQuery(id+"F3.wireOp",EDGE,"E986"),sQuery(id+"F3.wireOp",EDGE,"E987"),sQuery(id+"F3.wireOp",EDGE,"E988"),sQuery(id+"F3.wireOp",EDGE,"E989"),sQuery(id+"F3.wireOp",EDGE,"E990"),sQuery(id+"F3.wireOp",EDGE,"E991"),sQuery(id+"F3.wireOp",EDGE,"E992"),sQuery(id+"F3.wireOp",EDGE,"E993"),sQuery(id+"F3.wireOp",EDGE,"E994"),sQuery(id+"F3.wireOp",EDGE,"E995"),sQuery(id+"F3.wireOp",EDGE,"E996"),sQuery(id+"F3.wireOp",EDGE,"E997"),sQuery(id+"F3.wireOp",EDGE,"E998"),sQuery(id+"F3.wireOp",EDGE,"E999"),sQuery(id+"F3.wireOp",EDGE,"E1000"),sQuery(id+"F3.wireOp",EDGE,"E1001"),sQuery(id+"F3.wireOp",EDGE,"E1002"),sQuery(id+"F3.wireOp",EDGE,"E1003"),sQuery(id+"F3.wireOp",EDGE,"E1004"),sQuery(id+"F3.wireOp",EDGE,"E1005"),sQuery(id+"F3.wireOp",EDGE,"E1006"),sQuery(id+"F3.wireOp",EDGE,"E1007"),sQuery(id+"F3.wireOp",EDGE,"E1008"),sQuery(id+"F3.wireOp",EDGE,"E1009"),sQuery(id+"F3.wireOp",EDGE,"E1010"),sQuery(id+"F3.wireOp",EDGE,"E1011"),sQuery(id+"F3.wireOp",EDGE,"E1012"),sQuery(id+"F3.wireOp",EDGE,"E1013"),sQuery(id+"F3.wireOp",EDGE,"E1014"),sQuery(id+"F3.wireOp",EDGE,"E1015"),sQuery(id+"F3.wireOp",EDGE,"E1016"),sQuery(id+"F3.wireOp",EDGE,"E1017"),sQuery(id+"F3.wireOp",EDGE,"E1018"),sQuery(id+"F3.wireOp",EDGE,"E1019"),sQuery(id+"F3.wireOp",EDGE,"E1020"),sQuery(id+"F3.wireOp",EDGE,"E1021"),sQuery(id+"F3.wireOp",EDGE,"E1022"),sQuery(id+"F3.wireOp",EDGE,"E1023"),sQuery(id+"F3.wireOp",EDGE,"E1024"),sQuery(id+"F3.wireOp",EDGE,"E1025"),sQuery(id+"F3.wireOp",EDGE,"E1026"),sQuery(id+"F3.wireOp",EDGE,"E1027"),sQuery(id+"F3.wireOp",EDGE,"E1028"),sQuery(id+"F3.wireOp",EDGE,"E1029"),sQuery(id+"F3.wireOp",EDGE,"E1030"),sQuery(id+"F3.wireOp",EDGE,"E1031"),sQuery(id+"F3.wireOp",EDGE,"E1032"),sQuery(id+"F3.wireOp",EDGE,"E1033"),sQuery(id+"F3.wireOp",EDGE,"E1034"),sQuery(id+"F3.wireOp",EDGE,"E1035"),sQuery(id+"F3.wireOp",EDGE,"E1036"),sQuery(id+"F3.wireOp",EDGE,"E1037"),sQuery(id+"F3.wireOp",EDGE,"E1038"),sQuery(id+"F3.wireOp",EDGE,"E1039"),sQuery(id+"F3.wireOp",EDGE,"E1040"),sQuery(id+"F3.wireOp",EDGE,"E1041"),sQuery(id+"F3.wireOp",EDGE,"E1042"),sQuery(id+"F3.wireOp",EDGE,"E1043"),sQuery(id+"F3.wireOp",EDGE,"E1044"),sQuery(id+"F3.wireOp",EDGE,"E1045"),sQuery(id+"F3.wireOp",EDGE,"E1046"),sQuery(id+"F3.wireOp",EDGE,"E1047"),sQuery(id+"F3.wireOp",EDGE,"E1048"),sQuery(id+"F3.wireOp",EDGE,"E1049"),sQuery(id+"F3.wireOp",EDGE,"E1050"),sQuery(id+"F3.wireOp",EDGE,"E1051"),sQuery(id+"F3.wireOp",EDGE,"E1052"),sQuery(id+"F3.wireOp",EDGE,"E1053"),sQuery(id+"F3.wireOp",EDGE,"E1054"),sQuery(id+"F3.wireOp",EDGE,"E1055"),sQuery(id+"F3.wireOp",EDGE,"E1056"),sQuery(id+"F3.wireOp",EDGE,"E1057"),sQuery(id+"F3.wireOp",EDGE,"E1058"),sQuery(id+"F3.wireOp",EDGE,"E1059"),sQuery(id+"F3.wireOp",EDGE,"E1060"),sQuery(id+"F3.wireOp",EDGE,"E1061"),sQuery(id+"F3.wireOp",EDGE,"E1062"),sQuery(id+"F3.wireOp",EDGE,"E1063"),sQuery(id+"F3.wireOp",EDGE,"E1064"),sQuery(id+"F3.wireOp",EDGE,"E1065"),sQuery(id+"F3.wireOp",EDGE,"E1066"),sQuery(id+"F3.wireOp",EDGE,"E1067"),sQuery(id+"F3.wireOp",EDGE,"E1068"),sQuery(id+"F3.wireOp",EDGE,"E1069"),sQuery(id+"F3.wireOp",EDGE,"E1070"),sQuery(id+"F3.wireOp",EDGE,"E1071"),sQuery(id+"F3.wireOp",EDGE,"E1072"),sQuery(id+"F3.wireOp",EDGE,"E1073"),sQuery(id+"F3.wireOp",EDGE,"E1074"),sQuery(id+"F3.wireOp",EDGE,"E1075"),sQuery(id+"F3.wireOp",EDGE,"E1076"),sQuery(id+"F3.wireOp",EDGE,"E1077"),sQuery(id+"F3.wireOp",EDGE,"E1078"),sQuery(id+"F3.wireOp",EDGE,"E1079"),sQuery(id+"F3.wireOp",EDGE,"E1080"),sQuery(id+"F3.wireOp",EDGE,"E1081"),sQuery(id+"F3.wireOp",EDGE,"E1082"),sQuery(id+"F3.wireOp",EDGE,"E1083"),sQuery(id+"F3.wireOp",EDGE,"E1084"),sQuery(id+"F3.wireOp",EDGE,"E1085"),sQuery(id+"F3.wireOp",EDGE,"E1086"),sQuery(id+"F3.wireOp",EDGE,"E1087"),sQuery(id+"F3.wireOp",EDGE,"E1088"),sQuery(id+"F3.wireOp",EDGE,"E1089"),sQuery(id+"F3.wireOp",EDGE,"E1090"),sQuery(id+"F3.wireOp",EDGE,"E1091"),sQuery(id+"F3.wireOp",EDGE,"E1092"),sQuery(id+"F3.wireOp",EDGE,"E1093"),sQuery(id+"F3.wireOp",EDGE,"E1094"),sQuery(id+"F3.wireOp",EDGE,"E1095"),sQuery(id+"F3.wireOp",EDGE,"E1096"),sQuery(id+"F3.wireOp",EDGE,"E1097"),sQuery(id+"F3.wireOp",EDGE,"E1098"),sQuery(id+"F3.wireOp",EDGE,"E1099"),sQuery(id+"F3.wireOp",EDGE,"E1100"),sQuery(id+"F3.wireOp",EDGE,"E1101"),sQuery(id+"F3.wireOp",EDGE,"E1102"),sQuery(id+"F3.wireOp",EDGE,"E1103"),sQuery(id+"F3.wireOp",EDGE,"E1104"),sQuery(id+"F3.wireOp",EDGE,"E1105"),sQuery(id+"F3.wireOp",EDGE,"E1106"),sQuery(id+"F3.wireOp",EDGE,"E1107"),sQuery(id+"F3.wireOp",EDGE,"E1108"),sQuery(id+"F3.wireOp",EDGE,"E1109"),sQuery(id+"F3.wireOp",EDGE,"E1110"),sQuery(id+"F3.wireOp",EDGE,"E1111"),sQuery(id+"F3.wireOp",EDGE,"E1112"),sQuery(id+"F3.wireOp",EDGE,"E1113"),sQuery(id+"F3.wireOp",EDGE,"E1114"),sQuery(id+"F3.wireOp",EDGE,"E1115"),sQuery(id+"F3.wireOp",EDGE,"E1116"),sQuery(id+"F3.wireOp",EDGE,"E1117"),sQuery(id+"F3.wireOp",EDGE,"E1118"),sQuery(id+"F3.wireOp",EDGE,"E1119"),sQuery(id+"F3.wireOp",EDGE,"E1120"),sQuery(id+"F3.wireOp",EDGE,"E1121"),sQuery(id+"F3.wireOp",EDGE,"E1122"),sQuery(id+"F3.wireOp",EDGE,"E1123"),sQuery(id+"F3.wireOp",EDGE,"E1124"),sQuery(id+"F3.wireOp",EDGE,"E1125"),sQuery(id+"F3.wireOp",EDGE,"E1126"),sQuery(id+"F3.wireOp",EDGE,"E1127"),sQuery(id+"F3.wireOp",EDGE,"E1128"),sQuery(id+"F3.wireOp",EDGE,"E1129"),sQuery(id+"F3.wireOp",EDGE,"E1130"),sQuery(id+"F3.wireOp",EDGE,"E1131"),sQuery(id+"F3.wireOp",EDGE,"E1132"),sQuery(id+"F3.wireOp",EDGE,"E1133"),sQuery(id+"F3.wireOp",EDGE,"E1134"),sQuery(id+"F3.wireOp",EDGE,"E1135"),sQuery(id+"F3.wireOp",EDGE,"E1136"),sQuery(id+"F3.wireOp",EDGE,"E1137"),sQuery(id+"F3.wireOp",EDGE,"E1138"),sQuery(id+"F3.wireOp",EDGE,"E1139"),sQuery(id+"F3.wireOp",EDGE,"E1140"),sQuery(id+"F3.wireOp",EDGE,"E1141"),sQuery(id+"F3.wireOp",EDGE,"E1142"),sQuery(id+"F3.wireOp",EDGE,"E1143"),sQuery(id+"F3.wireOp",EDGE,"E1144"),sQuery(id+"F3.wireOp",EDGE,"E1145"),sQuery(id+"F3.wireOp",EDGE,"E1146"),sQuery(id+"F3.wireOp",EDGE,"E1147"),sQuery(id+"F3.wireOp",EDGE,"E1148"),sQuery(id+"F3.wireOp",EDGE,"E1149"),sQuery(id+"F3.wireOp",EDGE,"E1150"),sQuery(id+"F3.wireOp",EDGE,"E1151"),sQuery(id+"F3.wireOp",EDGE,"E1152"),sQuery(id+"F3.wireOp",EDGE,"E1153"),sQuery(id+"F3.wireOp",EDGE,"E1154"),sQuery(id+"F3.wireOp",EDGE,"E1155"),sQuery(id+"F3.wireOp",EDGE,"E1156"),sQuery(id+"F3.wireOp",EDGE,"E1157"),sQuery(id+"F3.wireOp",EDGE,"E1158"),sQuery(id+"F3.wireOp",EDGE,"E1159"),sQuery(id+"F3.wireOp",EDGE,"E1160"),sQuery(id+"F3.wireOp",EDGE,"E1161"),sQuery(id+"F3.wireOp",EDGE,"E1162"),sQuery(id+"F3.wireOp",EDGE,"E1163"),sQuery(id+"F3.wireOp",EDGE,"E1164"),sQuery(id+"F3.wireOp",EDGE,"E1165"),sQuery(id+"F3.wireOp",EDGE,"E1166"),sQuery(id+"F3.wireOp",EDGE,"E1167"),sQuery(id+"F3.wireOp",EDGE,"E1168"),sQuery(id+"F3.wireOp",EDGE,"E1169"),sQuery(id+"F3.wireOp",EDGE,"E1170"),sQuery(id+"F3.wireOp",EDGE,"E1171"),sQuery(id+"F3.wireOp",EDGE,"E1172"),sQuery(id+"F3.wireOp",EDGE,"E1173"),sQuery(id+"F3.wireOp",EDGE,"E1174"),sQuery(id+"F3.wireOp",EDGE,"E1175"),sQuery(id+"F3.wireOp",EDGE,"E1176"),sQuery(id+"F3.wireOp",EDGE,"E1177"),sQuery(id+"F3.wireOp",EDGE,"E1178"),sQuery(id+"F3.wireOp",EDGE,"E1179"),sQuery(id+"F3.wireOp",EDGE,"E1180"),sQuery(id+"F3.wireOp",EDGE,"E1181"),sQuery(id+"F3.wireOp",EDGE,"E1182"),sQuery(id+"F3.wireOp",EDGE,"E1183"),sQuery(id+"F3.wireOp",EDGE,"E1184"),sQuery(id+"F3.wireOp",EDGE,"E1185"),sQuery(id+"F3.wireOp",EDGE,"E1186"),sQuery(id+"F3.wireOp",EDGE,"E1187"),sQuery(id+"F3.wireOp",EDGE,"E1188"),sQuery(id+"F3.wireOp",EDGE,"E1189"),sQuery(id+"F3.wireOp",EDGE,"E1190"),sQuery(id+"F3.wireOp",EDGE,"E1191"),sQuery(id+"F3.wireOp",EDGE,"E1192"),sQuery(id+"F3.wireOp",EDGE,"E1193"),sQuery(id+"F3.wireOp",EDGE,"E1194"),sQuery(id+"F3.wireOp",EDGE,"E1195"),sQuery(id+"F3.wireOp",EDGE,"E1196"),sQuery(id+"F3.wireOp",EDGE,"E1197"),sQuery(id+"F3.wireOp",EDGE,"E1198"),sQuery(id+"F3.wireOp",EDGE,"E1199"),sQuery(id+"F3.wireOp",EDGE,"E1200"),sQuery(id+"F3.wireOp",EDGE,"E1201"),sQuery(id+"F3.wireOp",EDGE,"E1202"),sQuery(id+"F3.wireOp",EDGE,"E1203"),sQuery(id+"F3.wireOp",EDGE,"E1204"),sQuery(id+"F3.wireOp",EDGE,"E1205"),sQuery(id+"F3.wireOp",EDGE,"E1206"),sQuery(id+"F3.wireOp",EDGE,"E1207"),sQuery(id+"F3.wireOp",EDGE,"E1208"),sQuery(id+"F3.wireOp",EDGE,"E1209"),sQuery(id+"F3.wireOp",EDGE,"E1210"),sQuery(id+"F3.wireOp",EDGE,"E1211"),sQuery(id+"F3.wireOp",EDGE,"E1212"),sQuery(id+"F3.wireOp",EDGE,"E1213"),sQuery(id+"F3.wireOp",EDGE,"E1214"),sQuery(id+"F3.wireOp",EDGE,"E1215"),sQuery(id+"F3.wireOp",EDGE,"E1216"),sQuery(id+"F3.wireOp",EDGE,"E1217"),sQuery(id+"F3.wireOp",EDGE,"E1218"),sQuery(id+"F3.wireOp",EDGE,"E1219"),sQuery(id+"F3.wireOp",EDGE,"E1220"),sQuery(id+"F3.wireOp",EDGE,"E1221"),sQuery(id+"F3.wireOp",EDGE,"E1222"),sQuery(id+"F3.wireOp",EDGE,"E1223"),sQuery(id+"F3.wireOp",EDGE,"E1224"),sQuery(id+"F3.wireOp",EDGE,"E1225"),sQuery(id+"F3.wireOp",EDGE,"E1226"),sQuery(id+"F3.wireOp",EDGE,"E1227"),sQuery(id+"F3.wireOp",EDGE,"E1228"),sQuery(id+"F3.wireOp",EDGE,"E1229"),sQuery(id+"F3.wireOp",EDGE,"E1230"),sQuery(id+"F3.wireOp",EDGE,"E1231"),sQuery(id+"F3.wireOp",EDGE,"E1232"),sQuery(id+"F3.wireOp",EDGE,"E1233"),sQuery(id+"F3.wireOp",EDGE,"E1234"),sQuery(id+"F3.wireOp",EDGE,"E1235"),sQuery(id+"F3.wireOp",EDGE,"E1236"),sQuery(id+"F3.wireOp",EDGE,"E1237"),sQuery(id+"F3.wireOp",EDGE,"E1238"),sQuery(id+"F3.wireOp",EDGE,"E1239"),sQuery(id+"F3.wireOp",EDGE,"E1240"),sQuery(id+"F3.wireOp",EDGE,"E1241"),sQuery(id+"F3.wireOp",EDGE,"E1242"),sQuery(id+"F3.wireOp",EDGE,"E1243"),sQuery(id+"F3.wireOp",EDGE,"E1244"),sQuery(id+"F3.wireOp",EDGE,"E1245"),sQuery(id+"F3.wireOp",EDGE,"E1246"),sQuery(id+"F3.wireOp",EDGE,"E1247"),sQuery(id+"F3.wireOp",EDGE,"E1248"),sQuery(id+"F3.wireOp",EDGE,"E1249"),sQuery(id+"F3.wireOp",EDGE,"E1250"),sQuery(id+"F3.wireOp",EDGE,"E1251"),sQuery(id+"F3.wireOp",EDGE,"E1252"),sQuery(id+"F3.wireOp",EDGE,"E1253"),sQuery(id+"F3.wireOp",EDGE,"E1254"),sQuery(id+"F3.wireOp",EDGE,"E1255"),sQuery(id+"F3.wireOp",EDGE,"E1256"),sQuery(id+"F3.wireOp",EDGE,"E1257"),sQuery(id+"F3.wireOp",EDGE,"E1258"),sQuery(id+"F3.wireOp",EDGE,"E1259"),sQuery(id+"F3.wireOp",EDGE,"E1260"),sQuery(id+"F3.wireOp",EDGE,"E1261"),sQuery(id+"F3.wireOp",EDGE,"E1262"),sQuery(id+"F3.wireOp",EDGE,"E1263"),sQuery(id+"F3.wireOp",EDGE,"E1264"),sQuery(id+"F3.wireOp",EDGE,"E1265"),sQuery(id+"F3.wireOp",EDGE,"E1266"),sQuery(id+"F3.wireOp",EDGE,"E1267"),sQuery(id+"F3.wireOp",EDGE,"E1268"),sQuery(id+"F3.wireOp",EDGE,"E1269"),sQuery(id+"F3.wireOp",EDGE,"E1270"),sQuery(id+"F3.wireOp",EDGE,"E1271"),sQuery(id+"F3.wireOp",EDGE,"E1272"),sQuery(id+"F3.wireOp",EDGE,"E1273"),sQuery(id+"F3.wireOp",EDGE,"E1274"),sQuery(id+"F3.wireOp",EDGE,"E1275"),sQuery(id+"F3.wireOp",EDGE,"E1276"),sQuery(id+"F3.wireOp",EDGE,"E1277"),sQuery(id+"F3.wireOp",EDGE,"E1278"),sQuery(id+"F3.wireOp",EDGE,"E1279"),sQuery(id+"F3.wireOp",EDGE,"E1280"),sQuery(id+"F3.wireOp",EDGE,"E1281"),sQuery(id+"F3.wireOp",EDGE,"E1282"),sQuery(id+"F3.wireOp",EDGE,"E1283"),sQuery(id+"F3.wireOp",EDGE,"E1284"),sQuery(id+"F3.wireOp",EDGE,"E1285"),sQuery(id+"F3.wireOp",EDGE,"E1286"),sQuery(id+"F3.wireOp",EDGE,"E1287"),sQuery(id+"F3.wireOp",EDGE,"E1288"),sQuery(id+"F3.wireOp",EDGE,"E1289"),sQuery(id+"F3.wireOp",EDGE,"E1290"),sQuery(id+"F3.wireOp",EDGE,"E1291"),sQuery(id+"F3.wireOp",EDGE,"E1292"),sQuery(id+"F3.wireOp",EDGE,"E1293"),sQuery(id+"F3.wireOp",EDGE,"E1294"),sQuery(id+"F3.wireOp",EDGE,"E1295"),sQuery(id+"F3.wireOp",EDGE,"E1296"),sQuery(id+"F3.wireOp",EDGE,"E1297"),sQuery(id+"F3.wireOp",EDGE,"E1298"),sQuery(id+"F3.wireOp",EDGE,"E1299"),sQuery(id+"F3.wireOp",EDGE,"E1300"),sQuery(id+"F3.wireOp",EDGE,"E1301"),sQuery(id+"F3.wireOp",EDGE,"E1302"),sQuery(id+"F3.wireOp",EDGE,"E1303"),sQuery(id+"F3.wireOp",EDGE,"E1304"),sQuery(id+"F3.wireOp",EDGE,"E1305"),sQuery(id+"F3.wireOp",EDGE,"E1306"),sQuery(id+"F3.wireOp",EDGE,"E1307"),sQuery(id+"F3.wireOp",EDGE,"E1308"),sQuery(id+"F3.wireOp",EDGE,"E1309"),sQuery(id+"F3.wireOp",EDGE,"E1310"),sQuery(id+"F3.wireOp",EDGE,"E1311"),sQuery(id+"F3.wireOp",EDGE,"E1312"),sQuery(id+"F3.wireOp",EDGE,"E1313"),sQuery(id+"F3.wireOp",EDGE,"E1314"),sQuery(id+"F3.wireOp",EDGE,"E1315"),sQuery(id+"F3.wireOp",EDGE,"E1316"),sQuery(id+"F3.wireOp",EDGE,"E1317"),sQuery(id+"F3.wireOp",EDGE,"E1318"),sQuery(id+"F3.wireOp",EDGE,"E1319"),sQuery(id+"F3.wireOp",EDGE,"E1320"),sQuery(id+"F3.wireOp",EDGE,"E1321"),sQuery(id+"F3.wireOp",EDGE,"E1322"),sQuery(id+"F3.wireOp",EDGE,"E1323"),sQuery(id+"F3.wireOp",EDGE,"E1324"),sQuery(id+"F3.wireOp",EDGE,"E1325"),sQuery(id+"F3.wireOp",EDGE,"E1326"),sQuery(id+"F3.wireOp",EDGE,"E1327"),sQuery(id+"F3.wireOp",EDGE,"E1328"),sQuery(id+"F3.wireOp",EDGE,"E1329"),sQuery(id+"F3.wireOp",EDGE,"E1330"),sQuery(id+"F3.wireOp",EDGE,"E1331"),sQuery(id+"F3.wireOp",EDGE,"E1332"),sQuery(id+"F3.wireOp",EDGE,"E1333"),sQuery(id+"F3.wireOp",EDGE,"E1334"),sQuery(id+"F3.wireOp",EDGE,"E1335"),sQuery(id+"F3.wireOp",EDGE,"E1336"),sQuery(id+"F3.wireOp",EDGE,"E1337"),sQuery(id+"F3.wireOp",EDGE,"E1338"),sQuery(id+"F3.wireOp",EDGE,"E1339"),sQuery(id+"F3.wireOp",EDGE,"E1340"),sQuery(id+"F3.wireOp",EDGE,"E1341"),sQuery(id+"F3.wireOp",EDGE,"E1342"),sQuery(id+"F3.wireOp",EDGE,"E1343"),sQuery(id+"F3.wireOp",EDGE,"E1344"),sQuery(id+"F3.wireOp",EDGE,"E1345"),sQuery(id+"F3.wireOp",EDGE,"E1346"),sQuery(id+"F3.wireOp",EDGE,"E1347"),sQuery(id+"F3.wireOp",EDGE,"E1348"),sQuery(id+"F3.wireOp",EDGE,"E1349"),sQuery(id+"F3.wireOp",EDGE,"E1350"),sQuery(id+"F3.wireOp",EDGE,"E1351"),sQuery(id+"F3.wireOp",EDGE,"E1352"),sQuery(id+"F3.wireOp",EDGE,"E1353"),sQuery(id+"F3.wireOp",EDGE,"E1354"),sQuery(id+"F3.wireOp",EDGE,"E1355"),sQuery(id+"F3.wireOp",EDGE,"E1356"),sQuery(id+"F3.wireOp",EDGE,"E1357"),sQuery(id+"F3.wireOp",EDGE,"E1358"),sQuery(id+"F3.wireOp",EDGE,"E1359"),sQuery(id+"F3.wireOp",EDGE,"E1360"),sQuery(id+"F3.wireOp",EDGE,"E1361"),sQuery(id+"F3.wireOp",EDGE,"E1362"),sQuery(id+"F3.wireOp",EDGE,"E1363"),sQuery(id+"F3.wireOp",EDGE,"E1364"),sQuery(id+"F3.wireOp",EDGE,"E1365"),sQuery(id+"F3.wireOp",EDGE,"E1366"),sQuery(id+"F3.wireOp",EDGE,"E1367"),sQuery(id+"F3.wireOp",EDGE,"E1368"),sQuery(id+"F3.wireOp",EDGE,"E1369"),sQuery(id+"F3.wireOp",EDGE,"E1370"),sQuery(id+"F3.wireOp",EDGE,"E1371"),sQuery(id+"F3.wireOp",EDGE,"E1372"),sQuery(id+"F3.wireOp",EDGE,"E1373"),sQuery(id+"F3.wireOp",EDGE,"E1374"),sQuery(id+"F3.wireOp",EDGE,"E1375"),sQuery(id+"F3.wireOp",EDGE,"E1376"),sQuery(id+"F3.wireOp",EDGE,"E1377"),sQuery(id+"F3.wireOp",EDGE,"E1378"),sQuery(id+"F3.wireOp",EDGE,"E1379"),sQuery(id+"F3.wireOp",EDGE,"E1380"),sQuery(id+"F3.wireOp",EDGE,"E1381"),sQuery(id+"F3.wireOp",EDGE,"E1382"),sQuery(id+"F3.wireOp",EDGE,"E1383"),sQuery(id+"F3.wireOp",EDGE,"E1384"),sQuery(id+"F3.wireOp",EDGE,"E1385"),sQuery(id+"F3.wireOp",EDGE,"E1386"),sQuery(id+"F3.wireOp",EDGE,"E1387"),sQuery(id+"F3.wireOp",EDGE,"E1388"),sQuery(id+"F3.wireOp",EDGE,"E1389"),sQuery(id+"F3.wireOp",EDGE,"E1390"),sQuery(id+"F3.wireOp",EDGE,"E1391"),sQuery(id+"F3.wireOp",EDGE,"E1392"),sQuery(id+"F3.wireOp",EDGE,"E1393"),sQuery(id+"F3.wireOp",EDGE,"E1394"),sQuery(id+"F3.wireOp",EDGE,"E1395"),sQuery(id+"F3.wireOp",EDGE,"E1396"),sQuery(id+"F3.wireOp",EDGE,"E1397"),sQuery(id+"F3.wireOp",EDGE,"E1398"),sQuery(id+"F3.wireOp",EDGE,"E1399"),sQuery(id+"F3.wireOp",EDGE,"E1400"),sQuery(id+"F3.wireOp",EDGE,"E1401"),sQuery(id+"F3.wireOp",EDGE,"E1402"),sQuery(id+"F3.wireOp",EDGE,"E1403"),sQuery(id+"F3.wireOp",EDGE,"E1404"),sQuery(id+"F3.wireOp",EDGE,"E1405"),sQuery(id+"F3.wireOp",EDGE,"E1406"),sQuery(id+"F3.wireOp",EDGE,"E1407"),sQuery(id+"F3.wireOp",EDGE,"E1408"),sQuery(id+"F3.wireOp",EDGE,"E1409"),sQuery(id+"F3.wireOp",EDGE,"E1410"),sQuery(id+"F3.wireOp",EDGE,"E1411"),sQuery(id+"F3.wireOp",EDGE,"E1412"),sQuery(id+"F3.wireOp",EDGE,"E1413"),sQuery(id+"F3.wireOp",EDGE,"E1414"),sQuery(id+"F3.wireOp",EDGE,"E1415"),sQuery(id+"F3.wireOp",EDGE,"E1416"),sQuery(id+"F3.wireOp",EDGE,"E1417"),sQuery(id+"F3.wireOp",EDGE,"E1418"),sQuery(id+"F3.wireOp",EDGE,"E1419"),sQuery(id+"F3.wireOp",EDGE,"E1420"),sQuery(id+"F3.wireOp",EDGE,"E1421"),sQuery(id+"F3.wireOp",EDGE,"E1422"),sQuery(id+"F3.wireOp",EDGE,"E1423"),sQuery(id+"F3.wireOp",EDGE,"E1424"),sQuery(id+"F3.wireOp",EDGE,"E1425"),sQuery(id+"F3.wireOp",EDGE,"E1426"),sQuery(id+"F3.wireOp",EDGE,"E1427"),sQuery(id+"F3.wireOp",EDGE,"E1428"),sQuery(id+"F3.wireOp",EDGE,"E1429"),sQuery(id+"F3.wireOp",EDGE,"E1430"),sQuery(id+"F3.wireOp",EDGE,"E1431"),sQuery(id+"F3.wireOp",EDGE,"E1432"),sQuery(id+"F3.wireOp",EDGE,"E1433"),sQuery(id+"F3.wireOp",EDGE,"E1434"),sQuery(id+"F3.wireOp",EDGE,"E1435"),sQuery(id+"F3.wireOp",EDGE,"E1436"),sQuery(id+"F3.wireOp",EDGE,"E1437"),sQuery(id+"F3.wireOp",EDGE,"E1438"),sQuery(id+"F3.wireOp",EDGE,"E1439"),sQuery(id+"F3.wireOp",EDGE,"E1440"),sQuery(id+"F3.wireOp",EDGE,"E1441"),sQuery(id+"F3.wireOp",EDGE,"E1442"),sQuery(id+"F3.wireOp",EDGE,"E1443"),sQuery(id+"F3.wireOp",EDGE,"E1444"),sQuery(id+"F3.wireOp",EDGE,"E1445"),sQuery(id+"F3.wireOp",EDGE,"E1446"),sQuery(id+"F3.wireOp",EDGE,"E1447"),sQuery(id+"F3.wireOp",EDGE,"E1448"),sQuery(id+"F3.wireOp",EDGE,"E1449"),sQuery(id+"F3.wireOp",EDGE,"E1450"),sQuery(id+"F3.wireOp",EDGE,"E1451"),sQuery(id+"F3.wireOp",EDGE,"E1452"),sQuery(id+"F3.wireOp",EDGE,"E1453"),sQuery(id+"F3.wireOp",EDGE,"E1454"),sQuery(id+"F3.wireOp",EDGE,"E1455"),sQuery(id+"F3.wireOp",EDGE,"E1456"),sQuery(id+"F3.wireOp",EDGE,"E1457"),sQuery(id+"F3.wireOp",EDGE,"E1458"),sQuery(id+"F3.wireOp",EDGE,"E1459"),sQuery(id+"F3.wireOp",EDGE,"E1460"),sQuery(id+"F3.wireOp",EDGE,"E1461"),sQuery(id+"F3.wireOp",EDGE,"E1462"),sQuery(id+"F3.wireOp",EDGE,"E1463"),sQuery(id+"F3.wireOp",EDGE,"E1464"),sQuery(id+"F3.wireOp",EDGE,"E1465"),sQuery(id+"F3.wireOp",EDGE,"E1466"),sQuery(id+"F3.wireOp",EDGE,"E1467"),sQuery(id+"F3.wireOp",EDGE,"E1468"),sQuery(id+"F3.wireOp",EDGE,"E1469"),sQuery(id+"F3.wireOp",EDGE,"E1470"),sQuery(id+"F3.wireOp",EDGE,"E1471"),sQuery(id+"F3.wireOp",EDGE,"E1472"),sQuery(id+"F3.wireOp",EDGE,"E1473"),sQuery(id+"F3.wireOp",EDGE,"E1474"),sQuery(id+"F3.wireOp",EDGE,"E1475"),sQuery(id+"F3.wireOp",EDGE,"E1476"),sQuery(id+"F3.wireOp",EDGE,"E1477"),sQuery(id+"F3.wireOp",EDGE,"E1478"),sQuery(id+"F3.wireOp",EDGE,"E1479"),sQuery(id+"F3.wireOp",EDGE,"E1480"),sQuery(id+"F3.wireOp",EDGE,"E1481"),sQuery(id+"F3.wireOp",EDGE,"E1482"),sQuery(id+"F3.wireOp",EDGE,"E1483"),sQuery(id+"F3.wireOp",EDGE,"E1484"),sQuery(id+"F3.wireOp",EDGE,"E1485"),sQuery(id+"F3.wireOp",EDGE,"E1486"),sQuery(id+"F3.wireOp",EDGE,"E1487"),sQuery(id+"F3.wireOp",EDGE,"E1488"),sQuery(id+"F3.wireOp",EDGE,"E1489"),sQuery(id+"F3.wireOp",EDGE,"E1490"),sQuery(id+"F3.wireOp",EDGE,"E1491"),sQuery(id+"F3.wireOp",EDGE,"E1492"),sQuery(id+"F3.wireOp",EDGE,"E1493"),sQuery(id+"F3.wireOp",EDGE,"E1494"),sQuery(id+"F3.wireOp",EDGE,"E1495"),sQuery(id+"F3.wireOp",EDGE,"E1496"),sQuery(id+"F3.wireOp",EDGE,"E1497"),sQuery(id+"F3.wireOp",EDGE,"E1498"),sQuery(id+"F3.wireOp",EDGE,"E1499"),sQuery(id+"F3.wireOp",EDGE,"E1500"),sQuery(id+"F3.wireOp",EDGE,"E1501"),sQuery(id+"F3.wireOp",EDGE,"E1502"),sQuery(id+"F3.wireOp",EDGE,"E1503"),sQuery(id+"F3.wireOp",EDGE,"E1504"),sQuery(id+"F3.wireOp",EDGE,"E1505"),sQuery(id+"F3.wireOp",EDGE,"E1506"),sQuery(id+"F3.wireOp",EDGE,"E1507"),sQuery(id+"F3.wireOp",EDGE,"E1508"),sQuery(id+"F3.wireOp",EDGE,"E1509"),sQuery(id+"F3.wireOp",EDGE,"E1510"),sQuery(id+"F3.wireOp",EDGE,"E1511"),sQuery(id+"F3.wireOp",EDGE,"E1512"),sQuery(id+"F3.wireOp",EDGE,"E1513"),sQuery(id+"F3.wireOp",EDGE,"E1514"),sQuery(id+"F3.wireOp",EDGE,"E1515"),sQuery(id+"F3.wireOp",EDGE,"E1516"),sQuery(id+"F3.wireOp",EDGE,"E1517"),sQuery(id+"F3.wireOp",EDGE,"E1518"),sQuery(id+"F3.wireOp",EDGE,"E1519"),sQuery(id+"F3.wireOp",EDGE,"E1520"),sQuery(id+"F3.wireOp",EDGE,"E1521"),sQuery(id+"F3.wireOp",EDGE,"E1522"),sQuery(id+"F3.wireOp",EDGE,"E1523"),sQuery(id+"F3.wireOp",EDGE,"E1524"),sQuery(id+"F3.wireOp",EDGE,"E1525"),sQuery(id+"F3.wireOp",EDGE,"E1526"),sQuery(id+"F3.wireOp",EDGE,"E1527"),sQuery(id+"F3.wireOp",EDGE,"E1528"),sQuery(id+"F3.wireOp",EDGE,"E1529"),sQuery(id+"F3.wireOp",EDGE,"E1530"),sQuery(id+"F3.wireOp",EDGE,"E1531"),sQuery(id+"F3.wireOp",EDGE,"E1532"),sQuery(id+"F3.wireOp",EDGE,"E1533"),sQuery(id+"F3.wireOp",EDGE,"E1534"),sQuery(id+"F3.wireOp",EDGE,"E1535"),sQuery(id+"F3.wireOp",EDGE,"E1536"),sQuery(id+"F3.wireOp",EDGE,"E1537"),sQuery(id+"F3.wireOp",EDGE,"E1538"),sQuery(id+"F3.wireOp",EDGE,"E1539"),sQuery(id+"F3.wireOp",EDGE,"E1540"),sQuery(id+"F3.wireOp",EDGE,"E1541"),sQuery(id+"F3.wireOp",EDGE,"E1542"),sQuery(id+"F3.wireOp",EDGE,"E1543"),sQuery(id+"F3.wireOp",EDGE,"E1544"),sQuery(id+"F3.wireOp",EDGE,"E1545"),sQuery(id+"F3.wireOp",EDGE,"E1546"),sQuery(id+"F3.wireOp",EDGE,"E1547"),sQuery(id+"F3.wireOp",EDGE,"E1548"),sQuery(id+"F3.wireOp",EDGE,"E1549"),sQuery(id+"F3.wireOp",EDGE,"E1550"),sQuery(id+"F3.wireOp",EDGE,"E1551"),sQuery(id+"F3.wireOp",EDGE,"E1552"),sQuery(id+"F3.wireOp",EDGE,"E1553"),sQuery(id+"F3.wireOp",EDGE,"E1554"),sQuery(id+"F3.wireOp",EDGE,"E1555"),sQuery(id+"F3.wireOp",EDGE,"E1556"),sQuery(id+"F3.wireOp",EDGE,"E1557"),sQuery(id+"F3.wireOp",EDGE,"E1558"),sQuery(id+"F3.wireOp",EDGE,"E1559"),sQuery(id+"F3.wireOp",EDGE,"E1560"),sQuery(id+"F3.wireOp",EDGE,"E1561"),sQuery(id+"F3.wireOp",EDGE,"E1562"),sQuery(id+"F3.wireOp",EDGE,"E1563"),sQuery(id+"F3.wireOp",EDGE,"E1564"),sQuery(id+"F3.wireOp",EDGE,"E1565"),sQuery(id+"F3.wireOp",EDGE,"E1566"),sQuery(id+"F3.wireOp",EDGE,"E1567"),sQuery(id+"F3.wireOp",EDGE,"E1568"),sQuery(id+"F3.wireOp",EDGE,"E1569"),sQuery(id+"F3.wireOp",EDGE,"E1570"),sQuery(id+"F3.wireOp",EDGE,"E1571"),sQuery(id+"F3.wireOp",EDGE,"E1572"),sQuery(id+"F3.wireOp",EDGE,"E1573"),sQuery(id+"F3.wireOp",EDGE,"E1574"),sQuery(id+"F3.wireOp",EDGE,"E1575"),sQuery(id+"F3.wireOp",EDGE,"E1576"),sQuery(id+"F3.wireOp",EDGE,"E1577"),sQuery(id+"F3.wireOp",EDGE,"E1578"),sQuery(id+"F3.wireOp",EDGE,"E1579"),sQuery(id+"F3.wireOp",EDGE,"E1580"),sQuery(id+"F3.wireOp",EDGE,"E1581"),sQuery(id+"F3.wireOp",EDGE,"E1582"),sQuery(id+"F3.wireOp",EDGE,"E1583"),sQuery(id+"F3.wireOp",EDGE,"E1584"),sQuery(id+"F3.wireOp",EDGE,"E1585"),sQuery(id+"F3.wireOp",EDGE,"E1586"),sQuery(id+"F3.wireOp",EDGE,"E1587"),sQuery(id+"F3.wireOp",EDGE,"E1588"),sQuery(id+"F3.wireOp",EDGE,"E1589"),sQuery(id+"F3.wireOp",EDGE,"E1590"),sQuery(id+"F3.wireOp",EDGE,"E1591"),sQuery(id+"F3.wireOp",EDGE,"E1592"),sQuery(id+"F3.wireOp",EDGE,"E1593"),sQuery(id+"F3.wireOp",EDGE,"E1594"),sQuery(id+"F3.wireOp",EDGE,"E1595"),sQuery(id+"F3.wireOp",EDGE,"E1596"),sQuery(id+"F3.wireOp",EDGE,"E1597"),sQuery(id+"F3.wireOp",EDGE,"E1598"),sQuery(id+"F3.wireOp",EDGE,"E1599"),sQuery(id+"F3.wireOp",EDGE,"E1600"),sQuery(id+"F3.wireOp",EDGE,"E1601"),sQuery(id+"F3.wireOp",EDGE,"E1602"),sQuery(id+"F3.wireOp",EDGE,"E1603"),sQuery(id+"F3.wireOp",EDGE,"E1604"),sQuery(id+"F3.wireOp",EDGE,"E1605"),sQuery(id+"F3.wireOp",EDGE,"E1606"),sQuery(id+"F3.wireOp",EDGE,"E1607"),sQuery(id+"F3.wireOp",EDGE,"E1608"),sQuery(id+"F3.wireOp",EDGE,"E1609"),sQuery(id+"F3.wireOp",EDGE,"E1610"),sQuery(id+"F3.wireOp",EDGE,"E1611"),sQuery(id+"F3.wireOp",EDGE,"E1612"),sQuery(id+"F3.wireOp",EDGE,"E1613"),sQuery(id+"F3.wireOp",EDGE,"E1614"),sQuery(id+"F3.wireOp",EDGE,"E1615"),sQuery(id+"F3.wireOp",EDGE,"E1616"),sQuery(id+"F3.wireOp",EDGE,"E1617"),sQuery(id+"F3.wireOp",EDGE,"E1618"),sQuery(id+"F3.wireOp",EDGE,"E1619"),sQuery(id+"F3.wireOp",EDGE,"E1620"),sQuery(id+"F3.wireOp",EDGE,"E1621"),sQuery(id+"F3.wireOp",EDGE,"E1622"),sQuery(id+"F3.wireOp",EDGE,"E1623"),sQuery(id+"F3.wireOp",EDGE,"E1624"),sQuery(id+"F3.wireOp",EDGE,"E1625"),sQuery(id+"F3.wireOp",EDGE,"E1626"),sQuery(id+"F3.wireOp",EDGE,"E1627"),sQuery(id+"F3.wireOp",EDGE,"E1628"),sQuery(id+"F3.wireOp",EDGE,"E1629"),sQuery(id+"F3.wireOp",EDGE,"E1630"),sQuery(id+"F3.wireOp",EDGE,"E1631"),sQuery(id+"F3.wireOp",EDGE,"E1632"),sQuery(id+"F3.wireOp",EDGE,"E1633"),sQuery(id+"F3.wireOp",EDGE,"E1634"),sQuery(id+"F3.wireOp",EDGE,"E1635"),sQuery(id+"F3.wireOp",EDGE,"E1636"),sQuery(id+"F3.wireOp",EDGE,"E1637"),sQuery(id+"F3.wireOp",EDGE,"E1638"),sQuery(id+"F3.wireOp",EDGE,"E1639"),sQuery(id+"F3.wireOp",EDGE,"E1640"),sQuery(id+"F3.wireOp",EDGE,"E1641"),sQuery(id+"F3.wireOp",EDGE,"E1642"),sQuery(id+"F3.wireOp",EDGE,"E1643"),sQuery(id+"F3.wireOp",EDGE,"E1644"),sQuery(id+"F3.wireOp",EDGE,"E1645"),sQuery(id+"F3.wireOp",EDGE,"E1646"),sQuery(id+"F3.wireOp",EDGE,"E1647"),sQuery(id+"F3.wireOp",EDGE,"E1648"),sQuery(id+"F3.wireOp",EDGE,"E1649"),sQuery(id+"F3.wireOp",EDGE,"E1650"),sQuery(id+"F3.wireOp",EDGE,"E1651"),sQuery(id+"F3.wireOp",EDGE,"E1652"),sQuery(id+"F3.wireOp",EDGE,"E1653"),sQuery(id+"F3.wireOp",EDGE,"E1654"),sQuery(id+"F3.wireOp",EDGE,"E1655"),sQuery(id+"F3.wireOp",EDGE,"E1656"),sQuery(id+"F3.wireOp",EDGE,"E1657"),sQuery(id+"F3.wireOp",EDGE,"E1658"),sQuery(id+"F3.wireOp",EDGE,"E1659"),sQuery(id+"F3.wireOp",EDGE,"E1660"),sQuery(id+"F3.wireOp",EDGE,"E1661"),sQuery(id+"F3.wireOp",EDGE,"E1662"),sQuery(id+"F3.wireOp",EDGE,"E1663"),sQuery(id+"F3.wireOp",EDGE,"E1664"),sQuery(id+"F3.wireOp",EDGE,"E1665"),sQuery(id+"F3.wireOp",EDGE,"E1666"),sQuery(id+"F3.wireOp",EDGE,"E1667"),sQuery(id+"F3.wireOp",EDGE,"E1668"),sQuery(id+"F3.wireOp",EDGE,"E1669"),sQuery(id+"F3.wireOp",EDGE,"E1670"),sQuery(id+"F3.wireOp",EDGE,"E1671"),sQuery(id+"F3.wireOp",EDGE,"E1672"),sQuery(id+"F3.wireOp",EDGE,"E1673"),sQuery(id+"F3.wireOp",EDGE,"E1674"),sQuery(id+"F3.wireOp",EDGE,"E1675"),sQuery(id+"F3.wireOp",EDGE,"E1676"),sQuery(id+"F3.wireOp",EDGE,"E1677"),sQuery(id+"F3.wireOp",EDGE,"E1678"),sQuery(id+"F3.wireOp",EDGE,"E1679"),sQuery(id+"F3.wireOp",EDGE,"E1680"),sQuery(id+"F3.wireOp",EDGE,"E1681"),sQuery(id+"F3.wireOp",EDGE,"E1682"),sQuery(id+"F3.wireOp",EDGE,"E1683"),sQuery(id+"F3.wireOp",EDGE,"E1684"),sQuery(id+"F3.wireOp",EDGE,"E1685"),sQuery(id+"F3.wireOp",EDGE,"E1686"),sQuery(id+"F3.wireOp",EDGE,"E1687"),sQuery(id+"F3.wireOp",EDGE,"E1688"),sQuery(id+"F3.wireOp",EDGE,"E1689"),sQuery(id+"F3.wireOp",EDGE,"E1690"),sQuery(id+"F3.wireOp",EDGE,"E1691"),sQuery(id+"F3.wireOp",EDGE,"E1692"),sQuery(id+"F3.wireOp",EDGE,"E1693"),sQuery(id+"F3.wireOp",EDGE,"E1694"),sQuery(id+"F3.wireOp",EDGE,"E1695"),sQuery(id+"F3.wireOp",EDGE,"E1696"),sQuery(id+"F3.wireOp",EDGE,"E1697"),sQuery(id+"F3.wireOp",EDGE,"E1698"),sQuery(id+"F3.wireOp",EDGE,"E1699"),sQuery(id+"F3.wireOp",EDGE,"E1700"),sQuery(id+"F3.wireOp",EDGE,"E1701"),sQuery(id+"F3.wireOp",EDGE,"E1702"),sQuery(id+"F3.wireOp",EDGE,"E1703"),sQuery(id+"F3.wireOp",EDGE,"E1704"),sQuery(id+"F3.wireOp",EDGE,"E1705"),sQuery(id+"F3.wireOp",EDGE,"E1706"),sQuery(id+"F3.wireOp",EDGE,"E1707"),sQuery(id+"F3.wireOp",EDGE,"E1708"),sQuery(id+"F3.wireOp",EDGE,"E1709"),sQuery(id+"F3.wireOp",EDGE,"E1710"),sQuery(id+"F3.wireOp",EDGE,"E1711"),sQuery(id+"F3.wireOp",EDGE,"E1712"),sQuery(id+"F3.wireOp",EDGE,"E1713"),sQuery(id+"F3.wireOp",EDGE,"E1714"),sQuery(id+"F3.wireOp",EDGE,"E1715"),sQuery(id+"F3.wireOp",EDGE,"E1716"),sQuery(id+"F3.wireOp",EDGE,"E1717"),sQuery(id+"F3.wireOp",EDGE,"E1718"),sQuery(id+"F3.wireOp",EDGE,"E1719"),sQuery(id+"F3.wireOp",EDGE,"E1720"),sQuery(id+"F3.wireOp",EDGE,"E1721"),sQuery(id+"F3.wireOp",EDGE,"E1722"),sQuery(id+"F3.wireOp",EDGE,"E1723"),sQuery(id+"F3.wireOp",EDGE,"E1724"),sQuery(id+"F3.wireOp",EDGE,"E1725"),sQuery(id+"F3.wireOp",EDGE,"E1726"),sQuery(id+"F3.wireOp",EDGE,"E1727"),sQuery(id+"F3.wireOp",EDGE,"E1728"),sQuery(id+"F3.wireOp",EDGE,"E1729"),sQuery(id+"F3.wireOp",EDGE,"E1730"),sQuery(id+"F3.wireOp",EDGE,"E1731"),sQuery(id+"F3.wireOp",EDGE,"E1732"),sQuery(id+"F3.wireOp",EDGE,"E1733"),sQuery(id+"F3.wireOp",EDGE,"E1734"),sQuery(id+"F3.wireOp",EDGE,"E1735"),sQuery(id+"F3.wireOp",EDGE,"E1736"),sQuery(id+"F3.wireOp",EDGE,"E1737"),sQuery(id+"F3.wireOp",EDGE,"E1738"),sQuery(id+"F3.wireOp",EDGE,"E1739"),sQuery(id+"F3.wireOp",EDGE,"E1740"),sQuery(id+"F3.wireOp",EDGE,"E1741"),sQuery(id+"F3.wireOp",EDGE,"E1742"),sQuery(id+"F3.wireOp",EDGE,"E1743"),sQuery(id+"F3.wireOp",EDGE,"E1744"),sQuery(id+"F3.wireOp",EDGE,"E1745"),sQuery(id+"F3.wireOp",EDGE,"E1746"),sQuery(id+"F3.wireOp",EDGE,"E1747"),sQuery(id+"F3.wireOp",EDGE,"E1748"),sQuery(id+"F3.wireOp",EDGE,"E1749"),sQuery(id+"F3.wireOp",EDGE,"E1750"),sQuery(id+"F3.wireOp",EDGE,"E1751"),sQuery(id+"F3.wireOp",EDGE,"E1752"),sQuery(id+"F3.wireOp",EDGE,"E1753"),sQuery(id+"F3.wireOp",EDGE,"E1754"),sQuery(id+"F3.wireOp",EDGE,"E1755"),sQuery(id+"F3.wireOp",EDGE,"E1756"),sQuery(id+"F3.wireOp",EDGE,"E1757"),sQuery(id+"F3.wireOp",EDGE,"E1758"),sQuery(id+"F3.wireOp",EDGE,"E1759"),sQuery(id+"F3.wireOp",EDGE,"E1780.0.0"),sQuery(id+"F3.wireOp",EDGE,"E1780.0.1"),sQuery(id+"F3.wireOp",EDGE,"E1780.0.2"),sQuery(id+"F3.wireOp",EDGE,"E1780.0.3"),sQuery(id+"F3.wireOp",EDGE,"E1780.0.4"),sQuery(id+"F3.wireOp",EDGE,"E1780.0.5"),sQuery(id+"F3.wireOp",EDGE,"E1780.0.6"),sQuery(id+"F3.wireOp",EDGE,"E1780.0.7"),sQuery(id+"F3.wireOp",EDGE,"E1780.0.8"),sQuery(id+"F3.wireOp",EDGE,"E1780.0.9"),sQuery(id+"F3.wireOp",EDGE,"E1780.0.10"),sQuery(id+"F3.wireOp",EDGE,"E1780.0.11"),sQuery(id+"F3.wireOp",EDGE,"E1780.0.12"),sQuery(id+"F3.wireOp",EDGE,"E1780.0.13"),sQuery(id+"F3.wireOp",EDGE,"E1780.0.14"),sQuery(id+"F3.wireOp",EDGE,"E1780.0.15"),sQuery(id+"F3.wireOp",EDGE,"E1780.0.16"),sQuery(id+"F3.wireOp",EDGE,"E1780.0.17"),sQuery(id+"F3.wireOp",EDGE,"E1780.0.18"),sQuery(id+"F3.wireOp",EDGE,"E1780.0.19"),sQuery(id+"F3.wireOp",EDGE,"E1780.0.20"),sQuery(id+"F3.wireOp",EDGE,"E1780.0.21"),sQuery(id+"F3.wireOp",EDGE,"E1780.0.22"),sQuery(id+"F3.wireOp",EDGE,"E1780.0.23"),sQuery(id+"F3.wireOp",EDGE,"E1780.0.24"),sQuery(id+"F3.wireOp",EDGE,"E1780.0.25"),sQuery(id+"F3.wireOp",EDGE,"E1780.0.26"),sQuery(id+"F3.wireOp",EDGE,"E1780.0.27"),sQuery(id+"F3.wireOp",EDGE,"E1780.0.28"),sQuery(id+"F3.wireOp",EDGE,"E1780.0.29"),sQuery(id+"F3.wireOp",EDGE,"E1780.0.30"),sQuery(id+"F3.wireOp",EDGE,"E1780.0.31"),sQuery(id+"F3.wireOp",EDGE,"E1780.0.32"),sQuery(id+"F3.wireOp",EDGE,"E1780.0.33"),sQuery(id+"F3.wireOp",EDGE,"E1780.0.34"),sQuery(id+"F3.wireOp",EDGE,"E1780.0.35"),sQuery(id+"F3.wireOp",EDGE,"E1780.0.36"),sQuery(id+"F3.wireOp",EDGE,"E1780.0.37"),sQuery(id+"F3.wireOp",EDGE,"E1780.0.38"),sQuery(id+"F3.wireOp",EDGE,"E1780.0.39"),sQuery(id+"F3.wireOp",EDGE,"E1780.0.40"),sQuery(id+"F3.wireOp",EDGE,"E1780.0.41"),sQuery(id+"F3.wireOp",EDGE,"E1780.0.42"),sQuery(id+"F3.wireOp",EDGE,"E1780.0.43"),sQuery(id+"F3.wireOp",EDGE,"E1780.0.44"),sQuery(id+"F3.wireOp",EDGE,"E1780.0.45"),sQuery(id+"F3.wireOp",EDGE,"E1780.0.46"),sQuery(id+"F3.wireOp",EDGE,"E1780.0.47"),sQuery(id+"F3.wireOp",EDGE,"E1780.0.48"),sQuery(id+"F3.wireOp",EDGE,"E1780.0.49"),sQuery(id+"F3.wireOp",EDGE,"E1780.0.50"),sQuery(id+"F3.wireOp",EDGE,"E1780.0.51"),sQuery(id+"F3.wireOp",EDGE,"E1780.0.52"),sQuery(id+"F3.wireOp",EDGE,"E1780.0.53"),sQuery(id+"F3.wireOp",EDGE,"E1780.0.54"),sQuery(id+"F3.wireOp",EDGE,"E1780.0.55")])],"isStart":true});
            var sketch = newSketch(context, id + "F7", { "sketchPlane" : qUnion([Q0])});
            skCircle(sketch, "E1783", {"center": v(0, 0) * mm, "radius": 34.27 * mm});
            skCircle(sketch, "E1784", {"center": v(0, 0) * mm, "radius": 27.27 * mm});
            skSolve(sketch);
        }
        {
            var Q0;
            Q0 = qSketchRegion(id + "F7", true);
            extrude(context, id + "F8", {"entities" : qUnion([Q0]), "operationType" : NewBodyOperationType.ADD, "oppositeDirection" : true, "depth" : (getVariable(context, 'idlerThick')) * mm, "offsetDistance" : 25 * mm});
        }
        {
            var Q0;
            Q0=makeQuery(id+"F8.opExtrude","CAP_EDGE",EDGE,{"disambiguationData":[OSD([sQuery(id+"F7.wireOp",EDGE,"E1783")])],"isStart":false});
            var Q1;
            Q1=makeQuery(id+"F6.opExtrude","CAP_EDGE",EDGE,{"disambiguationData":[OSD([sQuery(id+"F5.wireOp",EDGE,"E1781")])],"isStart":false});
            fillet(context, id + "F9", {"entities" : qUnion([Q0, Q1]), "radius" : (getVariable(context, 'filletSize')) * mm, "tangentPropagation" : true, "allowEdgeOverflow" : false});
        }
    });
